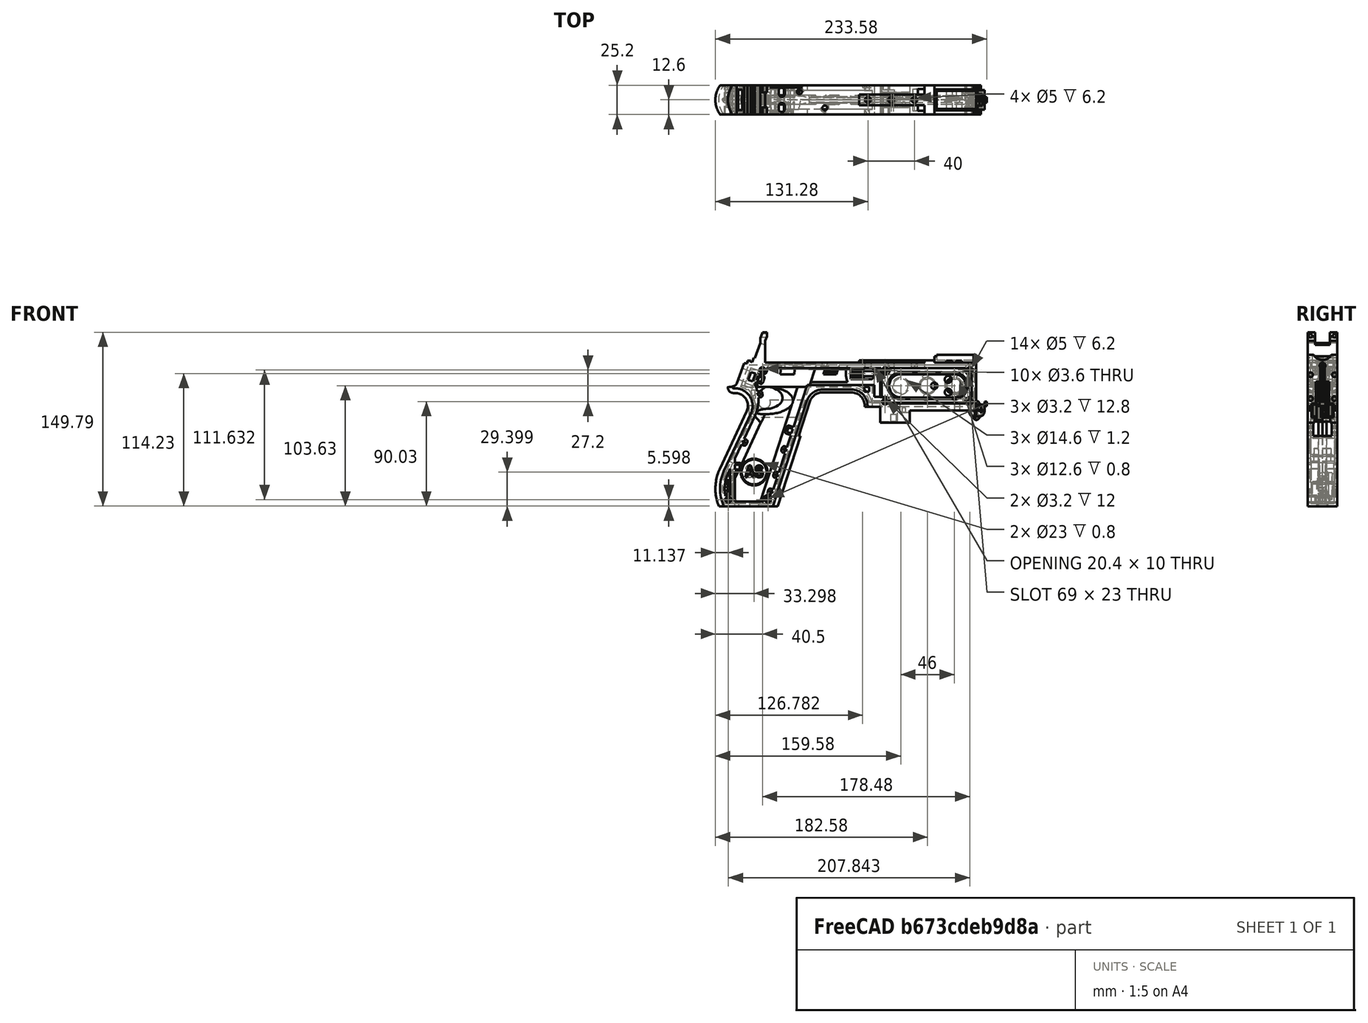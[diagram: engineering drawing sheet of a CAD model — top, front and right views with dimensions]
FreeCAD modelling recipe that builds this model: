
FCSTD DOCUMENT  (FreeCAD 1.0R39319 (Git))
Label: PICON-OF_ver_56
License: All rights reserved
LicenseURL: https://en.wikipedia.org/wiki/All_rights_reserved
objects: Sketcher::SketchObject×124, Part::Extrusion×63, Part::Cut×48, PartDesign::Pad×29, PartDesign::Pocket×21, PartDesign::Chamfer×15, PartDesign::Body×10, PartDesign::Fillet×6, Part::MultiFuse×5, Part::Part2DObjectPython×4, PartDesign::SubtractivePipe×4, PartDesign::SubtractiveLoft×4, PartDesign::Plane×3, PartDesign::SubShapeBinder×2, Part::Sweep×1, PartDesign::ShapeBinder×1, Mesh::Feature×1, PartDesign::Point×1, PartDesign::Groove×1
note: 626 computed .brp shape members not serialized (recipe doc carries the construction recipe); baked Part::Feature solids carry a one-line shape summary decoded from their .brp

FEATURE [Sketcher::SketchObject] Sketch  label="corpo principale"
  ArcFitTolerance = 1e-06
  AttacherType = Attacher::AttachEngine3D
  AttachmentSupport = -> [XZ_Plane]
  FullyConstrained = true
  MakeInternals = false
  MapMode = 5
  Placement = pos=(0,0,0) rot=(1,0,0;1.5708rad)
  sketch-geometry (65):
    g0: LineSegment StartX=0 StartY=0 StartZ=0 EndX=-57.2 EndY=0 EndZ=0
    g1: LineSegment StartX=-57.2 StartY=0 StartZ=0 EndX=-57.2 EndY=-10.4 EndZ=0
    g2: LineSegment StartX=-57.2 StartY=-10.4 StartZ=0 EndX=-82.8 EndY=-10.4 EndZ=0
    g3: LineSegment StartX=-82.8 StartY=-10.4 StartZ=0 EndX=-82.8 EndY=3.2 EndZ=0
    g4: LineSegment StartX=-82.8 StartY=3.2 StartZ=0 EndX=-93.6 EndY=3.2 EndZ=0
    g5: LineSegment StartX=-93.6 StartY=3.2 StartZ=0 EndX=-93.6 EndY=4 EndZ=0
    g6: LineSegment StartX=-107.6 StartY=18 StartZ=0 EndX=-132.428 EndY=18 EndZ=0
    g7: LineSegment StartX=-145.743 StartY=8.32624 StartZ=0 EndX=-175.232 EndY=-82.4316 EndZ=0
    g8: LineSegment StartX=-175.232 StartY=-82.4316 StartZ=0 EndX=-217.232 EndY=-82.4316 EndZ=0
    g9: LineSegment StartX=-217.232 StartY=-52.1862 StartZ=0 EndX=-193.988 EndY=-2.33927 EndZ=0
    g10: LineSegment StartX=-206.196 StartY=23.0857 StartZ=0 EndX=-199.861 EndY=40.4914 EndZ=0
    g11: LineSegment StartX=-199.861 StartY=40.4914 StartZ=0 EndX=-197.061 EndY=40.4914 EndZ=0
    g12: LineSegment StartX=-197.061 StartY=40.4914 StartZ=0 EndX=-197.061 EndY=42.8914 EndZ=0
    g13: LineSegment StartX=-197.061 StartY=42.8914 StartZ=0 EndX=-194.261 EndY=42.8914 EndZ=0
    g14: LineSegment StartX=-194.261 StartY=42.8914 StartZ=0 EndX=-194.535 EndY=42.1397 EndZ=0
    g15: LineSegment StartX=-194.535 StartY=42.1397 StartZ=0 EndX=-193.031 EndY=41.5924 EndZ=0
    g16: LineSegment StartX=-193.031 StartY=41.5924 StartZ=0 EndX=-191.663 EndY=45.3512 EndZ=0
    g17: LineSegment StartX=-191.663 StartY=45.3512 StartZ=0 EndX=-190.536 EndY=44.9408 EndZ=0
    g18: LineSegment StartX=-190.536 StartY=44.9408 StartZ=0 EndX=-185.747 EndY=58.0965 EndZ=0
    g19: LineSegment StartX=-185.747 StartY=58.0965 StartZ=0 EndX=-185.747 EndY=62.0965 EndZ=0
    g20: LineSegment StartX=-185.747 StartY=62.0965 StartZ=0 EndX=-183.832 EndY=67.3588 EndZ=0
    g21: LineSegment StartX=-183.832 StartY=67.3588 StartZ=0 EndX=-180.232 EndY=67.3588 EndZ=0
    g22: LineSegment StartX=-180.232 StartY=67.3588 StartZ=0 EndX=-180.232 EndY=63.7588 EndZ=0
    g23: LineSegment StartX=-180.232 StartY=63.7588 StartZ=0 EndX=-181.6 EndY=60 EndZ=0
    g24: LineSegment StartX=-181.6 StartY=60 StartZ=0 EndX=-181.6 EndY=41.2 EndZ=0
    g25: LineSegment StartX=-181.6 StartY=41.2 StartZ=0 EndX=-100.8 EndY=41.2 EndZ=0
    g26: LineSegment StartX=-36 StartY=43.2 StartZ=0 EndX=-36 EndY=41.2 EndZ=0
    g27: LineSegment StartX=0 StartY=48 StartZ=0 EndX=0 EndY=0 EndZ=0
    g28: LineSegment StartX=-209.901 StartY=19.85 StartZ=0 EndX=-209.901 EndY=20.1 EndZ=0
    g29: LineSegment StartX=-208.001 StartY=22 StartZ=0 EndX=-207.747 EndY=22 EndZ=0
    g30: LineSegment StartX=-207.583 StartY=19 StartZ=0 EndX=-209.051 EndY=19 EndZ=0
    g31: ArcOfCircle CenterX=-208.001 CenterY=20.1 CenterZ=0 NormalX=0 NormalY=0 NormalZ=1 AngleXU=0 Radius=1.9 StartAngle=1.5708 EndAngle=3.14159
    g32: GeomPoint [constr] X=-209.901 Y=22 Z=0
    g33: ArcOfCircle CenterX=-209.051 CenterY=19.85 CenterZ=0 NormalX=0 NormalY=0 NormalZ=1 AngleXU=0 Radius=0.85 StartAngle=3.14159 EndAngle=4.71239
    g34: GeomPoint [constr] X=-209.901 Y=19 Z=0
    g35: ArcOfCircle CenterX=-207.747 CenterY=23.65 CenterZ=0 NormalX=0 NormalY=0 NormalZ=1 AngleXU=0 Radius=1.65 StartAngle=4.71239 EndAngle=5.93412
    g36: GeomPoint [constr] X=-206.591 Y=22 Z=0
    g37: LineSegment StartX=-4 StartY=6 StartZ=0 EndX=-4 EndY=36.4 EndZ=0
    g38: LineSegment StartX=-4 StartY=36.4 StartZ=0 EndX=-185.2 EndY=36.4 EndZ=0
    g39: LineSegment StartX=-185.2 StartY=36.4 StartZ=0 EndX=-190.441 EndY=22 EndZ=0
    g40: LineSegment StartX=-214.575 StartY=-78.4316 StartZ=0 EndX=-178.142 EndY=-78.4316 EndZ=0
    g41: LineSegment StartX=-178.142 StartY=-78.4316 StartZ=0 EndX=-145.51 EndY=22 EndZ=0
    g42: LineSegment StartX=-145.51 StartY=22 StartZ=0 EndX=-87.91 EndY=22 EndZ=0
    g43: LineSegment StartX=-87.91 StartY=22 StartZ=0 EndX=-87.91 EndY=11.6 EndZ=0
    g44: LineSegment StartX=-87.91 StartY=11.6 StartZ=0 EndX=-80.11 EndY=11.6 EndZ=0
    g45: LineSegment StartX=-80.11 StartY=11.6 StartZ=0 EndX=-80.11 EndY=6 EndZ=0
    g46: LineSegment StartX=-80.11 StartY=6 StartZ=0 EndX=-4 EndY=6 EndZ=0
    g47: LineSegment StartX=-190.363 StartY=-4.02975 StartZ=0 EndX=-213.607 EndY=-53.8767 EndZ=0
    g48: ArcOfCircle CenterX=-132.428 CenterY=4 CenterZ=0 NormalX=0 NormalY=0 NormalZ=1 AngleXU=0 Radius=14 StartAngle=1.5708 EndAngle=2.82743
    g49: GeomPoint [constr] X=-142.6 Y=18 Z=0
    g50: ArcOfCircle CenterX=-107.6 CenterY=4 CenterZ=0 NormalX=0 NormalY=0 NormalZ=1 AngleXU=0 Radius=14 StartAngle=0 EndAngle=1.5708
    g51: GeomPoint [constr] X=-93.6 Y=18 Z=0
    g52: ArcOfCircle CenterX=-184.801 CenterY=-67.3089 CenterZ=0 NormalX=0 NormalY=0 NormalZ=1 AngleXU=0 Radius=35.7833 StartAngle=2.70526 EndAngle=3.57792
    g53: ArcOfCircle CenterX=-207.583 CenterY=4 CenterZ=0 NormalX=0 NormalY=0 NormalZ=1 AngleXU=0 Radius=15 StartAngle=5.84685 EndAngle=7.85398
    g54: LineSegment [constr] StartX=-213.607 StartY=-53.8767 StartZ=0 EndX=-217.232 EndY=-52.1862 EndZ=0
    g55: ArcOfCircle CenterX=-184.801 CenterY=-67.3089 CenterZ=0 NormalX=0 NormalY=0 NormalZ=1 AngleXU=0 Radius=31.7833 StartAngle=2.70526 EndAngle=3.49911
    g56: ArcOfCircle CenterX=-218.095 CenterY=8.90192 CenterZ=0 NormalX=0 NormalY=0 NormalZ=1 AngleXU=0 Radius=30.5989 StartAngle=5.84685 EndAngle=6.72553
    g57: LineSegment StartX=-44.6 StartY=43.2 StartZ=0 EndX=-36 EndY=43.2 EndZ=0
    g58: LineSegment StartX=-100.8 StartY=41.2 StartZ=0 EndX=-44.6 EndY=41.2 EndZ=0
    g59: LineSegment StartX=-44.6 StartY=41.2 StartZ=0 EndX=-44.6 EndY=43.2 EndZ=0
    g60: LineSegment StartX=-2.4 StartY=48 StartZ=0 EndX=0 EndY=48 EndZ=0
    g61: LineSegment StartX=-36 StartY=41.2 StartZ=0 EndX=-2.4 EndY=41.2 EndZ=0
    g62: LineSegment StartX=-2.4 StartY=41.2 StartZ=0 EndX=-2.4 EndY=48 EndZ=0
    g63: LineSegment [constr] StartX=-181.6 StartY=36.4 StartZ=0 EndX=-152.209 EndY=36.4 EndZ=0
    g64: LineSegment [constr] StartX=-181.6 StartY=36.4 StartZ=0 EndX=-130.41 EndY=36.4 EndZ=0
  constraints (183):
    c: Coincident(g-1,g0)
    c: PointOnObject(g0,g-1)
    c: Coincident(g0,g1)
    c: Vertical(g1)
    c: Coincident(g1,g2)
    c: Horizontal(g2)
    c: Coincident(g2,g3)
    c: Vertical(g3)
    c: Coincident(g3,g4)
    c: Coincident(g4,g5)
    c: Vertical(g5)
    c: Horizontal(g6)
    c: Coincident(g7,g8)
    c: Horizontal(g8)
    c: Coincident(g10,g11)
    c: Horizontal(g11)
    c: Coincident(g11,g12)
    c: Vertical(g12)
    c: Coincident(g12,g13)
    c: Horizontal(g13)
    c: Coincident(g13,g14)
    c: Coincident(g14,g15)
    c: Coincident(g15,g16)
    c: Coincident(g16,g17)
    c: Coincident(g17,g18)
    c: Coincident(g18,g19)
    c: Vertical(g19)
    c: Coincident(g19,g20)
    c: Coincident(g20,g21)
    c: Horizontal(g21)
    c: Coincident(g21,g22)
    c: Vertical(g22)
    c: Coincident(g22,g23)
    c: Coincident(g23,g24)
    c: Vertical(g24)
    c: Coincident(g24,g25)
    c: Horizontal(g25)
    c: Coincident(g57,g26)
    c: Vertical(g26)
    c: Coincident(g26,g61)
    c: PointOnObject(g60,g-2)
    c: Coincident(g60,g27)
    c: Coincident(g27,g0)
    c: DistanceY(g27,g27) = 48
    c: DistanceY(g1,g1) = 10.4
    c: DistanceX(g0,g0) = 57.2
    c: DistanceX(g2,g2) = 25.6
    c: Horizontal(g4)
    c: DistanceY(g3,g3) = 13.6
    c: DistanceX(g4,g4) = 10.8
    c: DistanceY(g5,g51) = 14.8
    c: DistanceX(g49,g51) = 49
    c: Distance(g7,g49) = 105.6
    c: DistanceX(g61,g60) = 36
    c: DistanceX(g25,g25) = 80.8
    c: DistanceY(g24,g24) = 18.8
    c: DistanceY(g22,g22) = 3.6
    c: Distance(g23) = 4
    c: Angle(g-1,g23) = 1.22173
    c: DistanceX(g21,g21) = 3.6
    c: Distance(g20) = 5.6
    c: Angle(g-1,g20) = 1.22173
    c: DistanceY(g19,g19) = 4
    c: Distance(g18) = 14
    c: Angle(g-1,g18) = 1.22173
    c: Distance(g17) = 1.2
    c: Distance(g16) = 4
    c: Angle(g16) = 1.22173
    c: Perpendicular(g18,g17)
    c: Distance(g15) = 1.6
    c: Perpendicular(g16,g15)
    c: Distance(g14) = 0.8
    c: DistanceX(g13,g13) = 2.8
    c: Perpendicular(g15,g14)
    c: DistanceY(g12,g12) = 2.4
    c: DistanceX(g11,g11) = 2.8
    c: Distance(g9) = 55
    c: Angle(g9,g-1) = 2.00713
    c: Horizontal(g29)
    c: Vertical(g28)
    c: Horizontal(g30)
    c: PointOnObject(g32,g29)
    c: PointOnObject(g32,g28)
    c: Tangent(g29,g31) = 1.5708
    c: Tangent(g28,g31) = 1.5708
    c: PointOnObject(g34,g28)
    c: PointOnObject(g34,g30)
    c: Tangent(g28,g33) = 1.5708
    c: Tangent(g30,g33) = 1.5708
    c: PointOnObject(g36,g29)
    c: PointOnObject(g36,g10)
    c: Tangent(g29,g35) = -1.5708
    c: Tangent(g10,g35) = -1.5708
    c: Angle(g-1,g10) = 1.22173
    c: Radius(g35) = 1.65
    c: Vertical(g37)
    c: Coincident(g37,g38)
    c: Horizontal(g38)
    c: Coincident(g38,g39)
    c: Horizontal(g40)
    c: Coincident(g40,g41)
    c: Coincident(g41,g42)
    c: Horizontal(g42)
    c: Coincident(g42,g43)
    c: Vertical(g43)
    c: Coincident(g43,g44)
    c: Horizontal(g44)
    c: Coincident(g44,g45)
    c: Vertical(g45)
    c: Coincident(g45,g46)
    c: Coincident(g46,g37)
    c: Horizontal(g46)
    c: DistanceY(g0,g37) = 6
    c: DistanceX(g37,g0) = 4
    c: DistanceY(g37,g25) = 4.8
    c: DistanceX(g38,g38) = 181.2
    c: DistanceX(g42,g42) = 57.6
    c: DistanceY(g49,g41) = 4
    c: DistanceX(g41,g49) = 2.91
    c: DistanceY(g43,g43) = 10.4
    c: DistanceX(g44,g44) = 7.8
    c: DistanceY(g7,g40) = 4
    c: Distance(g47) = 55
    c: Angle(g-1,g39) = 1.22173
    c: PointOnObject(g49,g7)
    c: PointOnObject(g49,g6)
    c: Tangent(g7,g48) = -1.5708
    c: Tangent(g6,g48) = -1.5708
    c: PointOnObject(g51,g5)
    c: PointOnObject(g51,g6)
    c: Tangent(g5,g50) = -1.5708
    c: Tangent(g6,g50) = -1.5708
    c: Radius(g50) = 14
    c: Radius(g48) = 14
    c: DistanceX(g8,g8) = 42
    c: Angle(g7,g-1) = 1.88496
    c: Parallel(g41,g7)
    c: Parallel(g47,g9)
    c: Coincident(g52,g8)
    c: Tangent(g52,g9) = 1.5708
    c: DistanceX(g9,g8) = 0
    c: Tangent(g53,g9) = -1.5708
    c: Tangent(g53,g30) = -1.5708
    c: Diameter(g53) = 30
    c: DistanceY(g53,g0) = -4
    c: Coincident(g54,g47)
    c: Distance(g54) = 4
    c: Coincident(g54,g9)
    c: Coincident(g55,g40)
    c: Tangent(g55,g47) = -1.5708
    c: Coincident(g52,g55)
    c: Coincident(g56,g39)
    c: Tangent(g56,g47) = 1.5708
    c: Horizontal(g57)
    c: DistanceX(g57,g57) = 8.6
    c: Coincident(g58,g25)
    c: Horizontal(g58)
    c: Coincident(g59,g58)
    c: Vertical(g59)
    c: DistanceY(g58,g57) = 2
    c: DistanceX(g58,g58) = 56.2
    c: Coincident(g59,g57)
    c: DistanceY(g41,g36) = 0
    c: DistanceY(g36,g39) = 0
    c: DistanceY(g28,g28) = 0.25
    c: DistanceX(g30,g36) = 2.46
    c: DistanceX(g28,g29) = 1.9
    c: Coincident(g62,g60)
    c: Horizontal(g60)
    c: DistanceX(g62,g27) = 2.4
    c: Coincident(g61,g62)
    c: DistanceY(g26,g26) = 2
    c: Vertical(g62)
    c: DistanceY(g61,g60) = 6.8
    c: Horizontal(g61)
    c: Distance(g63) = 29.391
    c: PointOnObject(g63,g38)
    c: PointOnObject(g63,g38)
    c: Distance(g64) = 51.19
    c: PointOnObject(g64,g38)
    c: PointOnObject(g64,g38)
    c: DistanceX(g24,g63) = 0
    c: DistanceX(g24,g64) = 0
FEATURE [Part::Extrusion] Extrude  label="Extrude corpo principale"
  Base = -> Sketch
  Dir = (0,-1,2e-16)
  DirMode = 2
  FaceMakerClass = Part::FaceMakerBullseye
  FaceMakerMode = 3
  LengthFwd = 25.2
  LengthRev = 12.6
  Solid = true
  Symmetric = true
FEATURE [Sketcher::SketchObject] Sketch002  label="scavo grilletto"
  ArcFitTolerance = 1e-06
  AttachmentSupport = -> [XZ_Plane]
  ExternalGeometry = -> [Sketch]
  FullyConstrained = true
  MakeInternals = false
  MapMode = 5
  Placement = pos=(0,0,0) rot=(1,0,0;1.5708rad)
  sketch-geometry (4):
    g0: LineSegment StartX=-89.51 StartY=22 StartZ=0 EndX=-152.71 EndY=22 EndZ=0
    g1: LineSegment StartX=-152.71 StartY=22 StartZ=0 EndX=-167.006 EndY=-22 EndZ=0
    g2: LineSegment StartX=-167.006 StartY=-22 StartZ=0 EndX=-89.51 EndY=-22 EndZ=0
    g3: LineSegment StartX=-89.51 StartY=-22 StartZ=0 EndX=-89.51 EndY=22 EndZ=0
  constraints (12):
    c: Horizontal(g0)
    c: Coincident(g0,g1)
    c: Coincident(g1,g2)
    c: Horizontal(g2)
    c: Coincident(g2,g3)
    c: Coincident(g3,g0)
    c: Vertical(g3)
    c: Angle(g1,g0) = 1.88496
    c: DistanceY(g3,g3) = 44
    c: DistanceX(g0,g0) = 63.2
    c: DistanceX(g0,g-3) = 1.6
    c: DistanceY(g-3,g0) = 0
FEATURE [Sketcher::SketchObject] Sketch004  label="traiettoria arrotondamento impugnatura anteriore"
  ArcFitTolerance = 1e-06
  AttachmentSupport = -> [XZ_Plane]
  ExternalGeometry = -> [Sketch]
  FullyConstrained = true
  MakeInternals = false
  MapMode = 5
  Placement = pos=(0,0,0) rot=(1,0,0;1.5708rad)
  sketch-geometry (13):
    g0: LineSegment StartX=-175.232 StartY=-82.4316 StartZ=0 EndX=-145.743 EndY=8.32624 EndZ=0
    g1: LineSegment StartX=-93.6 StartY=3.2 StartZ=0 EndX=-93.6 EndY=4 EndZ=0
    g2: LineSegment StartX=-132.428 StartY=18 StartZ=0 EndX=-107.6 EndY=18 EndZ=0
    g3: ArcOfCircle CenterX=-132.428 CenterY=4 CenterZ=0 NormalX=0 NormalY=0 NormalZ=1 AngleXU=0 Radius=14 StartAngle=1.5708 EndAngle=2.82743
    g4: ArcOfCircle CenterX=-107.6 CenterY=4 CenterZ=0 NormalX=0 NormalY=0 NormalZ=1 AngleXU=0 Radius=14 StartAngle=0 EndAngle=1.5708
    g5: LineSegment StartX=-175.232 StartY=-82.4316 StartZ=0 EndX=-217.232 EndY=-82.4316 EndZ=0
    g6: LineSegment StartX=-217.232 StartY=-52.1862 StartZ=0 EndX=-193.988 EndY=-2.33927 EndZ=0
    g7: LineSegment StartX=-209.051 StartY=19 StartZ=0 EndX=-207.583 EndY=19 EndZ=0
    g8: LineSegment StartX=-209.901 StartY=20.1 StartZ=0 EndX=-209.901 EndY=19.85 EndZ=0
    g9: ArcOfCircle CenterX=-184.801 CenterY=-67.3089 CenterZ=0 NormalX=0 NormalY=0 NormalZ=1 AngleXU=0 Radius=35.7833 StartAngle=2.70526 EndAngle=3.57792
    g10: ArcOfCircle CenterX=-207.583 CenterY=4 CenterZ=0 NormalX=0 NormalY=0 NormalZ=1 AngleXU=0 Radius=15 StartAngle=5.84685 EndAngle=7.85398
    g11: ArcOfCircle CenterX=-209.051 CenterY=19.85 CenterZ=0 NormalX=0 NormalY=0 NormalZ=1 AngleXU=0 Radius=0.85 StartAngle=3.14159 EndAngle=4.71239
    g12: ArcOfCircle CenterX=-208.001 CenterY=20.1 CenterZ=0 NormalX=0 NormalY=0 NormalZ=1 AngleXU=0 Radius=1.9 StartAngle=1.5708 EndAngle=3.14159
  constraints (26):
    c: Coincident(g0,g-3)
    c: Coincident(g0,g-6)
    c: Coincident(g1,g-8)
    c: Coincident(g1,g-7)
    c: Coincident(g2,g-5)
    c: Coincident(g2,g-4)
    c: Coincident(g3,g2)
    c: Tangent(g3,g0) = 1.5708
    c: Coincident(g4,g1)
    c: Tangent(g4,g2) = 1.5708
    c: Coincident(g5,g0)
    c: Coincident(g5,g-9)
    c: Coincident(g6,g-12)
    c: Coincident(g6,g-11)
    c: Coincident(g7,g-15)
    c: Coincident(g7,g-14)
    c: Coincident(g8,g-16)
    c: Coincident(g8,g-17)
    c: Tangent(g9,g6) = 1.5708
    c: Coincident(g9,g5)
    c: Coincident(g10,g7)
    c: Tangent(g10,g6) = -1.5708
    c: Tangent(g11,g7) = -1.5708
    c: Coincident(g11,g8)
    c: Tangent(g12,g8) = -1.5708
    c: Coincident(g12,g-17)
FEATURE [PartDesign::Plane] DatumPlane  label="Piano per disegno arrotondamento impugnatura"
  AttachmentSupport = -> [Sketch]
  Length = 73.6581
  MapMode = 7
  Placement = pos=(-145.743,1.8e-15,8.32624) rot=(0.154555,0.154555,0.97582;1.59527rad)
  ResizeMode = 0
  Width = 303.511
FEATURE [Sketcher::SketchObject] Sketch005  label="forma arrotondamento impugnatura anteriore"
  ArcFitTolerance = 1e-06
  AttachmentSupport = -> [DatumPlane]
  FullyConstrained = true
  MakeInternals = false
  MapMode = 5
  Placement = pos=(-145.743,1.8e-15,8.32624) rot=(0.154555,0.154555,0.97582;1.59527rad)
  sketch-geometry (5):
    g0: GeomPoint [constr] X=0 Y=-4 Z=0
    g1: GeomPoint [constr] X=-12.6 Y=7.1e-15 Z=0
    g2: GeomPoint [constr] X=12.6 Y=4.97e-14 Z=0
    g3: LineSegment StartX=-12.6 StartY=7.1e-15 StartZ=0 EndX=12.6 EndY=4.97e-14 EndZ=0
    g4: ArcOfCircle CenterX=-3.88e-14 CenterY=17.845 CenterZ=0 NormalX=0 NormalY=0 NormalZ=1 AngleXU=0 Radius=21.845 StartAngle=4.09759 EndAngle=5.32718
  constraints (11):
    c: DistanceY(g0,g-1) = 4
    c: DistanceX(g-1,g0) = 0
    c: DistanceX(g1,g-1) = 12.6
    c: DistanceX(g-1,g2) = 12.6
    c: DistanceY(g-1,g2) = 0
    c: DistanceY(g-1,g1) = 0
    c: Coincident(g3,g1)
    c: Coincident(g3,g2)
    c: Coincident(g4,g1)
    c: Coincident(g4,g2)
    c: PointOnObject(g0,g4)
FEATURE [Part::Sweep] Sweep  label="Sweep impugnatura"
  Frenet = true
  Sections = -> [Sketch005]
  Solid = true
  Spine = -> Sketch [Edge32,Edge33,Edge34,Edge35,Edge36,Edge37,Edge38,Edge39,Edge40,Edge41,Edge42,Edge43,Edge44]
  Transition = 1
FEATURE [Sketcher::SketchObject] Sketch008  label="buchi e pulizie varie"
  ArcFitTolerance = 1e-06
  AttachmentSupport = -> [XZ_Plane]
  ExternalGeometry = -> [Sketch]
  FullyConstrained = true
  MakeInternals = false
  MapMode = 5
  Placement = pos=(0,0,0) rot=(1,0,0;1.5708rad)
  sketch-geometry (26):
    g0: LineSegment StartX=-96.278 StartY=20.155 StartZ=0 EndX=-92.278 EndY=20.155 EndZ=0
    g1: LineSegment StartX=-92.278 StartY=20.155 StartZ=0 EndX=-92.278 EndY=16.155 EndZ=0
    g2: LineSegment StartX=-92.278 StartY=16.155 StartZ=0 EndX=-96.278 EndY=16.155 EndZ=0
    g3: LineSegment StartX=-96.278 StartY=16.155 StartZ=0 EndX=-96.278 EndY=20.155 EndZ=0
    g4: LineSegment StartX=-222.232 StartY=-82.4316 StartZ=0 EndX=-170.232 EndY=-82.4316 EndZ=0
    g5: LineSegment StartX=-170.232 StartY=-82.4316 StartZ=0 EndX=-170.232 EndY=-86.4316 EndZ=0
    g6: LineSegment StartX=-170.232 StartY=-86.4316 StartZ=0 EndX=-222.232 EndY=-86.4316 EndZ=0
    g7: LineSegment StartX=-222.232 StartY=-86.4316 StartZ=0 EndX=-222.232 EndY=-82.4316 EndZ=0
    g8: LineSegment StartX=-213.901 StartY=20.1 StartZ=0 EndX=-213.901 EndY=26 EndZ=0
    g9: LineSegment StartX=-213.901 StartY=26 StartZ=0 EndX=-206.196 EndY=26 EndZ=0
    g10: LineSegment StartX=-17.4 StartY=42.8 StartZ=0 EndX=-12.4 EndY=42.8 EndZ=0
    g11: LineSegment StartX=-12.4 StartY=42.8 StartZ=0 EndX=-12.4 EndY=41.2 EndZ=0
    g12: LineSegment StartX=-12.4 StartY=41.2 StartZ=0 EndX=-17.4 EndY=41.2 EndZ=0
    g13: LineSegment StartX=-17.4 StartY=41.2 StartZ=0 EndX=-17.4 EndY=42.8 EndZ=0
    g14: LineSegment StartX=-25.9 StartY=42.8 StartZ=0 EndX=-20.9 EndY=42.8 EndZ=0
    g15: LineSegment StartX=-20.9 StartY=42.8 StartZ=0 EndX=-20.9 EndY=41.2 EndZ=0
    g16: LineSegment StartX=-20.9 StartY=41.2 StartZ=0 EndX=-25.9 EndY=41.2 EndZ=0
    g17: LineSegment StartX=-25.9 StartY=41.2 StartZ=0 EndX=-25.9 EndY=42.8 EndZ=0
    g18: GeomPoint [constr] X=-206.196 Y=23.0857 Z=0
    g19: GeomPoint [constr] X=-213.901 Y=20.1 Z=0
    g20: BSplineCurve PolesCount=4 KnotsCount=2 Degree=3 IsPeriodic=0
    g21-g24: Circle [constr] x4 (B-spline internal-alignment scaffolding for g20; pole/knot coordinates omitted)
    g25: LineSegment StartX=-206.196 StartY=26 StartZ=0 EndX=-206.196 EndY=23.0857 EndZ=0
  constraints (73):
    c: Horizontal(g0)
    c: Coincident(g1,g0)
    c: Vertical(g1)
    c: Coincident(g2,g1)
    c: Horizontal(g2)
    c: Coincident(g3,g2)
    c: Coincident(g3,g0)
    c: Vertical(g3)
    c: DistanceX(g0,g-4) = 4.368
    c: DistanceY(g0,g-4) = 1.845
    c: DistanceY(g1,g1) = 4
    c: DistanceX(g2,g2) = 4
    c: Horizontal(g4)
    c: Coincident(g5,g4)
    c: Vertical(g5)
    c: Coincident(g6,g5)
    c: Horizontal(g6)
    c: Coincident(g7,g6)
    c: Coincident(g7,g4)
    c: Vertical(g7)
    c: DistanceY(g7,g7) = 4
    c: DistanceX(g4,g-5) = 5
    c: DistanceX(g-5,g4) = 5
    c: DistanceY(g4,g-5) = 0
    c: Coincident(g9,g8)
    c: Parallel(g9,g-6)
    c: DistanceX(g8,g-8) = 4
    c: Horizontal(g10)
    c: Coincident(g11,g10)
    c: Vertical(g11)
    c: Coincident(g12,g11)
    c: Horizontal(g12)
    c: Coincident(g13,g12)
    c: Coincident(g13,g10)
    c: Vertical(g13)
    c: Horizontal(g14)
    c: Coincident(g15,g14)
    c: Vertical(g15)
    c: Coincident(g16,g15)
    c: Horizontal(g16)
    c: Coincident(g17,g16)
    c: Coincident(g17,g14)
    c: Vertical(g17)
    c: DistanceY(g11,g10) = 1.6
    c: DistanceX(g10,g10) = 5
    c: DistanceY(g15,g14) = 1.6
    c: DistanceX(g14,g14) = 5
    c: DistanceX(g15,g12) = 3.5
    c: DistanceX(g11,g-9) = 10
    c: DistanceY(g-9,g11) = 0
    c: DistanceY(g-9,g15) = 0
    c: Perpendicular(g8,g9)
    c: DistanceY(g-7,g9) = 4
    c: DistanceY(g8,g-8) = 0
    c: InternalAlignment(g18,g20)
    c: InternalAlignment(g19,g20)
    c: InternalAlignment(g21,g20)
    c: Weight(g21) = 1
    c: InternalAlignment(g22,g20)
    c: Equal(g22,g21)
    c: InternalAlignment(g23,g20)
    c: Equal(g23,g21)
    c: InternalAlignment(g24,g20)
    c: Equal(g24,g21)
    c: Coincident(g18,g-12)
    c: Coincident(g19,g8)
    c: Coincident(g25,g9)
    c: Coincident(g25,g20)
    c: Vertical(g25)
    c: DistanceY(g20,g23) = 0
    c: DistanceY(g22,g18) = 2.26
    c: DistanceX(g22,g18) = 0.93
    c: DistanceX(g20,g23) = 2.9
FEATURE [Part::Extrusion] Extrude004  label="Extrude Buchi e pulizie varie"
  Base = -> Sketch008
  Dir = (0,-1,2e-16)
  DirMode = 2
  FaceMakerClass = Part::FaceMakerBullseye
  FaceMakerMode = 3
  LengthFwd = 25.2
  LengthRev = 0
  Solid = true
  Symmetric = true
FEATURE [Sketcher::SketchObject] Sketch009  label="rinforzi"
  ArcFitTolerance = 1e-06
  AttachmentSupport = -> [XZ_Plane]
  ExternalGeometry = -> [Sketch]
  FullyConstrained = true
  MakeInternals = false
  MapMode = 5
  Placement = pos=(0,0,0) rot=(1,0,0;1.5708rad)
  sketch-geometry (9):
    g0: LineSegment StartX=-87.91 StartY=22 StartZ=0 EndX=-87.91 EndY=36.4 EndZ=0
    g1: LineSegment StartX=-87.91 StartY=36.4 StartZ=0 EndX=-97.91 EndY=36.4 EndZ=0
    g2: LineSegment StartX=-97.91 StartY=36.4 StartZ=0 EndX=-97.91 EndY=22 EndZ=0
    g3: LineSegment StartX=-97.91 StartY=22 StartZ=0 EndX=-87.91 EndY=22 EndZ=0
    g4: LineSegment StartX=-149.713 StartY=9.06563 StartZ=0 EndX=-154.586 EndY=-5.93437 EndZ=0
    g5: LineSegment StartX=-154.586 StartY=-5.93437 StartZ=0 EndX=-191.863 EndY=-5.93437 EndZ=0
    g6: LineSegment StartX=-191.863 StartY=-5.93437 StartZ=0 EndX=-191.863 EndY=9.06563 EndZ=0
    g7: LineSegment StartX=-191.863 StartY=9.06563 StartZ=0 EndX=-149.713 EndY=9.06563 EndZ=0
    g8: LineSegment [constr] StartX=-145.51 StartY=22 StartZ=0 EndX=-149.713 EndY=9.06563 EndZ=0
  constraints (25):
    c: Vertical(g0)
    c: Coincident(g1,g0)
    c: Horizontal(g1)
    c: Coincident(g2,g1)
    c: Vertical(g2)
    c: Coincident(g3,g2)
    c: Coincident(g3,g0)
    c: Horizontal(g3)
    c: Coincident(g0,g-4)
    c: DistanceX(g3,g3) = 10
    c: DistanceY(g0,g-3) = 0
    c: Coincident(g5,g4)
    c: Horizontal(g5)
    c: Coincident(g6,g5)
    c: Vertical(g6)
    c: Coincident(g7,g6)
    c: Coincident(g7,g4)
    c: Horizontal(g7)
    c: Distance(g8) = 13.6
    c: Parallel(g-6,g8)
    c: Coincident(g-6,g8)
    c: Parallel(g4,g-6)
    c: DistanceY(g4,g4) = 15
    c: Coincident(g4,g8)
    c: DistanceX(g-5,g5) = -1.5
FEATURE [Part::Extrusion] Extrude001  label="Extrude scavo grilletto"
  Base = -> Sketch002
  Dir = (0,-1,2e-16)
  DirMode = 2
  FaceMakerClass = Part::FaceMakerBullseye
  FaceMakerMode = 3
  LengthFwd = 16
  LengthRev = 0
  Solid = true
  Symmetric = true
FEATURE [Part::Extrusion] Extrude005  label="Extrude Rinforzi"
  Base = -> Sketch009
  Dir = (0,-1,2e-16)
  DirMode = 2
  FaceMakerClass = Part::FaceMakerBullseye
  FaceMakerMode = 3
  LengthFwd = 2
  LengthRev = 0
  Placement = pos=(0,12.6,0) rot=(0,0,1;0rad)
  Solid = true
  Symmetric = false
FEATURE [PartDesign::ShapeBinder] CopyCut
  TraceSupport = false
FEATURE [PartDesign::Plane] DatumPlane001
  AttachmentSupport = -> [CopyCut]
  Length = 283.944
  MapMode = 5
  Placement = pos=(0,12.6,0) rot=(0,0.707107,0.707107;3.14159rad)
  ResizeMode = 0
  Width = 188.15
FEATURE [Sketcher::SketchObject] Sketch010  label="buco neopixel"
  ArcFitTolerance = 1e-06
  AttachmentSupport = -> [XZ_Plane]
  ExternalGeometry = -> [Sketch]
  FullyConstrained = true
  MakeInternals = false
  MapMode = 5
  Placement = pos=(0,0,0) rot=(1,0,0;1.5708rad)
  sketch-geometry (5):
    g0: LineSegment [constr] StartX=-199.861 StartY=40.4914 StartZ=0 EndX=-201.368 EndY=36.3521 EndZ=0
    g1: LineSegment StartX=-201.368 StartY=36.3521 StartZ=0 EndX=-204.932 EndY=26.5605 EndZ=0
    g2: LineSegment StartX=-201.368 StartY=36.3521 StartZ=0 EndX=-180.2 EndY=28.6477 EndZ=0
    g3: LineSegment StartX=-180.2 StartY=28.6477 StartZ=0 EndX=-183.764 EndY=18.8561 EndZ=0
    g4: LineSegment StartX=-183.764 StartY=18.8561 StartZ=0 EndX=-204.932 EndY=26.5605 EndZ=0
  constraints (14):
    c: Parallel(g0,g-3)
    c: Distance(g0) = 4.405
    c: Coincident(g0,g-3)
    c: Coincident(g2,g1)
    c: Coincident(g3,g2)
    c: Coincident(g4,g3)
    c: Coincident(g4,g1)
    c: Parallel(g1,g-3)
    c: Distance(g1) = 10.42
    c: Coincident(g1,g0)
    c: Parallel(g2,g4)
    c: Perpendicular(g1,g2)
    c: DistanceX(g-4,g2) = 5
    c: Parallel(g3,g1)
FEATURE [Part::Extrusion] Extrude006  label="Extrude buco neopixel"
  Base = -> Sketch010
  Dir = (0,-1,2e-16)
  DirMode = 2
  FaceMakerClass = Part::FaceMakerBullseye
  FaceMakerMode = 3
  LengthFwd = 17.2
  LengthRev = 0
  Solid = true
  Symmetric = true
FEATURE [Sketcher::SketchObject] Sketch011  label="fermo grilletto"
  ArcFitTolerance = 1e-06
  AttachmentSupport = -> [XZ_Plane]
  ExternalGeometry = -> [Sketch]
  FullyConstrained = true
  MakeInternals = false
  MapMode = 5
  Placement = pos=(0,0,0) rot=(1,0,0;1.5708rad)
  sketch-geometry (18):
    g0: LineSegment [constr] StartX=-145.51 StartY=22 StartZ=0 EndX=-157.347 EndY=-14.4293 EndZ=0
    g1: LineSegment [constr] StartX=-157.347 StartY=-14.4293 StartZ=0 EndX=-157.841 EndY=-15.951 EndZ=0
    g2: LineSegment StartX=-161.151 StartY=-13.1932 StartZ=0 EndX=-155.825 EndY=-14.9237 EndZ=0
    g3: LineSegment StartX=-163.167 StartY=-14.2205 StartZ=0 EndX=-164.403 EndY=-18.0247 EndZ=0
    g4: LineSegment StartX=-163.376 StartY=-20.0408 StartZ=0 EndX=-158.05 EndY=-21.7713 EndZ=0
    g5: LineSegment StartX=-158.05 StartY=-21.7713 StartZ=0 EndX=-155.825 EndY=-14.9237 EndZ=0
    g6: LineSegment StartX=-161.645 StartY=-14.7149 StartZ=0 EndX=-157.841 EndY=-15.951 EndZ=0
    g7: LineSegment StartX=-157.841 StartY=-15.951 StartZ=0 EndX=-159.077 EndY=-19.7552 EndZ=0
    g8: LineSegment StartX=-159.077 StartY=-19.7552 StartZ=0 EndX=-162.881 EndY=-18.5191 EndZ=0
    g9: LineSegment StartX=-162.881 StartY=-18.5191 StartZ=0 EndX=-161.645 EndY=-14.7149 EndZ=0
    g10: LineSegment [constr] StartX=-161.645 StartY=-14.7149 StartZ=0 EndX=-161.151 EndY=-13.1932 EndZ=0
    g11: LineSegment [constr] StartX=-159.077 StartY=-19.7552 StartZ=0 EndX=-157.555 EndY=-20.2496 EndZ=0
    g12: LineSegment [constr] StartX=-159.077 StartY=-19.7552 StartZ=0 EndX=-159.572 EndY=-21.2769 EndZ=0
    g13: LineSegment [constr] StartX=-161.645 StartY=-14.7149 StartZ=0 EndX=-163.167 EndY=-14.2205 EndZ=0
    g14: ArcOfCircle CenterX=-161.645 CenterY=-14.7149 CenterZ=0 NormalX=0 NormalY=0 NormalZ=1 AngleXU=0 Radius=1.6 StartAngle=1.25664 EndAngle=2.82743
    g15: GeomPoint [constr] X=-162.673 Y=-12.6988 Z=0
    g16: ArcOfCircle CenterX=-162.881 CenterY=-18.5191 CenterZ=0 NormalX=0 NormalY=0 NormalZ=1 AngleXU=0 Radius=1.6 StartAngle=2.82743 EndAngle=4.39823
    g17: GeomPoint [constr] X=-164.897 Y=-19.5464 Z=0
  constraints (48):
    c: Parallel(g0,g-3)
    c: Distance(g0) = 38.304
    c: Coincident(g0,g-3)
    c: Parallel(g1,g-3)
    c: Distance(g1) = 1.6
    c: Coincident(g1,g0)
    c: Coincident(g5,g4)
    c: Coincident(g5,g2)
    c: Coincident(g7,g6)
    c: Coincident(g8,g7)
    c: Coincident(g9,g8)
    c: Coincident(g9,g6)
    c: Parallel(g7,g-3)
    c: Parallel(g9,g7)
    c: Perpendicular(g6,g7)
    c: Parallel(g6,g8)
    c: Distance(g6) = 4
    c: Distance(g9) = 4
    c: Parallel(g5,g7)
    c: Parallel(g9,g3)
    c: Parallel(g2,g6)
    c: Parallel(g4,g8)
    c: Parallel(g13,g6)
    c: Parallel(g10,g9)
    c: Parallel(g11,g8)
    c: Parallel(g12,g7)
    c: Distance(g10) = 1.6
    c: Distance(g13) = 1.6
    c: Distance(g12) = 1.6
    c: Distance(g11) = 1.6
    c: Coincident(g10,g6)
    c: Coincident(g13,g6)
    c: Coincident(g12,g7)
    c: Coincident(g11,g7)
    c: Distance(g10,g15) = 1.6
    c: Distance(g15,g13) = 1.6
    c: Distance(g4,g12) = 1.6
    c: Distance(g4,g11) = 1.6
    c: PointOnObject(g15,g2)
    c: Tangent(g3,g14) = -1.5708
    c: Tangent(g2,g14) = 1.5708
    c: PointOnObject(g17,g4)
    c: PointOnObject(g17,g3)
    c: Tangent(g4,g16) = -1.5708
    c: Tangent(g3,g16) = -1.5708
    c: Equal(g16,g14)
    c: Coincident(g16,g8)
    c: Coincident(g6,g1)
FEATURE [Part::Extrusion] Extrude007  label="Extrude fermo grilletto"
  Base = -> Sketch011
  Dir = (0,-1,2e-16)
  DirMode = 2
  FaceMakerClass = Part::FaceMakerBullseye
  FaceMakerMode = 3
  LengthFwd = 25.2
  LengthRev = 0
  Solid = true
  Symmetric = true
FEATURE [Sketcher::SketchObject] Sketch012  label="buco oled"
  ArcFitTolerance = 1e-06
  AttachmentSupport = -> [XZ_Plane]
  ExternalGeometry = -> [Sketch]
  FullyConstrained = true
  MakeInternals = false
  MapMode = 5
  Placement = pos=(0,0,0) rot=(1,0,0;1.5708rad)
  sketch-geometry (4):
    g0: LineSegment StartX=-185.747 StartY=58.0965 StartZ=0 EndX=-180.232 EndY=56.0891 EndZ=0
    g1: LineSegment StartX=-185.747 StartY=58.0965 StartZ=0 EndX=-185.747 EndY=67.3588 EndZ=0
    g2: LineSegment StartX=-185.747 StartY=67.3588 StartZ=0 EndX=-180.232 EndY=67.3588 EndZ=0
    g3: LineSegment StartX=-180.232 StartY=67.3588 StartZ=0 EndX=-180.232 EndY=56.0891 EndZ=0
  constraints (10):
    c: Coincident(g1,g0)
    c: Coincident(g2,g1)
    c: Coincident(g3,g2)
    c: Coincident(g3,g0)
    c: Parallel(g1,g-5)
    c: Perpendicular(g-3,g0)
    c: Parallel(g2,g-6)
    c: Parallel(g3,g-4)
    c: Coincident(g0,g-5)
    c: Coincident(g2,g-6)
FEATURE [Part::Extrusion] Extrude008  label="Extrude buco oled"
  Base = -> Sketch012
  Dir = (0,-1,2e-16)
  DirMode = 2
  FaceMakerClass = Part::FaceMakerBullseye
  FaceMakerMode = 3
  LengthFwd = 12.8
  LengthRev = 0
  Solid = true
  Symmetric = true
FEATURE [Sketcher::SketchObject] Sketch013  label="buco pompa"
  ArcFitTolerance = 1e-06
  AttachmentSupport = -> [XZ_Plane]
  ExternalGeometry = -> [Sketch]
  FullyConstrained = true
  MakeInternals = false
  MapMode = 5
  Placement = pos=(0,0,0) rot=(1,0,0;1.5708rad)
  sketch-geometry (8):
    g0: LineSegment StartX=-82.8 StartY=-10.4 StartZ=0 EndX=-82.8 EndY=-9.6 EndZ=0
    g1: LineSegment StartX=-82.8 StartY=-9.6 StartZ=0 EndX=-67.9 EndY=-9.6 EndZ=0
    g2: LineSegment StartX=-67.9 StartY=-9.6 StartZ=0 EndX=-67.9 EndY=6 EndZ=0
    g3: LineSegment StartX=-67.9 StartY=6 StartZ=0 EndX=-65.9 EndY=6 EndZ=0
    g4: LineSegment StartX=-65.9 StartY=6 StartZ=0 EndX=-65.9 EndY=-1.7 EndZ=0
    g5: LineSegment StartX=-65.9 StartY=-1.7 StartZ=0 EndX=-57.2 EndY=-1.7 EndZ=0
    g6: LineSegment StartX=-57.2 StartY=-1.7 StartZ=0 EndX=-57.2 EndY=-10.4 EndZ=0
    g7: LineSegment StartX=-57.2 StartY=-10.4 StartZ=0 EndX=-82.8 EndY=-10.4 EndZ=0
  constraints (22):
    c: Vertical(g0)
    c: Coincident(g1,g0)
    c: Horizontal(g1)
    c: Coincident(g2,g1)
    c: Vertical(g2)
    c: Coincident(g3,g2)
    c: Horizontal(g3)
    c: Coincident(g4,g3)
    c: Vertical(g4)
    c: Coincident(g5,g4)
    c: Horizontal(g5)
    c: Coincident(g6,g5)
    c: Vertical(g6)
    c: Coincident(g7,g6)
    c: Coincident(g7,g0)
    c: DistanceY(g0,g0) = 0.8
    c: DistanceY(g6,g6) = 8.7
    c: DistanceX(g1,g1) = 14.9
    c: DistanceX(g3,g3) = 2
    c: Coincident(g0,g-4)
    c: DistanceY(g2,g-6) = 0
    c: Coincident(g6,g-5)
FEATURE [Part::Extrusion] Extrude009  label="Extrude buco pompa"
  Base = -> Sketch013
  Dir = (0,-1,2e-16)
  DirMode = 2
  FaceMakerClass = Part::FaceMakerBullseye
  FaceMakerMode = 3
  LengthFwd = 13.2
  LengthRev = 0
  Solid = true
  Symmetric = true
FEATURE [Sketcher::SketchObject] Sketch014  label="buco frontale"
  ArcFitTolerance = 1e-06
  AttachmentSupport = -> [XZ_Plane]
  ExternalGeometry = -> [Sketch]
  FullyConstrained = true
  MakeInternals = false
  MapMode = 5
  Placement = pos=(0,0,0) rot=(1,0,0;1.5708rad)
  sketch-geometry (10):
    g0: LineSegment StartX=0 StartY=0 StartZ=0 EndX=0 EndY=24.671 EndZ=0
    g1: LineSegment StartX=0 StartY=24.671 StartZ=0 EndX=-4 EndY=24.671 EndZ=0
    g2: LineSegment StartX=-4 StartY=24.671 StartZ=0 EndX=-4 EndY=16 EndZ=0
    g3: LineSegment StartX=-4 StartY=16 StartZ=0 EndX=-2.4 EndY=16 EndZ=0
    g4: LineSegment StartX=-2.4 StartY=16 StartZ=0 EndX=-2.4 EndY=10 EndZ=0
    g5: LineSegment StartX=-2.4 StartY=10 StartZ=0 EndX=-12 EndY=10 EndZ=0
    g6: LineSegment StartX=-12 StartY=10 StartZ=0 EndX=-12 EndY=6 EndZ=0
    g7: LineSegment StartX=-12 StartY=6 StartZ=0 EndX=-2.4 EndY=6 EndZ=0
    g8: LineSegment StartX=-2.4 StartY=6 StartZ=0 EndX=-2.4 EndY=0 EndZ=0
    g9: LineSegment StartX=-2.4 StartY=0 StartZ=0 EndX=0 EndY=0 EndZ=0
  constraints (29):
    c: Vertical(g0)
    c: Coincident(g1,g0)
    c: Horizontal(g1)
    c: Coincident(g2,g1)
    c: Vertical(g2)
    c: Coincident(g3,g2)
    c: Horizontal(g3)
    c: Coincident(g4,g3)
    c: Vertical(g4)
    c: Coincident(g5,g4)
    c: Horizontal(g5)
    c: Coincident(g6,g5)
    c: Vertical(g6)
    c: Coincident(g7,g6)
    c: Coincident(g8,g7)
    c: Vertical(g8)
    c: Coincident(g9,g8)
    c: Coincident(g9,g0)
    c: Horizontal(g9)
    c: DistanceY(g0,g0) = 24.671
    c: Horizontal(g7)
    c: DistanceY(g6,g6) = 4
    c: DistanceY(g4,g4) = 6
    c: DistanceX(g9,g9) = 2.4
    c: Coincident(g0,g-1)
    c: DistanceY(g-3,g7) = 0
    c: DistanceX(g8,g4) = 0
    c: DistanceX(g-3,g1) = 0
    c: DistanceX(g6,g-3) = 8
FEATURE [Part::Extrusion] Extrude010  label="Extrude buco frontale"
  Base = -> Sketch014
  Dir = (0,-1,2e-16)
  DirMode = 2
  FaceMakerClass = Part::FaceMakerBullseye
  FaceMakerMode = 3
  LengthFwd = 11.2
  LengthRev = 0
  Solid = true
  Symmetric = true
FEATURE [Sketcher::SketchObject] Sketch015  label="guida rail"
  ArcFitTolerance = 1e-06
  AttachmentSupport = -> [XZ_Plane]
  ExternalGeometry = -> [Sketch]
  FullyConstrained = true
  MakeInternals = false
  MapMode = 5
  Placement = pos=(0,0,0) rot=(1,0,0;1.5708rad)
  sketch-geometry (4):
    g0: LineSegment StartX=-100.8 StartY=43.2 StartZ=0 EndX=-44.6 EndY=43.2 EndZ=0
    g1: LineSegment StartX=-44.6 StartY=43.2 StartZ=0 EndX=-44.6 EndY=41.2 EndZ=0
    g2: LineSegment StartX=-44.6 StartY=41.2 StartZ=0 EndX=-100.8 EndY=41.2 EndZ=0
    g3: LineSegment StartX=-100.8 StartY=41.2 StartZ=0 EndX=-100.8 EndY=43.2 EndZ=0
  constraints (9):
    c: Horizontal(g0)
    c: Coincident(g1,g0)
    c: Coincident(g2,g1)
    c: Coincident(g3,g2)
    c: Coincident(g3,g0)
    c: Vertical(g3)
    c: Coincident(g2,g-3)
    c: Coincident(g1,g-3)
    c: Coincident(g0,g-4)
FEATURE [Part::Extrusion] Extrude011  label="Extrude guida rail"
  Base = -> Sketch015
  Dir = (0,-1,2e-16)
  DirMode = 2
  FaceMakerClass = Part::FaceMakerBullseye
  FaceMakerMode = 3
  LengthFwd = 9
  LengthRev = 0
  Solid = true
  Symmetric = true
FEATURE [Sketcher::SketchObject] Sketch016  label="guide per coperture laterali"
  ArcFitTolerance = 1e-06
  AttachmentSupport = -> [XZ_Plane]
  ExternalGeometry = -> [Sketch]
  FullyConstrained = true
  MakeInternals = false
  MapMode = 5
  Placement = pos=(0,0,0) rot=(1,0,0;1.5708rad)
  sketch-geometry (14):
    g0: Circle CenterX=-5.6 CenterY=7.6 CenterZ=0 NormalX=0 NormalY=0 NormalZ=1 AngleXU=0 Radius=1.6
    g1: Circle CenterX=-5.6 CenterY=7.6 CenterZ=0 NormalX=0 NormalY=0 NormalZ=1 AngleXU=0 Radius=4
    g2: Circle CenterX=-5.6 CenterY=34.8 CenterZ=0 NormalX=0 NormalY=0 NormalZ=1 AngleXU=0 Radius=1.6
    g3: Circle CenterX=-5.6 CenterY=34.8 CenterZ=0 NormalX=0 NormalY=0 NormalZ=1 AngleXU=0 Radius=4
    g4: Circle CenterX=-184.08 CenterY=34.8 CenterZ=0 NormalX=0 NormalY=0 NormalZ=1 AngleXU=0 Radius=1.6
    g5: Circle CenterX=-184.08 CenterY=34.8 CenterZ=0 NormalX=0 NormalY=0 NormalZ=1 AngleXU=0 Radius=4
    g6: Circle CenterX=-179.305 CenterY=-76.8316 CenterZ=0 NormalX=0 NormalY=0 NormalZ=1 AngleXU=0 Radius=1.6
    g7: Circle CenterX=-179.305 CenterY=-76.8316 CenterZ=0 NormalX=0 NormalY=0 NormalZ=1 AngleXU=0 Radius=4
    g8: Circle CenterX=-213.443 CenterY=-76.8316 CenterZ=0 NormalX=0 NormalY=0 NormalZ=1 AngleXU=0 Radius=1.6
    g9: Circle CenterX=-213.443 CenterY=-76.8316 CenterZ=0 NormalX=0 NormalY=0 NormalZ=1 AngleXU=0 Radius=4
    g10: Circle CenterX=-78.51 CenterY=7.6 CenterZ=0 NormalX=0 NormalY=0 NormalZ=1 AngleXU=0 Radius=1.6
    g11: Circle CenterX=-78.51 CenterY=7.6 CenterZ=0 NormalX=0 NormalY=0 NormalZ=1 AngleXU=0 Radius=4
    g12: Circle CenterX=-78.51 CenterY=34.8 CenterZ=0 NormalX=0 NormalY=0 NormalZ=1 AngleXU=0 Radius=1.6
    g13: Circle CenterX=-78.51 CenterY=34.8 CenterZ=0 NormalX=0 NormalY=0 NormalZ=1 AngleXU=0 Radius=4
  constraints (35):
    c: Diameter(g0) = 3.2
    c: Diameter(g1) = 8
    c: Coincident(g0,g1)
    c: Diameter(g2) = 3.2
    c: Diameter(g3) = 8
    c: Coincident(g3,g2)
    c: Tangent(g2,g-7)
    c: Diameter(g4) = 3.2
    c: Diameter(g5) = 8
    c: Coincident(g5,g4)
    c: Tangent(g4,g-7)
    c: Tangent(g4,g-8)
    c: Diameter(g6) = 3.2
    c: Diameter(g7) = 8
    c: Coincident(g7,g6)
    c: Tangent(g6,g-9)
    c: Tangent(g6,g-10)
    c: Diameter(g8) = 3.2
    c: Diameter(g9) = 8
    c: Coincident(g9,g8)
    c: Tangent(g8,g-10)
    c: Tangent(g8,g-11)
    c: Diameter(g10) = 3.2
    c: Diameter(g11) = 8
    c: Diameter(g12) = 3.2
    c: Diameter(g13) = 8
    c: Coincident(g12,g13)
    c: Coincident(g10,g11)
    c: Tangent(g12,g-7)
    c: DistanceX(g12,g10) = 0
    c: Tangent(g2,g-6)
    c: Tangent(g0,g-6)
    c: Tangent(g0,g-3)
    c: Tangent(g10,g-3)
    c: Tangent(g10,g-4)
FEATURE [Part::Extrusion] Extrude012  label="extrude guide per coperture laterali"
  Base = -> Sketch016
  Dir = (0,-1,2e-16)
  DirMode = 2
  FaceMakerClass = Part::FaceMakerBullseye
  FaceMakerMode = 3
  LengthFwd = 25.2
  LengthRev = 0
  Solid = true
  Symmetric = true
FEATURE [Sketcher::SketchObject] Sketch017  label="supporto CAM"
  ArcFitTolerance = 1e-06
  AttachmentSupport = -> [XZ_Plane]
  ExternalGeometry = -> [Sketch]
  FullyConstrained = true
  MakeInternals = false
  MapMode = 5
  Placement = pos=(0,0,0) rot=(1,0,0;1.5708rad)
  sketch-geometry (6):
    g0: LineSegment StartX=-2.4 StartY=48 StartZ=0 EndX=-2.4 EndY=41.2 EndZ=0
    g1: LineSegment StartX=-2.4 StartY=48 StartZ=0 EndX=-34 EndY=48 EndZ=0
    g2: LineSegment StartX=-34 StartY=48 StartZ=0 EndX=-34 EndY=46.72 EndZ=0
    g3: LineSegment StartX=-34 StartY=46.72 StartZ=0 EndX=-36 EndY=46.72 EndZ=0
    g4: LineSegment StartX=-36 StartY=46.72 StartZ=0 EndX=-36 EndY=41.2 EndZ=0
    g5: LineSegment StartX=-36 StartY=41.2 StartZ=0 EndX=-2.4 EndY=41.2 EndZ=0
  constraints (15):
    c: Coincident(g1,g0)
    c: Horizontal(g1)
    c: Coincident(g2,g1)
    c: Vertical(g2)
    c: Coincident(g3,g2)
    c: Horizontal(g3)
    c: Coincident(g4,g3)
    c: Coincident(g5,g4)
    c: DistanceX(g1,g0) = 31.6
    c: Coincident(g5,g0)
    c: Vertical(g4)
    c: DistanceY(g2,g1) = 1.28
    c: Coincident(g0,g-3)
    c: Coincident(g0,g-3)
    c: Coincident(g4,g-4)
FEATURE [Part::Extrusion] Extrude013  label="Extrude supporto CAM"
  Base = -> Sketch017
  Dir = (0,-1,2e-16)
  DirMode = 2
  FaceMakerClass = Part::FaceMakerBullseye
  FaceMakerMode = 3
  LengthFwd = 17.8
  LengthRev = 0
  Solid = true
  Symmetric = true
FEATURE [Sketcher::SketchObject] Sketch018  label="Scavo CAM"
  ArcFitTolerance = 1e-06
  AttachmentSupport = -> [YZ_Plane]
  ExternalGeometry = -> [Sketch]
  FullyConstrained = true
  MakeInternals = false
  MapMode = 5
  Placement = pos=(0,0,0) rot=(0.57735,0.57735,0.57735;2.0944rad)
  sketch-geometry (4):
    g0: LineSegment StartX=-7.73 StartY=48 StartZ=0 EndX=7.73 EndY=48 EndZ=0
    g1: LineSegment [constr] StartX=1.07e-14 StartY=48 StartZ=0 EndX=0 EndY=43.5155 EndZ=0
    g2: ArcOfCircle CenterX=9e-15 CenterY=52.42 CenterZ=0 NormalX=0 NormalY=0 NormalZ=1 AngleXU=0 Radius=8.90445 StartAngle=3.66102 EndAngle=5.76376
    g3: Circle [constr] CenterX=9e-15 CenterY=52.42 CenterZ=0 NormalX=0 NormalY=0 NormalZ=1 AngleXU=0 Radius=8.9
  constraints (13):
    c: Horizontal(g0)
    c: DistanceY(g-3,g0) = 0
    c: DistanceX(g0,g0) = 15.46
    c: DistanceX(g0,g-3) = 7.73
    c: DistanceX(g-3) = 0
    c: Coincident(g1,g-3)
    c: PointOnObject(g1,g-2)
    c: Coincident(g2,g0)
    c: Coincident(g2,g0)
    c: PointOnObject(g1,g2)
    c: Diameter(g3) = 17.8
    c: DistanceY(g1,g3) = 4.42
    c: Coincident(g2,g3)
FEATURE [Part::Extrusion] Extrude014  label="Extrude Scavo CAM"
  Base = -> Sketch018
  Dir = (1,0,0)
  DirMode = 2
  FaceMakerClass = Part::FaceMakerBullseye
  FaceMakerMode = 3
  LengthFwd = -34
  LengthRev = 0
  Solid = true
  Symmetric = false
FEATURE [Sketcher::SketchObject] Sketch019  label="scavo rumble"
  ArcFitTolerance = 1e-06
  AttachmentSupport = -> [XZ_Plane]
  ExternalGeometry = -> [Sketch]
  FullyConstrained = true
  MakeInternals = false
  MapMode = 5
  Placement = pos=(0,0,0) rot=(1,0,0;1.5708rad)
  sketch-geometry (6):
    g0: LineSegment StartX=-169.087 StartY=-38.264 StartZ=0 EndX=-163.951 EndY=-39.9327 EndZ=0
    g1: LineSegment StartX=-163.951 StartY=-39.9327 StartZ=0 EndX=-171.058 EndY=-61.807 EndZ=0
    g2: LineSegment StartX=-171.058 StartY=-61.807 StartZ=0 EndX=-176.194 EndY=-60.1383 EndZ=0
    g3: LineSegment StartX=-176.194 StartY=-60.1383 StartZ=0 EndX=-169.087 EndY=-38.264 EndZ=0
    g4: LineSegment [constr] StartX=-145.51 StartY=22 StartZ=0 EndX=-165.472 EndY=-39.4383 EndZ=0
    g5: LineSegment [constr] StartX=-163.951 StartY=-39.9327 StartZ=0 EndX=-165.472 EndY=-39.4383 EndZ=0
  constraints (17):
    c: Coincident(g1,g0)
    c: Coincident(g2,g1)
    c: Coincident(g3,g2)
    c: Coincident(g3,g0)
    c: Parallel(g3,g-3)
    c: Parallel(g3,g1)
    c: Perpendicular(g3,g0)
    c: Perpendicular(g2,g3)
    c: Distance(g2,g0) = 23
    c: Parallel(g4,g-3)
    c: Distance(g4) = 64.6
    c: Coincident(g4,g-3)
    c: Parallel(g5,g0)
    c: Coincident(g5,g0)
    c: Coincident(g5,g4)
    c: Distance(g4,g0) = 3.8
    c: Distance(g4,g0) = 1.6
FEATURE [Part::Extrusion] Extrude015  label="scavo rumble001"
  Base = -> Sketch019
  Dir = (0,-1,2e-16)
  DirMode = 2
  FaceMakerClass = Part::FaceMakerBullseye
  FaceMakerMode = 3
  LengthFwd = 21
  LengthRev = 0
  Solid = true
  Symmetric = true
FEATURE [Sketcher::SketchObject] Sketch020  label="fermo rumble"
  ArcFitTolerance = 1e-06
  AttachmentSupport = -> [XZ_Plane]
  ExternalGeometry = -> [Sketch019,Sketch]
  FullyConstrained = true
  MakeInternals = false
  MapMode = 5
  Placement = pos=(0,0,0) rot=(1,0,0;1.5708rad)
  sketch-geometry (16):
    g0: LineSegment [constr] StartX=-171.22 StartY=-57.1279 StartZ=0 EndX=-172.58 EndY=-61.3126 EndZ=0
    g1: LineSegment [constr] StartX=-172.58 StartY=-61.3126 StartZ=0 EndX=-171.058 EndY=-61.807 EndZ=0
    g2: LineSegment StartX=-172.633 StartY=-54.3557 StartZ=0 EndX=-170.54 EndY=-55.0356 EndZ=0
    g3: LineSegment StartX=-170.54 StartY=-55.0356 StartZ=0 EndX=-171.22 EndY=-57.1279 EndZ=0
    g4: LineSegment StartX=-171.22 StartY=-57.1279 StartZ=0 EndX=-173.313 EndY=-56.4481 EndZ=0
    g5: LineSegment StartX=-173.313 StartY=-56.4481 StartZ=0 EndX=-172.633 EndY=-54.3557 EndZ=0
    g6: LineSegment StartX=-172.138 StartY=-52.8341 StartZ=0 EndX=-168.714 EndY=-53.9465 EndZ=0
    g7: LineSegment StartX=-168.714 StartY=-53.9465 StartZ=0 EndX=-170.321 EndY=-58.892 EndZ=0
    g8: LineSegment StartX=-170.321 StartY=-58.892 StartZ=0 EndX=-173.745 EndY=-57.7795 EndZ=0
    g9: LineSegment StartX=-174.772 StartY=-55.7634 StartZ=0 EndX=-174.154 EndY=-53.8613 EndZ=0
    g10: LineSegment [constr] StartX=-174.154 StartY=-53.8613 StartZ=0 EndX=-173.66 EndY=-52.3396 EndZ=0
    g11: LineSegment [constr] StartX=-173.66 StartY=-52.3396 StartZ=0 EndX=-172.138 EndY=-52.8341 EndZ=0
    g12: ArcOfCircle CenterX=-173.251 CenterY=-56.2579 CenterZ=0 NormalX=0 NormalY=0 NormalZ=1 AngleXU=0 Radius=1.6 StartAngle=2.82743 EndAngle=4.39823
    g13: GeomPoint [constr] X=-175.267 Y=-57.2851 Z=0
    g14: ArcOfCircle CenterX=-172.633 CenterY=-54.3557 CenterZ=0 NormalX=0 NormalY=0 NormalZ=1 AngleXU=0 Radius=1.6 StartAngle=1.25664 EndAngle=2.82743
    g15: GeomPoint [constr] X=-173.66 Y=-52.3396 Z=0
  constraints (42):
    c: Parallel(g0,g-4)
    c: Distance(g0) = 4.4
    c: Coincident(g1,g0)
    c: Perpendicular(g0,g1)
    c: Distance(g1) = 1.6
    c: Coincident(g1,g-5)
    c: Coincident(g3,g2)
    c: Coincident(g4,g3)
    c: Coincident(g5,g4)
    c: Coincident(g5,g2)
    c: Parallel(g3,g-4)
    c: Parallel(g3,g5)
    c: Perpendicular(g2,g3)
    c: Parallel(g4,g2)
    c: Distance(g2) = 2.2
    c: Distance(g3) = 2.2
    c: Coincident(g7,g6)
    c: Coincident(g8,g7)
    c: Parallel(g7,g-4)
    c: Parallel(g7,g9)
    c: Perpendicular(g6,g7)
    c: Parallel(g6,g8)
    c: Distance(g6,g15) = 5.2
    c: Distance(g7) = 5.2
    c: Coincident(g11,g10)
    c: Parallel(g10,g9)
    c: Parallel(g11,g6)
    c: Distance(g10) = 1.6
    c: Distance(g11) = 1.6
    c: Coincident(g10,g15)
    c: Distance(g11,g2) = 1.6
    c: Distance(g2,g10) = 1.6
    c: PointOnObject(g13,g8)
    c: PointOnObject(g13,g9)
    c: Tangent(g8,g12) = 1.5708
    c: Tangent(g9,g12) = 1.5708
    c: PointOnObject(g15,g9)
    c: Tangent(g6,g14) = 1.5708
    c: Tangent(g9,g14) = 1.5708
    c: Equal(g12,g14)
    c: Coincident(g6,g11)
    c: Coincident(g3,g0)
FEATURE [Part::Extrusion] Extrude016  label="Extrude fermo rumble"
  Base = -> Sketch020
  Dir = (0,-1,2e-16)
  DirMode = 2
  FaceMakerClass = Part::FaceMakerBullseye
  FaceMakerMode = 3
  LengthFwd = 25.2
  LengthRev = 0
  Solid = true
  Symmetric = true
FEATURE [Sketcher::SketchObject] Sketch021  label="perno fermo rumble001"
  ArcFitTolerance = 1e-06
  AttachmentSupport = -> [XZ_Plane001]
  FullyConstrained = true
  MakeInternals = false
  MapMode = 5
  Placement = pos=(0,0,0) rot=(1,0,0;1.5708rad)
  sketch-geometry (16):
    g0: LineSegment StartX=0 StartY=0.45 StartZ=0 EndX=0 EndY=1.55 EndZ=0
    g1: LineSegment StartX=0.45 StartY=2 StartZ=0 EndX=1.55 EndY=2 EndZ=0
    g2: LineSegment StartX=2 StartY=1.55 StartZ=0 EndX=2 EndY=0.45 EndZ=0
    g3: LineSegment StartX=1.55 StartY=0 StartZ=0 EndX=0.45 EndY=0 EndZ=0
    g4: ArcOfCircle [constr] CenterX=0.45 CenterY=1.55 CenterZ=0 NormalX=0 NormalY=0 NormalZ=1 AngleXU=0 Radius=0.45 StartAngle=1.5708 EndAngle=3.14159
    g5: GeomPoint [constr] X=0 Y=2 Z=0
    g6: LineSegment StartX=0.45 StartY=2 StartZ=0 EndX=0 EndY=1.55 EndZ=0
    g7: ArcOfCircle [constr] CenterX=1.55 CenterY=1.55 CenterZ=0 NormalX=0 NormalY=0 NormalZ=1 AngleXU=0 Radius=0.45 StartAngle=0 EndAngle=1.5708
    g8: GeomPoint [constr] X=2 Y=2 Z=0
    g9: LineSegment StartX=2 StartY=1.55 StartZ=0 EndX=1.55 EndY=2 EndZ=0
    g10: ArcOfCircle [constr] CenterX=1.55 CenterY=0.45 CenterZ=0 NormalX=0 NormalY=0 NormalZ=1 AngleXU=0 Radius=0.45 StartAngle=4.71239 EndAngle=6.28319
    g11: GeomPoint [constr] X=2 Y=0 Z=0
    g12: LineSegment StartX=1.55 StartY=0 StartZ=0 EndX=2 EndY=0.45 EndZ=0
    g13: ArcOfCircle [constr] CenterX=0.45 CenterY=0.45 CenterZ=0 NormalX=0 NormalY=0 NormalZ=1 AngleXU=0 Radius=0.45 StartAngle=3.14159 EndAngle=4.71239
    g14: GeomPoint [constr] X=0 Y=0 Z=0
    g15: LineSegment StartX=0 StartY=0.45 StartZ=0 EndX=0.45 EndY=0 EndZ=0
  constraints (35):
    c: Coincident(g14,g-1)
    c: PointOnObject(g5,g-2)
    c: Horizontal(g1)
    c: Vertical(g2)
    c: Horizontal(g3)
    c: DistanceX(g5,g8) = 2
    c: DistanceY(g11,g8) = 2
    c: PointOnObject(g5,g0)
    c: PointOnObject(g5,g1)
    c: Tangent(g0,g4) = 1.5708
    c: Tangent(g1,g4) = 1.5708
    c: Coincident(g6,g0)
    c: Coincident(g6,g1)
    c: PointOnObject(g8,g2)
    c: PointOnObject(g8,g1)
    c: Tangent(g2,g7) = 1.5708
    c: Tangent(g1,g7) = 1.5708
    c: Coincident(g9,g2)
    c: Coincident(g9,g1)
    c: PointOnObject(g11,g2)
    c: PointOnObject(g11,g3)
    c: Tangent(g2,g10) = 1.5708
    c: Tangent(g3,g10) = 1.5708
    c: Coincident(g12,g2)
    c: Coincident(g12,g3)
    c: PointOnObject(g14,g0)
    c: PointOnObject(g14,g3)
    c: Tangent(g0,g13) = 1.5708
    c: Tangent(g3,g13) = 1.5708
    c: Coincident(g15,g0)
    c: Coincident(g15,g3)
    c: Equal(g6,g9)
    c: Equal(g9,g12)
    c: Equal(g12,g15)
    c: DistanceX(g14,g3) = 0.45
FEATURE [Sketcher::SketchObject] Sketch022  label="fori per M3x5(OD)x6(L)"
  ArcFitTolerance = 1e-06
  AttachmentSupport = -> [XZ_Plane]
  ExternalGeometry = -> [Sketch016]
  FullyConstrained = true
  MakeInternals = false
  MapMode = 5
  Placement = pos=(0,0,0) rot=(1,0,0;1.5708rad)
  sketch-geometry (7):
    g0: Circle CenterX=-5.6 CenterY=34.8 CenterZ=0 NormalX=0 NormalY=0 NormalZ=1 AngleXU=0 Radius=2.5
    g1: Circle CenterX=-5.6 CenterY=7.6 CenterZ=0 NormalX=0 NormalY=0 NormalZ=1 AngleXU=0 Radius=2.5
    g2: Circle CenterX=-78.51 CenterY=34.8 CenterZ=0 NormalX=0 NormalY=0 NormalZ=1 AngleXU=0 Radius=2.5
    g3: Circle CenterX=-78.51 CenterY=7.6 CenterZ=0 NormalX=0 NormalY=0 NormalZ=1 AngleXU=0 Radius=2.5
    g4: Circle CenterX=-184.08 CenterY=34.8 CenterZ=0 NormalX=0 NormalY=0 NormalZ=1 AngleXU=0 Radius=2.5
    g5: Circle CenterX=-179.305 CenterY=-76.8316 CenterZ=0 NormalX=0 NormalY=0 NormalZ=1 AngleXU=0 Radius=2.5
    g6: Circle CenterX=-213.443 CenterY=-76.8316 CenterZ=0 NormalX=0 NormalY=0 NormalZ=1 AngleXU=0 Radius=2.5
  constraints (14):
    c: Diameter(g0) = 5
    c: Diameter(g1) = 5
    c: Diameter(g2) = 5
    c: Diameter(g3) = 5
    c: Diameter(g4) = 5
    c: Diameter(g5) = 5
    c: Diameter(g6) = 5
    c: Coincident(g0,g-8)
    c: Coincident(g1,g-9)
    c: Coincident(g2,g-6)
    c: Coincident(g3,g-7)
    c: Coincident(g4,g-5)
    c: Coincident(g5,g-4)
    c: Coincident(g6,g-3)
FEATURE [Part::Extrusion] Extrude018  label="Extrude fori M3x5x6 - dx"
  Base = -> Sketch022
  Dir = (0,-1,2e-16)
  DirMode = 2
  FaceMakerClass = Part::FaceMakerBullseye
  FaceMakerMode = 3
  LengthFwd = 6.2
  LengthRev = 0
  Placement = pos=(0,-9.5,0) rot=(0,0,1;0rad)
  Solid = true
  Symmetric = true
FEATURE [Part::Extrusion] Extrude019  label="Extrude fori M3x5x6 - sx"
  Base = -> Sketch022
  Dir = (0,-1,2e-16)
  DirMode = 2
  FaceMakerClass = Part::FaceMakerBullseye
  FaceMakerMode = 3
  LengthFwd = 6.2
  LengthRev = 0
  Placement = pos=(0,9.5,0) rot=(0,0,1;0rad)
  Solid = true
  Symmetric = true
FEATURE [Sketcher::SketchObject] Sketch023  label="foro anteriore M3x5x6"
  ArcFitTolerance = 1e-06
  AttachmentSupport = -> [YZ_Plane]
  FullyConstrained = true
  MakeInternals = false
  MapMode = 5
  Placement = pos=(0,0,0) rot=(0.57735,0.57735,0.57735;2.0944rad)
  sketch-geometry (2):
    g0: LineSegment [constr] StartX=0 StartY=0 StartZ=0 EndX=0 EndY=38.6 EndZ=0
    g1: Circle CenterX=0 CenterY=38.6 CenterZ=0 NormalX=0 NormalY=0 NormalZ=1 AngleXU=0 Radius=2.5
  constraints (5):
    c: Coincident(g0,g-1)
    c: PointOnObject(g0,g-2)
    c: DistanceY(g0,g0) = 38.6
    c: Diameter(g1) = 5
    c: Coincident(g1,g0)
FEATURE [Part::Extrusion] Extrude020  label="Extrude foro anteriore M3x5x6"
  Base = -> Sketch023
  Dir = (1,0,0)
  DirMode = 2
  FaceMakerClass = Part::FaceMakerBullseye
  FaceMakerMode = 3
  LengthFwd = -6.2
  LengthRev = 0
  Solid = true
  Symmetric = false
FEATURE [Sketcher::SketchObject] Sketch024  label="fori per viti frontale"
  ArcFitTolerance = 1e-06
  AttachmentSupport = -> [YZ_Plane]
  FullyConstrained = true
  MakeInternals = false
  MapMode = 5
  Placement = pos=(0,0,0) rot=(0.57735,0.57735,0.57735;2.0944rad)
  sketch-geometry (9):
    g0: LineSegment [constr] StartX=-10.3 StartY=30.721 StartZ=0 EndX=10.3 EndY=30.721 EndZ=0
    g1: LineSegment [constr] StartX=10.3 StartY=30.721 StartZ=0 EndX=10.3 EndY=10.121 EndZ=0
    g2: LineSegment [constr] StartX=10.3 StartY=10.121 StartZ=0 EndX=-10.3 EndY=10.121 EndZ=0
    g3: LineSegment [constr] StartX=-10.3 StartY=10.121 StartZ=0 EndX=-10.3 EndY=30.721 EndZ=0
    g4: LineSegment [constr] StartX=0 StartY=0 StartZ=0 EndX=0 EndY=10.121 EndZ=0
    g5: Circle CenterX=-10.3 CenterY=30.721 CenterZ=0 NormalX=0 NormalY=0 NormalZ=1 AngleXU=0 Radius=2
    g6: Circle CenterX=10.3 CenterY=30.721 CenterZ=0 NormalX=0 NormalY=0 NormalZ=1 AngleXU=0 Radius=2
    g7: Circle CenterX=-10.3 CenterY=10.121 CenterZ=0 NormalX=0 NormalY=0 NormalZ=1 AngleXU=0 Radius=2
    g8: Circle CenterX=10.3 CenterY=10.121 CenterZ=0 NormalX=0 NormalY=0 NormalZ=1 AngleXU=0 Radius=2
  constraints (22):
    c: Horizontal(g0)
    c: Coincident(g1,g0)
    c: Vertical(g1)
    c: Coincident(g2,g1)
    c: Horizontal(g2)
    c: Coincident(g3,g2)
    c: Coincident(g3,g0)
    c: Vertical(g3)
    c: DistanceX(g0,g0) = 20.6
    c: DistanceY(g3,g3) = 20.6
    c: Coincident(g4,g-1)
    c: PointOnObject(g4,g-2)
    c: DistanceY(g4,g4) = 10.121
    c: Symmetric(g2,g2,g4)
    c: Diameter(g5) = 4
    c: Diameter(g6) = 4
    c: Diameter(g7) = 4
    c: Diameter(g8) = 4
    c: Coincident(g5,g0)
    c: Coincident(g6,g0)
    c: Coincident(g7,g2)
    c: Coincident(g8,g1)
FEATURE [Part::Extrusion] Extrude021  label="Extrude fori per viti frontale"
  Base = -> Sketch024
  Dir = (1,0,0)
  DirMode = 2
  FaceMakerClass = Part::FaceMakerBullseye
  FaceMakerMode = 3
  LengthFwd = -2.4
  LengthRev = 0
  Solid = true
  Symmetric = false
FEATURE [Sketcher::SketchObject] Sketch025  label="foro per filo CAM"
  ArcFitTolerance = 1e-06
  AttachmentSupport = -> [XZ_Plane]
  ExternalGeometry = -> [Sketch]
  FullyConstrained = true
  MakeInternals = false
  MapMode = 5
  Placement = pos=(0,0,0) rot=(1,0,0;1.5708rad)
  sketch-geometry (4):
    g0: LineSegment StartX=-44.6 StartY=41.2 StartZ=0 EndX=-44.6 EndY=36.4 EndZ=0
    g1: LineSegment StartX=-44.6 StartY=36.4 StartZ=0 EndX=-54.6 EndY=36.4 EndZ=0
    g2: LineSegment StartX=-54.6 StartY=36.4 StartZ=0 EndX=-50.4 EndY=41.2 EndZ=0
    g3: LineSegment StartX=-50.4 StartY=41.2 StartZ=0 EndX=-44.6 EndY=41.2 EndZ=0
  constraints (11):
    c: Vertical(g0)
    c: Coincident(g1,g0)
    c: Horizontal(g1)
    c: Coincident(g2,g1)
    c: Coincident(g3,g2)
    c: Coincident(g3,g0)
    c: Horizontal(g3)
    c: Coincident(g0,g-3)
    c: DistanceY(g0,g-4) = 0
    c: DistanceX(g3,g3) = 5.8
    c: DistanceX(g1,g1) = 10
FEATURE [Part::Extrusion] Extrude022  label="Extrude foro per filo CAM dx"
  Base = -> Sketch025
  Dir = (0,-1,2e-16)
  DirMode = 2
  FaceMakerClass = Part::FaceMakerBullseye
  FaceMakerMode = 3
  LengthFwd = 4.9
  LengthRev = 0
  Placement = pos=(0,6.95,0) rot=(0,0,1;0rad)
  Solid = true
  Symmetric = true
FEATURE [Part::Extrusion] Extrude023  label="Extrude foro per filo CAM sx"
  Base = -> Sketch025
  Dir = (0,-1,2e-16)
  DirMode = 2
  FaceMakerClass = Part::FaceMakerBullseye
  FaceMakerMode = 3
  LengthFwd = 4.9
  LengthRev = 0
  Placement = pos=(0,-6.95,0) rot=(0,0,1;0rad)
  Solid = true
  Symmetric = true
FEATURE [Sketcher::SketchObject] Sketch026  label="foro sotto anteriore M3x5x6"
  ArcFitTolerance = 1e-06
  AttachmentSupport = -> [XY_Plane]
  FullyConstrained = true
  MakeInternals = false
  MapMode = 5
  sketch-geometry (2):
    g0: LineSegment [constr] StartX=0 StartY=0 StartZ=0 EndX=-16.5 EndY=0 EndZ=0
    g1: Circle CenterX=-16.5 CenterY=0 CenterZ=0 NormalX=0 NormalY=0 NormalZ=1 AngleXU=0 Radius=2.5
  constraints (5):
    c: Distance(g0) = 16.5
    c: Coincident(g0,g-1)
    c: PointOnObject(g0,g-1)
    c: Diameter(g1) = 5
    c: Coincident(g0,g1)
FEATURE [Sketcher::SketchObject] Sketch027  label="foro sotto posteriore M3x5x6"
  ArcFitTolerance = 1e-06
  AttachmentSupport = -> [XY_Plane]
  ExternalGeometry = -> [Sketch]
  FullyConstrained = true
  MakeInternals = false
  MapMode = 5
  sketch-geometry (2):
    g0: LineSegment [constr] StartX=-82.8 StartY=2e-16 StartZ=0 EndX=-71.3 EndY=2e-16 EndZ=0
    g1: Circle CenterX=-71.3 CenterY=2e-16 CenterZ=0 NormalX=0 NormalY=0 NormalZ=1 AngleXU=0 Radius=2.5
  constraints (5):
    c: Distance(g0) = 11.5
    c: Coincident(g0,g-3)
    c: PointOnObject(g0,g-3)
    c: Diameter(g1) = 5
    c: Coincident(g1,g0)
FEATURE [Sketcher::SketchObject] Sketch029  label="fori sotto impugnatura"
  ArcFitTolerance = 1e-06
  AttachmentSupport = -> [XY_Plane]
  ExternalGeometry = -> [Sketch]
  FullyConstrained = true
  MakeInternals = false
  MapMode = 5
  sketch-geometry (15):
    g0: LineSegment [constr] StartX=-175.232 StartY=-1.83e-14 StartZ=0 EndX=-191.232 EndY=0 EndZ=0
    g1: Circle CenterX=-191.232 CenterY=0 CenterZ=0 NormalX=0 NormalY=0 NormalZ=1 AngleXU=0 Radius=3.95
    g2: LineSegment [constr] StartX=-175.232 StartY=-1.83e-14 StartZ=0 EndX=-204.275 EndY=0 EndZ=0
    g3: LineSegment StartX=-204.275 StartY=3.525 StartZ=0 EndX=-204.275 EndY=-3.525 EndZ=0
    g4: LineSegment StartX=-205.4 StartY=-4.65 StartZ=0 EndX=-206.65 EndY=-4.65 EndZ=0
    g5: LineSegment StartX=-207.775 StartY=-3.525 StartZ=0 EndX=-207.775 EndY=3.525 EndZ=0
    g6: LineSegment StartX=-206.65 StartY=4.65 StartZ=0 EndX=-205.4 EndY=4.65 EndZ=0
    g7: ArcOfCircle CenterX=-206.65 CenterY=3.525 CenterZ=0 NormalX=0 NormalY=0 NormalZ=1 AngleXU=0 Radius=1.125 StartAngle=1.5708 EndAngle=3.14159
    g8: GeomPoint [constr] X=-207.775 Y=4.65 Z=0
    g9: ArcOfCircle CenterX=-205.4 CenterY=3.525 CenterZ=0 NormalX=0 NormalY=0 NormalZ=1 AngleXU=0 Radius=1.125 StartAngle=0 EndAngle=1.5708
    g10: GeomPoint [constr] X=-204.275 Y=4.65 Z=0
    g11: ArcOfCircle CenterX=-205.4 CenterY=-3.525 CenterZ=0 NormalX=0 NormalY=0 NormalZ=1 AngleXU=0 Radius=1.125 StartAngle=4.71239 EndAngle=6.28319
    g12: GeomPoint [constr] X=-204.275 Y=-4.65 Z=0
    g13: ArcOfCircle CenterX=-206.65 CenterY=-3.525 CenterZ=0 NormalX=0 NormalY=0 NormalZ=1 AngleXU=0 Radius=1.125 StartAngle=3.14159 EndAngle=4.71239
    g14: GeomPoint [constr] X=-207.775 Y=-4.65 Z=0
  constraints (35):
    c: Distance(g0) = 16
    c: Coincident(g0,g-3)
    c: PointOnObject(g0,g-1)
    c: Diameter(g1) = 7.9
    c: Coincident(g1,g0)
    c: Coincident(g2,g0)
    c: PointOnObject(g2,g-1)
    c: Vertical(g3)
    c: Horizontal(g4)
    c: Vertical(g5)
    c: Horizontal(g6)
    c: DistanceY(g12,g10) = 9.3
    c: DistanceX(g8,g10) = 3.5
    c: Symmetric(g10,g12,g2)
    c: PointOnObject(g8,g5)
    c: PointOnObject(g8,g6)
    c: Tangent(g5,g7) = 1.5708
    c: Tangent(g6,g7) = 1.5708
    c: PointOnObject(g10,g3)
    c: PointOnObject(g10,g6)
    c: Tangent(g3,g9) = 1.5708
    c: Tangent(g6,g9) = 1.5708
    c: PointOnObject(g12,g3)
    c: PointOnObject(g12,g4)
    c: Tangent(g3,g11) = 1.5708
    c: Tangent(g4,g11) = 1.5708
    c: PointOnObject(g14,g4)
    c: PointOnObject(g14,g5)
    c: Tangent(g4,g13) = 1.5708
    c: Tangent(g5,g13) = 1.5708
    c: Equal(g7,g9)
    c: Equal(g9,g11)
    c: Equal(g11,g13)
    c: DistanceX(g6,g6) = 1.25
    c: DistanceX(g-5,g5) = 6.8
FEATURE [Sketcher::SketchObject] Sketch030  label="fori superiori per solenoide e oled"
  ArcFitTolerance = 1e-06
  AttachmentSupport = -> [XY_Plane]
  ExternalGeometry = -> [Sketch]
  FullyConstrained = true
  MakeInternals = false
  MapMode = 5
  sketch-geometry (33):
    g0: LineSegment [constr] StartX=-181.6 StartY=1.12e-14 StartZ=0 EndX=-169.91 EndY=0 EndZ=0
    g1: LineSegment [constr] StartX=-169.91 StartY=0 StartZ=0 EndX=-169.91 EndY=-2.6 EndZ=0
    g2: LineSegment [constr] StartX=-169.91 StartY=0 StartZ=0 EndX=-169.91 EndY=2.6 EndZ=0
    g3: LineSegment StartX=-169.91 StartY=4.975 StartZ=0 EndX=-169.91 EndY=8.225 EndZ=0
    g4: LineSegment StartX=-167.535 StartY=10.6 StartZ=0 EndX=-167.285 EndY=10.6 EndZ=0
    g5: LineSegment StartX=-164.91 StartY=8.225 StartZ=0 EndX=-164.91 EndY=4.975 EndZ=0
    g6: LineSegment StartX=-167.285 StartY=2.6 StartZ=0 EndX=-167.535 EndY=2.6 EndZ=0
    g7: LineSegment StartX=-169.91 StartY=-4.975 StartZ=0 EndX=-169.91 EndY=-8.225 EndZ=0
    g8: LineSegment StartX=-167.535 StartY=-10.6 StartZ=0 EndX=-167.285 EndY=-10.6 EndZ=0
    g9: LineSegment StartX=-164.91 StartY=-8.225 StartZ=0 EndX=-164.91 EndY=-4.975 EndZ=0
    g10: LineSegment StartX=-167.285 StartY=-2.6 StartZ=0 EndX=-167.535 EndY=-2.6 EndZ=0
    g11: ArcOfCircle CenterX=-167.535 CenterY=8.225 CenterZ=0 NormalX=0 NormalY=0 NormalZ=1 AngleXU=0 Radius=2.375 StartAngle=1.5708 EndAngle=3.14159
    g12: GeomPoint [constr] X=-169.91 Y=10.6 Z=0
    g13: ArcOfCircle CenterX=-167.285 CenterY=8.225 CenterZ=0 NormalX=0 NormalY=0 NormalZ=1 AngleXU=0 Radius=2.375 StartAngle=0 EndAngle=1.5708
    g14: GeomPoint [constr] X=-164.91 Y=10.6 Z=0
    g15: ArcOfCircle CenterX=-167.285 CenterY=4.975 CenterZ=0 NormalX=0 NormalY=0 NormalZ=1 AngleXU=0 Radius=2.375 StartAngle=4.71239 EndAngle=6.28319
    g16: GeomPoint [constr] X=-164.91 Y=2.6 Z=0
    g17: ArcOfCircle CenterX=-167.535 CenterY=4.975 CenterZ=0 NormalX=0 NormalY=0 NormalZ=1 AngleXU=0 Radius=2.375 StartAngle=3.14159 EndAngle=4.71239
    g18: GeomPoint [constr] X=-169.91 Y=2.6 Z=0
    g19: ArcOfCircle CenterX=-167.535 CenterY=-4.975 CenterZ=0 NormalX=0 NormalY=0 NormalZ=1 AngleXU=0 Radius=2.375 StartAngle=1.5708 EndAngle=3.14159
    g20: GeomPoint [constr] X=-169.91 Y=-2.6 Z=0
    g21: ArcOfCircle CenterX=-167.285 CenterY=-4.975 CenterZ=0 NormalX=0 NormalY=0 NormalZ=1 AngleXU=0 Radius=2.375 StartAngle=0 EndAngle=1.5708
    g22: GeomPoint [constr] X=-164.91 Y=-2.6 Z=0
    g23: ArcOfCircle CenterX=-167.285 CenterY=-8.225 CenterZ=0 NormalX=0 NormalY=0 NormalZ=1 AngleXU=0 Radius=2.375 StartAngle=4.71239 EndAngle=6.28319
    g24: GeomPoint [constr] X=-164.91 Y=-10.6 Z=0
    g25: ArcOfCircle CenterX=-167.535 CenterY=-8.225 CenterZ=0 NormalX=0 NormalY=0 NormalZ=1 AngleXU=0 Radius=2.375 StartAngle=3.14159 EndAngle=4.71239
    g26: GeomPoint [constr] X=-169.91 Y=-10.6 Z=0
    g27: LineSegment [constr] StartX=-181.6 StartY=1.12e-14 StartZ=0 EndX=-152.209 EndY=0 EndZ=0
    g28: LineSegment [constr] StartX=-181.6 StartY=1.12e-14 StartZ=0 EndX=-130.41 EndY=0 EndZ=0
    g29: LineSegment [constr] StartX=-152.209 StartY=0 StartZ=0 EndX=-152.209 EndY=6.95 EndZ=0
    g30: LineSegment [constr] StartX=-130.41 StartY=0 StartZ=0 EndX=-130.41 EndY=-6.95 EndZ=0
    g31: Circle CenterX=-152.209 CenterY=6.95 CenterZ=0 NormalX=0 NormalY=0 NormalZ=1 AngleXU=0 Radius=2.1
    g32: Circle CenterX=-130.41 CenterY=-6.95 CenterZ=0 NormalX=0 NormalY=0 NormalZ=1 AngleXU=0 Radius=2.1
  constraints (79):
    c: Distance(g0) = 11.69
    c: PointOnObject(g0,g-1)
    c: Coincident(g-4,g0)
    c: Distance(g1) = 2.6
    c: Coincident(g1,g0)
    c: Vertical(g1)
    c: Distance(g2) = 2.6
    c: Coincident(g2,g0)
    c: Vertical(g2)
    c: Distance(g18,g12) = 8
    c: Coincident(g18,g2)
    c: Vertical(g3)
    c: Distance(g14,g12) = 5
    c: Horizontal(g4)
    c: Distance(g16,g14) = 8
    c: Vertical(g5)
    c: Distance(g26,g20) = 8
    c: Coincident(g20,g1)
    c: Vertical(g7)
    c: Distance(g26,g24) = 5
    c: Horizontal(g8)
    c: Distance(g24,g22) = 8
    c: Vertical(g9)
    c: PointOnObject(g12,g3)
    c: PointOnObject(g12,g4)
    c: Tangent(g3,g11) = 1.5708
    c: Tangent(g4,g11) = 1.5708
    c: PointOnObject(g14,g5)
    c: PointOnObject(g14,g4)
    c: Tangent(g5,g13) = 1.5708
    c: Tangent(g4,g13) = 1.5708
    c: PointOnObject(g16,g5)
    c: PointOnObject(g16,g6)
    c: Tangent(g5,g15) = 1.5708
    c: Tangent(g6,g15) = 1.5708
    c: PointOnObject(g18,g3)
    c: PointOnObject(g18,g6)
    c: Tangent(g3,g17) = 1.5708
    c: Tangent(g6,g17) = 1.5708
    c: Equal(g11,g13)
    c: Equal(g13,g15)
    c: Equal(g15,g17)
    c: DistanceX(g4,g4) = 0.25
    c: PointOnObject(g20,g7)
    c: PointOnObject(g20,g10)
    c: Tangent(g7,g19) = -1.5708
    c: Tangent(g10,g19) = -1.5708
    c: PointOnObject(g22,g9)
    c: PointOnObject(g22,g10)
    c: Tangent(g9,g21) = -1.5708
    c: Tangent(g10,g21) = -1.5708
    c: PointOnObject(g24,g9)
    c: PointOnObject(g24,g8)
    c: Tangent(g9,g23) = -1.5708
    c: Tangent(g8,g23) = -1.5708
    c: PointOnObject(g26,g8)
    c: PointOnObject(g26,g7)
    c: Tangent(g8,g25) = -1.5708
    c: Tangent(g7,g25) = -1.5708
    c: Equal(g19,g21)
    c: Equal(g21,g23)
    c: Equal(g23,g25)
    c: DistanceX(g10,g10) = 0.25
    c: Distance(g27) = 29.391
    c: Coincident(g27,g0)
    c: PointOnObject(g27,g-1)
    c: Distance(g28) = 51.19
    c: Coincident(g28,g0)
    c: PointOnObject(g28,g-1)
    c: Distance(g29) = 6.95
    c: Coincident(g29,g27)
    c: Vertical(g29)
    c: Distance(g30) = 6.95
    c: Coincident(g30,g28)
    c: Vertical(g30)
    c: Diameter(g31) = 4.2
    c: Diameter(g32) = 4.2
    c: Coincident(g32,g30)
    c: Coincident(g31,g29)
FEATURE [Sketcher::SketchObject] Sketch031  label="fori inferiori switch pompa"
  ArcFitTolerance = 1e-06
  AttachmentSupport = -> [XY_Plane]
  ExternalGeometry = -> [Sketch]
  FullyConstrained = true
  MakeInternals = false
  MapMode = 5
  sketch-geometry (4):
    g0: LineSegment [constr] StartX=-57.2 StartY=1.9e-15 StartZ=0 EndX=-62.45 EndY=1.9e-15 EndZ=0
    g1: LineSegment [constr] StartX=-62.45 StartY=3.25 StartZ=0 EndX=-62.45 EndY=-3.25 EndZ=0
    g2: Circle CenterX=-62.45 CenterY=3.25 CenterZ=0 NormalX=0 NormalY=0 NormalZ=1 AngleXU=0 Radius=1.6
    g3: Circle CenterX=-62.45 CenterY=-3.25 CenterZ=0 NormalX=0 NormalY=0 NormalZ=1 AngleXU=0 Radius=1.6
  constraints (10):
    c: Distance(g0) = 5.25
    c: Coincident(g0,g-3)
    c: PointOnObject(g0,g-3)
    c: Vertical(g1)
    c: DistanceY(g1,g1) = 6.5
    c: Symmetric(g1,g1,g0)
    c: Diameter(g2) = 3.2
    c: Diameter(g3) = 3.2
    c: Coincident(g2,g1)
    c: Coincident(g3,g1)
FEATURE [Sketcher::SketchObject] Sketch032  label="spazio per PILA 18650"
  ArcFitTolerance = 1e-06
  AttachmentSupport = -> [XY_Plane]
  ExternalGeometry = -> [Sketch]
  FullyConstrained = true
  MakeInternals = false
  MapMode = 5
  sketch-geometry (2):
    g0: LineSegment [constr] StartX=-178.142 StartY=-1.74e-14 StartZ=0 EndX=-191.142 EndY=-1.83e-14 EndZ=0
    g1: Circle CenterX=-191.142 CenterY=-1.83e-14 CenterZ=0 NormalX=0 NormalY=0 NormalZ=1 AngleXU=0 Radius=10.5
  constraints (5):
    c: Distance(g0) = 13
    c: Coincident(g0,g-3)
    c: PointOnObject(g0,g-4)
    c: Diameter(g1) = 21
    c: Coincident(g1,g0)
FEATURE [Part::Extrusion] Extrude030  label="Extrude spazio per PILA 18650"
  Base = -> Sketch032
  Dir = (0,0,1)
  DirLink = -> Sketch [Edge45]
  DirMode = 2
  FaceMakerClass = Part::FaceMakerBullseye
  FaceMakerMode = 3
  LengthFwd = 76
  LengthRev = 0
  Placement = pos=(6,0,-72) rot=(0,0,1;0rad)
  Solid = true
  Symmetric = false
FEATURE [Sketcher::SketchObject] Sketch033  label="fermo per scheda micro"
  ArcFitTolerance = 1e-06
  AttachmentSupport = -> [XZ_Plane]
  ExternalGeometry = -> [Sketch]
  FullyConstrained = true
  MakeInternals = false
  MapMode = 5
  Placement = pos=(0,0,0) rot=(1,0,0;1.5708rad)
  sketch-geometry (12):
    g0: LineSegment StartX=-11.6 StartY=6 StartZ=0 EndX=-4 EndY=6 EndZ=0
    g1: LineSegment StartX=-4 StartY=6 StartZ=0 EndX=-4 EndY=36.4 EndZ=0
    g2: LineSegment StartX=-4 StartY=36.4 StartZ=0 EndX=-11.6 EndY=36.4 EndZ=0
    g3: LineSegment StartX=-11.6 StartY=36.4 StartZ=0 EndX=-11.6 EndY=6 EndZ=0
    g4: LineSegment StartX=-80.11 StartY=11.6 StartZ=0 EndX=-70.51 EndY=11.6 EndZ=0
    g5: LineSegment StartX=-70.51 StartY=11.6 StartZ=0 EndX=-70.51 EndY=6 EndZ=0
    g6: LineSegment StartX=-70.51 StartY=6 StartZ=0 EndX=-80.11 EndY=6 EndZ=0
    g7: LineSegment StartX=-80.11 StartY=6 StartZ=0 EndX=-80.11 EndY=11.6 EndZ=0
    g8: LineSegment StartX=-78.51 StartY=36.4 StartZ=0 EndX=-70.51 EndY=36.4 EndZ=0
    g9: LineSegment StartX=-70.51 StartY=36.4 StartZ=0 EndX=-70.51 EndY=30.8 EndZ=0
    g10: LineSegment StartX=-70.51 StartY=30.8 StartZ=0 EndX=-78.51 EndY=30.8 EndZ=0
    g11: LineSegment StartX=-78.51 StartY=30.8 StartZ=0 EndX=-78.51 EndY=36.4 EndZ=0
  constraints (33):
    c: Horizontal(g0)
    c: Coincident(g1,g0)
    c: Coincident(g2,g1)
    c: Horizontal(g2)
    c: Coincident(g3,g2)
    c: Coincident(g3,g0)
    c: Vertical(g3)
    c: DistanceX(g2,g2) = 7.6
    c: Coincident(g1,g-3)
    c: Coincident(g0,g-3)
    c: Horizontal(g4)
    c: Coincident(g5,g4)
    c: Vertical(g5)
    c: Coincident(g6,g5)
    c: Horizontal(g6)
    c: Coincident(g7,g6)
    c: Coincident(g7,g4)
    c: Vertical(g7)
    c: DistanceY(g5,g5) = 5.6
    c: DistanceX(g4,g4) = 9.6
    c: Coincident(g9,g8)
    c: Vertical(g9)
    c: Coincident(g10,g9)
    c: Horizontal(g10)
    c: Coincident(g11,g10)
    c: Coincident(g11,g8)
    c: Vertical(g11)
    c: DistanceY(g9,g9) = 5.6
    c: DistanceX(g10,g10) = 8
    c: Coincident(g4,g-4)
    c: DistanceX(g4,g10) = 1.6
    c: Horizontal(g8)
    c: DistanceY(g8,g1) = 0
FEATURE [Sketcher::SketchObject] Sketch034  label="buchi guida rail"
  ArcFitTolerance = 1e-06
  AttachmentSupport = -> [XY_Plane]
  ExternalGeometry = -> [Sketch]
  FullyConstrained = true
  MakeInternals = false
  MapMode = 5
  sketch-geometry (6):
    g0: LineSegment [constr] StartX=-100.8 StartY=9.1e-15 StartZ=0 EndX=-93.3 EndY=0 EndZ=0
    g1: LineSegment [constr] StartX=-93.3 StartY=0 StartZ=0 EndX=-73.3 EndY=0 EndZ=0
    g2: LineSegment [constr] StartX=-73.3 StartY=0 StartZ=0 EndX=-53.3 EndY=0 EndZ=0
    g3: Circle CenterX=-93.3 CenterY=0 CenterZ=0 NormalX=0 NormalY=0 NormalZ=1 AngleXU=0 Radius=2.5
    g4: Circle CenterX=-73.3 CenterY=0 CenterZ=0 NormalX=0 NormalY=0 NormalZ=1 AngleXU=0 Radius=2.5
    g5: Circle CenterX=-53.3 CenterY=0 CenterZ=0 NormalX=0 NormalY=0 NormalZ=1 AngleXU=0 Radius=2.5
  constraints (15):
    c: Distance(g0) = 7.5
    c: Coincident(g0,g-3)
    c: PointOnObject(g0,g-1)
    c: Distance(g1) = 20
    c: Coincident(g1,g0)
    c: PointOnObject(g1,g-1)
    c: Distance(g2) = 20
    c: Coincident(g2,g1)
    c: PointOnObject(g2,g-1)
    c: Diameter(g3) = 5
    c: Diameter(g4) = 5
    c: Diameter(g5) = 5
    c: Coincident(g3,g0)
    c: Coincident(g4,g1)
    c: Coincident(g5,g2)
FEATURE [Part::Extrusion] Extrude032  label="Extrude buchi guida rail"
  Base = -> Sketch034
  Dir = (0,0,1)
  DirMode = 2
  FaceMakerClass = Part::FaceMakerBullseye
  FaceMakerMode = 3
  LengthFwd = -6.2
  LengthRev = 0
  Placement = pos=(0,0,43.2) rot=(0,0,1;0rad)
  Solid = true
  Symmetric = false
FEATURE [Part::Extrusion] Extrude033  label="Extrude fori superiori per solenoide e oled001"
  Base = -> Sketch030
  Dir = (0,0,1)
  DirMode = 2
  FaceMakerClass = Part::FaceMakerBullseye
  FaceMakerMode = 3
  LengthFwd = -4.8
  LengthRev = 0
  Placement = pos=(0,0,41.2) rot=(0,0,1;0rad)
  Solid = true
  Symmetric = false
FEATURE [Part::Extrusion] Extrude034  label="Extrude fori sotto impugnatura001"
  Base = -> Sketch029
  Dir = (0,0,1)
  DirMode = 2
  FaceMakerClass = Part::FaceMakerBullseye
  FaceMakerMode = 3
  LengthFwd = 5
  LengthRev = 0
  Placement = pos=(0,0,-83) rot=(0,0,1;0rad)
  Solid = true
  Symmetric = false
FEATURE [Part::Extrusion] Extrude035  label="Extrude fori inferiori switch pompa001"
  Base = -> Sketch031
  Dir = (0,0,1)
  DirMode = 2
  FaceMakerClass = Part::FaceMakerBullseye
  FaceMakerMode = 3
  LengthFwd = 4
  LengthRev = 0
  Placement = pos=(0,0,-1.7) rot=(0,0,1;0rad)
  Solid = true
  Symmetric = false
FEATURE [Part::Extrusion] Extrude036  label="Extrude foro sotto posteriore M3x5x007"
  Base = -> Sketch027
  Dir = (0,0,1)
  DirMode = 2
  FaceMakerClass = Part::FaceMakerBullseye
  FaceMakerMode = 3
  LengthFwd = 6.2
  LengthRev = 0
  Placement = pos=(0,0,-9.6) rot=(0,0,1;0rad)
  Solid = true
  Symmetric = false
FEATURE [Part::Extrusion] Extrude037  label="Extrude foro sotto anteriore M3x5x007"
  Base = -> Sketch026
  Dir = (0,0,1)
  DirMode = 2
  FaceMakerClass = Part::FaceMakerBullseye
  FaceMakerMode = 3
  LengthFwd = 6.2
  LengthRev = 0
  Solid = true
  Symmetric = false
FEATURE [Sketcher::SketchObject] Sketch035  label="foro per fissaggio micro"
  ArcFitTolerance = 1e-06
  AttachmentSupport = -> [XZ_Plane]
  ExternalGeometry = -> [Sketch,Sketch033]
  FullyConstrained = true
  MakeInternals = false
  MapMode = 5
  Placement = pos=(0,0,0) rot=(1,0,0;1.5708rad)
  sketch-geometry (3):
    g0: Circle CenterX=-7.8 CenterY=21.2 CenterZ=0 NormalX=0 NormalY=0 NormalZ=1 AngleXU=0 Radius=1.6
    g1: GeomPoint [constr] X=-4 Y=21.2 Z=0
    g2: LineSegment [constr] StartX=-4 StartY=21.2 StartZ=0 EndX=-11.6 EndY=21.2 EndZ=0
  constraints (6):
    c: Diameter(g0) = 3.2
    c: Symmetric(g-3,g-3,g1)
    c: Coincident(g2,g1)
    c: Horizontal(g2)
    c: DistanceX(g-4,g2) = 0
    c: Symmetric(g2,g1,g0)
FEATURE [Part::Extrusion] Extrude038  label="Extrude foro per fissaggio micro"
  Base = -> Sketch035
  Dir = (0,-1,2e-16)
  DirMode = 2
  FaceMakerClass = Part::FaceMakerBullseye
  FaceMakerMode = 3
  LengthFwd = 3
  LengthRev = 0
  Placement = pos=(0,8.6,0) rot=(0,0,1;0rad)
  Solid = true
  Symmetric = false
FEATURE [Sketcher::SketchObject] Sketch036  label="supporto per alimentatore"
  ArcFitTolerance = 1e-06
  AttachmentSupport = -> [XZ_Plane]
  ExternalGeometry = -> [Sketch,Sketch016,Sketch022]
  FullyConstrained = true
  MakeInternals = false
  MapMode = 5
  Placement = pos=(0,0,0) rot=(1,0,0;1.5708rad)
  sketch-geometry (5):
    g0: LineSegment StartX=-211.843 StartY=-50.0944 StartZ=0 EndX=-211.843 EndY=-80.4316 EndZ=0
    g1: LineSegment StartX=-211.843 StartY=-50.0944 StartZ=0 EndX=-207.775 EndY=-41.3701 EndZ=0
    g2: LineSegment [constr] StartX=-209.443 StartY=-50.0944 StartZ=0 EndX=-209.443 EndY=-80.4316 EndZ=0
    g3: LineSegment StartX=-207.775 StartY=-41.3701 StartZ=0 EndX=-207.775 EndY=-80.4316 EndZ=0
    g4: LineSegment StartX=-211.843 StartY=-80.4316 StartZ=0 EndX=-207.775 EndY=-80.4316 EndZ=0
  constraints (15):
    c: Vertical(g0)
    c: Coincident(g1,g0)
    c: Vertical(g2)
    c: Tangent(g2,g-5)
    c: Coincident(g3,g1)
    c: Vertical(g3)
    c: DistanceY(g-3,g3) = -2
    c: Tangent(g1,g-8)
    c: DistanceY(g-3,g0) = -2
    c: Coincident(g4,g0)
    c: Coincident(g4,g3)
    c: Tangent(g0,g-6)
    c: DistanceY(g-3,g2) = -2
    c: DistanceY(g2,g0) = 0
    c: DistanceX(g-3,g3) = 6.8
FEATURE [Part::Extrusion] Extrude039  label="Extrude039 supporto alimentatore"
  Base = -> Sketch036
  Dir = (0,-1,2e-16)
  DirMode = 2
  FaceMakerClass = Part::FaceMakerBullseye
  FaceMakerMode = 3
  LengthFwd = 25.2
  LengthRev = 0
  Solid = true
  Symmetric = true
FEATURE [Sketcher::SketchObject] Sketch037  label="scavo per alimentatore"
  ArcFitTolerance = 1e-06
  AttachmentSupport = -> [XZ_Plane]
  ExternalGeometry = -> [Sketch036]
  FullyConstrained = true
  MakeInternals = false
  MapMode = 5
  Placement = pos=(0,0,0) rot=(1,0,0;1.5708rad)
  sketch-geometry (4):
    g0: LineSegment StartX=-209.575 StartY=-50.4316 StartZ=0 EndX=-209.575 EndY=-80.4316 EndZ=0
    g1: LineSegment StartX=-209.575 StartY=-50.4316 StartZ=0 EndX=-207.775 EndY=-50.4316 EndZ=0
    g2: LineSegment StartX=-207.775 StartY=-50.4316 StartZ=0 EndX=-207.775 EndY=-80.4316 EndZ=0
    g3: LineSegment StartX=-207.775 StartY=-80.4316 StartZ=0 EndX=-209.575 EndY=-80.4316 EndZ=0
  constraints (11):
    c: Vertical(g0)
    c: Coincident(g1,g0)
    c: Horizontal(g1)
    c: Coincident(g2,g1)
    c: Vertical(g2)
    c: Coincident(g3,g2)
    c: Coincident(g3,g0)
    c: Horizontal(g3)
    c: DistanceX(g1,g1) = 1.8
    c: Coincident(g2,g-3)
    c: DistanceY(g2,g2) = 30
FEATURE [Part::Extrusion] Extrude040  label="Extrude040 scavo alimentatore"
  Base = -> Sketch037
  Dir = (0,-1,2e-16)
  DirMode = 2
  FaceMakerClass = Part::FaceMakerBullseye
  FaceMakerMode = 3
  LengthFwd = 19.5
  LengthRev = 0
  Solid = true
  Symmetric = true
FEATURE [Part::Extrusion] Extrude031  label="Extrude fermo per scheda micro"
  Base = -> Sketch033
  Dir = (0,-1,2e-16)
  DirMode = 2
  FaceMakerClass = Part::FaceMakerBullseye
  FaceMakerMode = 3
  LengthFwd = 3
  LengthRev = 0
  Placement = pos=(0,8.6,0) rot=(0,0,1;0rad)
  Solid = true
  Symmetric = false
FEATURE [Sketcher::SketchObject] Sketch038  label="scavo driver solenoide"
  ArcFitTolerance = 1e-06
  AttachmentSupport = -> [XZ_Plane]
  ExternalGeometry = -> [Sketch,Sketch036]
  FullyConstrained = true
  MakeInternals = false
  MapMode = 5
  Placement = pos=(0,0,0) rot=(1,0,0;1.5708rad)
  sketch-geometry (7):
    g0: LineSegment StartX=-192.222 StartY=-8.0175 StartZ=0 EndX=-194.941 EndY=-6.74965 EndZ=0
    g1: LineSegment StartX=-194.941 StartY=-6.74965 StartZ=0 EndX=-212.269 EndY=-43.9083 EndZ=0
    g2: LineSegment StartX=-192.222 StartY=-8.0175 StartZ=0 EndX=-188.779 EndY=-9.62345 EndZ=0
    g3: LineSegment StartX=-188.779 StartY=-9.62345 StartZ=0 EndX=-205.357 EndY=-45.1761 EndZ=0
    g4: LineSegment StartX=-205.357 StartY=-45.1761 StartZ=0 EndX=-209.55 EndY=-45.1761 EndZ=0
    g5: LineSegment [constr] StartX=-212.269 StartY=-43.9083 StartZ=0 EndX=-209.55 EndY=-45.1761 EndZ=0
    g6: LineSegment StartX=-212.269 StartY=-43.9083 StartZ=0 EndX=-209.55 EndY=-45.1761 EndZ=0
  constraints (20):
    c: Coincident(g1,g0)
    c: Coincident(g3,g2)
    c: Coincident(g4,g3)
    c: Distance(g2) = 3.8
    c: Distance(g1) = 41
    c: Coincident(g5,g1)
    c: Distance(g5) = 3
    c: Perpendicular(g5,g-3)
    c: Parallel(g1,g-3)
    c: Perpendicular(g1,g0)
    c: Distance(g0) = 3
    c: Coincident(g6,g1)
    c: Parallel(g3,g-3)
    c: Perpendicular(g2,g3)
    c: Coincident(g2,g0)
    c: Perpendicular(g-4,g4)
    c: PointOnObject(g5,g-3)
    c: Distance(g-3,g5) = 9.6
    c: Coincident(g4,g5)
    c: Coincident(g6,g4)
FEATURE [Part::Extrusion] Extrude041  label="Extrude scavo driver solenoide"
  Base = -> Sketch038
  Dir = (0,-1,2e-16)
  DirMode = 2
  FaceMakerClass = Part::FaceMakerBullseye
  FaceMakerMode = 3
  LengthFwd = 20.6
  LengthRev = 0
  Solid = true
  Symmetric = true
FEATURE [Sketcher::SketchObject] Sketch039  label="scavo per cavo usb per micro"
  ArcFitTolerance = 1e-06
  AttachmentSupport = -> [XZ_Plane]
  ExternalGeometry = -> [Sketch,Sketch016]
  FullyConstrained = true
  MakeInternals = false
  MapMode = 5
  Placement = pos=(0,0,0) rot=(1,0,0;1.5708rad)
  sketch-geometry (4):
    g0: LineSegment StartX=-82.51 StartY=36.4 StartZ=0 EndX=-74.51 EndY=36.4 EndZ=0
    g1: LineSegment StartX=-74.51 StartY=36.4 StartZ=0 EndX=-74.51 EndY=30.8 EndZ=0
    g2: LineSegment StartX=-74.51 StartY=30.8 StartZ=0 EndX=-82.51 EndY=30.8 EndZ=0
    g3: LineSegment StartX=-82.51 StartY=30.8 StartZ=0 EndX=-82.51 EndY=36.4 EndZ=0
  constraints (11):
    c: Coincident(g1,g0)
    c: Vertical(g1)
    c: Coincident(g2,g1)
    c: Horizontal(g2)
    c: Coincident(g3,g2)
    c: Coincident(g3,g0)
    c: Vertical(g3)
    c: Tangent(g0,g-3)
    c: Tangent(g2,g-4)
    c: Tangent(g3,g-4)
    c: Tangent(g1,g-4)
FEATURE [Part::Extrusion] Extrude042  label="Extrude scavo per cavo usb per micro"
  Base = -> Sketch039
  Dir = (0,-1,2e-16)
  DirMode = 2
  FaceMakerClass = Part::FaceMakerBullseye
  FaceMakerMode = 3
  LengthFwd = 11.2
  LengthRev = 0
  Solid = true
  Symmetric = true
FEATURE [Sketcher::SketchObject] Sketch040  label="scavo saldature alimentatore connettore 5v"
  ArcFitTolerance = 1e-06
  AttachmentSupport = -> [XZ_Plane]
  ExternalGeometry = -> [Sketch037]
  FullyConstrained = true
  MakeInternals = false
  MapMode = 5
  Placement = pos=(0,0,0) rot=(1,0,0;1.5708rad)
  sketch-geometry (4):
    g0: LineSegment StartX=-211.175 StartY=-52.4316 StartZ=0 EndX=-211.175 EndY=-56.4316 EndZ=0
    g1: LineSegment StartX=-211.175 StartY=-52.4316 StartZ=0 EndX=-209.575 EndY=-52.4316 EndZ=0
    g2: LineSegment StartX=-209.575 StartY=-52.4316 StartZ=0 EndX=-209.575 EndY=-56.4316 EndZ=0
    g3: LineSegment StartX=-209.575 StartY=-56.4316 StartZ=0 EndX=-211.175 EndY=-56.4316 EndZ=0
  constraints (11):
    c: Vertical(g0)
    c: Coincident(g1,g0)
    c: Horizontal(g1)
    c: Coincident(g2,g1)
    c: Coincident(g3,g2)
    c: Coincident(g3,g0)
    c: Horizontal(g3)
    c: DistanceX(g1,g1) = 1.6
    c: DistanceY(g2,g2) = 4
    c: Tangent(g2,g-3)
    c: DistanceY(g1,g-3) = 2
FEATURE [Part::Extrusion] Extrude043  label="Extrude scavo saldature alimentatore connettore 5v"
  Base = -> Sketch040
  Dir = (0,-1,2e-16)
  DirMode = 2
  FaceMakerClass = Part::FaceMakerBullseye
  FaceMakerMode = 3
  LengthFwd = 8
  LengthRev = 0
  Solid = true
  Symmetric = true
FEATURE [Sketcher::SketchObject] Sketch041  label="scavo saldature alimentatore connettore 5v verticali"
  ArcFitTolerance = 1e-06
  AttachmentSupport = -> [XZ_Plane]
  ExternalGeometry = -> [Sketch037]
  FullyConstrained = true
  MakeInternals = false
  MapMode = 5
  Placement = pos=(0,0,0) rot=(1,0,0;1.5708rad)
  sketch-geometry (4):
    g0: LineSegment StartX=-211.175 StartY=-53.6316 StartZ=0 EndX=-209.575 EndY=-53.6316 EndZ=0
    g1: LineSegment StartX=-209.575 StartY=-53.6316 StartZ=0 EndX=-209.575 EndY=-76.6316 EndZ=0
    g2: LineSegment StartX=-209.575 StartY=-76.6316 StartZ=0 EndX=-211.175 EndY=-76.6316 EndZ=0
    g3: LineSegment StartX=-211.175 StartY=-76.6316 StartZ=0 EndX=-211.175 EndY=-53.6316 EndZ=0
  constraints (11):
    c: Horizontal(g0)
    c: Coincident(g1,g0)
    c: Coincident(g2,g1)
    c: Horizontal(g2)
    c: Coincident(g3,g2)
    c: Coincident(g3,g0)
    c: Vertical(g3)
    c: DistanceY(g3,g3) = 23
    c: DistanceX(g0,g0) = 1.6
    c: Tangent(g1,g-3)
    c: DistanceY(g0,g-3) = 3.2
FEATURE [Part::Extrusion] Extrude044  label="Extrude scavo saldature alimentatore connettore 5v verticali"
  Base = -> Sketch041
  Dir = (0,-1,2e-16)
  DirMode = 2
  FaceMakerClass = Part::FaceMakerBullseye
  FaceMakerMode = 3
  LengthFwd = 3.2
  LengthRev = 0
  Placement = pos=(0,8.3,0) rot=(0,0,1;0rad)
  Solid = true
  Symmetric = false
FEATURE [Sketcher::SketchObject] Sketch042  label="fermi per driver solenoide e alimentatore"
  ArcFitTolerance = 1e-06
  AttachmentSupport = -> [XZ_Plane]
  ExternalGeometry = -> [Sketch036,Sketch037,Sketch,Sketch038]
  FullyConstrained = true
  MakeInternals = false
  MapMode = 5
  Placement = pos=(0,0,0) rot=(1,0,0;1.5708rad)
  sketch-geometry (27):
    g0: LineSegment StartX=-200.506 StartY=-25.7811 StartZ=0 EndX=-201.436 EndY=-27.775 EndZ=0
    g1: LineSegment StartX=-201.436 StartY=-27.775 StartZ=0 EndX=-199.442 EndY=-28.7048 EndZ=0
    g2: LineSegment StartX=-199.442 StartY=-28.7048 StartZ=0 EndX=-198.512 EndY=-26.7109 EndZ=0
    g3: LineSegment StartX=-198.512 StartY=-26.7109 StartZ=0 EndX=-200.506 EndY=-25.7811 EndZ=0
    g4: LineSegment StartX=-201.28 StartY=-23.6549 StartZ=0 EndX=-203.562 EndY=-28.5489 EndZ=0
    g5: LineSegment StartX=-203.562 StartY=-28.5489 StartZ=0 EndX=-200.118 EndY=-30.1549 EndZ=0
    g6: LineSegment StartX=-197.992 StartY=-29.381 StartZ=0 EndX=-197.062 EndY=-27.3871 EndZ=0
    g7: LineSegment StartX=-197.836 StartY=-25.2608 StartZ=0 EndX=-201.28 EndY=-23.6549 EndZ=0
    g8: LineSegment [constr] StartX=-198.668 StartY=-30.8311 StartZ=0 EndX=-197.992 EndY=-29.381 EndZ=0
    g9: LineSegment [constr] StartX=-198.668 StartY=-30.8311 StartZ=0 EndX=-200.118 EndY=-30.1549 EndZ=0
    g10: ArcOfCircle CenterX=-198.512 CenterY=-26.7109 CenterZ=0 NormalX=0 NormalY=0 NormalZ=1 AngleXU=0 Radius=1.6 StartAngle=5.84685 EndAngle=7.41765
    g11: GeomPoint [constr] X=-196.386 Y=-25.937 Z=0
    g12: ArcOfCircle CenterX=-199.442 CenterY=-28.7048 CenterZ=0 NormalX=0 NormalY=0 NormalZ=1 AngleXU=0 Radius=1.6 StartAngle=4.27606 EndAngle=5.84685
    g13: GeomPoint [constr] X=-198.668 Y=-30.8311 Z=0
    g14: LineSegment StartX=-207.775 StartY=-46.8316 StartZ=0 EndX=-207.775 EndY=-50.8316 EndZ=0
    g15: LineSegment StartX=-207.775 StartY=-46.8316 StartZ=0 EndX=-203.775 EndY=-46.8316 EndZ=0
    g16: LineSegment StartX=-203.775 StartY=-46.8316 StartZ=0 EndX=-203.775 EndY=-50.8316 EndZ=0
    g17: LineSegment StartX=-207.775 StartY=-50.8316 StartZ=0 EndX=-203.775 EndY=-50.8316 EndZ=0
    g18: LineSegment StartX=-209.375 StartY=-52.4316 StartZ=0 EndX=-203.775 EndY=-52.4316 EndZ=0
    g19: LineSegment StartX=-202.175 StartY=-50.8316 StartZ=0 EndX=-202.175 EndY=-46.8316 EndZ=0
    g20: LineSegment StartX=-203.775 StartY=-45.2316 StartZ=0 EndX=-209.375 EndY=-45.2316 EndZ=0
    g21: LineSegment StartX=-209.375 StartY=-45.2316 StartZ=0 EndX=-209.375 EndY=-52.4316 EndZ=0
    g22: ArcOfCircle CenterX=-203.775 CenterY=-46.8316 CenterZ=0 NormalX=0 NormalY=0 NormalZ=1 AngleXU=0 Radius=1.6 StartAngle=1.8e-15 EndAngle=1.5708
    g23: GeomPoint [constr] X=-202.175 Y=-45.2316 Z=0
    g24: ArcOfCircle CenterX=-203.775 CenterY=-50.8316 CenterZ=0 NormalX=0 NormalY=0 NormalZ=1 AngleXU=0 Radius=1.6 StartAngle=4.71239 EndAngle=6.28319
    g25: GeomPoint [constr] X=-202.175 Y=-52.4316 Z=0
    g26: LineSegment [constr] StartX=-207.775 StartY=-50.4316 StartZ=0 EndX=-207.775 EndY=-50.8316 EndZ=0
  constraints (69):
    c: Coincident(g1,g0)
    c: Coincident(g2,g1)
    c: Coincident(g3,g2)
    c: Coincident(g3,g0)
    c: Parallel(g0,g2)
    c: Perpendicular(g3,g0)
    c: Perpendicular(g1,g0)
    c: Coincident(g5,g4)
    c: Coincident(g7,g4)
    c: Distance(g3) = 2.2
    c: Distance(g2) = 2.2
    c: Parallel(g6,g2)
    c: Parallel(g6,g4)
    c: Perpendicular(g5,g6)
    c: Perpendicular(g7,g6)
    c: Distance(g13,g11) = 5.4
    c: Distance(g5,g13) = 5.4
    c: Coincident(g9,g8)
    c: Distance(g8) = 1.6
    c: Distance(g9) = 1.6
    c: Perpendicular(g9,g8)
    c: Parallel(g8,g6)
    c: Coincident(g8,g13)
    c: Distance(g8,g1) = 1.6
    c: Distance(g9,g1) = 1.6
    c: Tangent(g0,g-5)
    c: Distance(g0,g-6) = 19.2
    c: PointOnObject(g11,g7)
    c: PointOnObject(g11,g6)
    c: Tangent(g7,g10) = -1.5708
    c: Tangent(g6,g10) = -1.5708
    c: PointOnObject(g13,g5)
    c: Tangent(g5,g12) = -1.5708
    c: Tangent(g6,g12) = -1.5708
    c: Equal(g10,g12)
    c: Coincident(g10,g2)
    c: Vertical(g14)
    c: Coincident(g15,g14)
    c: Horizontal(g15)
    c: Coincident(g16,g15)
    c: Vertical(g16)
    c: Coincident(g17,g14)
    c: Coincident(g17,g16)
    c: Horizontal(g17)
    c: Distance(g16) = 4
    c: Distance(g15) = 4
    c: Horizontal(g18)
    c: Vertical(g19)
    c: Horizontal(g20)
    c: Coincident(g21,g20)
    c: Coincident(g21,g18)
    c: Vertical(g21)
    c: Distance(g20,g23) = 7.2
    c: Distance(g25,g23) = 7.2
    c: DistanceY(g18,g14) = 1.6
    c: DistanceX(g18,g14) = 1.6
    c: PointOnObject(g23,g20)
    c: PointOnObject(g23,g19)
    c: Tangent(g20,g22) = -1.5708
    c: Tangent(g19,g22) = -1.5708
    c: PointOnObject(g25,g19)
    c: Tangent(g18,g24) = -1.5708
    c: Tangent(g19,g24) = -1.5708
    c: Equal(g22,g24)
    c: Coincident(g22,g15)
    c: Vertical(g26)
    c: Distance(g26) = 0.4
    c: Coincident(g26,g-4)
    c: Coincident(g14,g26)
FEATURE [Part::Extrusion] Extrude045  label="Extrude fermi per driver solenoide e alimentatore"
  Base = -> Sketch042
  Dir = (0,-1,2e-16)
  DirMode = 2
  FaceMakerClass = Part::FaceMakerBullseye
  FaceMakerMode = 3
  LengthFwd = 25.2
  LengthRev = 0
  Solid = true
  Symmetric = true
FEATURE [Sketcher::SketchObject] Sketch043  label="scavo pulizia fermo alimentatore"
  ArcFitTolerance = 1e-06
  AttachmentSupport = -> [XZ_Plane]
  ExternalGeometry = -> [Sketch042,Sketch036,Sketch037]
  FullyConstrained = true
  MakeInternals = false
  MapMode = 5
  Placement = pos=(0,0,0) rot=(1,0,0;1.5708rad)
  sketch-geometry (6):
    g0: LineSegment StartX=-209.375 StartY=-52.4316 StartZ=0 EndX=-209.375 EndY=-50.4316 EndZ=0
    g1: LineSegment StartX=-209.375 StartY=-50.4316 StartZ=0 EndX=-207.775 EndY=-50.4316 EndZ=0
    g2: LineSegment StartX=-207.775 StartY=-50.4316 StartZ=0 EndX=-207.775 EndY=-45.2316 EndZ=0
    g3: LineSegment StartX=-207.775 StartY=-45.2316 StartZ=0 EndX=-202.175 EndY=-45.2316 EndZ=0
    g4: LineSegment StartX=-202.175 StartY=-45.2316 StartZ=0 EndX=-202.175 EndY=-52.4316 EndZ=0
    g5: LineSegment StartX=-202.175 StartY=-52.4316 StartZ=0 EndX=-209.375 EndY=-52.4316 EndZ=0
  constraints (13):
    c: Vertical(g0)
    c: Coincident(g1,g0)
    c: Coincident(g2,g1)
    c: Coincident(g3,g2)
    c: Coincident(g4,g3)
    c: Coincident(g5,g4)
    c: Coincident(g5,g0)
    c: Horizontal(g5)
    c: Coincident(g0,g-6)
    c: Tangent(g1,g-8)
    c: Tangent(g2,g-4)
    c: Tangent(g3,g-7)
    c: Tangent(g4,g-3)
FEATURE [Part::Extrusion] Extrude046  label="Extrude scavo pulizia fermo alimentatore"
  Base = -> Sketch043
  Dir = (0,-1,2e-16)
  DirMode = 2
  FaceMakerClass = Part::FaceMakerBullseye
  FaceMakerMode = 3
  LengthFwd = 19.5
  LengthRev = 0
  Solid = true
  Symmetric = true
FEATURE [Sketcher::SketchObject] Sketch044  label="buchini per fissaggio oled"
  ArcFitTolerance = 1e-06
  AttachmentSupport = -> [YZ_Plane]
  ExternalGeometry = -> [Sketch]
  FullyConstrained = true
  MakeInternals = false
  MapMode = 5
  Placement = pos=(0,0,0) rot=(0.57735,0.57735,0.57735;2.0944rad)
  sketch-geometry (5):
    g0: LineSegment [constr] StartX=1.5e-14 StartY=67.3588 StartZ=0 EndX=0 EndY=64.3588 EndZ=0
    g1: LineSegment [constr] StartX=0 StartY=64.3588 StartZ=0 EndX=10.4 EndY=64.3588 EndZ=0
    g2: LineSegment [constr] StartX=0 StartY=64.3588 StartZ=0 EndX=-10.4 EndY=64.3588 EndZ=0
    g3: Circle CenterX=10.4 CenterY=64.3588 CenterZ=0 NormalX=0 NormalY=0 NormalZ=1 AngleXU=0 Radius=1.5
    g4: Circle CenterX=-10.4 CenterY=64.3588 CenterZ=0 NormalX=0 NormalY=0 NormalZ=1 AngleXU=0 Radius=1.5
  constraints (13):
    c: Distance(g0) = 3
    c: PointOnObject(g0,g-2)
    c: Coincident(g1,g0)
    c: Horizontal(g1)
    c: Coincident(g2,g0)
    c: Horizontal(g2)
    c: DistanceX(g1,g1) = 10.4
    c: Coincident(g3,g1)
    c: Diameter(g4) = 3
    c: Coincident(g4,g2)
    c: Coincident(g0,g-7)
    c: Equal(g1,g2)
    c: Equal(g4,g3)
FEATURE [Part::Extrusion] Extrude047  label="Extrude buchini per fissaggio oled"
  Base = -> Sketch044
  Dir = (1,0,0)
  DirMode = 2
  FaceMakerClass = Part::FaceMakerBullseye
  FaceMakerMode = 3
  LengthFwd = 10
  LengthRev = 0
  Placement = pos=(-186,0,0) rot=(0,0,1;0rad)
  Solid = true
  Symmetric = false
FEATURE [Sketcher::SketchObject] Sketch046  label="scavo 5x5 neopixel"
  ArcFitTolerance = 1e-06
  AttachmentSupport = -> [YZ_Plane002]
  FullyConstrained = true
  MakeInternals = false
  MapMode = 5
  Placement = pos=(0,0,0) rot=(0.57735,0.57735,0.57735;2.0944rad)
  sketch-geometry (4):
    g0: LineSegment StartX=-2.7 StartY=2.7 StartZ=0 EndX=2.7 EndY=2.7 EndZ=0
    g1: LineSegment StartX=2.7 StartY=2.7 StartZ=0 EndX=2.7 EndY=-2.7 EndZ=0
    g2: LineSegment StartX=2.7 StartY=-2.7 StartZ=0 EndX=-2.7 EndY=-2.7 EndZ=0
    g3: LineSegment StartX=-2.7 StartY=-2.7 StartZ=0 EndX=-2.7 EndY=2.7 EndZ=0
  constraints (11):
    c: Horizontal(g0)
    c: Coincident(g1,g0)
    c: Vertical(g1)
    c: Coincident(g2,g1)
    c: Horizontal(g2)
    c: Coincident(g3,g2)
    c: Coincident(g3,g0)
    c: Vertical(g3)
    c: DistanceX(g0,g0) = 5.4
    c: DistanceY(g1,g1) = 5.4
    c: Symmetric(g0,g1,g-1)
FEATURE [Sketcher::SketchObject] Sketch047  label="scavo 10x10 neopixel corpo"
  ArcFitTolerance = 1e-06
  AttachmentOffset = pos=(0,0,1) rot=(0,0,1;0rad)
  AttachmentSupport = -> [YZ_Plane002]
  FullyConstrained = true
  MakeInternals = false
  MapMode = 5
  Placement = pos=(1,0,0) rot=(0.57735,0.57735,0.57735;2.0944rad)
  sketch-geometry (4):
    g0: LineSegment StartX=-5 StartY=5.1 StartZ=0 EndX=5 EndY=5.1 EndZ=0
    g1: LineSegment StartX=5 StartY=5.1 StartZ=0 EndX=5 EndY=-5.1 EndZ=0
    g2: LineSegment StartX=5 StartY=-5.1 StartZ=0 EndX=-5 EndY=-5.1 EndZ=0
    g3: LineSegment StartX=-5 StartY=-5.1 StartZ=0 EndX=-5 EndY=5.1 EndZ=0
  constraints (11):
    c: Horizontal(g0)
    c: Coincident(g1,g0)
    c: Vertical(g1)
    c: Coincident(g2,g1)
    c: Horizontal(g2)
    c: Coincident(g3,g2)
    c: Coincident(g3,g0)
    c: Vertical(g3)
    c: DistanceX(g0,g0) = 10
    c: DistanceY(g1,g1) = 10.2
    c: Symmetric(g0,g2,g-1)
FEATURE [Sketcher::SketchObject] Sketch048  label="buco per perno blocco neopixel"
  ArcFitTolerance = 1e-06
  AttachmentSupport = -> [XZ_Plane002]
  FullyConstrained = true
  MakeInternals = false
  MapMode = 5
  Placement = pos=(0,0,0) rot=(1,0,0;1.5708rad)
  sketch-geometry (4):
    g0: LineSegment StartX=3 StartY=1.2 StartZ=0 EndX=3 EndY=-1.2 EndZ=0
    g1: LineSegment StartX=3 StartY=-1.2 StartZ=0 EndX=5.4 EndY=-1.2 EndZ=0
    g2: LineSegment StartX=5.4 StartY=-1.2 StartZ=0 EndX=5.4 EndY=1.2 EndZ=0
    g3: LineSegment StartX=5.4 StartY=1.2 StartZ=0 EndX=3 EndY=1.2 EndZ=0
  constraints (11):
    c: Coincident(g1,g0)
    c: Horizontal(g1)
    c: Coincident(g2,g1)
    c: Vertical(g2)
    c: Coincident(g3,g2)
    c: Coincident(g3,g0)
    c: Horizontal(g3)
    c: DistanceX(g1,g1) = 2.4
    c: DistanceY(g2,g2) = 2.4
    c: Symmetric(g0,g0,g-1)
    c: DistanceX(g-1,g0) = 3
FEATURE [Sketcher::SketchObject] Sketch045  label="blocco principale per neopixel"
  ArcFitTolerance = 1e-06
  AttachmentSupport = -> [XZ_Plane002]
  ExternalGeometry = -> [Sketch048]
  FullyConstrained = true
  MakeInternals = false
  MapMode = 5
  Placement = pos=(0,0,0) rot=(1,0,0;1.5708rad)
  sketch-geometry (6):
    g0: LineSegment StartX=0 StartY=5.1 StartZ=0 EndX=0 EndY=-5.1 EndZ=0
    g1: LineSegment StartX=0 StartY=-5.1 StartZ=0 EndX=3 EndY=-5.1 EndZ=0
    g2: LineSegment StartX=7 StartY=-1.1 StartZ=0 EndX=7 EndY=5.1 EndZ=0
    g3: LineSegment StartX=7 StartY=5.1 StartZ=0 EndX=0 EndY=5.1 EndZ=0
    g4: ArcOfCircle CenterX=3 CenterY=-1.1 CenterZ=0 NormalX=0 NormalY=0 NormalZ=1 AngleXU=0 Radius=4 StartAngle=4.71239 EndAngle=6.28319
    g5: GeomPoint [constr] X=7 Y=-5.1 Z=0
  constraints (15):
    c: Vertical(g0)
    c: Coincident(g1,g0)
    c: Horizontal(g1)
    c: Vertical(g2)
    c: Coincident(g3,g2)
    c: Coincident(g3,g0)
    c: Horizontal(g3)
    c: DistanceY(g0,g0) = 10.2
    c: Symmetric(g0,g0,g-1)
    c: DistanceX(g3,g3) = 7
    c: PointOnObject(g5,g2)
    c: PointOnObject(g5,g1)
    c: Tangent(g2,g4) = -1.5708
    c: Tangent(g1,g4) = -1.5708
    c: DistanceX(g-3,g1) = 0
FEATURE [Sketcher::SketchObject] Sketch049  label="rinforzi esterni per corpo neopoixel"
  ArcFitTolerance = 1e-06
  AttachmentSupport = -> [XZ_Plane002]
  ExternalGeometry = -> [Sketch045]
  FullyConstrained = true
  MakeInternals = false
  MapMode = 5
  Placement = pos=(0,0,0) rot=(1,0,0;1.5708rad)
  sketch-geometry (8):
    g0: LineSegment StartX=1 StartY=-4.1 StartZ=0 EndX=2 EndY=-4.1 EndZ=0
    g1: LineSegment StartX=2 StartY=-4.1 StartZ=0 EndX=2 EndY=-5.1 EndZ=0
    g2: LineSegment StartX=2 StartY=-5.1 StartZ=0 EndX=1 EndY=-5.1 EndZ=0
    g3: LineSegment StartX=1 StartY=-5.1 StartZ=0 EndX=1 EndY=-4.1 EndZ=0
    g4: LineSegment StartX=1 StartY=5.1 StartZ=0 EndX=2 EndY=5.1 EndZ=0
    g5: LineSegment StartX=2 StartY=5.1 StartZ=0 EndX=2 EndY=4.1 EndZ=0
    g6: LineSegment StartX=2 StartY=4.1 StartZ=0 EndX=1 EndY=4.1 EndZ=0
    g7: LineSegment StartX=1 StartY=4.1 StartZ=0 EndX=1 EndY=5.1 EndZ=0
  constraints (24):
    c: Horizontal(g0)
    c: Coincident(g1,g0)
    c: Vertical(g1)
    c: Coincident(g2,g1)
    c: Horizontal(g2)
    c: Coincident(g3,g2)
    c: Coincident(g3,g0)
    c: Vertical(g3)
    c: Horizontal(g4)
    c: Coincident(g5,g4)
    c: Vertical(g5)
    c: Coincident(g6,g5)
    c: Horizontal(g6)
    c: Coincident(g7,g6)
    c: Coincident(g7,g4)
    c: Vertical(g7)
    c: DistanceX(g4,g4) = 1
    c: DistanceY(g5,g5) = 1
    c: DistanceX(g0,g0) = 1
    c: DistanceY(g1,g1) = 1
    c: DistanceX(g-3,g4) = 1
    c: DistanceY(g-3,g4) = 0
    c: DistanceX(g-4,g2) = 1
    c: DistanceY(g2,g-4) = 0
FEATURE [Sketcher::SketchObject] Sketch052  label="scavo saldature driver solenoide"
  ArcFitTolerance = 1e-06
  AttachmentSupport = -> [XZ_Plane]
  ExternalGeometry = -> [Sketch038]
  FullyConstrained = true
  MakeInternals = false
  MapMode = 5
  Placement = pos=(0,0,0) rot=(1,0,0;1.5708rad)
  sketch-geometry (4):
    g0: LineSegment StartX=-195.304 StartY=-6.5806 StartZ=0 EndX=-196.994 EndY=-10.2058 EndZ=0
    g1: LineSegment StartX=-196.994 StartY=-10.2058 StartZ=0 EndX=-196.632 EndY=-10.3749 EndZ=0
    g2: LineSegment StartX=-196.632 StartY=-10.3749 StartZ=0 EndX=-194.941 EndY=-6.74965 EndZ=0
    g3: LineSegment StartX=-194.941 StartY=-6.74965 StartZ=0 EndX=-195.304 EndY=-6.5806 EndZ=0
  constraints (11):
    c: Coincident(g1,g0)
    c: Coincident(g2,g1)
    c: Coincident(g3,g2)
    c: Coincident(g3,g0)
    c: Parallel(g2,g0)
    c: Perpendicular(g2,g3)
    c: Perpendicular(g1,g2,g1) = 1.5708
    c: Parallel(g2,g-3)
    c: Distance(g2) = 4
    c: Distance(g3) = 0.4
    c: Coincident(g2,g-3)
FEATURE [Part::Extrusion] Extrude055  label="Extrude scavo saldature driver solenoide"
  Base = -> Sketch052
  Dir = (0,-1,2e-16)
  DirMode = 2
  FaceMakerClass = Part::FaceMakerBullseye
  FaceMakerMode = 3
  LengthFwd = 6
  LengthRev = 0
  Solid = true
  Symmetric = true
FEATURE [Sketcher::SketchObject] Sketch053  label="scavo saldature rumble"
  ArcFitTolerance = 1e-06
  AttachmentSupport = -> [XZ_Plane]
  ExternalGeometry = -> [Sketch019]
  FullyConstrained = true
  MakeInternals = false
  MapMode = 5
  Placement = pos=(0,0,0) rot=(1,0,0;1.5708rad)
  sketch-geometry (4):
    g0: LineSegment StartX=-169.822 StartY=-58.0028 StartZ=0 EndX=-171.058 EndY=-61.807 EndZ=0
    g1: LineSegment StartX=-171.058 StartY=-61.807 StartZ=0 EndX=-169.917 EndY=-62.1778 EndZ=0
    g2: LineSegment StartX=-169.917 StartY=-62.1778 StartZ=0 EndX=-168.681 EndY=-58.3736 EndZ=0
    g3: LineSegment StartX=-168.681 StartY=-58.3736 StartZ=0 EndX=-169.822 EndY=-58.0028 EndZ=0
  constraints (11):
    c: Coincident(g1,g0)
    c: Coincident(g2,g1)
    c: Coincident(g3,g2)
    c: Coincident(g3,g0)
    c: Parallel(g0,g2)
    c: Perpendicular(g3,g0)
    c: Perpendicular(g1,g0)
    c: Parallel(g0,g-3)
    c: Distance(g0) = 4
    c: Coincident(g0,g-3)
    c: Distance(g1) = 1.2
FEATURE [Part::Extrusion] Extrude056  label="Extrude scavo saldature rumble"
  Base = -> Sketch053
  Dir = (0,-1,2e-16)
  DirMode = 2
  FaceMakerClass = Part::FaceMakerBullseye
  FaceMakerMode = 3
  LengthFwd = 8.4
  LengthRev = 0
  Solid = true
  Symmetric = true
FEATURE [Sketcher::SketchObject] Sketch054  label="scavo saldature alimentatore connettore USB"
  ArcFitTolerance = 1e-06
  AttachmentSupport = -> [XZ_Plane]
  ExternalGeometry = -> [Sketch037]
  FullyConstrained = true
  MakeInternals = false
  MapMode = 5
  Placement = pos=(0,0,0) rot=(1,0,0;1.5708rad)
  sketch-geometry (4):
    g0: LineSegment StartX=-209.575 StartY=-80.4316 StartZ=0 EndX=-210.375 EndY=-80.4316 EndZ=0
    g1: LineSegment StartX=-210.375 StartY=-80.4316 StartZ=0 EndX=-210.375 EndY=-72.4316 EndZ=0
    g2: LineSegment StartX=-210.375 StartY=-72.4316 StartZ=0 EndX=-209.575 EndY=-72.4316 EndZ=0
    g3: LineSegment StartX=-209.575 StartY=-72.4316 StartZ=0 EndX=-209.575 EndY=-80.4316 EndZ=0
  constraints (11):
    c: Horizontal(g0)
    c: Coincident(g1,g0)
    c: Vertical(g1)
    c: Coincident(g2,g1)
    c: Horizontal(g2)
    c: Coincident(g3,g2)
    c: Coincident(g3,g0)
    c: Vertical(g3)
    c: DistanceX(g0,g0) = 0.8
    c: DistanceY(g3,g3) = 8
    c: Coincident(g0,g-4)
FEATURE [Part::Extrusion] Extrude057  label="Extrude scavo saldature alimentatore connettore USB"
  Base = -> Sketch054
  Dir = (0,-1,2e-16)
  DirMode = 2
  FaceMakerClass = Part::FaceMakerBullseye
  FaceMakerMode = 3
  LengthFwd = 11
  LengthRev = 0
  Solid = true
  Symmetric = true
FEATURE [Sketcher::SketchObject] Sketch055  label="buco interno per micro switch"
  ArcFitTolerance = 1e-06
  AttachmentSupport = -> [XZ_Plane]
  ExternalGeometry = -> [Sketch]
  FullyConstrained = true
  MakeInternals = false
  MapMode = 5
  Placement = pos=(0,0,0) rot=(1,0,0;1.5708rad)
  sketch-geometry (11):
    g0: LineSegment [constr] StartX=-194.483 StartY=34.2854 StartZ=0 EndX=-196.022 EndY=30.0568 EndZ=0
    g1: LineSegment [constr] StartX=-196.022 StartY=30.0568 StartZ=0 EndX=-197.561 EndY=25.8282 EndZ=0
    g2: LineSegment [constr] StartX=-196.022 StartY=30.0568 StartZ=0 EndX=-194.143 EndY=29.3727 EndZ=0
    g3: LineSegment [constr] StartX=-196.022 StartY=30.0568 StartZ=0 EndX=-197.902 EndY=30.7408 EndZ=0
    g4: LineSegment StartX=-196.362 StartY=34.9694 StartZ=0 EndX=-192.604 EndY=33.6014 EndZ=0
    g5: LineSegment StartX=-199.441 StartY=26.5122 StartZ=0 EndX=-195.682 EndY=25.1441 EndZ=0
    g6: LineSegment StartX=-192.604 StartY=33.6014 StartZ=0 EndX=-195.682 EndY=25.1441 EndZ=0
    g7: LineSegment StartX=-196.362 StartY=34.9694 StartZ=0 EndX=-199.441 EndY=26.5122 EndZ=0
    g8: GeomPoint [constr] X=-187.821 Y=29.2 Z=0
    g9: LineSegment [constr] StartX=-188.505 StartY=27.3206 StartZ=0 EndX=-196.022 EndY=30.0568 EndZ=0
    g10: LineSegment [constr] StartX=-187.821 StartY=29.2 StartZ=0 EndX=-188.505 EndY=27.3206 EndZ=0
  constraints (27):
    c: Coincident(g2,g0)
    c: Parallel(g0,g-3)
    c: Tangent(g1,g0) = -1.5708
    c: Perpendicular(g0,g2)
    c: Tangent(g2,g3)
    c: Distance(g0,g1) = 9
    c: Equal(g0,g1)
    c: Distance(g3,g2) = 4
    c: Equal(g2,g3)
    c: Parallel(g3,g4)
    c: Symmetric(g4,g4,g0)
    c: Parallel(g6,g1)
    c: Parallel(g7,g1)
    c: Symmetric(g6,g6,g2)
    c: Symmetric(g5,g5,g1)
    c: Symmetric(g7,g7,g3)
    c: Coincident(g7,g4)
    c: Coincident(g6,g4)
    c: Coincident(g5,g6)
    c: Symmetric(g-3,g-3,g8)
    c: Perpendicular(g-3,g9)
    c: Distance(g9) = 8
    c: Coincident(g3,g9)
    c: Coincident(g10,g8)
    c: Parallel(g10,g-3)
    c: Distance(g10) = 2
    c: Coincident(g10,g9)
FEATURE [Sketcher::SketchObject] Sketch056  label="buco esterno per micro switch"
  ArcFitTolerance = 1e-06
  AttachmentSupport = -> [XZ_Plane]
  ExternalGeometry = -> [Sketch055]
  FullyConstrained = true
  MakeInternals = false
  MapMode = 5
  Placement = pos=(0,0,0) rot=(1,0,0;1.5708rad)
  sketch-geometry (17):
    g0: GeomPoint [constr] X=-194.143 Y=29.3727 Z=0
    g1: GeomPoint [constr] X=-194.483 Y=34.2854 Z=0
    g2: GeomPoint [constr] X=-197.902 Y=30.7408 Z=0
    g3: GeomPoint [constr] X=-197.561 Y=25.8282 Z=0
    g4: GeomPoint [constr] X=-196.022 Y=30.0568 Z=0
    g5: LineSegment [constr] StartX=-194.483 StartY=34.2854 StartZ=0 EndX=-196.022 EndY=30.0568 EndZ=0
    g6: LineSegment [constr] StartX=-196.022 StartY=30.0568 StartZ=0 EndX=-197.561 EndY=25.8282 EndZ=0
    g7: LineSegment [constr] StartX=-197.902 StartY=30.7408 StartZ=0 EndX=-196.022 EndY=30.0568 EndZ=0
    g8: LineSegment [constr] StartX=-196.022 StartY=30.0568 StartZ=0 EndX=-194.143 EndY=29.3727 EndZ=0
    g9: LineSegment [constr] StartX=-195.338 StartY=31.9362 StartZ=0 EndX=-196.022 EndY=30.0568 EndZ=0
    g10: LineSegment [constr] StartX=-196.022 StartY=30.0568 StartZ=0 EndX=-196.706 EndY=28.1774 EndZ=0
    g11: LineSegment [constr] StartX=-196.022 StartY=30.0568 StartZ=0 EndX=-196.821 EndY=30.3475 EndZ=0
    g12: LineSegment [constr] StartX=-196.022 StartY=30.0568 StartZ=0 EndX=-195.223 EndY=29.7661 EndZ=0
    g13: LineSegment StartX=-194.539 StartY=31.6454 StartZ=0 EndX=-195.907 EndY=27.8867 EndZ=0
    g14: LineSegment StartX=-196.137 StartY=32.2269 StartZ=0 EndX=-197.505 EndY=28.4681 EndZ=0
    g15: LineSegment StartX=-196.137 StartY=32.2269 StartZ=0 EndX=-194.539 EndY=31.6454 EndZ=0
    g16: LineSegment StartX=-197.505 StartY=28.4681 StartZ=0 EndX=-195.907 EndY=27.8867 EndZ=0
  constraints (34):
    c: Symmetric(g-5,g-5,g1)
    c: Symmetric(g-5,g-6,g0)
    c: Symmetric(g-6,g-6,g3)
    c: Symmetric(g-5,g-6,g2)
    c: Coincident(g5,g1)
    c: Coincident(g5,g4)
    c: Coincident(g6,g4)
    c: Coincident(g6,g3)
    c: Equal(g5,g6)
    c: Coincident(g7,g2)
    c: Coincident(g7,g4)
    c: Coincident(g8,g4)
    c: Coincident(g8,g0)
    c: Equal(g7,g8)
    c: Coincident(g11,g9)
    c: Coincident(g12,g9)
    c: Tangent(g10,g9) = -1.5708
    c: Perpendicular(g11,g9)
    c: Parallel(g9,g-4)
    c: Equal(g9,g10)
    c: Parallel(g12,g11)
    c: Equal(g11,g12)
    c: Distance(g11,g12) = 1.7
    c: Distance(g9,g10) = 4
    c: Symmetric(g13,g13,g12)
    c: Parallel(g13,g9)
    c: Symmetric(g14,g14,g11)
    c: Symmetric(g15,g15,g9)
    c: Parallel(g15,g11)
    c: Symmetric(g16,g16,g10)
    c: Coincident(g16,g14)
    c: Coincident(g15,g14)
    c: Coincident(g13,g15)
    c: Coincident(g9,g4)
FEATURE [Sketcher::SketchObject] Sketch057  label="buco interno per SWITCH"
  ArcFitTolerance = 1e-06
  AttachmentSupport = -> [XZ_Plane]
  ExternalGeometry = -> [Sketch]
  FullyConstrained = true
  MakeInternals = false
  MapMode = 5
  Placement = pos=(0,0,0) rot=(1,0,0;1.5708rad)
  sketch-geometry (10):
    g0: GeomPoint [constr] X=-187.821 Y=29.2 Z=0
    g1: LineSegment [constr] StartX=-188.505 StartY=27.3206 StartZ=0 EndX=-193.203 EndY=29.0307 EndZ=0
    g2: LineSegment [constr] StartX=-190.809 StartY=35.6086 StartZ=0 EndX=-195.597 EndY=22.4529 EndZ=0
    g3: GeomPoint [constr] X=-193.203 Y=29.0307 Z=0
    g4: LineSegment [constr] StartX=-196.492 StartY=30.2278 StartZ=0 EndX=-189.914 EndY=27.8336 EndZ=0
    g5: LineSegment StartX=-194.098 StartY=36.8056 StartZ=0 EndX=-187.52 EndY=34.4115 EndZ=0
    g6: LineSegment StartX=-194.098 StartY=36.8056 StartZ=0 EndX=-198.886 EndY=23.6499 EndZ=0
    g7: LineSegment StartX=-187.52 StartY=34.4115 StartZ=0 EndX=-192.308 EndY=21.2558 EndZ=0
    g8: LineSegment StartX=-198.886 StartY=23.6499 StartZ=0 EndX=-192.308 EndY=21.2558 EndZ=0
    g9: LineSegment [constr] StartX=-187.821 StartY=29.2 StartZ=0 EndX=-188.505 EndY=27.3206 EndZ=0
  constraints (23):
    c: Symmetric(g-3,g-3,g0)
    c: Perpendicular(g1,g-3)
    c: Parallel(g2,g-3)
    c: Symmetric(g2,g2,g3)
    c: Perpendicular(g2,g4)
    c: Symmetric(g4,g4,g3)
    c: Distance(g2) = 14
    c: Distance(g4) = 7
    c: Distance(g1) = 5
    c: Parallel(g5,g4)
    c: Parallel(g7,g2)
    c: Symmetric(g5,g5,g2)
    c: Symmetric(g6,g6,g4)
    c: Symmetric(g7,g7,g4)
    c: Symmetric(g8,g8,g2)
    c: Coincident(g6,g5)
    c: Coincident(g7,g5)
    c: Coincident(g8,g7)
    c: Coincident(g3,g1)
    c: Coincident(g9,g0)
    c: Parallel(g9,g-3)
    c: Distance(g9) = 2
    c: Coincident(g1,g9)
FEATURE [Sketcher::SketchObject] Sketch058  label="buco esterno per SWITCH"
  ArcFitTolerance = 1e-06
  AttachmentSupport = -> [XZ_Plane]
  ExternalGeometry = -> [Sketch057]
  FullyConstrained = true
  MakeInternals = false
  MapMode = 5
  Placement = pos=(0,0,0) rot=(1,0,0;1.5708rad)
  sketch-geometry (12):
    g0: GeomPoint [constr] X=-190.809 Y=35.6086 Z=0
    g1: GeomPoint [constr] X=-196.492 Y=30.2278 Z=0
    g2: GeomPoint [constr] X=-189.914 Y=27.8336 Z=0
    g3: GeomPoint [constr] X=-195.597 Y=22.4529 Z=0
    g4: GeomPoint [constr] X=-193.203 Y=29.0307 Z=0
    g5: LineSegment [constr] StartX=-192.006 StartY=32.3196 StartZ=0 EndX=-194.4 EndY=25.7418 EndZ=0
    g6: GeomPoint [constr] X=-193.203 Y=29.0307 Z=0
    g7: LineSegment [constr] StartX=-195.082 StartY=29.7148 StartZ=0 EndX=-191.324 EndY=28.3467 EndZ=0
    g8: LineSegment StartX=-193.885 StartY=33.0037 StartZ=0 EndX=-190.127 EndY=31.6356 EndZ=0
    g9: LineSegment StartX=-190.127 StartY=31.6356 StartZ=0 EndX=-192.521 EndY=25.0578 EndZ=0
    g10: LineSegment StartX=-196.28 StartY=26.4258 StartZ=0 EndX=-192.521 EndY=25.0578 EndZ=0
    g11: LineSegment StartX=-193.885 StartY=33.0037 StartZ=0 EndX=-196.28 EndY=26.4258 EndZ=0
  constraints (21):
    c: Symmetric(g-6,g-6,g3)
    c: Symmetric(g-4,g-6,g2)
    c: Symmetric(g-5,g-4,g0)
    c: Symmetric(g-5,g-6,g1)
    c: Symmetric(g1,g2,g4)
    c: Parallel(g5,g-4)
    c: Symmetric(g5,g5,g6)
    c: Perpendicular(g7,g5)
    c: Symmetric(g7,g7,g6)
    c: Distance(g5) = 7
    c: Distance(g7) = 4
    c: Parallel(g8,g7)
    c: Parallel(g11,g5)
    c: Symmetric(g8,g8,g5)
    c: Symmetric(g9,g9,g7)
    c: Symmetric(g10,g10,g5)
    c: Symmetric(g11,g11,g7)
    c: Coincident(g11,g8)
    c: Coincident(g9,g8)
    c: Coincident(g9,g10)
    c: Coincident(g6,g4)
FEATURE [Part::Extrusion] Extrude060  label="Extrude buco interno per SWITCH destro"
  Base = -> Sketch057
  Dir = (0,-1,2e-16)
  DirMode = 2
  FaceMakerClass = Part::FaceMakerBullseye
  FaceMakerMode = 3
  LengthFwd = 13.2
  LengthRev = 0
  Placement = pos=(0,2.6,0) rot=(0,0,1;0rad)
  Solid = true
  Symmetric = false
FEATURE [Part::Extrusion] Extrude061  label="Extrude buco esterno per SWITCH destro"
  Base = -> Sketch058
  Dir = (0,-1,2e-16)
  DirMode = 2
  FaceMakerClass = Part::FaceMakerBullseye
  FaceMakerMode = 3
  LengthFwd = 2
  LengthRev = 0
  Placement = pos=(0,-10.6,0) rot=(0,0,1;0rad)
  Solid = true
  Symmetric = false
FEATURE [Sketcher::SketchObject] Sketch059  label="buco per spazio introduzione SWITCH"
  ArcFitTolerance = 1e-06
  AttachmentSupport = -> [XZ_Plane]
  ExternalGeometry = -> [Sketch057,Sketch010]
  FullyConstrained = true
  MakeInternals = false
  MapMode = 5
  Placement = pos=(0,0,0) rot=(1,0,0;1.5708rad)
  sketch-geometry (8):
    g0: LineSegment [constr] StartX=-201.368 StartY=36.3521 StartZ=0 EndX=-195.094 EndY=34.0687 EndZ=0
    g1: LineSegment [constr] StartX=-194.098 StartY=36.8056 StartZ=0 EndX=-195.094 EndY=34.0687 EndZ=0
    g2: LineSegment StartX=-198.658 StartY=24.2771 StartZ=0 EndX=-199.654 EndY=21.5401 EndZ=0
    g3: LineSegment StartX=-199.654 StartY=21.5401 StartZ=0 EndX=-181.196 EndY=14.822 EndZ=0
    g4: LineSegment StartX=-181.196 StartY=14.822 StartZ=0 EndX=-180.2 EndY=17.559 EndZ=0
    g5: LineSegment StartX=-180.2 StartY=17.559 StartZ=0 EndX=-198.658 EndY=24.2771 EndZ=0
    g6: LineSegment [constr] StartX=-204.932 StartY=26.5605 StartZ=0 EndX=-198.658 EndY=24.2771 EndZ=0
    g7: LineSegment [constr] StartX=-198.658 StartY=24.2771 StartZ=0 EndX=-199.654 EndY=21.5401 EndZ=0
  constraints (20):
    c: Parallel(g1,g-3)
    c: Parallel(g0,g-4)
    c: Coincident(g0,g-4)
    c: Coincident(g1,g-3)
    c: Coincident(g0,g1)
    c: Coincident(g3,g2)
    c: Coincident(g4,g3)
    c: Coincident(g5,g4)
    c: Coincident(g5,g2)
    c: Parallel(g5,g-5)
    c: Parallel(g3,g-5)
    c: Parallel(g4,g-6)
    c: DistanceX(g-6,g4) = 0
    c: Coincident(g6,g-5)
    c: Equal(g6,g0)
    c: Coincident(g7,g6)
    c: Equal(g7,g1)
    c: Tangent(g7,g-3)
    c: Coincident(g2,g6)
    c: Coincident(g2,g7)
FEATURE [Part::Extrusion] Extrude062  label="Extrude buco per spazio introduzione SWITCH"
  Base = -> Sketch059
  Dir = (0,-1,2e-16)
  DirMode = 2
  FaceMakerClass = Part::FaceMakerBullseye
  FaceMakerMode = 3
  LengthFwd = 13.2
  LengthRev = 0
  Solid = true
  Symmetric = true
FEATURE [Part::Extrusion] Extrude063  label="Extrude buco interno per SWITCH sinistro"
  Base = -> Sketch057
  Dir = (0,-1,2e-16)
  DirMode = 2
  FaceMakerClass = Part::FaceMakerBullseye
  FaceMakerMode = 3
  LengthFwd = 13.2
  LengthRev = 0
  Placement = pos=(0,10.6,0) rot=(0,0,1;0rad)
  Solid = true
  Symmetric = false
FEATURE [Part::Extrusion] Extrude064  label="Extrude buco esterno per SWITCH sinistro"
  Base = -> Sketch058
  Dir = (0,-1,2e-16)
  DirMode = 2
  FaceMakerClass = Part::FaceMakerBullseye
  FaceMakerMode = 3
  LengthFwd = 2
  LengthRev = 0
  Placement = pos=(0,12.6,0) rot=(0,0,1;0rad)
  Solid = true
  Symmetric = false
FEATURE [Sketcher::SketchObject] Sketch061  label="struttura esterna blocco switch"
  ArcFitTolerance = 1e-06
  AttachmentSupport = -> [XZ_Plane003]
  FullyConstrained = true
  MakeInternals = false
  MapMode = 5
  Placement = pos=(0,0,0) rot=(1,0,0;1.5708rad)
  sketch-geometry (5):
    g0: LineSegment StartX=-1 StartY=-5.1 StartZ=0 EndX=1 EndY=-5.1 EndZ=0
    g1: LineSegment StartX=1 StartY=-5.1 StartZ=0 EndX=1 EndY=5.1 EndZ=0
    g2: LineSegment StartX=1 StartY=5.1 StartZ=0 EndX=-1 EndY=5.1 EndZ=0
    g3: LineSegment StartX=-1 StartY=5.1 StartZ=0 EndX=-1 EndY=-5.1 EndZ=0
    g4: GeomPoint [constr] X=0 Y=0 Z=0
  constraints (12):
    c: Coincident(g0,g1)
    c: Coincident(g1,g2)
    c: Coincident(g2,g3)
    c: Coincident(g3,g0)
    c: Horizontal(g0)
    c: Horizontal(g2)
    c: Vertical(g1)
    c: Vertical(g3)
    c: Symmetric(g2,g0,g4)
    c: Distance(g1,g3) = 2
    c: Distance(g0,g2) = 10.2
    c: Coincident(g4,g-1)
FEATURE [Sketcher::SketchObject] Sketch062  label="struttura interna blocco switch"
  ArcFitTolerance = 1e-06
  AttachmentSupport = -> [XZ_Plane003]
  ExternalGeometry = -> [Sketch061]
  FullyConstrained = true
  MakeInternals = false
  MapMode = 5
  Placement = pos=(0,0,0) rot=(1,0,0;1.5708rad)
  sketch-geometry (5):
    g0: LineSegment StartX=-1 StartY=3.1 StartZ=0 EndX=-1 EndY=-3.1 EndZ=0
    g1: LineSegment StartX=-1 StartY=-3.1 StartZ=0 EndX=1 EndY=-3.1 EndZ=0
    g2: LineSegment StartX=1 StartY=-3.1 StartZ=0 EndX=1 EndY=3.1 EndZ=0
    g3: LineSegment StartX=1 StartY=3.1 StartZ=0 EndX=-1 EndY=3.1 EndZ=0
    g4: GeomPoint [constr] X=0 Y=0 Z=0
  constraints (12):
    c: Coincident(g0,g1)
    c: Coincident(g1,g2)
    c: Coincident(g2,g3)
    c: Coincident(g3,g0)
    c: Vertical(g0)
    c: Vertical(g2)
    c: Horizontal(g1)
    c: Horizontal(g3)
    c: Symmetric(g2,g0,g4)
    c: Coincident(g4,g-1)
    c: Distance(g0) = 6.2
    c: Equal(g3,g-3)
FEATURE [Sketcher::SketchObject] Sketch063  label="blocchi tra switch"
  ArcFitTolerance = 1e-06
  AttachmentSupport = -> [XZ_Plane003]
  ExternalGeometry = -> [Sketch061,Sketch062]
  FullyConstrained = true
  MakeInternals = false
  MapMode = 5
  Placement = pos=(0,0,0) rot=(1,0,0;1.5708rad)
  sketch-geometry (8):
    g0: LineSegment StartX=-3 StartY=5.1 StartZ=0 EndX=-1 EndY=5.1 EndZ=0
    g1: LineSegment StartX=-1 StartY=5.1 StartZ=0 EndX=-1 EndY=3.1 EndZ=0
    g2: LineSegment StartX=-1 StartY=3.1 StartZ=0 EndX=-3 EndY=3.1 EndZ=0
    g3: LineSegment StartX=-3 StartY=3.1 StartZ=0 EndX=-3 EndY=5.1 EndZ=0
    g4: LineSegment StartX=-3 StartY=-3.1 StartZ=0 EndX=-1 EndY=-3.1 EndZ=0
    g5: LineSegment StartX=-1 StartY=-3.1 StartZ=0 EndX=-1 EndY=-5.1 EndZ=0
    g6: LineSegment StartX=-1 StartY=-5.1 StartZ=0 EndX=-3 EndY=-5.1 EndZ=0
    g7: LineSegment StartX=-3 StartY=-5.1 StartZ=0 EndX=-3 EndY=-3.1 EndZ=0
  constraints (20):
    c: Horizontal(g0)
    c: Coincident(g1,g0)
    c: Coincident(g2,g1)
    c: Horizontal(g2)
    c: Coincident(g3,g2)
    c: Coincident(g3,g0)
    c: Vertical(g3)
    c: Horizontal(g4)
    c: Coincident(g5,g4)
    c: Coincident(g6,g5)
    c: Horizontal(g6)
    c: Coincident(g7,g6)
    c: Coincident(g7,g4)
    c: Vertical(g7)
    c: Coincident(g0,g-4)
    c: Coincident(g1,g-5)
    c: Coincident(g4,g-6)
    c: Coincident(g5,g-7)
    c: Distance(g0) = 2
    c: Distance(g4) = 2
FEATURE [Sketcher::SketchObject] Sketch066  label="piano per rampino"
  ArcFitTolerance = 1e-06
  AttachmentSupport = -> [XZ_Plane002]
  ExternalGeometry = -> [Sketch045]
  FullyConstrained = true
  MakeInternals = false
  MapMode = 5
  Placement = pos=(0,0,0) rot=(1,0,0;1.5708rad)
  sketch-geometry (4):
    g0: LineSegment StartX=5.4 StartY=5.1 StartZ=0 EndX=5.4 EndY=3.9 EndZ=0
    g1: LineSegment StartX=5.4 StartY=3.9 StartZ=0 EndX=7 EndY=3.9 EndZ=0
    g2: LineSegment StartX=7 StartY=3.9 StartZ=0 EndX=7 EndY=5.1 EndZ=0
    g3: LineSegment StartX=7 StartY=5.1 StartZ=0 EndX=5.4 EndY=5.1 EndZ=0
  constraints (11):
    c: Coincident(g0,g1)
    c: Coincident(g1,g2)
    c: Coincident(g2,g3)
    c: Coincident(g3,g0)
    c: Vertical(g0)
    c: Vertical(g2)
    c: Horizontal(g1)
    c: Horizontal(g3)
    c: Distance(g0,g2) = 1.6
    c: Distance(g1,g3) = 1.2
    c: Coincident(g2,g-3)
FEATURE [Sketcher::SketchObject] Sketch064  label="rampini_per_serraggio_struttura"
  ArcFitTolerance = 1e-06
  AttachmentSupport = -> [XZ_Plane002]
  ExternalGeometry = -> [Sketch066,Sketch045]
  FullyConstrained = true
  MakeInternals = false
  MapMode = 5
  Placement = pos=(0,0,0) rot=(1,0,0;1.5708rad)
  sketch-geometry (7):
    g0: LineSegment StartX=7 StartY=5.1 StartZ=0 EndX=7 EndY=3.9 EndZ=0
    g1: LineSegment StartX=7 StartY=3.9 StartZ=0 EndX=9 EndY=3.9 EndZ=0
    g2: LineSegment StartX=7 StartY=5.1 StartZ=0 EndX=7 EndY=5.1 EndZ=0
    g3: LineSegment StartX=7 StartY=5.1 StartZ=0 EndX=7 EndY=7.5 EndZ=0
    g4: LineSegment StartX=9 StartY=5.1 StartZ=0 EndX=9 EndY=3.9 EndZ=0
    g5: LineSegment StartX=7 StartY=7.5 StartZ=0 EndX=9 EndY=7.5 EndZ=0
    g6: LineSegment StartX=9 StartY=7.5 StartZ=0 EndX=9 EndY=5.1 EndZ=0
  constraints (20):
    c: Vertical(g0)
    c: Coincident(g1,g0)
    c: Horizontal(g1)
    c: Coincident(g2,g0)
    c: Horizontal(g2)
    c: Coincident(g3,g2)
    c: Vertical(g3)
    c: Coincident(g5,g3)
    c: Coincident(g4,g6)
    c: Coincident(g4,g1)
    c: Vertical(g4)
    c: Coincident(g0,g-3)
    c: DistanceY(g-4,g3) = 2.4
    c: DistanceX(g1,g1) = 2
    c: DistanceY(g2,g6) = 0
    c: DistanceX(g2,g2) = 0
    c: DistanceY(g0,g0) = 1.2
    c: Coincident(g5,g6)
    c: Horizontal(g5)
    c: Vertical(g6)
FEATURE [Sketcher::SketchObject] Sketch067  label="perno per blocco switch"
  ArcFitTolerance = 1e-06
  AttachmentSupport = -> [XZ_Plane]
  ExternalGeometry = -> [Sketch,Sketch010]
  FullyConstrained = true
  MakeInternals = false
  MapMode = 5
  Placement = pos=(0,0,0) rot=(1,0,0;1.5708rad)
  sketch-geometry (14):
    g0: LineSegment StartX=-191.073 StartY=24.9429 StartZ=0 EndX=-185.81 EndY=23.0276 EndZ=0
    g1: LineSegment StartX=-183.76 StartY=23.9839 StartZ=0 EndX=-182.392 EndY=27.7427 EndZ=0
    g2: LineSegment StartX=-183.348 StartY=29.7934 StartZ=0 EndX=-188.61 EndY=31.7087 EndZ=0
    g3: LineSegment StartX=-188.61 StartY=31.7087 StartZ=0 EndX=-191.073 EndY=24.9429 EndZ=0
    g4: GeomPoint [constr] X=-186.459 Y=27.0946 Z=0
    g5: LineSegment StartX=-189.022 StartY=25.8992 StartZ=0 EndX=-185.263 EndY=24.5311 EndZ=0
    g6: LineSegment StartX=-185.263 StartY=24.5311 StartZ=0 EndX=-183.895 EndY=28.2899 EndZ=0
    g7: LineSegment StartX=-183.895 StartY=28.2899 StartZ=0 EndX=-187.654 EndY=29.658 EndZ=0
    g8: LineSegment StartX=-187.654 StartY=29.658 StartZ=0 EndX=-189.022 EndY=25.8992 EndZ=0
    g9: GeomPoint [constr] X=-186.459 Y=27.0946 Z=0
    g10: ArcOfCircle CenterX=-185.263 CenterY=24.5311 CenterZ=0 NormalX=0 NormalY=0 NormalZ=1 AngleXU=0 Radius=1.6 StartAngle=4.36332 EndAngle=5.93412
    g11: GeomPoint [constr] X=-184.307 Y=22.4804 Z=0
    g12: ArcOfCircle CenterX=-183.895 CenterY=28.2899 CenterZ=0 NormalX=0 NormalY=0 NormalZ=1 AngleXU=0 Radius=1.6 StartAngle=5.93412 EndAngle=7.50492
    g13: GeomPoint [constr] X=-181.844 Y=29.2462 Z=0
  constraints (30):
    c: Coincident(g2,g3)
    c: Coincident(g3,g0)
    c: Symmetric(g13,g0,g4)
    c: Distance(g11,g3) = 7.2
    c: Distance(g0,g2) = 7.2
    c: Parallel(g3,g1)
    c: Parallel(g2,g0)
    c: Perpendicular(g2,g3)
    c: Coincident(g5,g6)
    c: Coincident(g6,g7)
    c: Coincident(g7,g8)
    c: Coincident(g8,g5)
    c: Symmetric(g7,g5,g9)
    c: Distance(g6,g8) = 4
    c: Distance(g5,g7) = 4
    c: Coincident(g9,g4)
    c: Parallel(g8,g6)
    c: Parallel(g7,g5)
    c: Perpendicular(g7,g8)
    c: Tangent(g8,g-3)
    c: Tangent(g2,g-4)
    c: PointOnObject(g11,g1)
    c: PointOnObject(g11,g0)
    c: Tangent(g1,g10) = -1.5708
    c: Tangent(g0,g10) = -1.5708
    c: PointOnObject(g13,g1)
    c: Tangent(g1,g12) = -1.5708
    c: Tangent(g2,g12) = -1.5708
    c: Equal(g10,g12)
    c: Coincident(g10,g5)
FEATURE [Part::Extrusion] Extrude072  label="Extrude perno per blocco switch"
  Base = -> Sketch067
  Dir = (0,-1,2e-16)
  DirMode = 2
  FaceMakerClass = Part::FaceMakerBullseye
  FaceMakerMode = 3
  LengthFwd = 25.2
  LengthRev = 0
  Solid = true
  Symmetric = true
FEATURE [Part::MultiFuse] Fusion
  Refine = true
  Shapes = -> [Extrude,Sweep,Extrude007,Extrude011,Extrude005,Extrude012,Extrude013,Extrude016,Extrude031,Extrude039,Extrude045,Extrude072]
FEATURE [Part::Cut] Cut
  Base = -> Fusion
  Refine = true
  Tool = -> Extrude001
FEATURE [Part::Cut] Cut001
  Base = -> Cut
  Refine = true
  Tool = -> Extrude004
FEATURE [Part::Cut] Cut002
  Base = -> Cut001
  Refine = true
  Tool = -> Extrude006
FEATURE [Part::Cut] Cut003
  Base = -> Cut002
  Refine = true
  Tool = -> Extrude008
FEATURE [Part::Cut] Cut004
  Base = -> Cut003
  Refine = true
  Tool = -> Extrude009
FEATURE [Part::Cut] Cut005
  Base = -> Cut004
  Refine = true
  Tool = -> Extrude010
FEATURE [Part::Cut] Cut006
  Base = -> Cut005
  Refine = true
  Tool = -> Extrude014
FEATURE [Part::Cut] Cut007
  Base = -> Cut006
  Refine = true
  Tool = -> Extrude015
FEATURE [Part::Cut] Cut008
  Base = -> Cut007
  Refine = true
  Tool = -> Extrude018
FEATURE [Part::Cut] Cut009
  Base = -> Cut008
  Refine = true
  Tool = -> Extrude019
FEATURE [Part::Cut] Cut010
  Base = -> Cut009
  Refine = true
  Tool = -> Extrude020
FEATURE [Part::Cut] Cut011
  Base = -> Cut010
  Refine = true
  Tool = -> Extrude021
FEATURE [Part::Cut] Cut012
  Base = -> Cut011
  Refine = true
  Tool = -> Extrude022
FEATURE [Part::Cut] Cut013
  Base = -> Cut012
  Refine = true
  Tool = -> Extrude023
FEATURE [Part::Cut] Cut014
  Base = -> Cut013
  Refine = true
  Tool = -> Extrude032
FEATURE [Part::Cut] Cut015
  Base = -> Cut014
  Refine = true
  Tool = -> Extrude033
FEATURE [Part::Cut] Cut016
  Base = -> Cut015
  Refine = true
  Tool = -> Extrude034
FEATURE [Part::Cut] Cut017
  Base = -> Cut016
  Refine = true
  Tool = -> Extrude035
FEATURE [Part::Cut] Cut018
  Base = -> Cut017
  Refine = true
  Tool = -> Extrude036
FEATURE [Part::Cut] Cut019
  Base = -> Cut018
  Refine = true
  Tool = -> Extrude037
FEATURE [Part::Cut] Cut020
  Base = -> Cut019
  Refine = true
  Tool = -> Extrude030
FEATURE [Part::Cut] Cut022
  Base = -> Cut020
  Refine = true
  Tool = -> Extrude038
FEATURE [Part::Cut] Cut023
  Base = -> Cut022
  Refine = true
  Tool = -> Extrude041
FEATURE [Part::Cut] Cut024
  Base = -> Cut023
  Refine = true
  Tool = -> Extrude040
FEATURE [Part::Cut] Cut025
  Base = -> Cut024
  Refine = true
  Tool = -> Extrude042
FEATURE [Part::Cut] Cut026
  Base = -> Cut025
  Refine = true
  Tool = -> Extrude043
FEATURE [Part::Cut] Cut027
  Base = -> Cut026
  Refine = true
  Tool = -> Extrude044
FEATURE [Part::Cut] Cut028
  Base = -> Cut027
  Refine = true
  Tool = -> Extrude046
FEATURE [Part::Cut] Cut029
  Base = -> Cut028
  Refine = true
  Tool = -> Extrude047
FEATURE [Part::Cut] Cut033
  Base = -> Cut029
  Refine = true
  Tool = -> Extrude055
FEATURE [Part::Cut] Cut034
  Base = -> Cut033
  Refine = true
  Tool = -> Extrude056
FEATURE [Part::Cut] Cut035
  Base = -> Cut034
  Refine = true
  Tool = -> Extrude057
FEATURE [Part::Cut] Cut037
  Base = -> Cut035
  Refine = true
  Tool = -> Extrude060
FEATURE [Part::Cut] Cut038
  Base = -> Cut037
  Refine = true
  Tool = -> Extrude061
FEATURE [Part::Cut] Cut039
  Base = -> Cut038
  Refine = true
  Tool = -> Extrude063
FEATURE [Part::Cut] Cut040
  Base = -> Cut039
  Refine = true
  Tool = -> Extrude064
FEATURE [Part::Cut] Cut041
  Base = -> Cut040
  Refine = true
  Tool = -> Extrude062
FEATURE [Sketcher::SketchObject] Sketch068  label="base con smusso sopra neopixel"
  ArcFitTolerance = 1e-06
  AttachmentSupport = -> [YZ_Plane002]
  FullyConstrained = true
  MakeInternals = false
  MapMode = 5
  Placement = pos=(0,0,0) rot=(0.57735,0.57735,0.57735;2.0944rad)
  sketch-geometry (5):
    g0: LineSegment StartX=-9.5 StartY=-6.1 StartZ=0 EndX=9.5 EndY=-6.1 EndZ=0
    g1: LineSegment StartX=9.5 StartY=-6.1 StartZ=0 EndX=9.5 EndY=6.1 EndZ=0
    g2: LineSegment StartX=9.5 StartY=6.1 StartZ=0 EndX=-9.5 EndY=6.1 EndZ=0
    g3: LineSegment StartX=-9.5 StartY=6.1 StartZ=0 EndX=-9.5 EndY=-6.1 EndZ=0
    g4: GeomPoint [constr] X=0 Y=0 Z=0
  constraints (12):
    c: Coincident(g0,g1)
    c: Coincident(g1,g2)
    c: Coincident(g2,g3)
    c: Coincident(g3,g0)
    c: Horizontal(g0)
    c: Horizontal(g2)
    c: Vertical(g1)
    c: Vertical(g3)
    c: Symmetric(g2,g0,g4)
    c: Distance(g1,g3) = 19
    c: Distance(g0,g2) = 12.2
    c: Coincident(g4,g-1)
FEATURE [Sketcher::SketchObject] Sketch069  label="cilindro minore"
  ArcFitTolerance = 1e-06
  AttachmentSupport = -> [XZ_Plane004]
  FullyConstrained = true
  MakeInternals = false
  MapMode = 5
  Placement = pos=(0,0,0) rot=(1,0,0;1.5708rad)
  sketch-geometry (1):
    g0: Circle CenterX=0 CenterY=0 CenterZ=0 NormalX=0 NormalY=0 NormalZ=1 AngleXU=0 Radius=5.8
  constraints (2):
    c: Diameter(g0) = 11.6
    c: Coincident(g0,g-1)
FEATURE [Sketcher::SketchObject] Sketch070  label="cilindro maggiore"
  ArcFitTolerance = 1e-06
  AttachmentSupport = -> [XZ_Plane004]
  ExternalGeometry = -> [Sketch069]
  FullyConstrained = true
  MakeInternals = false
  MapMode = 5
  Placement = pos=(0,0,0) rot=(1,0,0;1.5708rad)
  sketch-geometry (1):
    g0: Circle CenterX=0 CenterY=0 CenterZ=0 NormalX=0 NormalY=0 NormalZ=1 AngleXU=0 Radius=6.5
  constraints (2):
    c: Coincident(g0,g-1)
    c: Diameter(g0) = 13
FEATURE [Sketcher::SketchObject] Sketch071  label="buco interno"
  ArcFitTolerance = 1e-06
  AttachmentSupport = -> [XZ_Plane004]
  ExternalGeometry = -> [Sketch069]
  FullyConstrained = true
  MakeInternals = false
  MapMode = 5
  Placement = pos=(0,0,0) rot=(1,0,0;1.5708rad)
  sketch-geometry (1):
    g0: Circle CenterX=0 CenterY=0 CenterZ=0 NormalX=0 NormalY=0 NormalZ=1 AngleXU=0 Radius=5
  constraints (2):
    c: Coincident(g0,g-1)
    c: Diameter(g0) = 10
FEATURE [PartDesign::Pad] Pad
  Direction = (0,-1,2e-16)
  Length = 1.2
  Length2 = 10
  Placement = pos=(0,0,0) rot=(1,0,0;1.5708rad)
  Profile = -> Sketch070
  ReferenceAxis = -> Sketch070 [N_Axis]
  Refine = true
  Suppressed = false
  Type = 0
FEATURE [PartDesign::Pad] Pad001
  BaseFeature = -> Pad
  Direction = (0,-1,2e-16)
  Length = 5.6
  Length2 = 10
  Placement = pos=(0,0,0) rot=(1,0,0;1.5708rad)
  Profile = -> Sketch069
  ReferenceAxis = -> Sketch069 [N_Axis]
  Refine = true
  Suppressed = false
  Type = 0
FEATURE [PartDesign::Pocket] Pocket
  BaseFeature = -> Pad001
  Direction = (0,1,-2e-16)
  Length = 7
  Length2 = 5
  Midplane = true
  Placement = pos=(0,0,0) rot=(1,0,0;1.5708rad)
  Profile = -> Sketch071
  ReferenceAxis = -> Sketch071 [N_Axis]
  Refine = true
  Suppressed = false
  Type = 0
FEATURE [PartDesign::Fillet] Fillet
  Base = -> Pocket [Face7]
  BaseFeature = -> Pocket
  Placement = pos=(0,0,0) rot=(1,0,0;1.5708rad)
  Radius = 1
  Refine = true
  SupportTransform = false
  Suppressed = false
  UseAllEdges = false
FEATURE [PartDesign::Body] Body004  label="pulsanti lato sinistro"
  AllowCompound = false
  Group = -> [Sketch069,Sketch070,Sketch071,Pad,Pad001,Pocket,Fillet]
  Origin = -> Origin004
  Tip = -> Fillet
FEATURE [Sketcher::SketchObject] Sketch072  label="buco per saldature e diodo driver solenoide"
  ArcFitTolerance = 1e-06
  AttachmentSupport = -> [XZ_Plane]
  ExternalGeometry = -> [Sketch038]
  FullyConstrained = true
  MakeInternals = false
  MapMode = 5
  Placement = pos=(0,0,0) rot=(1,0,0;1.5708rad)
  sketch-geometry (4):
    g0: LineSegment StartX=-212.269 StartY=-43.9083 StartZ=0 EndX=-207.197 EndY=-33.0326 EndZ=0
    g1: LineSegment StartX=-207.197 StartY=-33.0326 StartZ=0 EndX=-207.56 EndY=-32.8635 EndZ=0
    g2: LineSegment StartX=-207.56 StartY=-32.8635 StartZ=0 EndX=-212.631 EndY=-43.7392 EndZ=0
    g3: LineSegment StartX=-212.631 StartY=-43.7392 StartZ=0 EndX=-212.269 EndY=-43.9083 EndZ=0
  constraints (11):
    c: Coincident(g1,g0)
    c: Coincident(g2,g1)
    c: Coincident(g3,g2)
    c: Coincident(g3,g0)
    c: Parallel(g-3,g0)
    c: Parallel(g0,g2)
    c: Perpendicular(g0,g3)
    c: Perpendicular(g1,g0)
    c: Distance(g3) = 0.4
    c: Distance(g2) = 12
    c: Coincident(g0,g-3)
FEATURE [Part::Extrusion] Extrude074  label="Extrude buco per saldature e diodo driver solenoide"
  Base = -> Sketch072
  Dir = (0,-1,2e-16)
  DirMode = 2
  FaceMakerClass = Part::FaceMakerBullseye
  FaceMakerMode = 3
  LengthFwd = 14.6
  LengthRev = 0
  Solid = true
  Symmetric = true
FEATURE [Part::Cut] Cut042
  Base = -> Cut041
  Refine = true
  Tool = -> Extrude074
FEATURE [Sketcher::SketchObject] Sketch073  label="fori slargati blocco solenoide"
  ArcFitTolerance = 1e-06
  AttachmentSupport = -> [XY_Plane]
  ExternalGeometry = -> [Sketch030]
  FullyConstrained = true
  MakeInternals = false
  MapMode = 5
  sketch-geometry (2):
    g0: Circle CenterX=-152.209 CenterY=6.95 CenterZ=0 NormalX=0 NormalY=0 NormalZ=1 AngleXU=0 Radius=3.7
    g1: Circle CenterX=-130.41 CenterY=-6.95 CenterZ=0 NormalX=0 NormalY=0 NormalZ=1 AngleXU=0 Radius=3.7
  constraints (4):
    c: Diameter(g0) = 7.4
    c: Coincident(g0,g-3)
    c: Diameter(g1) = 7.4
    c: Coincident(g1,g-4)
FEATURE [Part::Extrusion] Extrude075  label="Extrude fori slargati blocco solenoide"
  Base = -> Sketch073
  Dir = (0,0,1)
  DirMode = 2
  FaceMakerClass = Part::FaceMakerBullseye
  FaceMakerMode = 3
  LengthFwd = 1.5
  LengthRev = 0
  Placement = pos=(0,0,36.4) rot=(0,0,1;0rad)
  Solid = true
  Symmetric = false
FEATURE [Part::Cut] Cut043
  Base = -> Cut042
  Refine = true
  Tool = -> Extrude075
FEATURE [Sketcher::SketchObject] Sketch074  label="lato sx pistola"
  ArcFitTolerance = 1e-06
  AttachmentSupport = -> [XZ_Plane]
  ExternalGeometry = -> [Sketch016,Sketch,Sketch058]
  FullyConstrained = true
  MakeInternals = false
  MapMode = 5
  Placement = pos=(0,0,0) rot=(1,0,0;1.5708rad)
  sketch-geometry (37):
    g0: LineSegment StartX=-82.8 StartY=3.2 StartZ=0 EndX=0 EndY=3.2 EndZ=0
    g1: LineSegment StartX=-82.8 StartY=3.2 StartZ=0 EndX=-82.8 EndY=6.2 EndZ=0
    g2: LineSegment [constr] StartX=-107.6 StartY=18 StartZ=0 EndX=-107.6 EndY=20 EndZ=0
    g3: LineSegment [constr] StartX=-132.428 StartY=18 StartZ=0 EndX=-132.428 EndY=20 EndZ=0
    g4: LineSegment StartX=-132.428 StartY=20 StartZ=0 EndX=-107.6 EndY=20 EndZ=0
    g5: ArcOfCircle CenterX=-107.6 CenterY=4 CenterZ=0 NormalX=0 NormalY=0 NormalZ=1 AngleXU=0 Radius=16 StartAngle=0.137937 EndAngle=1.5708
    g6: LineSegment StartX=-82.8 StartY=6.2 StartZ=0 EndX=-91.752 EndY=6.2 EndZ=0
    g7: LineSegment [constr] StartX=-145.743 StartY=8.32624 StartZ=0 EndX=-147.645 EndY=8.94427 EndZ=0
    g8: ArcOfCircle CenterX=-132.428 CenterY=4 CenterZ=0 NormalX=0 NormalY=0 NormalZ=1 AngleXU=0 Radius=16 StartAngle=1.5708 EndAngle=2.82743
    g9: LineSegment StartX=-215.932 StartY=-80.4316 StartZ=0 EndX=-176.685 EndY=-80.4316 EndZ=0
    g10: LineSegment StartX=-147.645 StartY=8.94427 StartZ=0 EndX=-176.685 EndY=-80.4316 EndZ=0
    g11: LineSegment [constr] StartX=-193.988 StartY=-2.33927 StartZ=0 EndX=-192.176 EndY=-3.18451 EndZ=0
    g12: LineSegment [constr] StartX=-217.232 StartY=-52.1862 StartZ=0 EndX=-215.42 EndY=-53.0314 EndZ=0
    g13: LineSegment StartX=-192.176 StartY=-3.18451 StartZ=0 EndX=-215.42 EndY=-53.0314 EndZ=0
    g14: ArcOfCircle CenterX=-184.801 CenterY=-67.3089 CenterZ=0 NormalX=0 NormalY=0 NormalZ=1 AngleXU=0 Radius=33.7833 StartAngle=2.70526 EndAngle=3.54053
    g15: ArcOfCircle CenterX=-207.583 CenterY=4 CenterZ=0 NormalX=0 NormalY=0 NormalZ=1 AngleXU=0 Radius=17 StartAngle=5.84685 EndAngle=7.56663
    g16: LineSegment StartX=-202.765 StartY=20.303 StartZ=0 EndX=-195.887 EndY=39.2 EndZ=0
    g17: LineSegment [constr] StartX=-193.885 StartY=33.0037 StartZ=0 EndX=-197.644 EndY=34.3718 EndZ=0
    g18: LineSegment StartX=-195.887 StartY=39.2 StartZ=0 EndX=0 EndY=39.2 EndZ=0
    g19: LineSegment StartX=0 StartY=3.2 StartZ=0 EndX=0 EndY=39.2 EndZ=0
    g20: LineSegment StartX=-189.939 StartY=31.5672 StartZ=0 EndX=-192.333 EndY=24.9893 EndZ=0
    g21: LineSegment StartX=-196.467 StartY=26.4942 StartZ=0 EndX=-194.073 EndY=33.0721 EndZ=0
    g22: Circle CenterX=-213.443 CenterY=-76.8316 CenterZ=0 NormalX=0 NormalY=0 NormalZ=1 AngleXU=0 Radius=1.8
    g23: Circle CenterX=-179.305 CenterY=-76.8316 CenterZ=0 NormalX=0 NormalY=0 NormalZ=1 AngleXU=0 Radius=1.8
    g24: Circle CenterX=-184.08 CenterY=34.8 CenterZ=0 NormalX=0 NormalY=0 NormalZ=1 AngleXU=0 Radius=1.8
    g25: Circle CenterX=-78.51 CenterY=34.8 CenterZ=0 NormalX=0 NormalY=0 NormalZ=1 AngleXU=0 Radius=1.8
    g26: Circle CenterX=-78.51 CenterY=7.6 CenterZ=0 NormalX=0 NormalY=0 NormalZ=1 AngleXU=0 Radius=1.8
    g27: Circle CenterX=-5.6 CenterY=34.8 CenterZ=0 NormalX=0 NormalY=0 NormalZ=1 AngleXU=0 Radius=1.8
    g28: Circle CenterX=-5.6 CenterY=7.6 CenterZ=0 NormalX=0 NormalY=0 NormalZ=1 AngleXU=0 Radius=1.8
    g29: LineSegment StartX=-190.127 StartY=31.6356 StartZ=0 EndX=-189.939 EndY=31.5672 EndZ=0
    g30: LineSegment StartX=-194.073 StartY=33.0721 StartZ=0 EndX=-193.885 EndY=33.0037 EndZ=0
    g31: LineSegment StartX=-193.885 StartY=33.0037 StartZ=0 EndX=-190.127 EndY=31.6356 EndZ=0
    g32: LineSegment StartX=-196.467 StartY=26.4942 StartZ=0 EndX=-192.333 EndY=24.9893 EndZ=0
    g33: Circle CenterX=-19 CenterY=21.2 CenterZ=0 NormalX=0 NormalY=0 NormalZ=1 AngleXU=0 Radius=6.3
    g34: Circle CenterX=-42 CenterY=21.2 CenterZ=0 NormalX=0 NormalY=0 NormalZ=1 AngleXU=0 Radius=6.3
    g35: Circle CenterX=-65 CenterY=21.2 CenterZ=0 NormalX=0 NormalY=0 NormalZ=1 AngleXU=0 Radius=6.3
    g36: LineSegment [constr] StartX=-4 StartY=21.2 StartZ=0 EndX=-65 EndY=21.2 EndZ=0
  constraints (96):
    c: Coincident(g0,g-41)
    c: Horizontal(g0)
    c: PointOnObject(g0,g-39)
    c: Coincident(g1,g0)
    c: Vertical(g1)
    c: DistanceY(g1,g1) = 3
    c: Coincident(g2,g-17)
    c: Vertical(g2)
    c: Coincident(g3,g-16)
    c: Vertical(g3)
    c: DistanceY(g2,g2) = 2
    c: DistanceY(g3,g3) = 2
    c: Coincident(g4,g3)
    c: Coincident(g4,g2)
    c: Coincident(g5,g-17)
    c: Coincident(g5,g2)
    c: Coincident(g6,g1)
    c: Horizontal(g6)
    c: Coincident(g6,g5)
    c: Coincident(g7,g-15)
    c: Coincident(g8,g7)
    c: Coincident(g8,g3)
    c: Coincident(g8,g-15)
    c: Horizontal(g9)
    c: DistanceY(g-13,g9) = 2
    c: Coincident(g10,g7)
    c: Parallel(g10,g-14)
    c: Coincident(g9,g10)
    c: Distance(g11) = 2
    c: Coincident(g11,g-11)
    c: Perpendicular(g-11,g11)
    c: Distance(g12) = 2
    c: Coincident(g12,g-12)
    c: Perpendicular(g-11,g12)
    c: Coincident(g13,g11)
    c: Coincident(g13,g12)
    c: Coincident(g14,g-32)
    c: Coincident(g14,g12)
    c: Coincident(g14,g9)
    c: Coincident(g15,g-10)
    c: Coincident(g15,g11)
    c: Parallel(g16,g-22)
    c: Distance(g17) = 4
    c: PointOnObject(g17,g16)
    c: Coincident(g15,g16)
    c: Horizontal(g18)
    c: Coincident(g18,g16)
    c: Coincident(g19,g0)
    c: PointOnObject(g19,g-39)
    c: DistanceY(g19,g-36) = 2
    c: Coincident(g18,g19)
    c: Diameter(g22) = 3.6
    c: Coincident(g22,g-9)
    c: Diameter(g23) = 3.6
    c: Coincident(g23,g-8)
    c: Diameter(g24) = 3.6
    c: Diameter(g25) = 3.6
    c: Diameter(g26) = 3.6
    c: Diameter(g27) = 3.6
    c: Diameter(g28) = 3.6
    c: Coincident(g27,g-4)
    c: Coincident(g28,g-3)
    c: Coincident(g25,g-6)
    c: Coincident(g26,g-5)
    c: Coincident(g24,g-7)
    c: Parallel(g20,g-21)
    c: Equal(g20,g-21)
    c: Parallel(g21,g-19)
    c: Equal(g21,g-19)
    c: Distance(g29) = 0.2
    c: Distance(g30) = 0.2
    c: Parallel(g29,g-20)
    c: Parallel(g31,g-20)
    c: Equal(g31,g-20)
    c: Coincident(g30,g31)
    c: Coincident(g31,g29)
    c: Coincident(g29,g-21)
    c: Parallel(g30,g31)
    c: Coincident(g17,g30)
    c: Coincident(g20,g29)
    c: Coincident(g21,g30)
    c: Perpendicular(g16,g17)
    c: Coincident(g32,g21)
    c: Coincident(g32,g20)
    c: Perpendicular(g10,g7)
    c: Diameter(g33) = 12.6
    c: Diameter(g34) = 12.6
    c: Diameter(g35) = 12.6
    c: Horizontal(g36)
    c: PointOnObject(g33,g36)
    c: PointOnObject(g34,g36)
    c: DistanceX(g34,g33) = 23
    c: DistanceX(g35,g34) = 23
    c: DistanceX(g33,g36) = 15
    c: Symmetric(g-24,g-24,g36)
    c: Coincident(g36,g35)
FEATURE [Sketcher::SketchObject] Sketch075  label="lato dx pistola"
  ArcFitTolerance = 1e-06
  AttachmentSupport = -> [XZ_Plane]
  ExternalGeometry = -> [Sketch016,Sketch,Sketch058,Sketch074]
  FullyConstrained = true
  MakeInternals = false
  MapMode = 5
  Placement = pos=(0,0,0) rot=(1,0,0;1.5708rad)
  sketch-geometry (61):
    g0: LineSegment StartX=-82.8 StartY=3.2 StartZ=0 EndX=0 EndY=3.2 EndZ=0
    g1: LineSegment StartX=-82.8 StartY=3.2 StartZ=0 EndX=-82.8 EndY=6.2 EndZ=0
    g2: LineSegment [constr] StartX=-107.6 StartY=18 StartZ=0 EndX=-107.6 EndY=20 EndZ=0
    g3: LineSegment [constr] StartX=-132.428 StartY=18 StartZ=0 EndX=-132.428 EndY=20 EndZ=0
    g4: LineSegment StartX=-132.428 StartY=20 StartZ=0 EndX=-107.6 EndY=20 EndZ=0
    g5: ArcOfCircle CenterX=-107.6 CenterY=4 CenterZ=0 NormalX=0 NormalY=0 NormalZ=1 AngleXU=0 Radius=16 StartAngle=0.137937 EndAngle=1.5708
    g6: LineSegment StartX=-82.8 StartY=6.2 StartZ=0 EndX=-91.752 EndY=6.2 EndZ=0
    g7: LineSegment [constr] StartX=-145.743 StartY=8.32624 StartZ=0 EndX=-147.645 EndY=8.94427 EndZ=0
    g8: ArcOfCircle CenterX=-132.428 CenterY=4 CenterZ=0 NormalX=0 NormalY=0 NormalZ=1 AngleXU=0 Radius=16 StartAngle=1.5708 EndAngle=2.82743
    g9: LineSegment StartX=-215.932 StartY=-80.4316 StartZ=0 EndX=-176.685 EndY=-80.4316 EndZ=0
    g10: LineSegment StartX=-147.645 StartY=8.94427 StartZ=0 EndX=-176.685 EndY=-80.4316 EndZ=0
    g11: LineSegment [constr] StartX=-193.988 StartY=-2.33927 StartZ=0 EndX=-192.176 EndY=-3.18451 EndZ=0
    g12: LineSegment [constr] StartX=-217.232 StartY=-52.1862 StartZ=0 EndX=-215.42 EndY=-53.0314 EndZ=0
    g13: LineSegment StartX=-192.176 StartY=-3.18451 StartZ=0 EndX=-215.42 EndY=-53.0314 EndZ=0
    g14: ArcOfCircle CenterX=-184.801 CenterY=-67.3089 CenterZ=0 NormalX=0 NormalY=0 NormalZ=1 AngleXU=0 Radius=33.7833 StartAngle=2.70526 EndAngle=3.54053
    g15: ArcOfCircle CenterX=-207.583 CenterY=4 CenterZ=0 NormalX=0 NormalY=0 NormalZ=1 AngleXU=0 Radius=17 StartAngle=5.84685 EndAngle=7.56663
    g16: LineSegment StartX=-202.765 StartY=20.303 StartZ=0 EndX=-195.887 EndY=39.2 EndZ=0
    g17: LineSegment [constr] StartX=-193.885 StartY=33.0037 StartZ=0 EndX=-197.644 EndY=34.3718 EndZ=0
    g18: LineSegment StartX=-195.887 StartY=39.2 StartZ=0 EndX=0 EndY=39.2 EndZ=0
    g19: LineSegment StartX=0 StartY=3.2 StartZ=0 EndX=0 EndY=39.2 EndZ=0
    g20: LineSegment StartX=-189.939 StartY=31.5672 StartZ=0 EndX=-192.333 EndY=24.9893 EndZ=0
    g21: LineSegment StartX=-196.467 StartY=26.4942 StartZ=0 EndX=-194.073 EndY=33.0721 EndZ=0
    g22: Circle CenterX=-213.443 CenterY=-76.8316 CenterZ=0 NormalX=0 NormalY=0 NormalZ=1 AngleXU=0 Radius=1.8
    g23: Circle CenterX=-179.305 CenterY=-76.8316 CenterZ=0 NormalX=0 NormalY=0 NormalZ=1 AngleXU=0 Radius=1.8
    g24: Circle CenterX=-184.08 CenterY=34.8 CenterZ=0 NormalX=0 NormalY=0 NormalZ=1 AngleXU=0 Radius=1.8
    g25: Circle CenterX=-78.51 CenterY=34.8 CenterZ=0 NormalX=0 NormalY=0 NormalZ=1 AngleXU=0 Radius=1.8
    g26: Circle CenterX=-78.51 CenterY=7.6 CenterZ=0 NormalX=0 NormalY=0 NormalZ=1 AngleXU=0 Radius=1.8
    g27: Circle CenterX=-5.6 CenterY=34.8 CenterZ=0 NormalX=0 NormalY=0 NormalZ=1 AngleXU=0 Radius=1.8
    g28: Circle CenterX=-5.6 CenterY=7.6 CenterZ=0 NormalX=0 NormalY=0 NormalZ=1 AngleXU=0 Radius=1.8
    g29: LineSegment StartX=-190.127 StartY=31.6356 StartZ=0 EndX=-189.939 EndY=31.5672 EndZ=0
    g30: LineSegment StartX=-194.073 StartY=33.0721 StartZ=0 EndX=-193.885 EndY=33.0037 EndZ=0
    g31: LineSegment StartX=-193.885 StartY=33.0037 StartZ=0 EndX=-190.127 EndY=31.6356 EndZ=0
    g32: LineSegment StartX=-196.467 StartY=26.4942 StartZ=0 EndX=-192.333 EndY=24.9893 EndZ=0
    g33: LineSegment [constr] StartX=-4 StartY=21.2 StartZ=0 EndX=-87.91 EndY=21.2 EndZ=0
    g34: GeomPoint [constr] X=-4 Y=21.2 Z=0
    g35: LineSegment [constr] StartX=-15.2 StartY=33.7 StartZ=0 EndX=-15.2 EndY=8.7 EndZ=0
    g36: LineSegment [constr] StartX=-15.2 StartY=33.7 StartZ=0 EndX=-56.2 EndY=33.7 EndZ=0
    g37: LineSegment [constr] StartX=-15.2 StartY=8.7 StartZ=0 EndX=-56.2 EndY=8.7 EndZ=0
    g38: LineSegment [constr] StartX=-56.2 StartY=33.7 StartZ=0 EndX=-56.2 EndY=8.7 EndZ=0
    g39: Circle CenterX=-18.6 CenterY=30.3 CenterZ=0 NormalX=0 NormalY=0 NormalZ=1 AngleXU=0 Radius=3.4
    g40: Circle CenterX=-18.6 CenterY=12.1 CenterZ=0 NormalX=0 NormalY=0 NormalZ=1 AngleXU=0 Radius=3.4
    g41: Circle CenterX=-43.2 CenterY=30.3 CenterZ=0 NormalX=0 NormalY=0 NormalZ=1 AngleXU=0 Radius=3.4
    g42: Circle CenterX=-43.2 CenterY=12.1 CenterZ=0 NormalX=0 NormalY=0 NormalZ=1 AngleXU=0 Radius=3.4
    g43: LineSegment [constr] StartX=-4 StartY=21.2 StartZ=0 EndX=-15.2 EndY=21.2 EndZ=0
    g44: LineSegment [constr] StartX=-15.2 StartY=21.2 StartZ=0 EndX=-36.2 EndY=21.2 EndZ=0
    g45: LineSegment [constr] StartX=-41.5 StartY=16.2 StartZ=0 EndX=-30.9 EndY=16.2 EndZ=0
    g46: LineSegment [constr] StartX=-30.9 StartY=16.2 StartZ=0 EndX=-30.9 EndY=26.2 EndZ=0
    g47: LineSegment [constr] StartX=-30.9 StartY=26.2 StartZ=0 EndX=-41.5 EndY=26.2 EndZ=0
    g48: LineSegment [constr] StartX=-41.5 StartY=26.2 StartZ=0 EndX=-41.5 EndY=16.2 EndZ=0
    g49: GeomPoint [constr] X=-36.2 Y=21.2 Z=0
    g50: Circle CenterX=-36.2 CenterY=21.2 CenterZ=0 NormalX=0 NormalY=0 NormalZ=1 AngleXU=0 Radius=2.8
    g51: LineSegment [constr] StartX=-24.2 StartY=26.7 StartZ=0 EndX=-24.2 EndY=15.7 EndZ=0
    g52: Circle CenterX=-24.2 CenterY=26.7 CenterZ=0 NormalX=0 NormalY=0 NormalZ=1 AngleXU=0 Radius=3
    g53: Circle CenterX=-24.2 CenterY=15.7 CenterZ=0 NormalX=0 NormalY=0 NormalZ=1 AngleXU=0 Radius=3
    g54: GeomPoint X=-18.6 Y=30.3 Z=0
    g55: GeomPoint X=-18.6 Y=12.1 Z=0
    g56: GeomPoint X=-43.2 Y=12.1 Z=0
    g57: GeomPoint X=-43.2 Y=30.3 Z=0
    g58: Circle CenterX=-65 CenterY=21.2 CenterZ=0 NormalX=0 NormalY=0 NormalZ=1 AngleXU=0 Radius=1.5
    g59: Circle CenterX=-42 CenterY=21.2 CenterZ=0 NormalX=0 NormalY=0 NormalZ=1 AngleXU=0 Radius=1.5
    g60: Circle CenterX=-19 CenterY=21.2 CenterZ=0 NormalX=0 NormalY=0 NormalZ=1 AngleXU=0 Radius=1.5
  constraints (149):
    c: Coincident(g0,g-41)
    c: Horizontal(g0)
    c: PointOnObject(g0,g-39)
    c: Coincident(g1,g0)
    c: Vertical(g1)
    c: DistanceY(g1,g1) = 3
    c: Coincident(g2,g-17)
    c: Vertical(g2)
    c: Coincident(g3,g-16)
    c: Vertical(g3)
    c: DistanceY(g2,g2) = 2
    c: DistanceY(g3,g3) = 2
    c: Coincident(g4,g3)
    c: Coincident(g4,g2)
    c: Coincident(g5,g-17)
    c: Coincident(g5,g2)
    c: Coincident(g6,g1)
    c: Horizontal(g6)
    c: Coincident(g6,g5)
    c: Coincident(g7,g-15)
    c: Coincident(g8,g7)
    c: Coincident(g8,g3)
    c: Coincident(g8,g-15)
    c: Horizontal(g9)
    c: DistanceY(g-13,g9) = 2
    c: Coincident(g10,g7)
    c: Parallel(g10,g-14)
    c: Coincident(g9,g10)
    c: Distance(g11) = 2
    c: Coincident(g11,g-11)
    c: Perpendicular(g-11,g11)
    c: Distance(g12) = 2
    c: Coincident(g12,g-12)
    c: Perpendicular(g-11,g12)
    c: Coincident(g13,g11)
    c: Coincident(g13,g12)
    c: Coincident(g14,g-32)
    c: Coincident(g14,g12)
    c: Coincident(g14,g9)
    c: Coincident(g15,g-10)
    c: Coincident(g15,g11)
    c: Parallel(g16,g-22)
    c: Distance(g17) = 4
    c: PointOnObject(g17,g16)
    c: Coincident(g15,g16)
    c: Horizontal(g18)
    c: Coincident(g18,g16)
    c: Coincident(g19,g0)
    c: PointOnObject(g19,g-39)
    c: DistanceY(g19,g-36) = 2
    c: Coincident(g18,g19)
    c: Diameter(g22) = 3.6
    c: Coincident(g22,g-9)
    c: Diameter(g23) = 3.6
    c: Coincident(g23,g-8)
    c: Diameter(g24) = 3.6
    c: Diameter(g25) = 3.6
    c: Diameter(g26) = 3.6
    c: Diameter(g27) = 3.6
    c: Diameter(g28) = 3.6
    c: Coincident(g27,g-4)
    c: Coincident(g28,g-3)
    c: Coincident(g25,g-6)
    c: Coincident(g26,g-5)
    c: Coincident(g24,g-7)
    c: Parallel(g20,g-21)
    c: Equal(g20,g-21)
    c: Parallel(g21,g-19)
    c: Equal(g21,g-19)
    c: Distance(g29) = 0.2
    c: Distance(g30) = 0.2
    c: Parallel(g29,g-20)
    c: Parallel(g31,g-20)
    c: Equal(g31,g-20)
    c: Coincident(g30,g31)
    c: Coincident(g31,g29)
    c: Coincident(g29,g-21)
    c: Parallel(g30,g31)
    c: Coincident(g17,g30)
    c: Coincident(g20,g29)
    c: Coincident(g21,g30)
    c: Perpendicular(g16,g17)
    c: Coincident(g32,g21)
    c: Coincident(g32,g20)
    c: Perpendicular(g10,g7)
    c: Horizontal(g33)
    c: Symmetric(g-24,g-24,g33)
    c: PointOnObject(g33,g-28)
    c: Symmetric(g-24,g-24,g34)
    c: DistanceY(g35,g35) = 25
    c: Symmetric(g35,g35,g33)
    c: Distance(g36) = 41
    c: Coincident(g36,g35)
    c: Horizontal(g36)
    c: Coincident(g37,g35)
    c: Horizontal(g37)
    c: Coincident(g38,g36)
    c: Vertical(g38)
    c: Coincident(g37,g38)
    c: Diameter(g39) = 6.8
    c: Diameter(g40) = 6.8
    c: Tangent(g39,g36)
    c: Tangent(g40,g37)
    c: Tangent(g39,g35)
    c: Tangent(g40,g35)
    c: Diameter(g41) = 6.8
    c: Diameter(g42) = 6.8
    c: Tangent(g41,g36)
    c: Tangent(g42,g37)
    c: DistanceX(g41,g39) = 24.6
    c: DistanceX(g42,g40) = 24.6
    c: Distance(g43) = 11.2
    c: Coincident(g43,g33)
    c: PointOnObject(g43,g33)
    c: PointOnObject(g43,g35)
    c: Distance(g44) = 21
    c: Coincident(g44,g43)
    c: PointOnObject(g44,g33)
    c: Coincident(g45,g46)
    c: Coincident(g46,g47)
    c: Coincident(g47,g48)
    c: Coincident(g48,g45)
    c: Horizontal(g45)
    c: Horizontal(g47)
    c: Vertical(g46)
    c: Vertical(g48)
    c: Symmetric(g47,g45,g49)
    c: Distance(g46,g48) = 10.6
    c: Distance(g45,g47) = 10
    c: Coincident(g49,g44)
    c: Diameter(g50) = 5.6
    c: Coincident(g50,g44)
    c: Distance(g51) = 11
    c: Symmetric(g51,g51,g33)
    c: DistanceX(g51,g43) = 9
    c: Diameter(g52) = 6
    c: Coincident(g52,g51)
    c: Diameter(g53) = 6
    c: Coincident(g53,g51)
    c: Coincident(g40,g55)
    c: Coincident(g39,g54)
    c: Coincident(g41,g57)
    c: Coincident(g42,g56)
    c: Diameter(g58) = 3
    c: Diameter(g59) = 3
    c: Diameter(g60) = 3
    c: Coincident(g58,g-44)
    c: Coincident(g59,g-46)
    c: Coincident(g60,g-45)
FEATURE [Sketcher::SketchObject] Sketch078
  ArcFitTolerance = 1e-06
  AttachmentSupport = -> [XZ_Plane005]
  FullyConstrained = true
  MakeInternals = false
  MapMode = 5
  Placement = pos=(0,0,0) rot=(1,0,0;1.5708rad)
  sketch-geometry (5):
    g0: LineSegment [constr] StartX=0 StartY=5.5 StartZ=0 EndX=0 EndY=-5.5 EndZ=0
    g1: ArcOfCircle CenterX=0 CenterY=5.5 CenterZ=0 NormalX=0 NormalY=0 NormalZ=1 AngleXU=0 Radius=2.7 StartAngle=0 EndAngle=3.14159
    g2: ArcOfCircle CenterX=0 CenterY=-5.5 CenterZ=0 NormalX=0 NormalY=0 NormalZ=1 AngleXU=0 Radius=2.7 StartAngle=3.1416 EndAngle=6.28318
    g3: LineSegment StartX=-2.7 StartY=5.5 StartZ=0 EndX=-2.7 EndY=-5.50001 EndZ=0
    g4: LineSegment StartX=2.7 StartY=5.5 StartZ=0 EndX=2.7 EndY=-5.50001 EndZ=0
  constraints (13):
    c: Distance(g0) = 11
    c: Vertical(g0)
    c: Symmetric(g0,g0,g-1)
    c: Radius(g1) = 2.7
    c: Coincident(g1,g0)
    c: Radius(g2) = 2.7
    c: Coincident(g2,g0)
    c: Vertical(g3)
    c: Vertical(g4)
    c: Coincident(g2,g4)
    c: Coincident(g2,g3)
    c: Tangent(g3,g1) = -1.5708
    c: Tangent(g4,g1) = 1.5708
FEATURE [PartDesign::Pad] Pad002
  Direction = (0,-1,2e-16)
  Length = 0.8
  Length2 = 10
  Placement = pos=(0,0,0) rot=(1,0,0;1.5708rad)
  Profile = -> Sketch078
  ReferenceAxis = -> Sketch078 [N_Axis]
  Refine = true
  Suppressed = false
  Type = 0
FEATURE [Sketcher::SketchObject] Sketch079
  ArcFitTolerance = 1e-06
  AttachmentSupport = -> [XZ_Plane005]
  ExternalGeometry = -> [Sketch078]
  FullyConstrained = true
  MakeInternals = false
  MapMode = 5
  Placement = pos=(0,0,0) rot=(1,0,0;1.5708rad)
  sketch-geometry (2):
    g0: Circle CenterX=-1e-16 CenterY=5.5 CenterZ=0 NormalX=0 NormalY=0 NormalZ=1 AngleXU=0 Radius=2.7
    g1: Circle CenterX=0 CenterY=-5.5 CenterZ=0 NormalX=0 NormalY=0 NormalZ=1 AngleXU=0 Radius=2.7
  constraints (4):
    c: Coincident(g0,g-3)
    c: PointOnObject(g-3,g0)
    c: Coincident(g1,g-4)
    c: Equal(g1,g-4)
FEATURE [PartDesign::Pad] Pad003
  BaseFeature = -> Pad002
  Direction = (0,-1,2e-16)
  Length = 5
  Length2 = 10
  Placement = pos=(0,0,0) rot=(1,0,0;1.5708rad)
  Profile = -> Sketch079
  ReferenceAxis = -> Sketch079 [N_Axis]
  Refine = true
  Suppressed = false
  Type = 0
FEATURE [PartDesign::Fillet] Fillet001
  Base = -> Pad003 [Edge16,Edge14]
  BaseFeature = -> Pad003
  Placement = pos=(0,0,0) rot=(1,0,0;1.5708rad)
  Radius = 0.4
  Refine = true
  SupportTransform = false
  Suppressed = false
  UseAllEdges = false
FEATURE [PartDesign::Body] Body005  label="pulsanti lato destro"
  AllowCompound = false
  Group = -> [Sketch078,Pad002,Sketch079,Pad003,Fillet001]
  Origin = -> Origin005
  Tip = -> Fillet001
FEATURE [PartDesign::SubShapeBinder] Binder
  BindCopyOnChange = 0
  BindMode = 0
  ClaimChildren = false
  Context = -> Body006 [Binder.]
  Fuse = false
  MakeFace = true
  OffsetFill = false
  OffsetIntersection = false
  OffsetJoinType = 0
  OffsetOpenResult = false
  PartialLoad = false
  Refine = true
  Relative = true
  Support = -> [Body[Sketch074.]]
  _Version = 2
FEATURE [PartDesign::SubShapeBinder] Binder001
  BindCopyOnChange = 0
  BindMode = 0
  ClaimChildren = false
  Context = -> Body007 [Binder001.]
  Fuse = false
  MakeFace = true
  OffsetFill = false
  OffsetIntersection = false
  OffsetJoinType = 0
  OffsetOpenResult = false
  PartialLoad = false
  Refine = true
  Relative = true
  Support = -> [Body[Sketch075.]]
  _Version = 2
FEATURE [Mesh::Feature] logo_per_PCB_definitivo_positivo
  Placement = pos=(-191,17,-66) rot=(0,1,1;0rad)
FEATURE [Sketcher::SketchObject] Sketch114  label="Sketch114 - base lato DX"
  ArcFitTolerance = 1e-06
  AttachmentSupport = -> [Binder001]
  ExternalGeometry = -> [Binder001]
  FullyConstrained = true
  MakeInternals = false
  MapMode = 5
  Placement = pos=(0,1e-15,0) rot=(0,0.707107,0.707107;3.14159rad)
  sketch-geometry (30):
    g0: Circle CenterX=5.6 CenterY=34.8 CenterZ=0 NormalX=0 NormalY=0 NormalZ=1 AngleXU=0 Radius=1.8
    g1: Circle CenterX=5.6 CenterY=7.6 CenterZ=0 NormalX=0 NormalY=0 NormalZ=1 AngleXU=0 Radius=1.8
    g2: Circle CenterX=24.2 CenterY=26.7 CenterZ=0 NormalX=0 NormalY=0 NormalZ=1 AngleXU=0 Radius=3
    g3: Circle CenterX=24.2 CenterY=15.7 CenterZ=0 NormalX=0 NormalY=0 NormalZ=1 AngleXU=0 Radius=3
    g4: Circle CenterX=36.2 CenterY=21.2 CenterZ=0 NormalX=0 NormalY=0 NormalZ=1 AngleXU=0 Radius=2.8
    g5: Circle CenterX=78.51 CenterY=34.8 CenterZ=0 NormalX=0 NormalY=0 NormalZ=1 AngleXU=0 Radius=1.8
    g6: Circle CenterX=78.51 CenterY=7.6 CenterZ=0 NormalX=0 NormalY=0 NormalZ=1 AngleXU=0 Radius=1.8
    g7: Circle CenterX=184.08 CenterY=34.8 CenterZ=0 NormalX=0 NormalY=0 NormalZ=1 AngleXU=0 Radius=1.8
    g8: Circle CenterX=213.443 CenterY=-76.8316 CenterZ=0 NormalX=0 NormalY=0 NormalZ=1 AngleXU=0 Radius=1.8
    g9: Circle CenterX=179.305 CenterY=-76.8316 CenterZ=0 NormalX=0 NormalY=0 NormalZ=1 AngleXU=0 Radius=1.8
    g10: ArcOfCircle [constr] CenterX=132.428 CenterY=4 CenterZ=0 NormalX=0 NormalY=0 NormalZ=1 AngleXU=0 Radius=16 StartAngle=0.314159 EndAngle=1.5708
    g11: ArcOfCircle CenterX=107.6 CenterY=4 CenterZ=0 NormalX=0 NormalY=0 NormalZ=1 AngleXU=0 Radius=16 StartAngle=1.5708 EndAngle=3.00366
    g12: ArcOfCircle CenterX=207.583 CenterY=4 CenterZ=0 NormalX=0 NormalY=0 NormalZ=1 AngleXU=0 Radius=17 StartAngle=1.85815 EndAngle=3.57792
    g13: ArcOfCircle CenterX=184.801 CenterY=-67.3089 CenterZ=0 NormalX=0 NormalY=0 NormalZ=1 AngleXU=0 Radius=33.7833 StartAngle=5.88425 EndAngle=6.71952
    g14: LineSegment StartX=0 StartY=39.2 StartZ=0 EndX=0 EndY=3.2 EndZ=0
    g15: LineSegment StartX=0 StartY=3.2 StartZ=0 EndX=82.8 EndY=3.2 EndZ=0
    g16: LineSegment StartX=82.8 StartY=3.2 StartZ=0 EndX=82.8 EndY=6.2 EndZ=0
    g17: LineSegment StartX=82.8 StartY=6.2 StartZ=0 EndX=91.752 EndY=6.2 EndZ=0
    g18: LineSegment StartX=107.6 StartY=20 StartZ=0 EndX=132.428 EndY=20 EndZ=0
    g19: LineSegment StartX=147.645 StartY=8.94427 StartZ=0 EndX=176.685 EndY=-80.4316 EndZ=0
    g20: LineSegment StartX=176.685 StartY=-80.4316 StartZ=0 EndX=215.932 EndY=-80.4316 EndZ=0
    g21: LineSegment StartX=215.42 StartY=-53.0314 StartZ=0 EndX=192.176 EndY=-3.18451 EndZ=0
    g22: LineSegment StartX=202.765 StartY=20.303 StartZ=0 EndX=195.887 EndY=39.2 EndZ=0
    g23: LineSegment StartX=195.887 StartY=39.2 StartZ=0 EndX=0 EndY=39.2 EndZ=0
    g24: LineSegment StartX=196.467 StartY=26.4942 StartZ=0 EndX=194.073 EndY=33.0721 EndZ=0
    g25: LineSegment StartX=194.073 StartY=33.0721 StartZ=0 EndX=189.939 EndY=31.5672 EndZ=0
    g26: LineSegment StartX=189.939 StartY=31.5672 StartZ=0 EndX=192.333 EndY=24.9893 EndZ=0
    g27: LineSegment StartX=192.333 StartY=24.9893 StartZ=0 EndX=196.467 EndY=26.4942 EndZ=0
    g28: LineSegment StartX=132.428 StartY=20 StartZ=0 EndX=144.053 EndY=20 EndZ=0
    g29: LineSegment StartX=144.053 StartY=20 StartZ=0 EndX=147.645 EndY=8.94427 EndZ=0
  constraints (65):
    c: Equal(g0,g-25)
    c: Equal(g2,g-29)
    c: Equal(g3,g-30)
    c: Equal(g4,g-28)
    c: Equal(g1,g-26)
    c: Coincident(g0,g-25)
    c: Coincident(g1,g-26)
    c: Coincident(g2,g-29)
    c: Coincident(g3,g-30)
    c: Coincident(g4,g-28)
    c: Equal(g5,g-23)
    c: Equal(g6,g-24)
    c: Coincident(g5,g-23)
    c: Coincident(g6,g-24)
    c: Equal(g7,g-20)
    c: Coincident(g7,g-20)
    c: Equal(g9,g-22)
    c: Coincident(g9,g-22)
    c: Equal(g8,g-21)
    c: Coincident(g8,g-21)
    c: Equal(g13,g-12)
    c: Equal(g12,g-14)
    c: Equal(g10,g-9)
    c: Equal(g11,g-7)
    c: Coincident(g14,g-27)
    c: Coincident(g14,g-27)
    c: Coincident(g15,g14)
    c: Coincident(g15,g-5)
    c: Coincident(g16,g15)
    c: Coincident(g16,g-6)
    c: Coincident(g17,g16)
    c: Coincident(g17,g-7)
    c: Coincident(g11,g17)
    c: Coincident(g11,g-8)
    c: Coincident(g18,g11)
    c: Coincident(g18,g-9)
    c: Coincident(g10,g18)
    c: Coincident(g10,g-10)
    c: Coincident(g19,g10)
    c: Coincident(g19,g-11)
    c: Coincident(g20,g19)
    c: Coincident(g20,g-12)
    c: Coincident(g13,g20)
    c: Coincident(g13,g-13)
    c: Coincident(g21,g13)
    c: Coincident(g21,g-14)
    c: Coincident(g12,g21)
    c: Coincident(g12,g-15)
    c: Coincident(g22,g12)
    c: Coincident(g22,g-15)
    c: Coincident(g23,g22)
    c: Coincident(g23,g14)
    c: Coincident(g24,g-18)
    c: Coincident(g24,g-16)
    c: Coincident(g25,g24)
    c: Coincident(g25,g-19)
    c: Coincident(g26,g25)
    c: Coincident(g26,g-19)
    c: Coincident(g27,g26)
    c: Coincident(g27,g24)
    c: Coincident(g29,g10)
    c: Coincident(g28,g10)
    c: Coincident(g29,g28)
    c: Parallel(g28,g18)
    c: Parallel(g29,g19)
FEATURE [PartDesign::Pad] Pad011
  Direction = (0,1,-2e-16)
  Length = 2
  Length2 = 10
  Profile = -> Sketch114
  ReferenceAxis = -> Sketch114 [N_Axis]
  Refine = true
  Reversed = true
  Suppressed = false
  Type = 0
FEATURE [Sketcher::SketchObject] Sketch115
  ArcFitTolerance = 1e-06
  AttachmentSupport = -> [Pad011]
  ExternalGeometry = -> [Binder001]
  FullyConstrained = true
  MakeInternals = false
  MapMode = 5
  Placement = pos=(0,1.7e-15,0) rot=(0,0.707107,0.707107;3.14159rad)
  sketch-geometry (4):
    g0: ArcOfCircle CenterX=24.2 CenterY=26.7 CenterZ=0 NormalX=0 NormalY=0 NormalZ=1 AngleXU=0 Radius=3 StartAngle=4.48384e-08 EndAngle=3.14159
    g1: ArcOfCircle CenterX=24.2 CenterY=15.7 CenterZ=0 NormalX=0 NormalY=0 NormalZ=1 AngleXU=0 Radius=3 StartAngle=3.14159 EndAngle=6.28318
    g2: LineSegment StartX=21.2 StartY=26.7 StartZ=0 EndX=21.2 EndY=15.7 EndZ=0
    g3: LineSegment StartX=27.2 StartY=26.7 StartZ=0 EndX=27.2 EndY=15.7 EndZ=0
  constraints (12):
    c: Equal(g1,g-4)
    c: Equal(g0,g-3)
    c: Coincident(g0,g-3)
    c: Coincident(g1,g-4)
    c: Vertical(g2)
    c: Vertical(g3)
    c: Tangent(g3,g-3)
    c: Tangent(g2,g-3)
    c: Coincident(g0,g2)
    c: Coincident(g0,g3)
    c: Coincident(g1,g2)
    c: Coincident(g3,g1)
FEATURE [Sketcher::SketchObject] Sketch117  label="Sketch117 - fori per inserto M3 x 3 x 4.5"
  ArcFitTolerance = 1e-06
  AttachmentSupport = -> [Pad011]
  ExternalGeometry = -> [Binder001]
  FullyConstrained = true
  MakeInternals = false
  MapMode = 5
  Placement = pos=(0,1.7e-15,0) rot=(0,0.707107,0.707107;3.14159rad)
  sketch-geometry (4):
    g0: Circle CenterX=43.2 CenterY=30.3 CenterZ=0 NormalX=0 NormalY=0 NormalZ=1 AngleXU=0 Radius=2.25
    g1: Circle CenterX=43.2 CenterY=12.1 CenterZ=0 NormalX=0 NormalY=0 NormalZ=1 AngleXU=0 Radius=2.25
    g2: Circle CenterX=18.6 CenterY=30.3 CenterZ=0 NormalX=0 NormalY=0 NormalZ=1 AngleXU=0 Radius=2.25
    g3: Circle CenterX=18.6 CenterY=12.1 CenterZ=0 NormalX=0 NormalY=0 NormalZ=1 AngleXU=0 Radius=2.25
  constraints (8):
    c: Diameter(g0) = 4.5
    c: Diameter(g1) = 4.5
    c: Diameter(g2) = 4.5
    c: Diameter(g3) = 4.5
    c: Coincident(g2,g-3)
    c: Coincident(g3,g-6)
    c: Coincident(g0,g-4)
    c: Coincident(g1,g-5)
FEATURE [Sketcher::SketchObject] Sketch118
  ArcFitTolerance = 1e-06
  AttachmentSupport = -> [Pad011]
  ExternalGeometry = -> [Binder001]
  FullyConstrained = true
  MakeInternals = false
  MapMode = 5
  Placement = pos=(0,-2,0) rot=(1,0,0;1.5708rad)
  sketch-geometry (12):
    g0: Circle CenterX=-78.51 CenterY=34.8 CenterZ=0 NormalX=0 NormalY=0 NormalZ=1 AngleXU=0 Radius=1.8
    g1: Circle CenterX=-78.51 CenterY=7.6 CenterZ=0 NormalX=0 NormalY=0 NormalZ=1 AngleXU=0 Radius=1.8
    g2: Circle CenterX=-5.6 CenterY=34.8 CenterZ=0 NormalX=0 NormalY=0 NormalZ=1 AngleXU=0 Radius=1.8
    g3: Circle CenterX=-5.6 CenterY=7.6 CenterZ=0 NormalX=0 NormalY=0 NormalZ=1 AngleXU=0 Radius=1.8
    g4: LineSegment StartX=0 StartY=39.2 StartZ=0 EndX=0 EndY=3.2 EndZ=0
    g5: LineSegment StartX=0 StartY=3.2 StartZ=0 EndX=-82.8 EndY=3.2 EndZ=0
    g6: LineSegment StartX=-82.8 StartY=3.2 StartZ=0 EndX=-82.8 EndY=39.2 EndZ=0
    g7: LineSegment StartX=-82.8 StartY=39.2 StartZ=0 EndX=0 EndY=39.2 EndZ=0
    g8: ArcOfCircle CenterX=-65 CenterY=21.2 CenterZ=0 NormalX=0 NormalY=0 NormalZ=1 AngleXU=0 Radius=10 StartAngle=1.5708 EndAngle=4.71239
    g9: ArcOfCircle CenterX=-19 CenterY=21.2 CenterZ=0 NormalX=0 NormalY=0 NormalZ=1 AngleXU=0 Radius=10 StartAngle=4.71239 EndAngle=7.85398
    g10: LineSegment StartX=-65 StartY=31.2 StartZ=0 EndX=-19 EndY=31.2 EndZ=0
    g11: LineSegment StartX=-65 StartY=11.2 StartZ=0 EndX=-19 EndY=11.2 EndZ=0
  constraints (25):
    c: Equal(g2,g-5)
    c: Equal(g3,g-7)
    c: Equal(g1,g-6)
    c: Equal(g0,g-4)
    c: Coincident(g0,g-4)
    c: Coincident(g1,g-6)
    c: Coincident(g3,g-7)
    c: Coincident(g2,g-5)
    c: Coincident(g4,g-8)
    c: Coincident(g4,g-9)
    c: Coincident(g5,g4)
    c: Coincident(g5,g-10)
    c: Coincident(g6,g5)
    c: PointOnObject(g6,g-3)
    c: Vertical(g6)
    c: Coincident(g7,g6)
    c: Coincident(g7,g4)
    c: Tangent(g8,g10) = 1.5708
    c: Tangent(g8,g11) = -1.5708
    c: Tangent(g9,g10) = 1.5708
    c: Tangent(g9,g11) = -1.5708
    c: Equal(g8,g9)
    c: Radius(g8) = 10
    c: Coincident(g8,g-11)
    c: Coincident(g9,g-12)
FEATURE [Sketcher::SketchObject] Sketch120
  ArcFitTolerance = 1e-06
  AttachmentSupport = -> [Pad011]
  ExternalGeometry = -> [Binder001]
  FullyConstrained = true
  MakeInternals = false
  MapMode = 5
  Placement = pos=(0,-2,0) rot=(1,0,0;1.5708rad)
  sketch-geometry (4):
    g0: LineSegment StartX=-137.815 StartY=39.2 StartZ=0 EndX=-142.655 EndY=24.303 EndZ=0
    g1: LineSegment StartX=-137.815 StartY=39.2 StartZ=0 EndX=-110.815 EndY=39.2 EndZ=0
    g2: LineSegment StartX=-142.655 StartY=24.303 StartZ=0 EndX=-110.815 EndY=24.303 EndZ=0
    g3: ArcOfCircle CenterX=-92.2534 CenterY=31.7515 CenterZ=0 NormalX=0 NormalY=0 NormalZ=1 AngleXU=0 Radius=20 StartAngle=2.75997 EndAngle=3.52321
  constraints (12):
    c: PointOnObject(g0,g-3)
    c: Coincident(g1,g0)
    c: PointOnObject(g1,g-3)
    c: Coincident(g2,g0)
    c: Horizontal(g2)
    c: Tangent(g0,g-4)
    c: Vertical(g2,g1)
    c: DistanceX(g1,g1) = 27
    c: DistanceY(g-6,g0) = 4
    c: Radius(g3) = 20
    c: Coincident(g3,g1)
    c: Coincident(g3,g2)
FEATURE [Sketcher::SketchObject] Sketch121
  ArcFitTolerance = 1e-06
  AttachmentSupport = -> [Pad011]
  ExternalGeometry = -> [Binder001]
  FullyConstrained = true
  MakeInternals = false
  MapMode = 5
  Placement = pos=(0,-2,0) rot=(1,0,0;1.5708rad)
  sketch-geometry (15):
    g0: LineSegment StartX=-137.815 StartY=39.2 StartZ=0 EndX=-143.955 EndY=20.303 EndZ=0
    g1: LineSegment StartX=-143.955 StartY=20.303 StartZ=0 EndX=-190.141 EndY=20.303 EndZ=0
    g2: LineSegment StartX=-190.141 StartY=20.303 StartZ=0 EndX=-186.139 EndY=31.3 EndZ=0
    g3: LineSegment StartX=-178.754 StartY=39.2 StartZ=0 EndX=-180.791 EndY=33.6029 EndZ=0
    g4: ArcOfCircle CenterX=-184.08 CenterY=34.8 CenterZ=0 NormalX=0 NormalY=0 NormalZ=1 AngleXU=0 Radius=3.5 StartAngle=4.71239 EndAngle=5.93412
    g5: LineSegment StartX=-184.08 StartY=31.3 StartZ=0 EndX=-186.139 EndY=31.3 EndZ=0
    g6: LineSegment StartX=-137.815 StartY=39.2 StartZ=0 EndX=-156.815 EndY=39.2 EndZ=0
    g7: LineSegment StartX=-168.815 StartY=39.2 StartZ=0 EndX=-178.754 EndY=39.2 EndZ=0
    g8: LineSegment StartX=-157.815 StartY=39.2 StartZ=0 EndX=-167.815 EndY=39.2 EndZ=0
    g9: LineSegment StartX=-168.815 StartY=31.2 StartZ=0 EndX=-156.815 EndY=31.2 EndZ=0
    g10: LineSegment StartX=-167.436 StartY=36.2 StartZ=0 EndX=-157.436 EndY=36.2 EndZ=0
    g11: ArcOfCircle CenterX=-176.411 CenterY=35.2 CenterZ=0 NormalX=0 NormalY=0 NormalZ=1 AngleXU=0 Radius=20 StartAngle=6.08183 EndAngle=6.48454
    g12: ArcOfCircle CenterX=-188.411 CenterY=35.2 CenterZ=0 NormalX=0 NormalY=0 NormalZ=1 AngleXU=0 Radius=20 StartAngle=6.08183 EndAngle=6.48454
    g13: ArcOfCircle CenterX=-177.411 CenterY=35.2 CenterZ=0 NormalX=0 NormalY=0 NormalZ=1 AngleXU=0 Radius=20 StartAngle=0.0500209 EndAngle=0.201358
    g14: ArcOfCircle CenterX=-187.411 CenterY=35.2 CenterZ=0 NormalX=0 NormalY=0 NormalZ=1 AngleXU=0 Radius=20 StartAngle=0.0500209 EndAngle=0.201358
  constraints (46):
    c: PointOnObject(g0,g-3)
    c: Tangent(g0,g-5)
    c: Coincident(g1,g0)
    c: Horizontal(g1)
    c: Coincident(g2,g1)
    c: PointOnObject(g3,g-3)
    c: Parallel(g3,g-6)
    c: Parallel(g2,g-6)
    c: Radius(g4) = 3.5
    c: Coincident(g4,g-7)
    c: Tangent(g3,g4) = 1.5708
    c: Horizontal(g5)
    c: Tangent(g5,g4) = 1.5708
    c: DistanceX(g-8,g5) = 3.8
    c: Coincident(g2,g5)
    c: Coincident(g6,g0)
    c: PointOnObject(g6,g-3)
    c: DistanceX(g6,g6) = 19
    c: PointOnObject(g7,g-3)
    c: DistanceX(g7,g6) = 12
    c: Coincident(g7,g3)
    c: PointOnObject(g8,g-3)
    c: PointOnObject(g8,g-3)
    c: DistanceX(g8,g8) = 10
    c: DistanceX(g8,g6) = 1
    c: Horizontal(g9)
    c: Vertical(g7,g9)
    c: Vertical(g6,g9)
    c: DistanceY(g9,g7) = 8
    c: Horizontal(g10)
    c: Equal(g8,g10)
    c: DistanceY(g10,g8) = 3
    c: Radius(g11) = 20
    c: Coincident(g11,g6)
    c: Coincident(g11,g9)
    c: Radius(g12) = 20
    c: Coincident(g12,g7)
    c: Coincident(g12,g9)
    c: Equal(g13,g11)
    c: Coincident(g13,g8)
    c: Coincident(g13,g10)
    c: Horizontal(g13,g11)
    c: Equal(g14,g12)
    c: Coincident(g14,g8)
    c: Coincident(g14,g10)
    c: Horizontal(g1,g-6)
FEATURE [Sketcher::SketchObject] Sketch122
  ArcFitTolerance = 1e-06
  AttachmentSupport = -> [Pad011]
  ExternalGeometry = -> [Binder001]
  FullyConstrained = true
  MakeInternals = false
  MapMode = 5
  Placement = pos=(0,-2,0) rot=(1,0,0;1.5708rad)
  sketch-geometry (8):
    g0: ArcOfCircle CenterX=-184.801 CenterY=-67.3089 CenterZ=0 NormalX=0 NormalY=0 NormalZ=1 AngleXU=0 Radius=33.7833 StartAngle=2.70526 EndAngle=3.54053
    g1: LineSegment StartX=-176.685 StartY=-80.4316 StartZ=0 EndX=-215.932 EndY=-80.4316 EndZ=0
    g2: LineSegment StartX=-215.42 StartY=-53.0314 StartZ=0 EndX=-192.176 EndY=-3.18454 EndZ=0
    g3: ArcOfCircle CenterX=-207.583 CenterY=4 CenterZ=0 NormalX=0 NormalY=0 NormalZ=1 AngleXU=0 Radius=17 StartAngle=5.84685 EndAngle=7.56663
    g4: Circle CenterX=-213.443 CenterY=-76.8316 CenterZ=0 NormalX=0 NormalY=0 NormalZ=1 AngleXU=0 Radius=3
    g5: Circle CenterX=-179.305 CenterY=-76.8316 CenterZ=0 NormalX=0 NormalY=0 NormalZ=1 AngleXU=0 Radius=3
    g6: LineSegment StartX=-143.955 StartY=20.303 StartZ=0 EndX=-176.685 EndY=-80.4316 EndZ=0
    g7: LineSegment StartX=-202.765 StartY=20.303 StartZ=0 EndX=-143.955 EndY=20.303 EndZ=0
  constraints (18):
    c: Coincident(g0,g-7)
    c: Coincident(g0,g-8)
    c: Coincident(g1,g0)
    c: Tangent(g2,g-5)
    c: Coincident(g3,g-6)
    c: Coincident(g2,g3)
    c: Coincident(g0,g2)
    c: Diameter(g4) = 6
    c: Diameter(g5) = 6
    c: Coincident(g4,g-9)
    c: Coincident(g5,g-10)
    c: Horizontal(g1)
    c: Coincident(g6,g1)
    c: Tangent(g6,g-4)
    c: Coincident(g3,g-6)
    c: Coincident(g7,g3)
    c: Horizontal(g7)
    c: Coincident(g7,g6)
FEATURE [Sketcher::SketchObject] Sketch123
  ArcFitTolerance = 1e-06
  AttachmentSupport = -> [Pad011]
  ExternalGeometry = -> [Binder001]
  FullyConstrained = true
  MakeInternals = false
  MapMode = 5
  Placement = pos=(0,-2,0) rot=(1,0,0;1.5708rad)
  sketch-geometry (4):
    g0: LineSegment StartX=-108 StartY=36.8 StartZ=0 EndX=-90 EndY=36.8 EndZ=0
    g1: LineSegment StartX=-108 StartY=36.8 StartZ=0 EndX=-108 EndY=26.8 EndZ=0
    g2: LineSegment StartX=-108 StartY=26.8 StartZ=0 EndX=-90 EndY=26.8 EndZ=0
    g3: ArcOfCircle CenterX=-94 CenterY=31.8 CenterZ=0 NormalX=0 NormalY=0 NormalZ=1 AngleXU=0 Radius=6.40312 StartAngle=5.38713 EndAngle=7.17924
  constraints (13):
    c: Horizontal(g0)
    c: Coincident(g1,g0)
    c: Vertical(g1)
    c: Coincident(g2,g1)
    c: Horizontal(g2)
    c: DistanceX(g0,g0) = 18
    c: DistanceY(g1,g1) = 10
    c: Equal(g0,g2)
    c: DistanceX(g0,g-3) = 90
    c: DistanceY(g0,g-3) = 2.4
    c: Coincident(g3,g0)
    c: Coincident(g3,g2)
    c: DistanceX(g3,g0) = 4
FEATURE [PartDesign::Chamfer] Chamfer014
  Angle = 45
  Base = -> Pad011 [Edge80,Edge4,Edge7]
  BaseFeature = -> Pad011
  ChamferType = 0
  FlipDirection = false
  Refine = true
  Size = 1.9
  Size2 = 1
  SupportTransform = false
  Suppressed = false
  UseAllEdges = false
FEATURE [PartDesign::Pocket] Pocket006
  BaseFeature = -> Chamfer014
  Direction = (0,-1,2e-16)
  Length = 1.2
  Length2 = 5
  Profile = -> Sketch115
  ReferenceAxis = -> Sketch115 [N_Axis]
  Refine = true
  Suppressed = false
  Type = 0
FEATURE [Sketcher::SketchObject] Sketch116  label="Sketch116 - pieno per inserto M3 x 3 x 4,5"
  ArcFitTolerance = 1e-06
  AttachmentSupport = -> [Pocket006]
  ExternalGeometry = -> [Binder001]
  FullyConstrained = true
  MakeInternals = false
  MapMode = 5
  Placement = pos=(0,1.7e-15,0) rot=(0,0.707107,0.707107;3.14159rad)
  sketch-geometry (4):
    g0: Circle CenterX=43.2 CenterY=30.3 CenterZ=0 NormalX=0 NormalY=0 NormalZ=1 AngleXU=0 Radius=3.4
    g1: Circle CenterX=43.2 CenterY=12.1 CenterZ=0 NormalX=0 NormalY=0 NormalZ=1 AngleXU=0 Radius=3.4
    g2: Circle CenterX=18.6 CenterY=30.3 CenterZ=0 NormalX=0 NormalY=0 NormalZ=1 AngleXU=0 Radius=3.4
    g3: Circle CenterX=18.6 CenterY=12.1 CenterZ=0 NormalX=0 NormalY=0 NormalZ=1 AngleXU=0 Radius=3.4
  constraints (8):
    c: Diameter(g0) = 6.8
    c: Diameter(g1) = 6.8
    c: Diameter(g2) = 6.8
    c: Diameter(g3) = 6.8
    c: Coincident(g2,g-3)
    c: Coincident(g0,g-4)
    c: Coincident(g3,g-6)
    c: Coincident(g1,g-5)
FEATURE [PartDesign::Pad] Pad012
  BaseFeature = -> Pocket006
  Direction = (0,1,-2e-16)
  Length = 2.4
  Length2 = 10
  Profile = -> Sketch116
  ReferenceAxis = -> Sketch116 [N_Axis]
  Refine = true
  Suppressed = false
  Type = 0
FEATURE [PartDesign::Pocket] Pocket007
  BaseFeature = -> Pad012
  Direction = (0,-1,2e-16)
  Length = 0.6
  Length2 = 2.4
  Profile = -> Sketch117
  ReferenceAxis = -> Sketch117 [N_Axis]
  Refine = true
  Suppressed = false
  Type = 4
FEATURE [PartDesign::Pad] Pad013
  BaseFeature = -> Pocket007
  Direction = (0,-1,2e-16)
  Length = 1.6
  Length2 = 10
  Profile = -> Sketch118
  ReferenceAxis = -> Sketch118 [N_Axis]
  Refine = true
  Suppressed = false
  Type = 0
FEATURE [Sketcher::SketchObject] Sketch119
  ArcFitTolerance = 1e-06
  AttachmentSupport = -> [Pad013]
  ExternalGeometry = -> [Binder001]
  FullyConstrained = true
  MakeInternals = false
  MapMode = 5
  Placement = pos=(0,-3.6,0) rot=(1,0,0;1.5708rad)
  sketch-geometry (21):
    g0: LineSegment [constr] StartX=-82.8 StartY=3.2 StartZ=0 EndX=-82.8 EndY=39.2 EndZ=0
    g1: ArcOfCircle CenterX=-78.51 CenterY=34.8 CenterZ=0 NormalX=0 NormalY=0 NormalZ=1 AngleXU=0 Radius=3.5 StartAngle=4.71239 EndAngle=6.28319
    g2: ArcOfCircle CenterX=-78.51 CenterY=7.6 CenterZ=0 NormalX=0 NormalY=0 NormalZ=1 AngleXU=0 Radius=3.5 StartAngle=0 EndAngle=1.5708
    g3: ArcOfCircle CenterX=-5.6 CenterY=34.8 CenterZ=0 NormalX=0 NormalY=0 NormalZ=1 AngleXU=0 Radius=3.5 StartAngle=3.14159 EndAngle=4.71239
    g4: ArcOfCircle CenterX=-5.6 CenterY=7.6 CenterZ=0 NormalX=0 NormalY=0 NormalZ=1 AngleXU=0 Radius=3.5 StartAngle=1.5708 EndAngle=3.14159
    g5: LineSegment StartX=0 StartY=39.2 StartZ=0 EndX=0 EndY=31.3 EndZ=0
    g6: LineSegment StartX=0 StartY=39.2 StartZ=0 EndX=-9.1 EndY=39.2 EndZ=0
    g7: LineSegment StartX=0 StartY=3.2 StartZ=0 EndX=0 EndY=11.1 EndZ=0
    g8: LineSegment StartX=0 StartY=3.2 StartZ=0 EndX=-9.1 EndY=3.2 EndZ=0
    g9: LineSegment StartX=-82.8 StartY=3.2 StartZ=0 EndX=-75.01 EndY=3.2 EndZ=0
    g10: LineSegment StartX=-82.8 StartY=3.2 StartZ=0 EndX=-82.8 EndY=11.1 EndZ=0
    g11: LineSegment StartX=-82.8 StartY=39.2 StartZ=0 EndX=-82.8 EndY=31.3 EndZ=0
    g12: LineSegment StartX=-82.8 StartY=39.2 StartZ=0 EndX=-75.01 EndY=39.2 EndZ=0
    g13: LineSegment StartX=-82.8 StartY=31.3 StartZ=0 EndX=-78.51 EndY=31.3 EndZ=0
    g14: LineSegment StartX=-75.01 StartY=39.2 StartZ=0 EndX=-75.01 EndY=34.8 EndZ=0
    g15: LineSegment StartX=-82.8 StartY=11.1 StartZ=0 EndX=-78.51 EndY=11.1 EndZ=0
    g16: LineSegment StartX=-75.01 StartY=3.2 StartZ=0 EndX=-75.01 EndY=7.6 EndZ=0
    g17: LineSegment StartX=-9.1 StartY=39.2 StartZ=0 EndX=-9.1 EndY=34.8 EndZ=0
    g18: LineSegment StartX=0 StartY=31.3 StartZ=0 EndX=-5.6 EndY=31.3 EndZ=0
    g19: LineSegment StartX=0 StartY=11.1 StartZ=0 EndX=-5.6 EndY=11.1 EndZ=0
    g20: LineSegment StartX=-9.1 StartY=3.2 StartZ=0 EndX=-9.1 EndY=7.6 EndZ=0
  constraints (51):
    c: Coincident(g0,g-10)
    c: PointOnObject(g0,g-8)
    c: Vertical(g0)
    c: Coincident(g1,g-3)
    c: Coincident(g2,g-4)
    c: Coincident(g3,g-5)
    c: Coincident(g4,g-6)
    c: Radius(g4) = 3.5
    c: Radius(g3) = 3.5
    c: Radius(g1) = 3.5
    c: Radius(g2) = 3.5
    c: Coincident(g5,g-9)
    c: PointOnObject(g5,g-9)
    c: Coincident(g6,g5)
    c: PointOnObject(g6,g-8)
    c: Coincident(g7,g-9)
    c: PointOnObject(g7,g-9)
    c: Coincident(g8,g7)
    c: PointOnObject(g8,g-7)
    c: Coincident(g9,g0)
    c: PointOnObject(g9,g-7)
    c: Coincident(g10,g0)
    c: PointOnObject(g10,g0)
    c: Coincident(g11,g0)
    c: PointOnObject(g11,g0)
    c: Coincident(g12,g0)
    c: PointOnObject(g12,g-8)
    c: Coincident(g13,g11)
    c: Horizontal(g13)
    c: Coincident(g14,g12)
    c: Vertical(g14)
    c: Coincident(g15,g10)
    c: Horizontal(g15)
    c: Coincident(g16,g9)
    c: Vertical(g16)
    c: Coincident(g17,g6)
    c: Vertical(g17)
    c: Coincident(g18,g5)
    c: Horizontal(g18)
    c: Coincident(g19,g7)
    c: Horizontal(g19)
    c: Coincident(g20,g8)
    c: Vertical(g20)
    c: Tangent(g20,g4) = 1.5708
    c: Tangent(g4,g19) = -1.5708
    c: Tangent(g18,g3) = 1.5708
    c: Tangent(g3,g17) = -1.5708
    c: Tangent(g13,g1) = -1.5708
    c: Tangent(g1,g14) = 1.5708
    c: Tangent(g16,g2) = -1.5708
    c: Tangent(g2,g15) = 1.5708
FEATURE [PartDesign::Pocket] Pocket008
  BaseFeature = -> Pad013
  Direction = (0,1,-2e-16)
  Length = 1.6
  Length2 = 5
  Profile = -> Sketch119
  ReferenceAxis = -> Sketch119 [N_Axis]
  Refine = true
  Suppressed = false
  Type = 0
FEATURE [PartDesign::Pad] Pad017
  BaseFeature = -> Pocket008
  Direction = (0,-1,2e-16)
  Length = 1.6
  Length2 = 10
  Profile = -> Sketch123
  ReferenceAxis = -> Sketch123 [N_Axis]
  Refine = true
  Suppressed = false
  Type = 0
FEATURE [Sketcher::SketchObject] Sketch125
  ArcFitTolerance = 1e-06
  AttachmentSupport = -> [Pad017]
  ExternalGeometry = -> [Pad017]
  FullyConstrained = true
  MakeInternals = false
  MapMode = 5
  Placement = pos=(0,-3.6,8e-16) rot=(1,0,0;1.5708rad)
  sketch-geometry (20):
    g0: LineSegment StartX=-108 StartY=35.8 StartZ=0 EndX=-108 EndY=35 EndZ=0
    g1: LineSegment StartX=-108 StartY=35 StartZ=0 EndX=-97 EndY=35 EndZ=0
    g2: LineSegment StartX=-97 StartY=35 StartZ=0 EndX=-97 EndY=35.8 EndZ=0
    g3: LineSegment StartX=-97 StartY=35.8 StartZ=0 EndX=-108 EndY=35.8 EndZ=0
    g4: LineSegment StartX=-108 StartY=28.6 StartZ=0 EndX=-108 EndY=27.8 EndZ=0
    g5: LineSegment StartX=-108 StartY=27.8 StartZ=0 EndX=-97 EndY=27.8 EndZ=0
    g6: LineSegment StartX=-97 StartY=27.8 StartZ=0 EndX=-97 EndY=28.6 EndZ=0
    g7: LineSegment StartX=-97 StartY=28.6 StartZ=0 EndX=-108 EndY=28.6 EndZ=0
    g8: LineSegment StartX=-108 StartY=30.4 StartZ=0 EndX=-108 EndY=29.6 EndZ=0
    g9: LineSegment StartX=-108 StartY=29.6 StartZ=0 EndX=-97 EndY=29.6 EndZ=0
    g10: LineSegment StartX=-97 StartY=29.6 StartZ=0 EndX=-97 EndY=30.4 EndZ=0
    g11: LineSegment StartX=-97 StartY=30.4 StartZ=0 EndX=-108 EndY=30.4 EndZ=0
    g12: LineSegment StartX=-108 StartY=32.2 StartZ=0 EndX=-108 EndY=31.4 EndZ=0
    g13: LineSegment StartX=-108 StartY=31.4 StartZ=0 EndX=-97 EndY=31.4 EndZ=0
    g14: LineSegment StartX=-97 StartY=31.4 StartZ=0 EndX=-97 EndY=32.2 EndZ=0
    g15: LineSegment StartX=-97 StartY=32.2 StartZ=0 EndX=-108 EndY=32.2 EndZ=0
    g16: LineSegment StartX=-108 StartY=34 StartZ=0 EndX=-108 EndY=33.2 EndZ=0
    g17: LineSegment StartX=-108 StartY=33.2 StartZ=0 EndX=-97 EndY=33.2 EndZ=0
    g18: LineSegment StartX=-97 StartY=33.2 StartZ=0 EndX=-97 EndY=34 EndZ=0
    g19: LineSegment StartX=-97 StartY=34 StartZ=0 EndX=-108 EndY=34 EndZ=0
  constraints (55):
    c: Coincident(g1,g0)
    c: Horizontal(g1)
    c: Coincident(g2,g1)
    c: Vertical(g2)
    c: Coincident(g3,g2)
    c: Horizontal(g3)
    c: Coincident(g3,g0)
    c: DistanceX(g1,g1) = 11
    c: DistanceY(g2,g2) = 0.8
    c: Coincident(g5,g4)
    c: Horizontal(g5)
    c: Coincident(g6,g5)
    c: Vertical(g6)
    c: Coincident(g7,g6)
    c: Horizontal(g7)
    c: Coincident(g7,g4)
    c: Coincident(g9,g8)
    c: Horizontal(g9)
    c: Coincident(g10,g9)
    c: Vertical(g10)
    c: Coincident(g11,g10)
    c: Horizontal(g11)
    c: Coincident(g11,g8)
    c: Coincident(g13,g12)
    c: Horizontal(g13)
    c: Coincident(g14,g13)
    c: Vertical(g14)
    c: Coincident(g15,g14)
    c: Horizontal(g15)
    c: Coincident(g15,g12)
    c: Coincident(g17,g16)
    c: Horizontal(g17)
    c: Coincident(g18,g17)
    c: Vertical(g18)
    c: Coincident(g19,g18)
    c: Horizontal(g19)
    c: Coincident(g19,g16)
    c: Equal(g3,g19)
    c: Equal(g3,g15)
    c: Equal(g3,g11)
    c: Equal(g3,g7)
    c: Equal(g2,g18)
    c: Equal(g2,g14)
    c: Equal(g2,g10)
    c: Equal(g2,g6)
    c: DistanceY(g-4,g4) = 1
    c: DistanceY(g4,g8) = 1
    c: DistanceY(g8,g12) = 1
    c: DistanceY(g12,g16) = 1
    c: DistanceY(g16,g0) = 1
    c: Tangent(g0,g-5)
    c: Tangent(g16,g-5)
    c: Tangent(g12,g-5)
    c: Tangent(g8,g-5)
    c: Tangent(g4,g-5)
FEATURE [PartDesign::Chamfer] Chamfer009
  Angle = 45
  Base = -> Pad017 [Edge151,Edge154]
  BaseFeature = -> Pad017
  ChamferType = 1
  FlipDirection = false
  Refine = true
  Size = 1.5
  Size2 = 2.8
  SupportTransform = false
  Suppressed = false
  UseAllEdges = false
FEATURE [PartDesign::Pocket] Pocket009
  BaseFeature = -> Chamfer009
  Direction = (0,1,-2e-16)
  Length = 1
  Length2 = 5
  Profile = -> Sketch125
  ReferenceAxis = -> Sketch125 [N_Axis]
  Refine = true
  Suppressed = false
  Type = 0
FEATURE [PartDesign::Pad] Pad014
  BaseFeature = -> Pocket009
  Direction = (0,-1,2e-16)
  Length = 0.8
  Length2 = 10
  Profile = -> Sketch120
  ReferenceAxis = -> Sketch120 [N_Axis]
  Refine = true
  Suppressed = false
  Type = 0
FEATURE [Sketcher::SketchObject] Sketch124
  ArcFitTolerance = 1e-06
  AttachmentSupport = -> [Pad014]
  ExternalGeometry = -> [Binder001]
  FullyConstrained = true
  MakeInternals = false
  MapMode = 5
  Placement = pos=(0,-2.8,6e-16) rot=(1,0,0;1.5708rad)
  sketch-geometry (4):
    g0: LineSegment StartX=-129 StartY=39.2 StartZ=0 EndX=-131.599 EndY=31.2 EndZ=0
    g1: LineSegment StartX=-118 StartY=39.2 StartZ=0 EndX=-120.599 EndY=31.2 EndZ=0
    g2: LineSegment StartX=-129 StartY=39.2 StartZ=0 EndX=-118 EndY=39.2 EndZ=0
    g3: LineSegment StartX=-120.599 StartY=31.2 StartZ=0 EndX=-131.599 EndY=31.2 EndZ=0
  constraints (12):
    c: PointOnObject(g0,g-3)
    c: PointOnObject(g1,g-3)
    c: Parallel(g-4,g0)
    c: Parallel(g-4,g1)
    c: Coincident(g2,g0)
    c: Coincident(g2,g1)
    c: DistanceX(g2,g2) = 11
    c: DistanceY(g1,g1) = 8
    c: Coincident(g3,g1)
    c: Horizontal(g3)
    c: Coincident(g3,g0)
    c: DistanceX(g1,g-3) = 118
FEATURE [PartDesign::Pad] Pad018
  BaseFeature = -> Pad014
  Direction = (0,-1,2e-16)
  Length = 1.2
  Length2 = 10
  Profile = -> Sketch124
  ReferenceAxis = -> Sketch124 [N_Axis]
  Refine = true
  Suppressed = false
  Type = 0
FEATURE [Sketcher::SketchObject] Sketch126
  ArcFitTolerance = 1e-06
  AttachmentSupport = -> [Pad018]
  ExternalGeometry = -> [Pad018]
  FullyConstrained = true
  MakeInternals = false
  MapMode = 5
  Placement = pos=(0,-4,0) rot=(1,0,0;1.5708rad)
  sketch-geometry (8):
    g0: LineSegment StartX=-129.877 StartY=36.5 StartZ=0 EndX=-130.137 EndY=35.7 EndZ=0
    g1: LineSegment StartX=-130.69 StartY=34 StartZ=0 EndX=-130.95 EndY=33.2 EndZ=0
    g2: LineSegment StartX=-129.877 StartY=36.5 StartZ=0 EndX=-118.877 EndY=36.5 EndZ=0
    g3: LineSegment StartX=-130.137 StartY=35.7 StartZ=0 EndX=-119.137 EndY=35.7 EndZ=0
    g4: LineSegment StartX=-130.69 StartY=34 StartZ=0 EndX=-119.69 EndY=34 EndZ=0
    g5: LineSegment StartX=-130.95 StartY=33.2 StartZ=0 EndX=-119.95 EndY=33.2 EndZ=0
    g6: LineSegment StartX=-118.877 StartY=36.5 StartZ=0 EndX=-119.137 EndY=35.7 EndZ=0
    g7: LineSegment StartX=-119.69 StartY=34 StartZ=0 EndX=-119.95 EndY=33.2 EndZ=0
  constraints (20):
    c: Coincident(g2,g0)
    c: Horizontal(g2)
    c: Coincident(g3,g0)
    c: Horizontal(g3)
    c: Coincident(g4,g1)
    c: Horizontal(g4)
    c: Coincident(g5,g1)
    c: Horizontal(g5)
    c: Coincident(g6,g2)
    c: Coincident(g6,g3)
    c: Coincident(g7,g4)
    c: Coincident(g7,g5)
    c: Tangent(g0,g-4)
    c: Tangent(g6,g-5)
    c: Tangent(g1,g-4)
    c: Tangent(g7,g-5)
    c: DistanceY(g3,g2) = 0.8
    c: DistanceY(g5,g4) = 0.8
    c: DistanceY(g-6,g1) = 2
    c: DistanceY(g-6,g0) = 4.5
FEATURE [PartDesign::Chamfer] Chamfer008
  Angle = 45
  Base = -> Pad018 [Edge257]
  BaseFeature = -> Pad018
  ChamferType = 1
  FlipDirection = false
  Refine = true
  Size = 1
  Size2 = 6
  SupportTransform = false
  Suppressed = false
  UseAllEdges = false
FEATURE [PartDesign::Pocket] Pocket010
  BaseFeature = -> Chamfer008
  Direction = (0,1,-2e-16)
  Length = 1
  Length2 = 5
  Profile = -> Sketch126
  ReferenceAxis = -> Sketch126 [N_Axis]
  Refine = true
  Suppressed = false
  Type = 0
FEATURE [PartDesign::Pad] Pad015
  BaseFeature = -> Pocket010
  Direction = (0,-1,2e-16)
  Length = 2
  Length2 = 10
  Profile = -> Sketch121
  ReferenceAxis = -> Sketch121 [N_Axis]
  Refine = true
  Suppressed = false
  Type = 0
FEATURE [PartDesign::Pad] Pad016
  BaseFeature = -> Pad015
  Direction = (0,-1,2e-16)
  Length = 1.6
  Length2 = 10
  Profile = -> Sketch122
  ReferenceAxis = -> Sketch122 [N_Axis]
  Refine = true
  Suppressed = false
  Type = 0
FEATURE [Sketcher::SketchObject] Sketch129
  ArcFitTolerance = 1e-06
  AttachmentSupport = -> [Pad016]
  ExternalGeometry = -> [Binder001]
  FullyConstrained = true
  MakeInternals = false
  MapMode = 5
  Placement = pos=(0,-3.6,0) rot=(1,0,0;1.5708rad)
  sketch-geometry (12):
    g0: LineSegment [constr] StartX=-192.176 StartY=-3.18451 StartZ=0 EndX=-181.223 EndY=20.303 EndZ=0
    g1: LineSegment [constr] StartX=-202.765 StartY=20.303 StartZ=0 EndX=-181.223 EndY=20.303 EndZ=0
    g2: LineSegment StartX=-202.765 StartY=20.303 StartZ=0 EndX=-181.223 EndY=20.303 EndZ=0
    g3: LineSegment StartX=-192.176 StartY=-3.18451 StartZ=0 EndX=-196.804 EndY=-13.1107 EndZ=0
    g4: ArcOfCircle CenterX=-207.583 CenterY=4 CenterZ=0 NormalX=0 NormalY=0 NormalZ=1 AngleXU=0 Radius=17 StartAngle=5.84685 EndAngle=7.56663
    g5: ArcOfEllipse CenterX=-181.223 CenterY=8.55923 CenterZ=0 NormalX=0 NormalY=0 NormalZ=1 MajorRadius=23.4779 MinorRadius=11.7437 AngleXU=2e-16 StartAngle=4.71239 EndAngle=7.85398
    g6: LineSegment [constr] StartX=-157.745 StartY=8.55923 StartZ=0 EndX=-204.701 EndY=8.55923 EndZ=0
    g7: LineSegment [constr] StartX=-181.223 StartY=20.303 StartZ=0 EndX=-181.223 EndY=-3.18451 EndZ=0
    g8: GeomPoint [constr] X=-160.894 Y=8.55923 Z=0
    g9: GeomPoint [constr] X=-201.553 Y=8.55923 Z=0
    g10: ArcOfCircle CenterX=-181.223 CenterY=-20.3763 CenterZ=0 NormalX=0 NormalY=0 NormalZ=1 AngleXU=0 Radius=17.1918 StartAngle=1.57079 EndAngle=2.70526
    g11: GeomPoint [constr] X=-181.223 Y=-3.18451 Z=0
  constraints (23):
    c: Coincident(g0,g-5)
    c: Coincident(g1,g-6)
    c: Horizontal(g1)
    c: Coincident(g1,g0)
    c: Parallel(g0,g-4)
    c: Coincident(g2,g1)
    c: Coincident(g2,g0)
    c: Coincident(g3,g0)
    c: Equal(g4,g-5)
    c: Coincident(g4,g1)
    c: Coincident(g4,g0)
    c: InternalAlignment(g6-g9 -> g5) x4
    c: Vertical(g5,g0)
    c: Horizontal(g6)
    c: Coincident(g5,g0)
    c: DistanceX(g6,g-3) = 10.1
    c: Tangent(g10,g3) = -1.5708
    c: PointOnObject(g11,g10)
    c: Tangent(g5,g10,g11) = 1.5708
    c: Coincident(g10,g5)
    c: Coincident(g11,g7)
    c: Parallel(g3,g-4)
    c: Horizontal(g5,g0)
FEATURE [Sketcher::SketchObject] Sketch130
  ArcFitTolerance = 1e-06
  AttachmentOffset = pos=(0,0,-1.6) rot=(0,0,1;0rad)
  AttachmentSupport = -> [Pad016]
  ExternalGeometry = -> [Binder001]
  FullyConstrained = true
  MakeInternals = false
  MapMode = 5
  Placement = pos=(0,-2,-4e-16) rot=(1,0,0;1.5708rad)
  sketch-geometry (12):
    g0: LineSegment [constr] StartX=-192.176 StartY=-3.18451 StartZ=0 EndX=-181.223 EndY=20.303 EndZ=0
    g1: LineSegment [constr] StartX=-202.765 StartY=20.303 StartZ=0 EndX=-181.223 EndY=20.303 EndZ=0
    g2: LineSegment StartX=-202.765 StartY=20.303 StartZ=0 EndX=-181.223 EndY=20.303 EndZ=0
    g3: LineSegment StartX=-192.176 StartY=-3.18451 StartZ=0 EndX=-193.827 EndY=-6.72678 EndZ=0
    g4: ArcOfCircle CenterX=-207.583 CenterY=4 CenterZ=0 NormalX=0 NormalY=0 NormalZ=1 AngleXU=0 Radius=17 StartAngle=5.84685 EndAngle=7.56663
    g5: ArcOfEllipse CenterX=-181.223 CenterY=10.803 CenterZ=0 NormalX=0 NormalY=0 NormalZ=1 MajorRadius=14.4779 MinorRadius=9.5 AngleXU=0 StartAngle=4.71239 EndAngle=7.85398
    g6: LineSegment [constr] StartX=-166.745 StartY=10.803 StartZ=0 EndX=-195.701 EndY=10.803 EndZ=0
    g7: LineSegment [constr] StartX=-181.223 StartY=20.303 StartZ=0 EndX=-181.223 EndY=1.30297 EndZ=0
    g8: GeomPoint [constr] X=-170.298 Y=10.803 Z=0
    g9: GeomPoint [constr] X=-192.148 Y=10.803 Z=0
    g10: ArcOfCircle CenterX=-181.223 CenterY=-12.6042 CenterZ=0 NormalX=0 NormalY=0 NormalZ=1 AngleXU=0 Radius=13.9072 StartAngle=1.5708 EndAngle=2.70526
    g11: GeomPoint [constr] X=-181.223 Y=1.30297 Z=0
  constraints (23):
    c: Coincident(g0,g-5)
    c: Coincident(g1,g-6)
    c: Horizontal(g1)
    c: Coincident(g1,g0)
    c: Parallel(g0,g-4)
    c: Coincident(g2,g1)
    c: Coincident(g2,g0)
    c: Coincident(g3,g0)
    c: Equal(g4,g-5)
    c: Coincident(g4,g1)
    c: Coincident(g4,g0)
    c: InternalAlignment(g6-g9 -> g5) x4
    c: Vertical(g5,g0)
    c: Horizontal(g6)
    c: Coincident(g5,g0)
    c: DistanceX(g6,g-3) = 19.1
    c: Tangent(g10,g3) = -1.5708
    c: PointOnObject(g11,g10)
    c: Tangent(g5,g10,g11) = 1.5708
    c: Coincident(g10,g5)
    c: Coincident(g11,g7)
    c: Parallel(g3,g-4)
    c: DistanceY(g5,g0) = 19
FEATURE [Part::Part2DObjectPython] Clone2D001  label="Sketch130 (2D)"  # Draft 2D object (typed FeaturePython)
  Fuse = false
  Objects = -> [Sketch130]
  Placement = pos=(0,-2,-4e-16) rot=(1,0,0;1.5708rad)
  Scale = (1,1,1)
FEATURE [Sketcher::SketchObject] Sketch131
  ArcFitTolerance = 1e-06
  AttachmentOffset = pos=(0,0,-3.5) rot=(0,0,1;0rad)
  AttachmentSupport = -> [Pad016]
  ExternalGeometry = -> [Binder001]
  FullyConstrained = true
  MakeInternals = false
  MapMode = 5
  Placement = pos=(0,-0.1,-8e-16) rot=(1,0,0;1.5708rad)
  sketch-geometry (1):
    g0: GeomPoint X=-197.47 Y=8.55923 Z=0
  constraints (1):
    c: Symmetric(g-6,g-4,g0)
FEATURE [Sketcher::SketchObject] Sketch132
  ArcFitTolerance = 1e-06
  AttachmentSupport = -> [Pad016]
  ExternalGeometry = -> [Binder001]
  FullyConstrained = true
  MakeInternals = false
  MapMode = 5
  Placement = pos=(0,-3.6,0) rot=(1,0,0;1.5708rad)
  sketch-geometry (3):
    g0: LineSegment [constr] StartX=-215.42 StartY=-53.0314 StartZ=0 EndX=-167.782 EndY=-53.0314 EndZ=0
    g1: Circle CenterX=-191.282 CenterY=-53.0314 CenterZ=0 NormalX=0 NormalY=0 NormalZ=1 AngleXU=0 Radius=11.5
    g2: Circle CenterX=-191.282 CenterY=-53.0314 CenterZ=0 NormalX=0 NormalY=0 NormalZ=1 AngleXU=0 Radius=10.7
  constraints (8):
    c: Coincident(g0,g-3)
    c: PointOnObject(g0,g-4)
    c: Horizontal(g0)
    c: Diameter(g1) = 23
    c: PointOnObject(g1,g0)
    c: DistanceX(g1,g0) = 23.5
    c: Diameter(g2) = 21.4
    c: Coincident(g2,g1)
FEATURE [Part::Part2DObjectPython] ShapeString  # Draft 2D object (typed FeaturePython)
  FontFile = <path>
  Fuse = false
  Justification = 6
  JustificationReference = 0
  KeepLeftMargin = false
  MakeFace = true
  ObliqueAngle = 0
  Placement = pos=(-199,-3.6,-57.5) rot=(1,0,0;1.5708rad)
  ScaleToSize = true
  Size = 10
  String = AS
  Tracking = 0
FEATURE [Sketcher::SketchObject] Sketch133
  ArcFitTolerance = 1e-06
  AttachmentSupport = -> [Binder]
  ExternalGeometry = -> [Binder]
  FullyConstrained = true
  MakeInternals = false
  MapMode = 5
  Placement = pos=(0,9e-16,0) rot=(0,0.707107,0.707107;3.14159rad)
  sketch-geometry (30):
    g0: LineSegment StartX=0 StartY=39.2 StartZ=0 EndX=0 EndY=3.2 EndZ=0
    g1: LineSegment StartX=0 StartY=3.2 StartZ=0 EndX=82.8 EndY=3.2 EndZ=0
    g2: LineSegment StartX=82.8 StartY=3.2 StartZ=0 EndX=82.8 EndY=6.2 EndZ=0
    g3: LineSegment StartX=82.8 StartY=6.2 StartZ=0 EndX=91.752 EndY=6.2 EndZ=0
    g4: LineSegment StartX=0 StartY=39.2 StartZ=0 EndX=195.887 EndY=39.2 EndZ=0
    g5: LineSegment StartX=195.887 StartY=39.2 StartZ=0 EndX=202.765 EndY=20.303 EndZ=0
    g6: LineSegment StartX=192.333 StartY=24.9893 StartZ=0 EndX=196.467 EndY=26.4942 EndZ=0
    g7: LineSegment StartX=196.467 StartY=26.4942 StartZ=0 EndX=194.073 EndY=33.0721 EndZ=0
    g8: LineSegment StartX=194.073 StartY=33.0721 StartZ=0 EndX=189.939 EndY=31.5672 EndZ=0
    g9: LineSegment StartX=189.939 StartY=31.5672 StartZ=0 EndX=192.333 EndY=24.9893 EndZ=0
    g10: ArcOfCircle CenterX=107.6 CenterY=4 CenterZ=0 NormalX=0 NormalY=0 NormalZ=1 AngleXU=0 Radius=16 StartAngle=1.5708 EndAngle=3.00366
    g11: LineSegment StartX=107.6 StartY=20 StartZ=0 EndX=132.428 EndY=20 EndZ=0
    g12: ArcOfCircle [constr] CenterX=132.428 CenterY=4 CenterZ=0 NormalX=0 NormalY=0 NormalZ=1 AngleXU=0 Radius=16 StartAngle=0.314159 EndAngle=1.5708
    g13: LineSegment StartX=147.645 StartY=8.94427 StartZ=0 EndX=176.685 EndY=-80.4316 EndZ=0
    g14: LineSegment StartX=176.685 StartY=-80.4316 StartZ=0 EndX=215.932 EndY=-80.4316 EndZ=0
    g15: ArcOfCircle CenterX=207.583 CenterY=4 CenterZ=0 NormalX=0 NormalY=0 NormalZ=1 AngleXU=0 Radius=17 StartAngle=1.85815 EndAngle=3.57792
    g16: ArcOfCircle CenterX=184.801 CenterY=-67.3089 CenterZ=0 NormalX=0 NormalY=0 NormalZ=1 AngleXU=0 Radius=33.7833 StartAngle=5.88425 EndAngle=6.71952
    g17: LineSegment StartX=192.176 StartY=-3.18451 StartZ=0 EndX=215.42 EndY=-53.0314 EndZ=0
    g18: Circle CenterX=5.6 CenterY=34.8 CenterZ=0 NormalX=0 NormalY=0 NormalZ=1 AngleXU=0 Radius=1.8
    g19: Circle CenterX=5.6 CenterY=7.6 CenterZ=0 NormalX=0 NormalY=0 NormalZ=1 AngleXU=0 Radius=1.8
    g20: Circle CenterX=78.51 CenterY=34.8 CenterZ=0 NormalX=0 NormalY=0 NormalZ=1 AngleXU=0 Radius=1.8
    g21: Circle CenterX=78.51 CenterY=7.6 CenterZ=0 NormalX=0 NormalY=0 NormalZ=1 AngleXU=0 Radius=1.8
    g22: Circle CenterX=184.08 CenterY=34.8 CenterZ=0 NormalX=0 NormalY=0 NormalZ=1 AngleXU=0 Radius=1.8
    g23: Circle CenterX=179.305 CenterY=-76.8316 CenterZ=0 NormalX=0 NormalY=0 NormalZ=1 AngleXU=0 Radius=1.8
    g24: Circle CenterX=213.443 CenterY=-76.8316 CenterZ=0 NormalX=0 NormalY=0 NormalZ=1 AngleXU=0 Radius=1.8
    g25: Circle CenterX=19 CenterY=21.2 CenterZ=0 NormalX=0 NormalY=0 NormalZ=1 AngleXU=0 Radius=6.3
    g26: Circle CenterX=42 CenterY=21.2 CenterZ=0 NormalX=0 NormalY=0 NormalZ=1 AngleXU=0 Radius=6.3
    g27: Circle CenterX=65 CenterY=21.2 CenterZ=0 NormalX=0 NormalY=0 NormalZ=1 AngleXU=0 Radius=6.3
    g28: LineSegment StartX=132.428 StartY=20 StartZ=0 EndX=144.053 EndY=20 EndZ=0
    g29: LineSegment StartX=147.645 StartY=8.94427 StartZ=0 EndX=144.053 EndY=20 EndZ=0
  constraints (65):
    c: Coincident(g0,g-4)
    c: Coincident(g0,g-5)
    c: Coincident(g1,g0)
    c: Coincident(g1,g-6)
    c: Coincident(g2,g1)
    c: Coincident(g2,g-7)
    c: Coincident(g3,g2)
    c: Coincident(g3,g-8)
    c: Coincident(g4,g0)
    c: Coincident(g4,g-16)
    c: Coincident(g5,g4)
    c: Coincident(g5,g-16)
    c: Coincident(g6,g-20)
    c: Coincident(g6,g-21)
    c: Coincident(g7,g6)
    c: Coincident(g7,g-23)
    c: Coincident(g8,g7)
    c: Coincident(g8,g-22)
    c: Coincident(g9,g8)
    c: Coincident(g9,g6)
    c: Equal(g10,g-8)
    c: Coincident(g10,g3)
    c: Coincident(g10,g-9)
    c: Coincident(g11,g10)
    c: Coincident(g11,g-10)
    c: Equal(g12,g-10)
    c: Coincident(g12,g11)
    c: Coincident(g12,g-11)
    c: Coincident(g13,g12)
    c: Coincident(g13,g-12)
    c: Coincident(g14,g13)
    c: Coincident(g14,g-13)
    c: Equal(g15,g-15)
    c: Coincident(g15,g5)
    c: Coincident(g15,g-15)
    c: Equal(g16,g-13)
    c: Coincident(g16,g14)
    c: Coincident(g16,g-14)
    c: Coincident(g17,g15)
    c: Coincident(g17,g16)
    c: Equal(g18,g-28)
    c: Equal(g19,g-29)
    c: Equal(g20,g-26)
    c: Equal(g21,g-27)
    c: Equal(g22,g-17)
    c: Equal(g24,g-25)
    c: Equal(g23,g-24)
    c: Coincident(g23,g-24)
    c: Coincident(g24,g-25)
    c: Coincident(g22,g-17)
    c: Coincident(g20,g-26)
    c: Coincident(g21,g-27)
    c: Coincident(g18,g-28)
    c: Coincident(g19,g-29)
    c: Equal(g25,g-30)
    c: Equal(g26,g-31)
    c: Equal(g27,g-32)
    c: Coincident(g25,g-30)
    c: Coincident(g26,g-31)
    c: Coincident(g27,g-32)
    c: Parallel(g28,g11)
    c: Parallel(g29,g13)
    c: Coincident(g28,g11)
    c: Coincident(g29,g12)
    c: Coincident(g29,g28)
FEATURE [PartDesign::Pad] Pad019
  Direction = (0,1,-2e-16)
  Length = 2
  Length2 = 10
  Profile = -> Sketch133
  ReferenceAxis = -> Sketch133 [N_Axis]
  Refine = true
  Suppressed = false
  Type = 0
FEATURE [Sketcher::SketchObject] Sketch091  label="Sketch091 - forma anteriore"
  ArcFitTolerance = 1e-06
  AttachmentSupport = -> [Pad019]
  ExternalGeometry = -> [Binder]
  FullyConstrained = true
  MakeInternals = false
  MapMode = 5
  Placement = pos=(0,2,0) rot=(0,0.707107,0.707107;3.14159rad)
  sketch-geometry (12):
    g0: Circle CenterX=5.6 CenterY=34.8 CenterZ=0 NormalX=0 NormalY=0 NormalZ=1 AngleXU=0 Radius=1.8
    g1: Circle CenterX=5.6 CenterY=7.6 CenterZ=0 NormalX=0 NormalY=0 NormalZ=1 AngleXU=0 Radius=1.8
    g2: Circle CenterX=78.51 CenterY=34.8 CenterZ=0 NormalX=0 NormalY=0 NormalZ=1 AngleXU=0 Radius=1.8
    g3: Circle CenterX=78.51 CenterY=7.6 CenterZ=0 NormalX=0 NormalY=0 NormalZ=1 AngleXU=0 Radius=1.8
    g4: LineSegment StartX=0 StartY=39.2 StartZ=0 EndX=0 EndY=3.2 EndZ=0
    g5: LineSegment StartX=0 StartY=3.2 StartZ=0 EndX=82.8 EndY=3.2 EndZ=0
    g6: LineSegment StartX=82.8 StartY=3.2 StartZ=0 EndX=82.8 EndY=39.2 EndZ=0
    g7: LineSegment StartX=82.8 StartY=39.2 StartZ=0 EndX=0 EndY=39.2 EndZ=0
    g8: ArcOfCircle CenterX=19 CenterY=21.2 CenterZ=0 NormalX=0 NormalY=0 NormalZ=1 AngleXU=0 Radius=10 StartAngle=1.5708 EndAngle=4.71239
    g9: ArcOfCircle CenterX=65 CenterY=21.2 CenterZ=0 NormalX=0 NormalY=0 NormalZ=1 AngleXU=0 Radius=10 StartAngle=4.71239 EndAngle=7.85398
    g10: LineSegment StartX=19 StartY=31.2 StartZ=0 EndX=65 EndY=31.2 EndZ=0
    g11: LineSegment StartX=19 StartY=11.2 StartZ=0 EndX=65 EndY=11.2 EndZ=0
  constraints (25):
    c: Equal(g2,g-7)
    c: Equal(g3,g-8)
    c: Equal(g1,g-13)
    c: Equal(g0,g-12)
    c: Coincident(g0,g-12)
    c: Coincident(g1,g-13)
    c: Coincident(g3,g-8)
    c: Coincident(g2,g-7)
    c: Coincident(g4,g-4)
    c: Coincident(g4,g-5)
    c: Coincident(g5,g4)
    c: Coincident(g5,g-6)
    c: Coincident(g6,g5)
    c: PointOnObject(g6,g-3)
    c: Vertical(g6)
    c: Coincident(g7,g6)
    c: Coincident(g7,g4)
    c: Tangent(g8,g10) = 1.5708
    c: Tangent(g8,g11) = -1.5708
    c: Tangent(g9,g10) = 1.5708
    c: Tangent(g9,g11) = -1.5708
    c: Equal(g8,g9)
    c: Radius(g8) = 10
    c: Coincident(g8,g-11)
    c: Coincident(g9,g-9)
FEATURE [Sketcher::SketchObject] Sketch093  label="Sketch093 - scavi interni pulsanti"
  ArcFitTolerance = 1e-06
  AttachmentSupport = -> [Pad019]
  ExternalGeometry = -> [Binder]
  FullyConstrained = true
  MakeInternals = false
  MapMode = 5
  Placement = pos=(0,1.8e-15,0) rot=(1,0,0;1.5708rad)
  sketch-geometry (3):
    g0: Circle CenterX=-65 CenterY=21.2 CenterZ=0 NormalX=0 NormalY=0 NormalZ=1 AngleXU=0 Radius=7.3
    g1: Circle CenterX=-42 CenterY=21.2 CenterZ=0 NormalX=0 NormalY=0 NormalZ=1 AngleXU=0 Radius=7.3
    g2: Circle CenterX=-19 CenterY=21.2 CenterZ=0 NormalX=0 NormalY=0 NormalZ=1 AngleXU=0 Radius=7.3
  constraints (6):
    c: Coincident(g0,g-3)
    c: Coincident(g1,g-4)
    c: Coincident(g2,g-5)
    c: Diameter(g0) = 14.6
    c: Diameter(g1) = 14.6
    c: Diameter(g2) = 14.6
FEATURE [Sketcher::SketchObject] Sketch094  label="Sketch094 - forma centrale"
  ArcFitTolerance = 1e-06
  AttachmentSupport = -> [Pad019]
  ExternalGeometry = -> [Binder]
  FullyConstrained = true
  MakeInternals = false
  MapMode = 5
  Placement = pos=(0,2,0) rot=(0,0.707107,0.707107;3.14159rad)
  sketch-geometry (4):
    g0: LineSegment StartX=137.815 StartY=39.2 StartZ=0 EndX=142.655 EndY=24.303 EndZ=0
    g1: LineSegment StartX=110.815 StartY=24.303 StartZ=0 EndX=142.655 EndY=24.303 EndZ=0
    g2: LineSegment StartX=137.815 StartY=39.2 StartZ=0 EndX=110.815 EndY=39.2 EndZ=0
    g3: ArcOfCircle CenterX=92.2534 CenterY=31.7515 CenterZ=0 NormalX=0 NormalY=0 NormalZ=1 AngleXU=0 Radius=20 StartAngle=5.90156 EndAngle=6.66481
  constraints (12):
    c: PointOnObject(g0,g-3)
    c: Tangent(g0,g-5)
    c: Horizontal(g1)
    c: Coincident(g1,g0)
    c: Coincident(g2,g0)
    c: PointOnObject(g2,g-3)
    c: DistanceX(g2,g2) = 27
    c: Vertical(g1,g2)
    c: Coincident(g3,g2)
    c: Radius(g3) = 20
    c: Coincident(g3,g1)
    c: DistanceY(g-6,g0) = 4
FEATURE [Sketcher::SketchObject] Sketch095  label="Sketch095 - forma posteriore"
  ArcFitTolerance = 1e-06
  AttachmentSupport = -> [Pad019]
  ExternalGeometry = -> [Binder]
  FullyConstrained = true
  MakeInternals = false
  MapMode = 5
  Placement = pos=(0,2,0) rot=(0,0.707107,0.707107;3.14159rad)
  sketch-geometry (15):
    g0: LineSegment StartX=137.815 StartY=39.2 StartZ=0 EndX=143.955 EndY=20.303 EndZ=0
    g1: LineSegment StartX=143.955 StartY=20.303 StartZ=0 EndX=190.141 EndY=20.303 EndZ=0
    g2: ArcOfCircle CenterX=184.08 CenterY=34.8 CenterZ=0 NormalX=0 NormalY=0 NormalZ=1 AngleXU=0 Radius=3.5 StartAngle=3.49066 EndAngle=4.71239
    g3: LineSegment StartX=180.791 StartY=33.6029 StartZ=0 EndX=178.754 EndY=39.2 EndZ=0
    g4: LineSegment StartX=184.08 StartY=31.3 StartZ=0 EndX=186.139 EndY=31.3 EndZ=0
    g5: LineSegment StartX=190.141 StartY=20.303 StartZ=0 EndX=186.139 EndY=31.3 EndZ=0
    g6: LineSegment StartX=137.815 StartY=39.2 StartZ=0 EndX=156.815 EndY=39.2 EndZ=0
    g7: LineSegment StartX=178.754 StartY=39.2 StartZ=0 EndX=168.815 EndY=39.2 EndZ=0
    g8: LineSegment StartX=156.815 StartY=31.2 StartZ=0 EndX=168.815 EndY=31.2 EndZ=0
    g9: ArcOfCircle CenterX=176.411 CenterY=35.2 CenterZ=0 NormalX=0 NormalY=0 NormalZ=1 AngleXU=0 Radius=20 StartAngle=2.94023 EndAngle=3.34295
    g10: ArcOfCircle CenterX=188.411 CenterY=35.2 CenterZ=0 NormalX=0 NormalY=0 NormalZ=1 AngleXU=0 Radius=20 StartAngle=2.94023 EndAngle=3.34295
    g11: LineSegment StartX=157.815 StartY=39.2 StartZ=0 EndX=167.815 EndY=39.2 EndZ=0
    g12: LineSegment StartX=157.436 StartY=36.2 StartZ=0 EndX=167.436 EndY=36.2 EndZ=0
    g13: ArcOfCircle CenterX=177.411 CenterY=35.2 CenterZ=0 NormalX=0 NormalY=0 NormalZ=1 AngleXU=0 Radius=20 StartAngle=2.94023 EndAngle=3.09157
    g14: ArcOfCircle CenterX=187.411 CenterY=35.2 CenterZ=0 NormalX=0 NormalY=0 NormalZ=1 AngleXU=0 Radius=20 StartAngle=2.94023 EndAngle=3.09157
  constraints (46):
    c: PointOnObject(g0,g-3)
    c: Tangent(g0,g-6)
    c: Coincident(g1,g0)
    c: Horizontal(g1)
    c: Radius(g2) = 3.5
    c: Coincident(g2,g-5)
    c: PointOnObject(g3,g-3)
    c: Parallel(g3,g-4)
    c: Tangent(g3,g2) = 1.5708
    c: Horizontal(g4)
    c: Tangent(g4,g2) = -1.5708
    c: Coincident(g5,g1)
    c: Parallel(g5,g-4)
    c: Coincident(g5,g4)
    c: DistanceX(g4,g-8) = 3.8
    c: Coincident(g6,g0)
    c: PointOnObject(g6,g-3)
    c: Coincident(g7,g3)
    c: PointOnObject(g7,g-3)
    c: Horizontal(g8)
    c: DistanceX(g6,g7) = 12
    c: Vertical(g8,g6)
    c: Vertical(g7,g8)
    c: DistanceY(g8,g6) = 8
    c: Coincident(g9,g8)
    c: Coincident(g9,g6)
    c: Coincident(g10,g7)
    c: Coincident(g10,g8)
    c: Radius(g9) = 20
    c: Radius(g10) = 20
    c: PointOnObject(g11,g-3)
    c: PointOnObject(g11,g-3)
    c: DistanceX(g11,g11) = 10
    c: DistanceX(g6,g11) = 1
    c: Horizontal(g12)
    c: Equal(g12,g11)
    c: DistanceY(g12,g11) = 3
    c: Coincident(g13,g11)
    c: Coincident(g13,g12)
    c: Radius(g13) = 20
    c: Coincident(g14,g11)
    c: Coincident(g14,g12)
    c: Radius(g14) = 20
    c: DistanceX(g0,g6) = 19
    c: Horizontal(g9,g13)
    c: Horizontal(g0,g-4)
FEATURE [Sketcher::SketchObject] Sketch096  label="Sketch096 - forma impugnatura"
  ArcFitTolerance = 1e-06
  AttachmentSupport = -> [Pad019]
  ExternalGeometry = -> [Binder]
  FullyConstrained = true
  MakeInternals = false
  MapMode = 5
  Placement = pos=(0,2,0) rot=(0,0.707107,0.707107;3.14159rad)
  sketch-geometry (8):
    g0: LineSegment StartX=176.685 StartY=-80.4316 StartZ=0 EndX=143.955 EndY=20.303 EndZ=0
    g1: LineSegment StartX=176.685 StartY=-80.4316 StartZ=0 EndX=215.932 EndY=-80.4316 EndZ=0
    g2: Circle CenterX=179.305 CenterY=-76.8316 CenterZ=0 NormalX=0 NormalY=0 NormalZ=1 AngleXU=0 Radius=3
    g3: Circle CenterX=213.443 CenterY=-76.8316 CenterZ=0 NormalX=0 NormalY=0 NormalZ=1 AngleXU=0 Radius=3
    g4: LineSegment StartX=143.955 StartY=20.303 StartZ=0 EndX=202.765 EndY=20.303 EndZ=0
    g5: LineSegment StartX=215.42 StartY=-53.0314 StartZ=0 EndX=192.176 EndY=-3.18451 EndZ=0
    g6: ArcOfCircle CenterX=184.801 CenterY=-67.3089 CenterZ=0 NormalX=0 NormalY=0 NormalZ=1 AngleXU=0 Radius=33.7833 StartAngle=5.88425 EndAngle=6.71952
    g7: ArcOfCircle CenterX=207.583 CenterY=4 CenterZ=0 NormalX=0 NormalY=0 NormalZ=1 AngleXU=0 Radius=17 StartAngle=1.85815 EndAngle=3.57792
  constraints (19):
    c: Coincident(g0,g-4)
    c: PointOnObject(g0,g-3)
    c: Horizontal(g0,g-7)
    c: Coincident(g1,g0)
    c: Coincident(g1,g-5)
    c: Diameter(g2) = 6
    c: Diameter(g3) = 6
    c: Coincident(g2,g-9)
    c: Coincident(g3,g-10)
    c: Coincident(g4,g0)
    c: Coincident(g5,g-6)
    c: Coincident(g6,g1)
    c: Coincident(g6,g5)
    c: Equal(g-5,g6)
    c: Coincident(g5,g-7)
    c: Coincident(g4,g-7)
    c: Tangent(g7,g-7)
    c: Coincident(g7,g4)
    c: Coincident(g7,g5)
FEATURE [Sketcher::SketchObject] Sketch097
  ArcFitTolerance = 1e-06
  AttachmentSupport = -> [Pad019]
  ExternalGeometry = -> [Binder]
  FullyConstrained = true
  MakeInternals = false
  MapMode = 5
  Placement = pos=(0,2,0) rot=(0,0.707107,0.707107;3.14159rad)
  sketch-geometry (4):
    g0: LineSegment StartX=90 StartY=36.8 StartZ=0 EndX=108 EndY=36.8 EndZ=0
    g1: LineSegment StartX=108 StartY=36.8 StartZ=0 EndX=108 EndY=26.8 EndZ=0
    g2: LineSegment StartX=108 StartY=26.8 StartZ=0 EndX=90 EndY=26.8 EndZ=0
    g3: ArcOfCircle CenterX=94 CenterY=31.8 CenterZ=0 NormalX=0 NormalY=0 NormalZ=1 AngleXU=0 Radius=6.40312 StartAngle=2.24554 EndAngle=4.03765
  constraints (13):
    c: Horizontal(g0)
    c: Coincident(g1,g0)
    c: Vertical(g1)
    c: DistanceX(g0,g0) = 18
    c: DistanceY(g1,g1) = 10
    c: Coincident(g2,g1)
    c: Horizontal(g2)
    c: Equal(g2,g0)
    c: DistanceY(g0,g-3) = 2.4
    c: Coincident(g3,g0)
    c: Coincident(g3,g2)
    c: DistanceX(g2,g3) = 4
    c: DistanceX(g-3,g0) = 90
FEATURE [PartDesign::Chamfer] Chamfer015
  Angle = 45
  Base = -> Pad019 [Edge19,Edge22,Edge79]
  BaseFeature = -> Pad019
  ChamferType = 0
  FlipDirection = false
  Refine = true
  Size = 1.9
  Size2 = 1
  SupportTransform = false
  Suppressed = false
  UseAllEdges = false
FEATURE [PartDesign::Pocket] Pocket002
  BaseFeature = -> Chamfer015
  Direction = (0,1,-2e-16)
  Length = 1.2
  Length2 = 5
  Profile = -> Sketch093
  ReferenceAxis = -> Sketch093 [N_Axis]
  Refine = true
  Suppressed = false
  Type = 0
FEATURE [PartDesign::Pad] Pad005
  BaseFeature = -> Pocket002
  Direction = (0,1,-2e-16)
  Length = 1.6
  Length2 = 10
  Profile = -> Sketch091
  ReferenceAxis = -> Sketch091 [N_Axis]
  Refine = true
  Suppressed = false
  Type = 0
FEATURE [Sketcher::SketchObject] Sketch092  label="Sketch092 - scavi per viti anteriori"
  ArcFitTolerance = 1e-06
  AttachmentSupport = -> [Pad005]
  ExternalGeometry = -> [Binder]
  FullyConstrained = true
  MakeInternals = false
  MapMode = 5
  Placement = pos=(0,3.6,0) rot=(0,0.707107,0.707107;3.14159rad)
  sketch-geometry (20):
    g0: ArcOfCircle CenterX=5.6 CenterY=7.6 CenterZ=0 NormalX=0 NormalY=0 NormalZ=1 AngleXU=0 Radius=3.5 StartAngle=0 EndAngle=1.5708
    g1: ArcOfCircle CenterX=5.6 CenterY=34.8 CenterZ=0 NormalX=0 NormalY=0 NormalZ=1 AngleXU=0 Radius=3.5 StartAngle=4.71239 EndAngle=6.28319
    g2: ArcOfCircle CenterX=78.51 CenterY=34.8 CenterZ=0 NormalX=0 NormalY=0 NormalZ=1 AngleXU=0 Radius=3.5 StartAngle=3.14159 EndAngle=4.71239
    g3: ArcOfCircle CenterX=78.51 CenterY=7.6 CenterZ=0 NormalX=0 NormalY=0 NormalZ=1 AngleXU=0 Radius=3.5 StartAngle=1.5708 EndAngle=3.14159
    g4: LineSegment StartX=0 StartY=3.2 StartZ=0 EndX=0 EndY=11.1 EndZ=0
    g5: LineSegment StartX=0 StartY=11.1 StartZ=0 EndX=5.6 EndY=11.1 EndZ=0
    g6: LineSegment StartX=0 StartY=3.2 StartZ=0 EndX=9.1 EndY=3.2 EndZ=0
    g7: LineSegment StartX=9.1 StartY=3.2 StartZ=0 EndX=9.1 EndY=7.6 EndZ=0
    g8: LineSegment StartX=0 StartY=39.2 StartZ=0 EndX=0 EndY=31.3 EndZ=0
    g9: LineSegment StartX=0 StartY=31.3 StartZ=0 EndX=5.6 EndY=31.3 EndZ=0
    g10: LineSegment StartX=0 StartY=39.2 StartZ=0 EndX=9.1 EndY=39.2 EndZ=0
    g11: LineSegment StartX=9.1 StartY=39.2 StartZ=0 EndX=9.1 EndY=34.8 EndZ=0
    g12: LineSegment StartX=82.8 StartY=39.2 StartZ=0 EndX=75.01 EndY=39.2 EndZ=0
    g13: LineSegment StartX=82.8 StartY=39.2 StartZ=0 EndX=82.8 EndY=31.3 EndZ=0
    g14: LineSegment StartX=82.8 StartY=31.3 StartZ=0 EndX=78.51 EndY=31.3 EndZ=0
    g15: LineSegment StartX=82.8 StartY=3.2 StartZ=0 EndX=75.01 EndY=3.2 EndZ=0
    g16: LineSegment StartX=75.01 StartY=3.2 StartZ=0 EndX=75.01 EndY=7.6 EndZ=0
    g17: LineSegment StartX=82.8 StartY=3.2 StartZ=0 EndX=82.8 EndY=11.1 EndZ=0
    g18: LineSegment StartX=82.8 StartY=11.1 StartZ=0 EndX=78.51 EndY=11.1 EndZ=0
    g19: LineSegment StartX=75.01 StartY=39.2 StartZ=0 EndX=75.01 EndY=34.8 EndZ=0
  constraints (48):
    c: Radius(g0) = 3.5
    c: Coincident(g0,g-10)
    c: Radius(g1) = 3.5
    c: Coincident(g1,g-9)
    c: Radius(g2) = 3.5
    c: Coincident(g2,g-8)
    c: Radius(g3) = 3.5
    c: Coincident(g3,g-7)
    c: Coincident(g4,g-5)
    c: PointOnObject(g4,g-4)
    c: Coincident(g5,g4)
    c: Horizontal(g5)
    c: Coincident(g6,g4)
    c: PointOnObject(g6,g-5)
    c: Coincident(g7,g6)
    c: Vertical(g7)
    c: Coincident(g8,g-4)
    c: PointOnObject(g8,g-4)
    c: Coincident(g9,g8)
    c: Horizontal(g9)
    c: Coincident(g10,g8)
    c: PointOnObject(g10,g-3)
    c: Coincident(g11,g10)
    c: Vertical(g11)
    c: PointOnObject(g12,g-3)
    c: PointOnObject(g12,g-3)
    c: Coincident(g13,g12)
    c: Vertical(g13)
    c: Coincident(g14,g13)
    c: Horizontal(g14)
    c: Coincident(g15,g-6)
    c: PointOnObject(g15,g-5)
    c: Coincident(g16,g15)
    c: Vertical(g16)
    c: Coincident(g17,g15)
    c: Coincident(g18,g17)
    c: Horizontal(g18)
    c: Tangent(g3,g18) = -1.5708
    c: Tangent(g16,g3) = 1.5708
    c: Coincident(g19,g12)
    c: Vertical(g19)
    c: Tangent(g2,g19) = -1.5708
    c: Tangent(g2,g14) = 1.5708
    c: Tangent(g0,g7) = -1.5708
    c: Tangent(g0,g5) = 1.5708
    c: Tangent(g9,g1) = -1.5708
    c: Tangent(g1,g11) = 1.5708
    c: Tangent(g17,g13)
FEATURE [PartDesign::Pocket] Pocket001
  BaseFeature = -> Pad005
  Direction = (0,-1,2e-16)
  Length = 1.6
  Length2 = 5
  Profile = -> Sketch092
  ReferenceAxis = -> Sketch092 [N_Axis]
  Refine = true
  Suppressed = false
  Type = 0
FEATURE [PartDesign::Pad] Pad006
  BaseFeature = -> Pocket001
  Direction = (0,1,-2e-16)
  Length = 0.8
  Length2 = 10
  Profile = -> Sketch094
  ReferenceAxis = -> Sketch094 [N_Axis]
  Refine = true
  Suppressed = false
  Type = 0
FEATURE [PartDesign::Pad] Pad007
  BaseFeature = -> Pad006
  Direction = (0,1,-2e-16)
  Length = 2
  Length2 = 10
  Profile = -> Sketch095
  ReferenceAxis = -> Sketch095 [N_Axis]
  Refine = true
  Suppressed = false
  Type = 0
FEATURE [PartDesign::Pad] Pad008  label="Pad008 - forma impugnatura"
  BaseFeature = -> Pad007
  Direction = (0,1,-2e-16)
  Length = 1.6
  Length2 = 10
  Profile = -> Sketch096
  ReferenceAxis = -> Sketch096 [N_Axis]
  Refine = true
  Suppressed = false
  Type = 0
FEATURE [PartDesign::Pad] Pad009
  BaseFeature = -> Pad008
  Direction = (0,1,-2e-16)
  Length = 1.6
  Length2 = 10
  Profile = -> Sketch097
  ReferenceAxis = -> Sketch097 [N_Axis]
  Refine = true
  Suppressed = false
  Type = 0
FEATURE [Sketcher::SketchObject] Sketch098
  ArcFitTolerance = 1e-06
  AttachmentSupport = -> [Pad006]
  ExternalGeometry = -> [Binder]
  FullyConstrained = true
  MakeInternals = false
  MapMode = 5
  Placement = pos=(0,2.8,-7e-16) rot=(0,0.707107,0.707107;3.14159rad)
  sketch-geometry (4):
    g0: LineSegment StartX=118 StartY=39.2 StartZ=0 EndX=129 EndY=39.2 EndZ=0
    g1: LineSegment StartX=120.599 StartY=31.2 StartZ=0 EndX=131.599 EndY=31.2 EndZ=0
    g2: LineSegment StartX=129 StartY=39.2 StartZ=0 EndX=131.599 EndY=31.2 EndZ=0
    g3: LineSegment StartX=118 StartY=39.2 StartZ=0 EndX=120.599 EndY=31.2 EndZ=0
  constraints (12):
    c: PointOnObject(g0,g-3)
    c: PointOnObject(g0,g-3)
    c: DistanceX(g0,g0) = 11
    c: Horizontal(g1)
    c: Equal(g1,g0)
    c: Coincident(g2,g0)
    c: Coincident(g3,g0)
    c: Parallel(g-4,g2)
    c: Coincident(g1,g2)
    c: Coincident(g1,g3)
    c: DistanceY(g1,g0) = 8
    c: DistanceX(g-3,g0) = 118
FEATURE [Sketcher::SketchObject] Sketch099
  ArcFitTolerance = 1e-06
  AttachmentSupport = -> [Pad008]
  ExternalGeometry = -> [Binder]
  FullyConstrained = true
  MakeInternals = false
  MapMode = 5
  Placement = pos=(0,3.6,0) rot=(0,0.707107,0.707107;3.14159rad)
  sketch-geometry (13):
    g0: LineSegment StartX=192.176 StartY=-3.18451 StartZ=0 EndX=196.804 EndY=-13.1108 EndZ=0
    g1: LineSegment [constr] StartX=202.765 StartY=20.303 StartZ=0 EndX=181.223 EndY=20.303 EndZ=0
    g2: LineSegment [constr] StartX=181.223 StartY=20.303 StartZ=0 EndX=181.223 EndY=-3.18451 EndZ=0
    g3: ArcOfCircle CenterX=181.223 CenterY=-20.3764 CenterZ=0 NormalX=0 NormalY=0 NormalZ=1 AngleXU=0 Radius=17.1918 StartAngle=0.436332 EndAngle=1.57079
    g4: ArcOfEllipse CenterX=181.223 CenterY=8.55923 CenterZ=0 NormalX=0 NormalY=0 NormalZ=1 MajorRadius=23.4779 MinorRadius=11.7437 AngleXU=0 StartAngle=1.5708 EndAngle=4.71239
    g5: LineSegment [constr] StartX=204.701 StartY=8.55923 StartZ=0 EndX=157.745 EndY=8.55923 EndZ=0
    g6: LineSegment [constr] StartX=181.223 StartY=20.303 StartZ=0 EndX=181.223 EndY=-3.18451 EndZ=0
    g7: GeomPoint [constr] X=201.553 Y=8.55923 Z=0
    g8: GeomPoint [constr] X=160.894 Y=8.55923 Z=0
    g9: GeomPoint [constr] X=181.223 Y=-3.18451 Z=0
    g10: LineSegment StartX=181.223 StartY=20.303 StartZ=0 EndX=202.765 EndY=20.303 EndZ=0
    g11: ArcOfCircle CenterX=207.583 CenterY=4 CenterZ=0 NormalX=0 NormalY=0 NormalZ=1 AngleXU=0 Radius=17 StartAngle=1.85815 EndAngle=3.57792
    g12: LineSegment [constr] StartX=172.411 StartY=39.2 StartZ=0 EndX=192.176 EndY=-3.18451 EndZ=0
  constraints (27):
    c: Coincident(g1,g-7)
    c: Horizontal(g1)
    c: Coincident(g2,g1)
    c: Vertical(g2)
    c: Horizontal(g2,g0)
    c: Coincident(g3,g0)
    c: Coincident(g3,g2)
    c: InternalAlignment(g5-g8 -> g4) x4
    c: Horizontal(g5)
    c: PointOnObject(g4,g2)
    c: Coincident(g4,g1)
    c: DistanceX(g-3,g5) = 10.1
    c: Coincident(g4,g2)
    c: Tangent(g3,g-5)
    c: PointOnObject(g9,g4)
    c: PointOnObject(g9,g3)
    c: Tangent(g4,g3,g9) = 1.5708
    c: Coincident(g10,g1)
    c: Coincident(g10,g1)
    c: Equal(g11,g-4)
    c: Coincident(g11,g1)
    c: Coincident(g11,g0)
    c: PointOnObject(g12,g-6)
    c: PointOnObject(g1,g12)
    c: Tangent(g12,g-5) = -1.5708
    c: Tangent(g0,g-5) = -1.5708
    c: Horizontal(g9,g12)
FEATURE [Sketcher::SketchObject] Sketch106  label="Sketch106 - smusso impuniatura interno"
  ArcFitTolerance = 1e-06
  AttachmentSupport = -> [Pad008]
  ExternalGeometry = -> [Pad008]
  FullyConstrained = true
  MakeInternals = false
  MapMode = 5
  Placement = pos=(0,-1.586e-13,-80.4316) rot=(1,0,0;3.14159rad)
  sketch-geometry (9):
    g0: LineSegment StartX=-176.685 StartY=-3.6 StartZ=0 EndX=-176.685 EndY=-1.421e-13 EndZ=0
    g1: LineSegment [constr] StartX=-176.685 StartY=-1.416e-13 StartZ=0 EndX=-176.685 EndY=-1.419e-13 EndZ=0
    g2: LineSegment [constr] StartX=-186.685 StartY=-3.6 StartZ=0 EndX=-186.685 EndY=-1.421e-13 EndZ=0
    g3: ArcOfEllipse CenterX=-186.685 CenterY=-1.419e-13 CenterZ=0 NormalX=0 NormalY=0 NormalZ=1 MajorRadius=10 MinorRadius=3.6 AngleXU=-3.14159 StartAngle=1.5708 EndAngle=3.14159
    g4: LineSegment [constr] StartX=-196.685 StartY=-1.416e-13 StartZ=0 EndX=-176.685 EndY=-1.416e-13 EndZ=0
    g5: LineSegment [constr] StartX=-186.685 StartY=-3.6 StartZ=0 EndX=-186.685 EndY=3.6 EndZ=0
    g6: GeomPoint [constr] X=-196.015 Y=-1.425e-13 Z=0
    g7: GeomPoint [constr] X=-177.356 Y=-1.415e-13 Z=0
    g8: LineSegment StartX=-176.685 StartY=-3.6 StartZ=0 EndX=-186.685 EndY=-3.6 EndZ=0
  constraints (15):
    c: PointOnObject(g2,g-3)
    c: Coincident(g1,g-5)
    c: DistanceY(g1,g1) = 0
    c: Coincident(g0,g1)
    c: DistanceX(g2,g-5) = 10
    c: Vertical(g2)
    c: Horizontal(g2,g0)
    c: InternalAlignment(g4-g7 -> g3) x4
    c: Coincident(g3,g2)
    c: Horizontal(g4)
    c: Coincident(g3,g0)
    c: Tangent(g0,g-5) = 1.5708
    c: Coincident(g3,g2)
    c: Coincident(g8,g0)
    c: Coincident(g8,g2)
FEATURE [Sketcher::SketchObject] Sketch107  label="Sketch107 - smusso impugnatura esterno"
  ArcFitTolerance = 1e-06
  AttachmentSupport = -> [Pad008]
  ExternalGeometry = -> [Pad008]
  FullyConstrained = true
  MakeInternals = false
  MapMode = 5
  Placement = pos=(0,-1.586e-13,-80.4316) rot=(1,0,0;3.14159rad)
  sketch-geometry (9):
    g0: LineSegment [constr] StartX=-215.932 StartY=-1.416e-13 StartZ=0 EndX=-215.932 EndY=-5.02e-14 EndZ=0
    g1: LineSegment StartX=-215.932 StartY=-3.6 StartZ=0 EndX=-215.932 EndY=-5.02e-14 EndZ=0
    g2: LineSegment StartX=-215.932 StartY=-3.6 StartZ=0 EndX=-205.932 EndY=-3.6 EndZ=0
    g3: LineSegment [constr] StartX=-205.932 StartY=-3.6 StartZ=0 EndX=-205.932 EndY=-5.02e-14 EndZ=0
    g4: ArcOfEllipse CenterX=-205.932 CenterY=-5.02e-14 CenterZ=0 NormalX=0 NormalY=0 NormalZ=1 MajorRadius=10 MinorRadius=3.6 AngleXU=-3.14159 StartAngle=-2.66e-14 EndAngle=1.5708
    g5: LineSegment [constr] StartX=-215.932 StartY=-1.416e-13 StartZ=0 EndX=-195.932 EndY=-1.416e-13 EndZ=0
    g6: LineSegment [constr] StartX=-205.932 StartY=-3.6 StartZ=0 EndX=-205.932 EndY=3.6 EndZ=0
    g7: GeomPoint [constr] X=-215.262 Y=-1.394e-13 Z=0
    g8: GeomPoint [constr] X=-196.602 Y=-1.551e-13 Z=0
  constraints (16):
    c: Coincident(g0,g-6)
    c: PointOnObject(g0,g-6)
    c: DistanceY(g0,g0) = 0
    c: Coincident(g1,g-6)
    c: Coincident(g1,g0)
    c: Tangent(g2,g-3)
    c: DistanceX(g2,g2) = 10
    c: Coincident(g3,g2)
    c: Vertical(g3)
    c: Horizontal(g3,g0)
    c: InternalAlignment(g5-g8 -> g4) x4
    c: Coincident(g4,g3)
    c: Horizontal(g5)
    c: Coincident(g4,g0)
    c: Coincident(g4,g2)
    c: PointOnObject(g2,g1)
FEATURE [Sketcher::SketchObject] Sketch108
  ArcFitTolerance = 1e-06
  AttachmentOffset = pos=(0,0,-1.6) rot=(0,0,1;0rad)
  AttachmentSupport = -> [Pad008]
  ExternalGeometry = -> [Binder]
  FullyConstrained = true
  MakeInternals = false
  MapMode = 5
  Placement = pos=(0,2,4e-16) rot=(0,0.707107,0.707107;3.14159rad)
  sketch-geometry (14):
    g0: LineSegment StartX=192.176 StartY=-3.18451 StartZ=0 EndX=193.827 EndY=-6.72678 EndZ=0
    g1: LineSegment [constr] StartX=202.765 StartY=20.303 StartZ=0 EndX=181.223 EndY=20.303 EndZ=0
    g2: LineSegment [constr] StartX=181.223 StartY=20.303 StartZ=0 EndX=181.223 EndY=1.30297 EndZ=0
    g3: ArcOfCircle CenterX=181.223 CenterY=-12.6042 CenterZ=0 NormalX=0 NormalY=0 NormalZ=1 AngleXU=0 Radius=13.9072 StartAngle=0.436332 EndAngle=1.5708
    g4: ArcOfEllipse CenterX=181.223 CenterY=10.803 CenterZ=0 NormalX=0 NormalY=0 NormalZ=1 MajorRadius=14.4779 MinorRadius=9.5 AngleXU=0 StartAngle=1.5708 EndAngle=4.71239
    g5: LineSegment [constr] StartX=195.701 StartY=10.803 StartZ=0 EndX=166.745 EndY=10.803 EndZ=0
    g6: LineSegment [constr] StartX=181.223 StartY=20.303 StartZ=0 EndX=181.223 EndY=1.30297 EndZ=0
    g7: GeomPoint [constr] X=192.148 Y=10.803 Z=0
    g8: GeomPoint [constr] X=170.298 Y=10.803 Z=0
    g9: LineSegment StartX=181.223 StartY=20.303 StartZ=0 EndX=202.765 EndY=20.303 EndZ=0
    g10: ArcOfCircle CenterX=207.583 CenterY=4 CenterZ=0 NormalX=0 NormalY=0 NormalZ=1 AngleXU=0 Radius=17 StartAngle=1.85815 EndAngle=3.57792
    g11: LineSegment [constr] StartX=172.411 StartY=39.2 StartZ=0 EndX=192.176 EndY=-3.18451 EndZ=0
    g12: GeomPoint [constr] X=181.223 Y=1.30297 Z=0
    g13: GeomPoint [constr] X=181.223 Y=1.30297 Z=0
  constraints (28):
    c: Coincident(g1,g-7)
    c: Horizontal(g1)
    c: Coincident(g2,g1)
    c: Vertical(g2)
    c: Coincident(g3,g2)
    c: InternalAlignment(g5-g8 -> g4) x4
    c: Horizontal(g5)
    c: PointOnObject(g4,g2)
    c: Coincident(g4,g1)
    c: DistanceX(g-3,g5) = 19.1
    c: Coincident(g4,g2)
    c: Coincident(g9,g1)
    c: Coincident(g9,g1)
    c: Coincident(g10,g1)
    c: Coincident(g10,g0)
    c: PointOnObject(g11,g-6)
    c: PointOnObject(g1,g11)
    c: DistanceY(g2,g1) = 19
    c: Coincident(g10,g-4)
    c: PointOnObject(g12,g4)
    c: PointOnObject(g12,g3)
    c: Tangent(g11,g-5) = -1.5708
    c: Tangent(g0,g-5) = -1.5708
    c: Tangent(g3,g0) = 1.5708
    c: PointOnObject(g13,g4)
    c: PointOnObject(g13,g3)
    c: Tangent(g4,g3,g13) = 1.5708
    c: Horizontal(g11,g0)
FEATURE [Part::Part2DObjectPython] Clone2D  label="Sketch108 (2D)"  # Draft 2D object (typed FeaturePython)
  Fuse = false
  Objects = -> [Sketch108]
  Placement = pos=(0,2,4e-16) rot=(0,0.707107,0.707107;3.14159rad)
  Scale = (1,1,1)
FEATURE [Sketcher::SketchObject] Sketch109
  ArcFitTolerance = 1e-06
  AttachmentOffset = pos=(0,0,-3.5) rot=(0,0,1;0rad)
  AttachmentSupport = -> [Pad008]
  ExternalGeometry = -> [Binder]
  FullyConstrained = true
  MakeInternals = false
  MapMode = 5
  Placement = pos=(0,0.1,8e-16) rot=(0,0.707107,0.707107;3.14159rad)
  sketch-geometry (1):
    g0: GeomPoint X=197.47 Y=8.55923 Z=0
  constraints (1):
    c: Symmetric(g-7,g-5,g0)
FEATURE [PartDesign::Chamfer] Chamfer005
  Angle = 45
  Base = -> Pad009 [Edge215,Edge212]
  BaseFeature = -> Pad009
  ChamferType = 1
  FlipDirection = false
  Refine = true
  Size = 1.5
  Size2 = 2.8
  SupportTransform = false
  Suppressed = false
  UseAllEdges = false
FEATURE [Sketcher::SketchObject] Sketch111
  ArcFitTolerance = 1e-06
  AttachmentSupport = -> [Pad009]
  ExternalGeometry = -> [Pad009]
  FullyConstrained = true
  MakeInternals = false
  MapMode = 5
  Placement = pos=(0,3.6,-8e-16) rot=(0,0.707107,0.707107;3.14159rad)
  sketch-geometry (21):
    g0: LineSegment [constr] StartX=97 StartY=36.8 StartZ=0 EndX=97 EndY=26.8 EndZ=0
    g1: LineSegment StartX=97 StartY=28.6 StartZ=0 EndX=97 EndY=27.8 EndZ=0
    g2: LineSegment StartX=97 StartY=27.8 StartZ=0 EndX=108 EndY=27.8 EndZ=0
    g3: LineSegment StartX=108 StartY=27.8 StartZ=0 EndX=108 EndY=28.6 EndZ=0
    g4: LineSegment StartX=108 StartY=28.6 StartZ=0 EndX=97 EndY=28.6 EndZ=0
    g5: LineSegment StartX=97 StartY=35.8 StartZ=0 EndX=97 EndY=35 EndZ=0
    g6: LineSegment StartX=97 StartY=35 StartZ=0 EndX=108 EndY=35 EndZ=0
    g7: LineSegment StartX=108 StartY=35 StartZ=0 EndX=108 EndY=35.8 EndZ=0
    g8: LineSegment StartX=108 StartY=35.8 StartZ=0 EndX=97 EndY=35.8 EndZ=0
    g9: LineSegment StartX=97 StartY=30.4 StartZ=0 EndX=97 EndY=29.6 EndZ=0
    g10: LineSegment StartX=97 StartY=29.6 StartZ=0 EndX=108 EndY=29.6 EndZ=0
    g11: LineSegment StartX=108 StartY=29.6 StartZ=0 EndX=108 EndY=30.4 EndZ=0
    g12: LineSegment StartX=108 StartY=30.4 StartZ=0 EndX=97 EndY=30.4 EndZ=0
    g13: LineSegment StartX=97 StartY=34 StartZ=0 EndX=97 EndY=33.2 EndZ=0
    g14: LineSegment StartX=97 StartY=33.2 StartZ=0 EndX=108 EndY=33.2 EndZ=0
    g15: LineSegment StartX=108 StartY=33.2 StartZ=0 EndX=108 EndY=34 EndZ=0
    g16: LineSegment StartX=108 StartY=34 StartZ=0 EndX=97 EndY=34 EndZ=0
    g17: LineSegment StartX=97 StartY=32.2 StartZ=0 EndX=97 EndY=31.4 EndZ=0
    g18: LineSegment StartX=97 StartY=31.4 StartZ=0 EndX=108 EndY=31.4 EndZ=0
    g19: LineSegment StartX=108 StartY=31.4 StartZ=0 EndX=108 EndY=32.2 EndZ=0
    g20: LineSegment StartX=108 StartY=32.2 StartZ=0 EndX=97 EndY=32.2 EndZ=0
  constraints (54):
    c: Vertical(g0)
    c: PointOnObject(g0,g-3)
    c: PointOnObject(g0,g-4)
    c: DistanceX(g0,g-5) = 11
    c: Coincident(g1,g2)
    c: Coincident(g2,g3)
    c: Coincident(g3,g4)
    c: Coincident(g4,g1)
    c: Horizontal(g2)
    c: Horizontal(g4)
    c: Tangent(g1,g0)
    c: Tangent(g3,g-5)
    c: DistanceY(g2,g3) = 0.8
    c: Coincident(g5,g6)
    c: Coincident(g6,g7)
    c: Coincident(g7,g8)
    c: Coincident(g8,g5)
    c: Horizontal(g6)
    c: Horizontal(g8)
    c: DistanceY(g6,g7) = 0.8
    c: Coincident(g9,g10)
    c: Coincident(g10,g11)
    c: Coincident(g11,g12)
    c: Coincident(g12,g9)
    c: Horizontal(g10)
    c: Horizontal(g12)
    c: DistanceY(g10,g11) = 0.8
    c: Tangent(g5,g0)
    c: Tangent(g7,g-5)
    c: Tangent(g9,g0)
    c: Tangent(g11,g-5)
    c: Coincident(g13,g14)
    c: Coincident(g14,g15)
    c: Coincident(g15,g16)
    c: Coincident(g16,g13)
    c: Horizontal(g14)
    c: Horizontal(g16)
    c: DistanceY(g14,g15) = 0.8
    c: Tangent(g13,g0)
    c: Tangent(g15,g-5)
    c: Coincident(g17,g18)
    c: Coincident(g18,g19)
    c: Coincident(g19,g20)
    c: Coincident(g20,g17)
    c: Horizontal(g18)
    c: Horizontal(g20)
    c: DistanceY(g18,g19) = 0.8
    c: Tangent(g17,g0)
    c: Tangent(g19,g-5)
    c: DistanceY(g1,g9) = 1
    c: DistanceY(g9,g17) = 1
    c: DistanceY(g17,g13) = 1
    c: DistanceY(g13,g5) = 1
    c: DistanceY(g0,g1) = 1
FEATURE [PartDesign::Pocket] Pocket004
  BaseFeature = -> Chamfer005
  Direction = (0,-1,2e-16)
  Length = 1
  Length2 = 5
  Profile = -> Sketch111
  ReferenceAxis = -> Sketch111 [N_Axis]
  Refine = true
  Suppressed = false
  Type = 0
FEATURE [PartDesign::Pad] Pad010
  BaseFeature = -> Pocket004
  Direction = (0,1,-2e-16)
  Length = 1.2
  Length2 = 10
  Profile = -> Sketch098
  ReferenceAxis = -> Sketch098 [N_Axis]
  Refine = true
  Suppressed = false
  Type = 0
FEATURE [PartDesign::Chamfer] Chamfer006
  Angle = 45
  Base = -> Pad010 [Edge291]
  BaseFeature = -> Pad010
  ChamferType = 1
  FlipDirection = false
  Refine = true
  Size = 1
  Size2 = 6
  SupportTransform = false
  Suppressed = false
  UseAllEdges = false
FEATURE [Sketcher::SketchObject] Sketch110
  ArcFitTolerance = 1e-06
  AttachmentSupport = -> [Pad010]
  ExternalGeometry = -> [Sketch098]
  FullyConstrained = true
  MakeInternals = false
  MapMode = 5
  Placement = pos=(0,4,-9e-16) rot=(0,0.707107,0.707107;3.14159rad)
  sketch-geometry (8):
    g0: LineSegment StartX=119.69 StartY=34 StartZ=0 EndX=130.69 EndY=34 EndZ=0
    g1: LineSegment StartX=119.95 StartY=33.2 StartZ=0 EndX=130.95 EndY=33.2 EndZ=0
    g2: LineSegment StartX=119.137 StartY=35.7 StartZ=0 EndX=130.137 EndY=35.7 EndZ=0
    g3: LineSegment StartX=118.877 StartY=36.5 StartZ=0 EndX=129.877 EndY=36.5 EndZ=0
    g4: LineSegment StartX=118.877 StartY=36.5 StartZ=0 EndX=119.137 EndY=35.7 EndZ=0
    g5: LineSegment StartX=129.877 StartY=36.5 StartZ=0 EndX=130.137 EndY=35.7 EndZ=0
    g6: LineSegment StartX=119.69 StartY=34 StartZ=0 EndX=119.95 EndY=33.2 EndZ=0
    g7: LineSegment StartX=130.69 StartY=34 StartZ=0 EndX=130.95 EndY=33.2 EndZ=0
  constraints (24):
    c: Horizontal(g0)
    c: Horizontal(g1)
    c: Horizontal(g2)
    c: Horizontal(g3)
    c: Equal(g1,g-5)
    c: Equal(g0,g-5)
    c: Equal(g2,g-5)
    c: Equal(g3,g-5)
    c: PointOnObject(g0,g-3)
    c: PointOnObject(g1,g-3)
    c: PointOnObject(g2,g-3)
    c: PointOnObject(g3,g-3)
    c: Coincident(g4,g3)
    c: Coincident(g4,g2)
    c: Coincident(g5,g3)
    c: Coincident(g5,g2)
    c: Coincident(g6,g0)
    c: Coincident(g6,g1)
    c: Coincident(g7,g0)
    c: Coincident(g7,g1)
    c: DistanceY(g1,g0) = 0.8
    c: DistanceY(g2,g3) = 0.8
    c: DistanceY(g-5,g1) = 2
    c: DistanceY(g-5,g2) = 4.5
FEATURE [PartDesign::Pocket] Pocket003
  BaseFeature = -> Chamfer006
  Direction = (0,-1,2e-16)
  Length = 1
  Length2 = 5
  Profile = -> Sketch110
  ReferenceAxis = -> Sketch110 [N_Axis]
  Refine = true
  Suppressed = false
  Type = 0
FEATURE [PartDesign::SubtractivePipe] SubtractivePipe
  AuxilleryCurvelinear = true
  AuxillerySpineTangent = false
  BaseFeature = -> Pocket003
  Binormal = (0,0,0)
  Mode = 0
  Profile = -> Sketch106
  Refine = true
  Spine = -> Pad008 [Edge215]
  SpineTangent = false
  Suppressed = false
  Transformation = 0
  Transition = 0
FEATURE [PartDesign::SubtractivePipe] SubtractivePipe001
  AuxilleryCurvelinear = true
  AuxillerySpineTangent = false
  BaseFeature = -> SubtractivePipe
  Binormal = (0,0,0)
  Mode = 0
  Profile = -> Sketch107
  Refine = true
  Spine = -> Pad008 [Edge213,Edge216,Edge210]
  SpineTangent = false
  Suppressed = false
  Transformation = 0
  Transition = 0
FEATURE [PartDesign::SubtractiveLoft] SubtractiveLoft
  BaseFeature = -> SubtractivePipe001
  Closed = false
  Profile = -> Sketch099
  Refine = true
  Ruled = false
  Sections = -> [Sketch108]
  Suppressed = false
FEATURE [PartDesign::SubtractiveLoft] SubtractiveLoft001
  BaseFeature = -> SubtractiveLoft
  Closed = false
  Profile = -> Clone2D
  Refine = true
  Ruled = false
  Sections = -> [Sketch109]
  Suppressed = false
FEATURE [Sketcher::SketchObject] Sketch112
  ArcFitTolerance = 1e-06
  AttachmentSupport = -> [Pad008]
  ExternalGeometry = -> [Binder]
  FullyConstrained = true
  MakeInternals = false
  MapMode = 5
  Placement = pos=(0,3.6,0) rot=(0,0.707107,0.707107;3.14159rad)
  sketch-geometry (4):
    g0: LineSegment [constr] StartX=167.782 StartY=-53.0314 StartZ=0 EndX=215.42 EndY=-53.0314 EndZ=0
    g1: GeomPoint [constr] X=191.282 Y=-53.0314 Z=0
    g2: Circle CenterX=191.282 CenterY=-53.0314 CenterZ=0 NormalX=0 NormalY=0 NormalZ=1 AngleXU=0 Radius=11.5
    g3: Circle CenterX=191.282 CenterY=-53.0314 CenterZ=0 NormalX=0 NormalY=0 NormalZ=1 AngleXU=0 Radius=10.7
  constraints (9):
    c: Horizontal(g0)
    c: PointOnObject(g0,g-3)
    c: Diameter(g2) = 23
    c: Coincident(g2,g1)
    c: Diameter(g3) = 21.4
    c: Coincident(g3,g1)
    c: DistanceX(g0,g1) = 23.5
    c: PointOnObject(g1,g0)
    c: Coincident(g0,g-4)
FEATURE [PartDesign::Chamfer] Chamfer016
  Angle = 45
  Base = -> SubtractiveLoft001 [Edge118,Edge117,Edge119,Edge120,Edge109]
  BaseFeature = -> SubtractiveLoft001
  ChamferType = 0
  FlipDirection = false
  Refine = true
  Size = 1.5
  Size2 = 1
  SupportTransform = false
  Suppressed = false
  UseAllEdges = false
FEATURE [PartDesign::Chamfer] Chamfer017
  Angle = 45
  Base = -> Chamfer016 [Edge15]
  BaseFeature = -> Chamfer016
  ChamferType = 0
  FlipDirection = false
  Refine = true
  Size = 1.6
  Size2 = 1
  SupportTransform = false
  Suppressed = false
  UseAllEdges = false
FEATURE [PartDesign::Chamfer] Chamfer018
  Angle = 45
  Base = -> Chamfer017 [Edge10]
  BaseFeature = -> Chamfer017
  ChamferType = 0
  FlipDirection = false
  Refine = true
  Size = 3.5
  Size2 = 1
  SupportTransform = false
  Suppressed = false
  UseAllEdges = false
FEATURE [PartDesign::Chamfer] Chamfer019
  Angle = 45
  Base = -> Chamfer018 [Edge94]
  BaseFeature = -> Chamfer018
  ChamferType = 0
  FlipDirection = false
  Refine = true
  Size = 1.9
  Size2 = 1
  SupportTransform = false
  Suppressed = false
  UseAllEdges = false
FEATURE [PartDesign::Fillet] Fillet009
  Base = -> Chamfer019 [Edge83]
  BaseFeature = -> Chamfer019
  Radius = 1.1
  Refine = true
  SupportTransform = false
  Suppressed = false
  UseAllEdges = false
FEATURE [PartDesign::Fillet] Fillet010
  Base = -> Fillet009 [Edge77]
  BaseFeature = -> Fillet009
  Radius = 1.9
  Refine = true
  SupportTransform = false
  Suppressed = false
  UseAllEdges = false
FEATURE [PartDesign::Pocket] Pocket005
  BaseFeature = -> Fillet010
  Direction = (0,-1,2e-16)
  Length = 0.8
  Length2 = 5
  Profile = -> Sketch112
  ReferenceAxis = -> Sketch112 [N_Axis]
  Refine = true
  Suppressed = false
  Type = 0
FEATURE [Part::Part2DObjectPython] ShapeString001  # Draft 2D object (typed FeaturePython)
  FontFile = <path>
  Fuse = false
  Justification = 6
  JustificationReference = 0
  KeepLeftMargin = false
  MakeFace = true
  ObliqueAngle = 0
  Placement = pos=(-183.5,3.6,-57.5) rot=(0,0.707107,0.707107;3.14159rad)
  ScaleToSize = true
  Size = 10
  String = AS
  Tracking = 0
FEATURE [PartDesign::Pocket] Pocket013
  BaseFeature = -> Pocket005
  Direction = (-1e-16,-1,2e-16)
  Length = 1
  Length2 = 5
  Profile = -> ShapeString001
  ReferenceAxis = -> ShapeString001 [N_Axis]
  Refine = true
  Suppressed = false
  Type = 0
FEATURE [PartDesign::Pad] Pad020
  Direction = (0,-1,2e-16)
  Length = 25.2
  Length2 = 10
  Midplane = true
  Placement = pos=(0,0,0) rot=(1,0,0;1.5708rad)
  Profile = -> Sketch021
  ReferenceAxis = -> Sketch021 [N_Axis]
  Refine = true
  Suppressed = false
  Type = 0
FEATURE [PartDesign::Body] Body001  label="perno fermo rumble e driver solenoide"
  AllowCompound = false
  Group = -> [Sketch021,Pad020]
  Origin = -> Origin001
  Tip = -> Pad020
FEATURE [PartDesign::Pad] Pad021
  Direction = (0,-1,2e-16)
  Length = 16.8
  Length2 = 10
  Midplane = true
  Placement = pos=(0,0,0) rot=(1,0,0;1.5708rad)
  Profile = -> Sketch061
  ReferenceAxis = -> Sketch061 [N_Axis]
  Refine = true
  Suppressed = false
  Type = 0
FEATURE [PartDesign::Pocket] Pocket014
  BaseFeature = -> Pad021
  Direction = (0,1,-2e-16)
  Length = 12.8
  Length2 = 5
  Midplane = true
  Placement = pos=(0,0,0) rot=(1,0,0;1.5708rad)
  Profile = -> Sketch062
  ReferenceAxis = -> Sketch062 [N_Axis]
  Refine = true
  Suppressed = false
  Type = 0
FEATURE [PartDesign::Pad] Pad022
  BaseFeature = -> Pocket014
  Direction = (0,-1,2e-16)
  Length = 7.6
  Length2 = 10
  Midplane = true
  Placement = pos=(0,0,0) rot=(1,0,0;1.5708rad)
  Profile = -> Sketch063
  ReferenceAxis = -> Sketch063 [N_Axis]
  Refine = true
  Suppressed = false
  Type = 0
FEATURE [PartDesign::Body] Body003  label="blocco switch"
  AllowCompound = false
  Group = -> [Sketch061,Sketch062,Sketch063,Pad021,Pocket014,Pad022]
  Origin = -> Origin003
  Tip = -> Pad022
FEATURE [PartDesign::Pad] Pad024
  Direction = (0,-1,2e-16)
  Length = 17
  Length2 = 10
  Midplane = true
  Placement = pos=(0,0,0) rot=(1,0,0;1.5708rad)
  Profile = -> Sketch045
  ReferenceAxis = -> Sketch045 [N_Axis]
  Refine = true
  Suppressed = false
  Type = 0
FEATURE [PartDesign::Pocket] Pocket015
  BaseFeature = -> Pad024
  Direction = (-1,0,0)
  Length = 8
  Length2 = 5
  Placement = pos=(0,0,0) rot=(1,0,0;1.5708rad)
  Profile = -> Sketch047
  ReferenceAxis = -> Sketch047 [N_Axis]
  Refine = true
  Reversed = true
  Suppressed = false
  Type = 0
FEATURE [PartDesign::Pocket] Pocket016
  BaseFeature = -> Pocket015
  Direction = (-1,0,0)
  Length = 1
  Length2 = 5
  Placement = pos=(0,0,0) rot=(1,0,0;1.5708rad)
  Profile = -> Sketch046
  ReferenceAxis = -> Sketch046 [N_Axis]
  Refine = true
  Reversed = true
  Suppressed = false
  Type = 0
FEATURE [PartDesign::Pocket] Pocket017
  BaseFeature = -> Pocket016
  Direction = (0,1,-2e-16)
  Length = 17
  Length2 = 5
  Midplane = true
  Placement = pos=(0,0,0) rot=(1,0,0;1.5708rad)
  Profile = -> Sketch048
  ReferenceAxis = -> Sketch048 [N_Axis]
  Refine = true
  Suppressed = false
  Type = 0
FEATURE [PartDesign::Pad] Pad025
  BaseFeature = -> Pocket017
  Direction = (0,-1,2e-16)
  Length = 17
  Length2 = 10
  Midplane = true
  Placement = pos=(0,0,0) rot=(1,0,0;1.5708rad)
  Profile = -> Sketch049
  ReferenceAxis = -> Sketch049 [N_Axis]
  Refine = true
  Suppressed = false
  Type = 0
FEATURE [PartDesign::Pad] Pad026
  BaseFeature = -> Pad025
  Direction = (0,-1,2e-16)
  Length = 17
  Length2 = 10
  Midplane = true
  Placement = pos=(0,0,0) rot=(1,0,0;1.5708rad)
  Profile = -> Sketch066
  ReferenceAxis = -> Sketch066 [N_Axis]
  Refine = true
  Suppressed = false
  Type = 0
FEATURE [PartDesign::Pad] Pad027
  BaseFeature = -> Pad026
  Direction = (0,-1,2e-16)
  Length = 5
  Length2 = 10
  Midplane = true
  Placement = pos=(0,0,0) rot=(1,0,0;1.5708rad)
  Profile = -> Sketch064
  ReferenceAxis = -> Sketch064 [N_Axis]
  Refine = true
  Suppressed = false
  Type = 0
FEATURE [PartDesign::Pad] Pad028
  BaseFeature = -> Pad027
  Direction = (1,0,0)
  Length = 1
  Length2 = 10
  Placement = pos=(0,0,0) rot=(1,0,0;1.5708rad)
  Profile = -> Sketch068
  ReferenceAxis = -> Sketch068 [N_Axis]
  Refine = true
  Reversed = true
  Suppressed = false
  Type = 0
FEATURE [PartDesign::Chamfer] Chamfer020
  Angle = 45
  Base = -> Pad028 [Edge73,Edge75,Edge78,Edge77]
  BaseFeature = -> Pad028
  ChamferType = 0
  FlipDirection = false
  Placement = pos=(0,0,0) rot=(1,0,0;1.5708rad)
  Refine = true
  Size = 0.5
  Size2 = 1
  SupportTransform = false
  Suppressed = false
  UseAllEdges = false
FEATURE [PartDesign::Body] Body002  label="supporto per neopixel"
  AllowCompound = false
  Group = -> [Sketch045,Sketch047,Sketch046,Sketch048,Sketch049,Sketch066,Sketch064,Sketch068,Pad024,Pocket015,Pocket016,Pocket017,Pad025,Pad026,Pad027,Pad028,Chamfer020]
  Origin = -> Origin002
  Tip = -> Chamfer020
FEATURE [Sketcher::SketchObject] Sketch134  label="perno fermo rumble002"
  ArcFitTolerance = 1e-06
  AttachmentSupport = -> [XZ_Plane008]
  FullyConstrained = true
  MakeInternals = false
  MapMode = 5
  Placement = pos=(0,0,0) rot=(1,0,0;1.5708rad)
  sketch-geometry (16):
    g0: LineSegment StartX=0 StartY=0.45 StartZ=0 EndX=0 EndY=1.55 EndZ=0
    g1: LineSegment StartX=0.45 StartY=2 StartZ=0 EndX=1.55 EndY=2 EndZ=0
    g2: LineSegment StartX=2 StartY=1.55 StartZ=0 EndX=2 EndY=0.45 EndZ=0
    g3: LineSegment StartX=1.55 StartY=0 StartZ=0 EndX=0.45 EndY=0 EndZ=0
    g4: ArcOfCircle [constr] CenterX=0.45 CenterY=1.55 CenterZ=0 NormalX=0 NormalY=0 NormalZ=1 AngleXU=0 Radius=0.45 StartAngle=1.5708 EndAngle=3.14159
    g5: GeomPoint [constr] X=0 Y=2 Z=0
    g6: LineSegment StartX=0.45 StartY=2 StartZ=0 EndX=0 EndY=1.55 EndZ=0
    g7: ArcOfCircle [constr] CenterX=1.55 CenterY=1.55 CenterZ=0 NormalX=0 NormalY=0 NormalZ=1 AngleXU=0 Radius=0.45 StartAngle=0 EndAngle=1.5708
    g8: GeomPoint [constr] X=2 Y=2 Z=0
    g9: LineSegment StartX=2 StartY=1.55 StartZ=0 EndX=1.55 EndY=2 EndZ=0
    g10: ArcOfCircle [constr] CenterX=1.55 CenterY=0.45 CenterZ=0 NormalX=0 NormalY=0 NormalZ=1 AngleXU=0 Radius=0.45 StartAngle=4.71239 EndAngle=6.28319
    g11: GeomPoint [constr] X=2 Y=0 Z=0
    g12: LineSegment StartX=1.55 StartY=0 StartZ=0 EndX=2 EndY=0.45 EndZ=0
    g13: ArcOfCircle [constr] CenterX=0.45 CenterY=0.45 CenterZ=0 NormalX=0 NormalY=0 NormalZ=1 AngleXU=0 Radius=0.45 StartAngle=3.14159 EndAngle=4.71239
    g14: GeomPoint [constr] X=0 Y=0 Z=0
    g15: LineSegment StartX=0 StartY=0.45 StartZ=0 EndX=0.45 EndY=0 EndZ=0
  constraints (35):
    c: Coincident(g14,g-1)
    c: PointOnObject(g5,g-2)
    c: Horizontal(g1)
    c: Vertical(g2)
    c: Horizontal(g3)
    c: DistanceX(g5,g8) = 2
    c: DistanceY(g11,g8) = 2
    c: PointOnObject(g5,g0)
    c: PointOnObject(g5,g1)
    c: Tangent(g0,g4) = 1.5708
    c: Tangent(g1,g4) = 1.5708
    c: Coincident(g6,g0)
    c: Coincident(g6,g1)
    c: PointOnObject(g8,g2)
    c: PointOnObject(g8,g1)
    c: Tangent(g2,g7) = 1.5708
    c: Tangent(g1,g7) = 1.5708
    c: Coincident(g9,g2)
    c: Coincident(g9,g1)
    c: PointOnObject(g11,g2)
    c: PointOnObject(g11,g3)
    c: Tangent(g2,g10) = 1.5708
    c: Tangent(g3,g10) = 1.5708
    c: Coincident(g12,g2)
    c: Coincident(g12,g3)
    c: PointOnObject(g14,g0)
    c: PointOnObject(g14,g3)
    c: Tangent(g0,g13) = 1.5708
    c: Tangent(g3,g13) = 1.5708
    c: Coincident(g15,g0)
    c: Coincident(g15,g3)
    c: Equal(g6,g9)
    c: Equal(g9,g12)
    c: Equal(g12,g15)
    c: DistanceX(g14,g3) = 0.45
FEATURE [PartDesign::Pad] Pad029
  Direction = (0,-1,2e-16)
  Length = 17
  Length2 = 10
  Midplane = true
  Placement = pos=(0,0,0) rot=(1,0,0;1.5708rad)
  Profile = -> Sketch134
  ReferenceAxis = -> Sketch134 [N_Axis]
  Refine = true
  Suppressed = false
  Type = 0
FEATURE [PartDesign::Body] Body008  label="perno fermo neopixel"
  AllowCompound = false
  Group = -> [Sketch134,Pad029]
  Origin = -> Origin008
  Tip = -> Pad029
FEATURE [Sketcher::SketchObject] Sketch135  label="perno fermo rumble003"
  ArcFitTolerance = 1e-06
  AttachmentSupport = -> [XZ_Plane009]
  FullyConstrained = true
  MakeInternals = false
  MapMode = 5
  Placement = pos=(0,0,0) rot=(1,0,0;1.5708rad)
  sketch-geometry (16):
    g0: LineSegment StartX=4.69e-14 StartY=0.8 StartZ=0 EndX=-3.04e-14 EndY=3.1 EndZ=0
    g1: LineSegment StartX=0.8 StartY=3.9 StartZ=0 EndX=3.1 EndY=3.9 EndZ=0
    g2: LineSegment StartX=3.9 StartY=3.1 StartZ=0 EndX=3.9 EndY=0.8 EndZ=0
    g3: LineSegment StartX=3.1 StartY=0 StartZ=0 EndX=0.8 EndY=0 EndZ=0
    g4: ArcOfCircle [constr] CenterX=0.8 CenterY=3.1 CenterZ=0 NormalX=0 NormalY=0 NormalZ=1 AngleXU=0 Radius=0.8 StartAngle=1.5708 EndAngle=3.14159
    g5: GeomPoint [constr] X=0 Y=3.9 Z=0
    g6: LineSegment StartX=0.8 StartY=3.9 StartZ=0 EndX=-3.04e-14 EndY=3.1 EndZ=0
    g7: ArcOfCircle [constr] CenterX=3.1 CenterY=3.1 CenterZ=0 NormalX=0 NormalY=0 NormalZ=1 AngleXU=0 Radius=0.8 StartAngle=-2.4e-14 EndAngle=1.5708
    g8: GeomPoint [constr] X=3.9 Y=3.9 Z=0
    g9: LineSegment StartX=3.9 StartY=3.1 StartZ=0 EndX=3.1 EndY=3.9 EndZ=0
    g10: ArcOfCircle [constr] CenterX=3.1 CenterY=0.8 CenterZ=0 NormalX=0 NormalY=0 NormalZ=1 AngleXU=0 Radius=0.8 StartAngle=4.71239 EndAngle=6.28319
    g11: GeomPoint [constr] X=3.9 Y=0 Z=0
    g12: LineSegment StartX=3.1 StartY=0 StartZ=0 EndX=3.9 EndY=0.8 EndZ=0
    g13: ArcOfCircle [constr] CenterX=0.8 CenterY=0.8 CenterZ=0 NormalX=0 NormalY=0 NormalZ=1 AngleXU=0 Radius=0.8 StartAngle=3.14159 EndAngle=4.71239
    g14: GeomPoint [constr] X=0 Y=0 Z=0
    g15: LineSegment StartX=4.69e-14 StartY=0.8 StartZ=0 EndX=0.8 EndY=0 EndZ=0
  constraints (35):
    c: Coincident(g14,g-1)
    c: PointOnObject(g5,g-2)
    c: Horizontal(g1)
    c: Vertical(g2)
    c: Horizontal(g3)
    c: DistanceX(g5,g8) = 3.9
    c: DistanceY(g11,g8) = 3.9
    c: PointOnObject(g5,g0)
    c: PointOnObject(g5,g1)
    c: Tangent(g0,g4) = 1.5708
    c: Tangent(g1,g4) = 1.5708
    c: Coincident(g6,g0)
    c: Coincident(g6,g1)
    c: PointOnObject(g8,g2)
    c: PointOnObject(g8,g1)
    c: Tangent(g2,g7) = 1.5708
    c: Tangent(g1,g7) = 1.5708
    c: Coincident(g9,g2)
    c: Coincident(g9,g1)
    c: PointOnObject(g11,g2)
    c: PointOnObject(g11,g3)
    c: Tangent(g2,g10) = 1.5708
    c: Tangent(g3,g10) = 1.5708
    c: Coincident(g12,g2)
    c: Coincident(g12,g3)
    c: PointOnObject(g14,g0)
    c: PointOnObject(g14,g3)
    c: Tangent(g0,g13) = 1.5708
    c: Tangent(g3,g13) = 1.5708
    c: Coincident(g15,g0)
    c: Coincident(g15,g3)
    c: Equal(g6,g9)
    c: Equal(g9,g12)
    c: Equal(g12,g15)
    c: DistanceX(g14,g3) = 0.8
FEATURE [PartDesign::Pad] Pad030
  Direction = (0,-1,2e-16)
  Length = 25.2
  Length2 = 10
  Midplane = true
  Placement = pos=(0,0,0) rot=(1,0,0;1.5708rad)
  Profile = -> Sketch135
  ReferenceAxis = -> Sketch135 [N_Axis]
  Refine = true
  Suppressed = false
  Type = 0
FEATURE [PartDesign::Body] Body009  label="perno fermo switch - caricabatterie - grilletto"
  AllowCompound = false
  Group = -> [Sketch135,Pad030]
  Origin = -> Origin009
  Tip = -> Pad030
FEATURE [Sketcher::SketchObject] Sketch136  label="scavo_rele"
  ArcFitTolerance = 1e-06
  AttachmentSupport = -> [XZ_Plane]
  ExternalGeometry = -> [Sketch]
  FullyConstrained = true
  MakeInternals = false
  MapMode = 5
  Placement = pos=(0,0,0) rot=(1,0,0;1.5708rad)
  sketch-geometry (7):
    g0: LineSegment [constr] StartX=-173.013 StartY=-62.644 StartZ=0 EndX=-176.535 EndY=-73.4861 EndZ=0
    g1: LineSegment [constr] StartX=-173.013 StartY=-62.644 StartZ=0 EndX=-170.35 EndY=-63.5093 EndZ=0
    g2: LineSegment [constr] StartX=-173.013 StartY=-62.644 StartZ=0 EndX=-176.627 EndY=-61.4698 EndZ=0
    g3: LineSegment StartX=-176.627 StartY=-61.4698 StartZ=0 EndX=-170.35 EndY=-63.5093 EndZ=0
    g4: LineSegment StartX=-176.627 StartY=-61.4698 StartZ=0 EndX=-180.149 EndY=-72.3118 EndZ=0
    g5: LineSegment StartX=-170.35 StartY=-63.5093 StartZ=0 EndX=-173.872 EndY=-74.3513 EndZ=0
    g6: LineSegment StartX=-180.149 StartY=-72.3118 StartZ=0 EndX=-173.872 EndY=-74.3513 EndZ=0
  constraints (19):
    c: Tangent(g0,g-3)
    c: Distance(g0,g-3) = 89
    c: Distance(g0,g0) = 11.4
    c: Coincident(g1,g0)
    c: Coincident(g2,g0)
    c: Distance(g2) = 3.8
    c: Distance(g1) = 2.8
    c: Perpendicular(g0,g1)
    c: Perpendicular(g0,g2)
    c: Coincident(g3,g2)
    c: Coincident(g3,g1)
    c: Equal(g4,g0)
    c: Equal(g5,g0)
    c: Parallel(g4,g0)
    c: Parallel(g5,g0)
    c: Coincident(g4,g2)
    c: Coincident(g5,g1)
    c: Coincident(g6,g4)
    c: Coincident(g6,g5)
FEATURE [Part::Extrusion] Extrude076  label="Extrude076 - scavo_rele"
  Base = -> Sketch136
  Dir = (0,-1,2e-16)
  DirMode = 2
  FaceMakerClass = Part::FaceMakerBullseye
  FaceMakerMode = 3
  LengthFwd = 17.8
  LengthRev = 0
  Solid = true
  Symmetric = true
FEATURE [Sketcher::SketchObject] Sketch137  label="scavo_nuovo_driver"
  ArcFitTolerance = 1e-06
  AttachmentSupport = -> [XZ_Plane]
  ExternalGeometry = -> [Sketch]
  FullyConstrained = true
  MakeInternals = false
  MapMode = 5
  Placement = pos=(0,0,0) rot=(1,0,0;1.5708rad)
  sketch-geometry (7):
    g0: LineSegment [constr] StartX=-160.157 StartY=-23.0801 StartZ=0 EndX=-164.978 EndY=-37.9166 EndZ=0
    g1: LineSegment [constr] StartX=-160.157 StartY=-23.0801 StartZ=0 EndX=-157.114 EndY=-24.0689 EndZ=0
    g2: LineSegment [constr] StartX=-160.157 StartY=-23.0801 StartZ=0 EndX=-163.771 EndY=-21.9058 EndZ=0
    g3: LineSegment StartX=-163.771 StartY=-21.9058 StartZ=0 EndX=-157.114 EndY=-24.0689 EndZ=0
    g4: LineSegment StartX=-163.771 StartY=-21.9058 StartZ=0 EndX=-168.592 EndY=-36.7423 EndZ=0
    g5: LineSegment StartX=-157.114 StartY=-24.0689 StartZ=0 EndX=-161.935 EndY=-38.9054 EndZ=0
    g6: LineSegment StartX=-168.592 StartY=-36.7423 StartZ=0 EndX=-161.935 EndY=-38.9054 EndZ=0
  constraints (19):
    c: Distance(g0,g-3) = 47.4
    c: Distance(g0) = 15.6
    c: Tangent(g0,g-3)
    c: Coincident(g1,g0)
    c: Coincident(g2,g0)
    c: Distance(g1) = 3.2
    c: Distance(g2) = 3.8
    c: Perpendicular(g0,g1)
    c: Perpendicular(g0,g2)
    c: Coincident(g3,g2)
    c: Coincident(g3,g1)
    c: Equal(g4,g0)
    c: Equal(g5,g0)
    c: Parallel(g4,g0)
    c: Parallel(g5,g0)
    c: Coincident(g4,g2)
    c: Coincident(g5,g1)
    c: Coincident(g6,g4)
    c: Coincident(g6,g5)
FEATURE [Part::Extrusion] Extrude077  label="Extrude077 - scavo_nuovo_driver"
  Base = -> Sketch137
  Dir = (0,-1,2e-16)
  DirMode = 2
  FaceMakerClass = Part::FaceMakerBullseye
  FaceMakerMode = 3
  LengthFwd = 20.8
  LengthRev = 0
  Solid = true
  Symmetric = true
FEATURE [Sketcher::SketchObject] Sketch138  label="scavo_nuovo_driver_alto"
  ArcFitTolerance = 1e-06
  AttachmentSupport = -> [XZ_Plane]
  ExternalGeometry = -> [Sketch]
  FullyConstrained = true
  MakeInternals = false
  MapMode = 5
  Placement = pos=(0,0,0) rot=(1,0,0;1.5708rad)
  sketch-geometry (7):
    g0: LineSegment [constr] StartX=-188.796 StartY=17.7274 StartZ=0 EndX=-187.75 EndY=4.97025 EndZ=0
    g1: LineSegment StartX=-187.75 StartY=4.97025 StartZ=0 EndX=-189.743 EndY=4.8067 EndZ=0
    g2: LineSegment StartX=-187.75 StartY=4.97025 StartZ=0 EndX=-182.766 EndY=5.37913 EndZ=0
    g3: LineSegment StartX=-190.79 StartY=17.5638 StartZ=0 EndX=-189.743 EndY=4.8067 EndZ=0
    g4: LineSegment StartX=-183.813 StartY=18.1363 StartZ=0 EndX=-182.766 EndY=5.37913 EndZ=0
    g5: LineSegment StartX=-190.79 StartY=17.5638 StartZ=0 EndX=-188.796 EndY=17.7274 EndZ=0
    g6: LineSegment StartX=-188.796 StartY=17.7274 StartZ=0 EndX=-183.813 EndY=18.1363 EndZ=0
  constraints (20):
    c: Distance(g0) = 12.8
    c: DistanceY(g-3,g0) = 9
    c: PointOnObject(g0,g-4)
    c: PointOnObject(g0,g-4)
    c: Coincident(g1,g0)
    c: Coincident(g2,g0)
    c: Distance(g1) = 2
    c: Distance(g2) = 5
    c: Perpendicular(g0,g1)
    c: Perpendicular(g0,g2)
    c: Equal(g3,g0)
    c: Parallel(g3,g0)
    c: Coincident(g3,g1)
    c: Equal(g4,g0)
    c: Parallel(g4,g0)
    c: Coincident(g4,g2)
    c: Coincident(g5,g3)
    c: Coincident(g5,g0)
    c: Coincident(g6,g0)
    c: Coincident(g6,g4)
FEATURE [Part::Extrusion] Extrude078  label="Extrude078 - scavo_nuovo_driver_alto"
  Base = -> Sketch138
  Dir = (0,-1,2e-16)
  DirMode = 2
  FaceMakerClass = Part::FaceMakerBullseye
  FaceMakerMode = 3
  LengthFwd = 16.6
  LengthRev = 0
  Solid = true
  Symmetric = true
FEATURE [Sketcher::SketchObject] Sketch139  label="fermi_nuovo_driver_alto"
  ArcFitTolerance = 1e-06
  AttachmentSupport = -> [XZ_Plane]
  ExternalGeometry = -> [Sketch138,Sketch]
  FullyConstrained = true
  MakeInternals = false
  MapMode = 5
  Placement = pos=(0,0,0) rot=(1,0,0;1.5708rad)
  sketch-geometry (17):
    g0: LineSegment [constr] StartX=-188.314 StartY=16.4295 StartZ=0 EndX=-187.885 EndY=13.7638 EndZ=0
    g1: LineSegment [constr] StartX=-187.885 StartY=13.7638 StartZ=0 EndX=-187.456 EndY=11.0981 EndZ=0
    g2: LineSegment StartX=-187.885 StartY=13.7638 StartZ=0 EndX=-187.71 EndY=12.6778 EndZ=0
    g3: LineSegment StartX=-187.885 StartY=13.7638 StartZ=0 EndX=-188.06 EndY=14.8499 EndZ=0
    g4: LineSegment StartX=-187.71 StartY=12.6778 StartZ=0 EndX=-185.538 EndY=13.0274 EndZ=0
    g5: LineSegment StartX=-188.06 StartY=14.8499 StartZ=0 EndX=-185.888 EndY=15.1994 EndZ=0
    g6: LineSegment StartX=-185.888 StartY=15.1994 StartZ=0 EndX=-185.538 EndY=13.0274 EndZ=0
    g7: LineSegment StartX=-187.456 StartY=11.0981 StartZ=0 EndX=-189.035 EndY=10.8439 EndZ=0
    g8: LineSegment StartX=-188.314 StartY=16.4295 StartZ=0 EndX=-189.893 EndY=16.1753 EndZ=0
    g9: LineSegment StartX=-189.893 StartY=16.1753 StartZ=0 EndX=-189.035 EndY=10.8439 EndZ=0
    g10: LineSegment StartX=-187.456 StartY=11.0981 StartZ=0 EndX=-185.284 EndY=11.4477 EndZ=0
    g11: LineSegment StartX=-188.314 StartY=16.4295 StartZ=0 EndX=-186.142 EndY=16.7791 EndZ=0
    g12: LineSegment StartX=-184.308 StartY=15.4537 StartZ=0 EndX=-183.958 EndY=13.2816 EndZ=0
    g13: ArcOfCircle CenterX=-185.888 CenterY=15.1994 CenterZ=0 NormalX=0 NormalY=0 NormalZ=1 AngleXU=0 Radius=1.6 StartAngle=0.15957 EndAngle=1.73037
    g14: GeomPoint [constr] X=-184.562 Y=17.0333 Z=0
    g15: ArcOfCircle CenterX=-185.538 CenterY=13.0274 CenterZ=0 NormalX=0 NormalY=0 NormalZ=1 AngleXU=0 Radius=1.6 StartAngle=4.87196 EndAngle=6.44276
    g16: GeomPoint [constr] X=-183.704 Y=11.7019 Z=0
  constraints (43):
    c: Tangent(g1,g0) = -1.5708
    c: Distance(g0) = 2.7
    c: Equal(g1,g0)
    c: Tangent(g1,g-5)
    c: Coincident(g2,g0)
    c: Coincident(g3,g0)
    c: Distance(g2) = 1.1
    c: Equal(g3,g2)
    c: PointOnObject(g3,g2)
    c: Coincident(g4,g2)
    c: Coincident(g5,g3)
    c: Distance(g4) = 2.2
    c: Equal(g4,g5)
    c: Perpendicular(g1,g4)
    c: Perpendicular(g0,g5)
    c: Coincident(g6,g5)
    c: Coincident(g6,g4)
    c: Coincident(g7,g1)
    c: Coincident(g8,g0)
    c: Distance(g7) = 1.6
    c: Equal(g7,g8)
    c: Perpendicular(g1,g7)
    c: Perpendicular(g8,g0)
    c: Coincident(g9,g8)
    c: Coincident(g9,g7)
    c: Coincident(g10,g1)
    c: Coincident(g11,g0)
    c: Distance(g10,g16) = 3.8
    c: Perpendicular(g1,g10)
    c: Perpendicular(g1,g11)
    c: DistanceY(g0,g-4) = 3.8
    c: PointOnObject(g14,g12)
    c: PointOnObject(g14,g11)
    c: Tangent(g12,g13) = 1.5708
    c: Tangent(g11,g13) = 1.5708
    c: PointOnObject(g16,g12)
    c: PointOnObject(g16,g10)
    c: Tangent(g12,g15) = 1.5708
    c: Tangent(g10,g15) = -1.5708
    c: Equal(g13,g15)
    c: Coincident(g13,g5)
    c: Parallel(g2,g0)
    c: PointOnObject(g0,g-5)
FEATURE [Part::Extrusion] Extrude079  label="Extrude079 - fermi_nuovo_driver_alto"
  Base = -> Sketch139
  Dir = (0,-1,2e-16)
  DirMode = 2
  FaceMakerClass = Part::FaceMakerBullseye
  FaceMakerMode = 3
  LengthFwd = 25.2
  LengthRev = 0
  Solid = true
  Symmetric = true
FEATURE [Sketcher::SketchObject] Sketch140  label="scavo_diodo_nuovo_driver_alto"
  ArcFitTolerance = 1e-06
  AttachmentSupport = -> [XZ_Plane]
  ExternalGeometry = -> [Sketch138]
  FullyConstrained = true
  MakeInternals = false
  MapMode = 5
  Placement = pos=(0,0,0) rot=(1,0,0;1.5708rad)
  sketch-geometry (4):
    g0: LineSegment StartX=-190.79 StartY=17.5638 StartZ=0 EndX=-189.743 EndY=4.8067 EndZ=0
    g1: LineSegment StartX=-193.78 StartY=17.3185 StartZ=0 EndX=-192.733 EndY=4.56137 EndZ=0
    g2: LineSegment StartX=-190.79 StartY=17.5638 StartZ=0 EndX=-193.78 EndY=17.3185 EndZ=0
    g3: LineSegment StartX=-192.733 StartY=4.56137 StartZ=0 EndX=-189.743 EndY=4.8067 EndZ=0
  constraints (11):
    c: Equal(g0,g-3)
    c: Parallel(g0,g-3)
    c: Equal(g1,g-3)
    c: Parallel(g1,g-3)
    c: Coincident(g2,g0)
    c: Distance(g2) = 3
    c: Perpendicular(g0,g2)
    c: Coincident(g1,g2)
    c: Coincident(g3,g1)
    c: Coincident(g3,g0)
    c: Coincident(g0,g-3)
FEATURE [Part::Extrusion] Extrude080  label="Extrude080 - scavo_diodo_nuovo_driver_alto"
  Base = -> Sketch140
  Dir = (0,-1,2e-16)
  DirMode = 2
  FaceMakerClass = Part::FaceMakerBullseye
  FaceMakerMode = 3
  LengthFwd = 4
  LengthRev = 0
  Placement = pos=(0,7.8,0) rot=(0,0,1;0rad)
  Solid = true
  Symmetric = false
FEATURE [Part::MultiFuse] Fusion001
  Refine = true
  Shapes = -> [Cut043,Extrude079]
FEATURE [Part::Cut] Cut044
  Base = -> Fusion001
  Refine = true
  Tool = -> Extrude078
FEATURE [Part::Cut] Cut045
  Base = -> Cut044
  Refine = true
  Tool = -> Extrude080
FEATURE [Sketcher::SketchObject] Sketch141  label="fermi_nuovo_driver"
  ArcFitTolerance = 1e-06
  AttachmentSupport = -> [XZ_Plane]
  ExternalGeometry = -> [Sketch,Sketch137]
  FullyConstrained = true
  MakeInternals = false
  MapMode = 5
  Placement = pos=(0,0,0) rot=(1,0,0;1.5708rad)
  sketch-geometry (17):
    g0: LineSegment [constr] StartX=-157.114 StartY=-24.0689 StartZ=0 EndX=-160.157 EndY=-23.0801 EndZ=0
    g1: LineSegment [constr] StartX=-160.157 StartY=-23.0801 StartZ=0 EndX=-162.939 EndY=-31.6396 EndZ=0
    g2: LineSegment [constr] StartX=-162.939 StartY=-31.6396 StartZ=0 EndX=-164.607 EndY=-36.7753 EndZ=0
    g3: LineSegment StartX=-164.607 StartY=-36.7753 StartZ=0 EndX=-166.7 EndY=-36.0955 EndZ=0
    g4: LineSegment StartX=-167.727 StartY=-34.0793 StartZ=0 EndX=-167.047 EndY=-31.987 EndZ=0
    g5: LineSegment StartX=-165.031 StartY=-30.9598 StartZ=0 EndX=-161.417 EndY=-32.134 EndZ=0
    g6: LineSegment StartX=-161.417 StartY=-32.134 StartZ=0 EndX=-163.086 EndY=-37.2697 EndZ=0
    g7: LineSegment StartX=-164.607 StartY=-36.7753 StartZ=0 EndX=-163.086 EndY=-37.2697 EndZ=0
    g8: LineSegment StartX=-165.525 StartY=-32.4814 StartZ=0 EndX=-166.205 EndY=-34.5738 EndZ=0
    g9: LineSegment StartX=-166.205 StartY=-34.5738 StartZ=0 EndX=-164.113 EndY=-35.2536 EndZ=0
    g10: LineSegment StartX=-164.113 StartY=-35.2536 StartZ=0 EndX=-163.433 EndY=-33.1613 EndZ=0
    g11: LineSegment StartX=-163.433 StartY=-33.1613 StartZ=0 EndX=-165.525 EndY=-32.4814 EndZ=0
    g12: ArcOfCircle CenterX=-165.525 CenterY=-32.4814 CenterZ=0 NormalX=0 NormalY=0 NormalZ=1 AngleXU=0 Radius=1.6 StartAngle=1.25664 EndAngle=2.82743
    g13: GeomPoint [constr] X=-166.553 Y=-30.4653 Z=0
    g14: ArcOfCircle CenterX=-166.205 CenterY=-34.5738 CenterZ=0 NormalX=0 NormalY=0 NormalZ=1 AngleXU=0 Radius=1.6 StartAngle=2.82743 EndAngle=4.39823
    g15: GeomPoint [constr] X=-168.221 Y=-35.601 Z=0
    g16: LineSegment [constr] StartX=-160.157 StartY=-23.0801 StartZ=0 EndX=-164.978 EndY=-37.9166 EndZ=0
  constraints (44):
    c: Coincident(g0,g-4)
    c: PointOnObject(g0,g-3)
    c: Parallel(g0,g-4)
    c: Coincident(g1,g0)
    c: Parallel(g1,g-3)
    c: Coincident(g2,g1)
    c: Distance(g2) = 5.4
    c: Coincident(g3,g2)
    c: Parallel(g2,g-3)
    c: Distance(g15,g13) = 5.4
    c: Perpendicular(g3,g2)
    c: Parallel(g4,g2)
    c: Distance(g5,g13) = 5.4
    c: Distance(g3,g15) = 3.8
    c: Perpendicular(g4,g5)
    c: Coincident(g6,g5)
    c: Distance(g6) = 5.4
    c: Parallel(g6,g4)
    c: Coincident(g7,g2)
    c: Coincident(g7,g6)
    c: Coincident(g8,g9)
    c: Coincident(g9,g10)
    c: Coincident(g10,g11)
    c: Coincident(g11,g8)
    c: Distance(g8,g10) = 2.2
    c: Distance(g9,g11) = 2.2
    c: Perpendicular(g11,g8)
    c: Equal(g8,g10)
    c: Equal(g11,g9)
    c: Tangent(g10,g2)
    c: Distance(g10,g1) = 1.6
    c: PointOnObject(g13,g4)
    c: PointOnObject(g13,g5)
    c: Tangent(g4,g12) = 1.5708
    c: Tangent(g5,g12) = 1.5708
    c: PointOnObject(g15,g4)
    c: Tangent(g4,g14) = 1.5708
    c: Tangent(g3,g14) = 1.5708
    c: Equal(g14,g12)
    c: Coincident(g12,g8)
    c: Coincident(g16,g0)
    c: PointOnObject(g16,g-5)
    c: Parallel(g16,g-3)
    c: Distance(g16,g2) = 1.2
FEATURE [Part::Extrusion] Extrude081  label="Extrude081 - fermi_nuovo_driver"
  Base = -> Sketch141
  Dir = (0,-1,2e-16)
  DirMode = 2
  FaceMakerClass = Part::FaceMakerBullseye
  FaceMakerMode = 3
  LengthFwd = 25.2
  LengthRev = 0
  Solid = true
  Symmetric = true
FEATURE [Part::MultiFuse] Fusion002
  Refine = true
  Shapes = -> [Cut045,Extrude081]
FEATURE [Part::Cut] Cut046
  Base = -> Fusion002
  Refine = true
  Tool = -> Extrude077
FEATURE [Sketcher::SketchObject] Sketch142  label="fermi_rele"
  ArcFitTolerance = 1e-06
  AttachmentSupport = -> [XZ_Plane]
  ExternalGeometry = -> [Sketch,Sketch136]
  FullyConstrained = true
  MakeInternals = false
  MapMode = 5
  Placement = pos=(0,0,0) rot=(1,0,0;1.5708rad)
  sketch-geometry (15):
    g0: LineSegment StartX=-178.851 StartY=-68.3174 StartZ=0 EndX=-179.531 EndY=-70.4097 EndZ=0
    g1: LineSegment StartX=-176.835 StartY=-67.2901 StartZ=0 EndX=-173.221 EndY=-68.4644 EndZ=0
    g2: LineSegment StartX=-173.221 StartY=-68.4644 StartZ=0 EndX=-174.89 EndY=-73.6001 EndZ=0
    g3: LineSegment StartX=-178.504 StartY=-72.4258 StartZ=0 EndX=-174.89 EndY=-73.6001 EndZ=0
    g4: LineSegment StartX=-177.33 StartY=-68.8118 StartZ=0 EndX=-175.237 EndY=-69.4916 EndZ=0
    g5: LineSegment StartX=-177.33 StartY=-68.8118 StartZ=0 EndX=-178.01 EndY=-70.9041 EndZ=0
    g6: LineSegment StartX=-175.237 StartY=-69.4916 StartZ=0 EndX=-175.917 EndY=-71.584 EndZ=0
    g7: LineSegment StartX=-178.01 StartY=-70.9041 StartZ=0 EndX=-175.917 EndY=-71.584 EndZ=0
    g8: LineSegment [constr] StartX=-175.237 StartY=-69.4916 StartZ=0 EndX=-174.743 EndY=-67.9699 EndZ=0
    g9: LineSegment [constr] StartX=-175.237 StartY=-69.4916 StartZ=0 EndX=-173.716 EndY=-69.9861 EndZ=0
    g10: LineSegment [constr] StartX=-170.35 StartY=-63.5093 StartZ=0 EndX=-173.013 EndY=-62.644 EndZ=0
    g11: ArcOfCircle CenterX=-177.33 CenterY=-68.8118 CenterZ=0 NormalX=0 NormalY=0 NormalZ=1 AngleXU=0 Radius=1.6 StartAngle=1.25664 EndAngle=2.82743
    g12: GeomPoint [constr] X=-178.357 Y=-66.7957 Z=0
    g13: ArcOfCircle CenterX=-178.01 CenterY=-70.9041 CenterZ=0 NormalX=0 NormalY=0 NormalZ=1 AngleXU=0 Radius=1.6 StartAngle=2.82743 EndAngle=4.39823
    g14: GeomPoint [constr] X=-180.026 Y=-71.9314 Z=0
  constraints (39):
    c: Distance(g14,g12) = 5.4
    c: Distance(g1,g12) = 5.4
    c: Perpendicular(g1,g0)
    c: Coincident(g2,g1)
    c: Parallel(g2,g0)
    c: Coincident(g3,g2)
    c: Parallel(g2,g-3)
    c: Coincident(g5,g4)
    c: Distance(g5) = 2.2
    c: Distance(g4) = 2.2
    c: Perpendicular(g4,g5)
    c: Coincident(g6,g4)
    c: Equal(g6,g5)
    c: Parallel(g6,g5)
    c: Coincident(g7,g5)
    c: Coincident(g7,g6)
    c: Coincident(g8,g4)
    c: Coincident(g9,g4)
    c: Distance(g8) = 1.6
    c: Distance(g9) = 1.6
    c: Parallel(g8,g6)
    c: Parallel(g9,g4)
    c: PointOnObject(g8,g1)
    c: PointOnObject(g9,g2)
    c: Coincident(g10,g-4)
    c: Parallel(g10,g-4)
    c: PointOnObject(g10,g-3)
    c: Tangent(g6,g-3) = 1.5708
    c: Distance(g4,g10) = 7.2
    c: PointOnObject(g12,g1)
    c: Tangent(g1,g11) = 1.5708
    c: Tangent(g0,g11) = -1.5708
    c: PointOnObject(g14,g3)
    c: PointOnObject(g14,g0)
    c: Tangent(g3,g13) = -1.5708
    c: Tangent(g0,g13) = -1.5708
    c: Equal(g11,g13)
    c: Coincident(g11,g4)
    c: Parallel(g3,g1)
FEATURE [Part::Extrusion] Extrude082  label="Extrude082 - fermi_rele"
  Base = -> Sketch142
  Dir = (0,-1,2e-16)
  DirMode = 2
  FaceMakerClass = Part::FaceMakerBullseye
  FaceMakerMode = 3
  LengthFwd = 25.2
  LengthRev = 0
  Solid = true
  Symmetric = true
FEATURE [Part::MultiFuse] Fusion003
  Refine = true
  Shapes = -> [Cut046,Extrude082]
FEATURE [Part::Cut] Cut047
  Base = -> Fusion003
  Refine = true
  Tool = -> Extrude076
FEATURE [Sketcher::SketchObject] Sketch143  label="foro_passaggio_cavi_led_batteria"
  ArcFitTolerance = 1e-06
  AttachmentSupport = -> [XZ_Plane]
  ExternalGeometry = -> [Sketch,Sketch042,Sketch036]
  FullyConstrained = true
  MakeInternals = false
  MapMode = 5
  Placement = pos=(0,0,0) rot=(1,0,0;1.5708rad)
  sketch-geometry (4):
    g0: LineSegment StartX=-207.775 StartY=-41.3701 StartZ=0 EndX=-213.607 EndY=-53.8767 EndZ=0
    g1: LineSegment StartX=-213.607 StartY=-53.8767 StartZ=0 EndX=-211.843 EndY=-59.5559 EndZ=0
    g2: LineSegment StartX=-207.775 StartY=-41.3701 StartZ=0 EndX=-207.775 EndY=-50.8316 EndZ=0
    g3: LineSegment StartX=-207.775 StartY=-50.8316 StartZ=0 EndX=-211.843 EndY=-59.5559 EndZ=0
  constraints (9):
    c: Coincident(g0,g-3)
    c: PointOnObject(g1,g-6)
    c: Coincident(g1,g0)
    c: Coincident(g2,g0)
    c: Coincident(g2,g-7)
    c: Coincident(g3,g2)
    c: Parallel(g3,g0)
    c: Coincident(g3,g1)
    c: Coincident(g0,g-5)
FEATURE [Part::Extrusion] Extrude083  label="Extrude083 - foro_passaggio_cavi_led_batteria"
  Base = -> Sketch143
  Dir = (0,-1,2e-16)
  DirMode = 2
  FaceMakerClass = Part::FaceMakerBullseye
  FaceMakerMode = 3
  LengthFwd = 6
  LengthRev = 0
  Solid = true
  Symmetric = true
FEATURE [Part::Cut] Cut048
  Base = -> Cut047
  Refine = true
  Tool = -> Extrude083
FEATURE [Sketcher::SketchObject] Sketch144  label="foro_areazione_alimentatore"
  ArcFitTolerance = 1e-06
  AttachmentSupport = -> [XZ_Plane]
  ExternalGeometry = -> [Sketch036]
  FullyConstrained = true
  MakeInternals = false
  MapMode = 5
  Placement = pos=(0,0,0) rot=(1,0,0;1.5708rad)
  sketch-geometry (4):
    g0: LineSegment StartX=-211.843 StartY=-60.3701 StartZ=0 EndX=-207.775 EndY=-60.3701 EndZ=0
    g1: LineSegment StartX=-207.775 StartY=-60.3701 StartZ=0 EndX=-207.775 EndY=-70.3701 EndZ=0
    g2: LineSegment StartX=-211.843 StartY=-60.3701 StartZ=0 EndX=-211.843 EndY=-70.3701 EndZ=0
    g3: LineSegment StartX=-207.775 StartY=-70.3701 StartZ=0 EndX=-211.843 EndY=-70.3701 EndZ=0
  constraints (11):
    c: Horizontal(g0)
    c: Distance(g1) = 10
    c: Coincident(g1,g0)
    c: Tangent(g1,g-3)
    c: PointOnObject(g0,g-4)
    c: Coincident(g2,g0)
    c: PointOnObject(g2,g-4)
    c: Coincident(g3,g1)
    c: Horizontal(g3)
    c: Coincident(g3,g2)
    c: DistanceY(g0,g-3) = 19
FEATURE [Part::Extrusion] Extrude084  label="Extrude084 - foro_areazione_alimentatore"
  Base = -> Sketch144
  Dir = (0,-1,2e-16)
  DirMode = 2
  FaceMakerClass = Part::FaceMakerBullseye
  FaceMakerMode = 3
  LengthFwd = 10
  LengthRev = 0
  Solid = true
  Symmetric = true
FEATURE [Part::Cut] Cut049
  Base = -> Cut048
  Refine = true
  Tool = -> Extrude084
FEATURE [Sketcher::SketchObject] Sketch145  label="foro_per_condesatore"
  ArcFitTolerance = 1e-06
  AttachmentSupport = -> [XZ_Plane]
  ExternalGeometry = -> [Sketch,Sketch139]
  FullyConstrained = true
  MakeInternals = false
  MapMode = 5
  Placement = pos=(0,0,0) rot=(1,0,0;1.5708rad)
  sketch-geometry (1):
    g0: Circle CenterX=-182.345 CenterY=7.02342 CenterZ=0 NormalX=0 NormalY=0 NormalZ=1 AngleXU=0 Radius=5.2
  constraints (3):
    c: Diameter(g0) = 10.4
    c: Tangent(g0,g-3)
    c: Tangent(g0,g-4)
FEATURE [Part::Extrusion] Extrude085  label="Extrude085 - foro_per_condesatore"
  Base = -> Sketch145
  Dir = (0,-1,2e-16)
  DirMode = 2
  FaceMakerClass = Part::FaceMakerBullseye
  FaceMakerMode = 3
  LengthFwd = 25.2
  LengthRev = 0
  Solid = true
  Symmetric = true
FEATURE [Part::Cut] Cut050
  Base = -> Cut049
  Refine = true
  Tool = -> Extrude085
FEATURE [Sketcher::SketchObject] Sketch146  label="scavo_pulsante_6x6_per_led_batteria"
  ArcFitTolerance = 1e-06
  AttachmentSupport = -> [XZ_Plane]
  ExternalGeometry = -> [Sketch016]
  FullyConstrained = true
  MakeInternals = false
  MapMode = 5
  Placement = pos=(0,0,0) rot=(1,0,0;1.5708rad)
  sketch-geometry (5):
    g0: LineSegment StartX=-216.643 StartY=-65.8316 StartZ=0 EndX=-216.643 EndY=-72.8316 EndZ=0
    g1: LineSegment StartX=-216.643 StartY=-72.8316 StartZ=0 EndX=-210.243 EndY=-72.8316 EndZ=0
    g2: LineSegment StartX=-210.243 StartY=-72.8316 StartZ=0 EndX=-210.243 EndY=-65.8316 EndZ=0
    g3: LineSegment StartX=-210.243 StartY=-65.8316 StartZ=0 EndX=-216.643 EndY=-65.8316 EndZ=0
    g4: GeomPoint [constr] X=-213.443 Y=-69.3316 Z=0
  constraints (13):
    c: Coincident(g0,g1)
    c: Coincident(g1,g2)
    c: Coincident(g2,g3)
    c: Coincident(g3,g0)
    c: Vertical(g0)
    c: Vertical(g2)
    c: Horizontal(g1)
    c: Horizontal(g3)
    c: Distance(g0,g2) = 6.4
    c: Distance(g1,g3) = 7
    c: Tangent(g1,g-3)
    c: Symmetric(g0,g2,g4)
    c: Vertical(g-3,g4)
FEATURE [Part::Extrusion] Extrude086  label="Extrude086 - scavo_pulsante_6x6_per_led_batteria"
  Base = -> Sketch146
  Dir = (0,-1,2e-16)
  DirMode = 2
  FaceMakerClass = Part::FaceMakerBullseye
  FaceMakerMode = 3
  LengthFwd = 4
  LengthRev = 0
  Placement = pos=(0,12.6,0) rot=(0,0,1;0rad)
  Solid = true
  Symmetric = false
FEATURE [Sketcher::SketchObject] Sketch147  label="scavo_led_stato_batteria"
  ArcFitTolerance = 1e-06
  AttachmentSupport = -> [XZ_Plane]
  ExternalGeometry = -> [Sketch016]
  FullyConstrained = true
  MakeInternals = false
  MapMode = 5
  Placement = pos=(0,0,0) rot=(1,0,0;1.5708rad)
  sketch-geometry (5):
    g0: LineSegment StartX=-215.843 StartY=-56.2316 StartZ=0 EndX=-215.843 EndY=-65.4316 EndZ=0
    g1: LineSegment StartX=-215.843 StartY=-65.4316 StartZ=0 EndX=-211.043 EndY=-65.4316 EndZ=0
    g2: LineSegment StartX=-211.043 StartY=-65.4316 StartZ=0 EndX=-211.043 EndY=-56.2316 EndZ=0
    g3: LineSegment StartX=-211.043 StartY=-56.2316 StartZ=0 EndX=-215.843 EndY=-56.2316 EndZ=0
    g4: GeomPoint [constr] X=-213.443 Y=-60.8316 Z=0
  constraints (13):
    c: Coincident(g0,g1)
    c: Coincident(g1,g2)
    c: Coincident(g2,g3)
    c: Coincident(g3,g0)
    c: Distance(g0,g2) = 4.8
    c: Distance(g1,g3) = 9.2
    c: Equal(g0,g2)
    c: Equal(g1,g3)
    c: Perpendicular(g3,g0)
    c: DistanceY(g-3,g0) = 11.4
    c: Vertical(g2)
    c: Symmetric(g0,g2,g4)
    c: Vertical(g4,g-3)
FEATURE [Part::Extrusion] Extrude087  label="Extrude087 - scavo_led_stato_batteria"
  Base = -> Sketch147
  Dir = (0,-1,2e-16)
  DirMode = 2
  FaceMakerClass = Part::FaceMakerBullseye
  FaceMakerMode = 3
  LengthFwd = 2.2
  LengthRev = 0
  Placement = pos=(0,12.6,0) rot=(0,0,1;0rad)
  Solid = true
  Symmetric = false
FEATURE [Sketcher::SketchObject] Sketch148
  ArcFitTolerance = 1e-06
  AttachmentSupport = -> [Pad016]
  ExternalGeometry = -> [Pad016]
  FullyConstrained = true
  MakeInternals = false
  MapMode = 5
  Placement = pos=(0,0,-80.4316) rot=(1,0,0;3.14159rad)
  sketch-geometry (8):
    g0: LineSegment StartX=-176.685 StartY=3.6 StartZ=0 EndX=-186.685 EndY=3.6 EndZ=0
    g1: LineSegment StartX=-176.685 StartY=3.6 StartZ=0 EndX=-176.685 EndY=-9e-16 EndZ=0
    g2: LineSegment [constr] StartX=-186.685 StartY=3.6 StartZ=0 EndX=-186.685 EndY=-9e-16 EndZ=0
    g3: ArcOfEllipse CenterX=-186.685 CenterY=-9e-16 CenterZ=0 NormalX=0 NormalY=0 NormalZ=1 MajorRadius=10 MinorRadius=3.6 AngleXU=0 StartAngle=0 EndAngle=1.5708
    g4: LineSegment [constr] StartX=-176.685 StartY=-1e-15 StartZ=0 EndX=-196.685 EndY=-1e-15 EndZ=0
    g5: LineSegment [constr] StartX=-186.685 StartY=3.6 StartZ=0 EndX=-186.685 EndY=-3.6 EndZ=0
    g6: GeomPoint [constr] X=-177.356 Y=-1e-15 Z=0
    g7: GeomPoint [constr] X=-196.015 Y=-1e-15 Z=0
  constraints (13):
    c: Distance(g0) = 10
    c: Coincident(g0,g-5)
    c: PointOnObject(g0,g-3)
    c: Coincident(g1,g0)
    c: Coincident(g1,g-5)
    c: Coincident(g2,g0)
    c: Vertical(g2)
    c: PointOnObject(g2,g-4)
    c: InternalAlignment(g4-g7 -> g3) x4
    c: Coincident(g3,g2)
    c: Coincident(g3,g0)
    c: Coincident(g3,g1)
    c: Horizontal(g4)
FEATURE [PartDesign::SubtractivePipe] SubtractivePipe004
  AuxilleryCurvelinear = true
  AuxillerySpineTangent = false
  BaseFeature = -> Pad016
  Binormal = (0,0,0)
  Mode = 0
  Profile = -> Sketch148
  Refine = true
  Spine = -> Pad016 [Edge253]
  SpineTangent = false
  Suppressed = false
  Transformation = 0
  Transition = 0
FEATURE [Sketcher::SketchObject] Sketch149
  ArcFitTolerance = 1e-06
  AttachmentSupport = -> [Pad016]
  ExternalGeometry = -> [Pad016]
  FullyConstrained = true
  MakeInternals = false
  MapMode = 5
  Placement = pos=(0,0,-80.4316) rot=(1,0,0;3.14159rad)
  sketch-geometry (8):
    g0: LineSegment StartX=-215.932 StartY=3.6 StartZ=0 EndX=-205.932 EndY=3.6 EndZ=0
    g1: LineSegment StartX=-215.932 StartY=3.6 StartZ=0 EndX=-215.932 EndY=-4e-16 EndZ=0
    g2: LineSegment [constr] StartX=-205.932 StartY=3.6 StartZ=0 EndX=-205.932 EndY=-9e-16 EndZ=0
    g3: ArcOfEllipse CenterX=-205.932 CenterY=-1e-15 CenterZ=0 NormalX=0 NormalY=0 NormalZ=1 MajorRadius=10 MinorRadius=3.6 AngleXU=-3.14159 StartAngle=4.71239 EndAngle=6.28319
    g4: LineSegment [constr] StartX=-215.932 StartY=-1e-15 StartZ=0 EndX=-195.932 EndY=-1e-15 EndZ=0
    g5: LineSegment [constr] StartX=-205.932 StartY=-3.6 StartZ=0 EndX=-205.932 EndY=3.6 EndZ=0
    g6: GeomPoint [constr] X=-215.262 Y=-2.1e-15 Z=0
    g7: GeomPoint [constr] X=-196.602 Y=-9e-16 Z=0
  constraints (13):
    c: Distance(g0) = 10
    c: Coincident(g0,g-5)
    c: PointOnObject(g0,g-5)
    c: Coincident(g1,g0)
    c: Coincident(g1,g-4)
    c: Coincident(g2,g0)
    c: Vertical(g2)
    c: PointOnObject(g2,g-3)
    c: InternalAlignment(g4-g7 -> g3) x4
    c: Coincident(g3,g2)
    c: Coincident(g3,g0)
    c: Coincident(g3,g1)
    c: Horizontal(g4)
FEATURE [PartDesign::SubtractivePipe] SubtractivePipe005
  AuxilleryCurvelinear = true
  AuxillerySpineTangent = false
  BaseFeature = -> SubtractivePipe004
  Binormal = (0,0,0)
  Mode = 0
  Profile = -> Sketch149
  Refine = true
  Spine = -> Pad016 [Edge251,Edge256,Edge255]
  SpineTangent = false
  Suppressed = false
  Transformation = 0
  Transition = 0
FEATURE [PartDesign::SubtractiveLoft] SubtractiveLoft002
  BaseFeature = -> SubtractivePipe005
  Closed = false
  Profile = -> Sketch129
  Refine = true
  Ruled = false
  Sections = -> [Sketch130]
  Suppressed = false
FEATURE [PartDesign::SubtractiveLoft] SubtractiveLoft003
  BaseFeature = -> SubtractiveLoft002
  Closed = false
  Profile = -> Clone2D001
  Refine = true
  Ruled = false
  Sections = -> [Sketch131]
  Suppressed = false
FEATURE [PartDesign::Chamfer] Chamfer010
  Angle = 45
  Base = -> SubtractiveLoft003 [Edge203,Edge204,Edge202,Edge201,Edge195]
  BaseFeature = -> SubtractiveLoft003
  ChamferType = 0
  FlipDirection = false
  Refine = true
  Size = 1.5
  Size2 = 1
  SupportTransform = false
  Suppressed = false
  UseAllEdges = false
FEATURE [PartDesign::Chamfer] Chamfer011
  Angle = 45
  Base = -> Chamfer010 [Edge15]
  BaseFeature = -> Chamfer010
  ChamferType = 0
  FlipDirection = false
  Refine = true
  Size = 1.6
  Size2 = 1
  SupportTransform = false
  Suppressed = false
  UseAllEdges = false
FEATURE [PartDesign::Chamfer] Chamfer012
  Angle = 45
  Base = -> Chamfer011 [Edge10]
  BaseFeature = -> Chamfer011
  ChamferType = 0
  FlipDirection = false
  Refine = true
  Size = 3.5
  Size2 = 1
  SupportTransform = false
  Suppressed = false
  UseAllEdges = false
FEATURE [PartDesign::Chamfer] Chamfer013
  Angle = 45
  Base = -> Chamfer012 [Edge94]
  BaseFeature = -> Chamfer012
  ChamferType = 0
  FlipDirection = false
  Refine = true
  Size = 1.9
  Size2 = 1
  SupportTransform = false
  Suppressed = false
  UseAllEdges = false
FEATURE [PartDesign::Fillet] Fillet007
  Base = -> Chamfer013 [Edge83]
  BaseFeature = -> Chamfer013
  Radius = 1.1
  Refine = true
  SupportTransform = false
  Suppressed = false
  UseAllEdges = false
FEATURE [PartDesign::Fillet] Fillet008
  Base = -> Fillet007 [Edge75]
  BaseFeature = -> Fillet007
  Radius = 1.9
  Refine = true
  SupportTransform = false
  Suppressed = false
  UseAllEdges = false
FEATURE [PartDesign::Pocket] Pocket011
  BaseFeature = -> Fillet008
  Direction = (0,1,-2e-16)
  Length = 0.8
  Length2 = 5
  Profile = -> Sketch132
  ReferenceAxis = -> Sketch132 [N_Axis]
  Refine = true
  Suppressed = false
  Type = 0
FEATURE [PartDesign::Pocket] Pocket012
  BaseFeature = -> Pocket011
  Direction = (0,1,0)
  Length = 1
  Length2 = 5
  Profile = -> ShapeString
  ReferenceAxis = -> ShapeString [N_Axis]
  Refine = true
  Suppressed = false
  Type = 0
FEATURE [Sketcher::SketchObject] Sketch150
  ArcFitTolerance = 1e-06
  AttachmentSupport = -> [Pad008]
  ExternalGeometry = -> [Pad008]
  FullyConstrained = true
  MakeInternals = false
  MapMode = 5
  Placement = pos=(0,3.6,0) rot=(0,0.707107,0.707107;3.14159rad)
  sketch-geometry (7):
    g0: LineSegment [constr] StartX=210.343 StartY=-66.0316 StartZ=0 EndX=210.343 EndY=-72.8316 EndZ=0
    g1: LineSegment [constr] StartX=210.343 StartY=-72.8316 StartZ=0 EndX=216.543 EndY=-72.8316 EndZ=0
    g2: LineSegment [constr] StartX=216.543 StartY=-72.8316 StartZ=0 EndX=216.543 EndY=-66.0316 EndZ=0
    g3: LineSegment [constr] StartX=216.543 StartY=-66.0316 StartZ=0 EndX=210.343 EndY=-66.0316 EndZ=0
    g4: LineSegment [constr] StartX=210.343 StartY=-72.8316 StartZ=0 EndX=216.543 EndY=-66.0316 EndZ=0
    g5: LineSegment [constr] StartX=210.343 StartY=-66.0316 StartZ=0 EndX=213.443 EndY=-69.4316 EndZ=0
    g6: Circle CenterX=213.443 CenterY=-69.4316 CenterZ=0 NormalX=0 NormalY=0 NormalZ=1 AngleXU=0 Radius=2
  constraints (18):
    c: Coincident(g0,g1)
    c: Coincident(g1,g2)
    c: Coincident(g2,g3)
    c: Coincident(g3,g0)
    c: Vertical(g0)
    c: Vertical(g2)
    c: Horizontal(g1)
    c: Horizontal(g3)
    c: Distance(g0,g2) = 6.2
    c: Distance(g1,g3) = 6.8
    c: DistanceY(g-3,g1) = 4
    c: Coincident(g4,g0)
    c: Coincident(g4,g2)
    c: Coincident(g5,g0)
    c: Symmetric(g0,g2,g5)
    c: Diameter(g6) = 4
    c: Coincident(g6,g5)
    c: Vertical(g5,g-3)
FEATURE [Sketcher::SketchObject] Sketch151
  ArcFitTolerance = 1e-06
  AttachmentSupport = -> [Pad008]
  ExternalGeometry = -> [Pad008]
  FullyConstrained = true
  MakeInternals = false
  MapMode = 5
  Placement = pos=(0,3.6,0) rot=(0,0.707107,0.707107;3.14159rad)
  sketch-geometry (10):
    g0: LineSegment [constr] StartX=211.143 StartY=-56.2316 StartZ=0 EndX=211.143 EndY=-65.4316 EndZ=0
    g1: LineSegment [constr] StartX=211.143 StartY=-65.4316 StartZ=0 EndX=215.743 EndY=-65.4316 EndZ=0
    g2: LineSegment [constr] StartX=215.743 StartY=-65.4316 StartZ=0 EndX=215.743 EndY=-56.2316 EndZ=0
    g3: LineSegment [constr] StartX=215.743 StartY=-56.2316 StartZ=0 EndX=211.143 EndY=-56.2316 EndZ=0
    g4: LineSegment StartX=212.243 StartY=-63.8316 StartZ=0 EndX=214.643 EndY=-63.8316 EndZ=0
    g5: LineSegment StartX=214.643 StartY=-63.8316 StartZ=0 EndX=214.643 EndY=-57.0316 EndZ=0
    g6: LineSegment StartX=214.643 StartY=-57.0316 StartZ=0 EndX=212.243 EndY=-57.0316 EndZ=0
    g7: LineSegment StartX=212.243 StartY=-57.0316 StartZ=0 EndX=212.243 EndY=-63.8316 EndZ=0
    g8: GeomPoint [constr] X=213.443 Y=-60.4316 Z=0
    g9: GeomPoint [constr] X=213.443 Y=-60.8316 Z=0
  constraints (26):
    c: Coincident(g0,g1)
    c: Coincident(g1,g2)
    c: Coincident(g2,g3)
    c: Coincident(g3,g0)
    c: Vertical(g0)
    c: Vertical(g2)
    c: Horizontal(g1)
    c: Horizontal(g3)
    c: Distance(g0,g2) = 4.6
    c: Distance(g1,g3) = 9.2
    c: DistanceY(g-3,g1) = 11.4
    c: Coincident(g4,g5)
    c: Coincident(g5,g6)
    c: Coincident(g6,g7)
    c: Coincident(g7,g4)
    c: Horizontal(g4)
    c: Horizontal(g6)
    c: Vertical(g5)
    c: Vertical(g7)
    c: Symmetric(g6,g4,g8)
    c: Distance(g5,g7) = 2.4
    c: Distance(g4,g6) = 6.8
    c: Symmetric(g2,g0,g9)
    c: Vertical(g8,g9)
    c: DistanceY(g1,g4) = 1.6
    c: Vertical(g9,g-3)
FEATURE [PartDesign::Pocket] Pocket019
  BaseFeature = -> Pocket013
  Direction = (0,-1,2e-16)
  Length = 3.6
  Length2 = 5
  Profile = -> Sketch151
  ReferenceAxis = -> Sketch151 [N_Axis]
  Refine = true
  Suppressed = false
  Type = 0
FEATURE [PartDesign::Pocket] Pocket018
  BaseFeature = -> Pocket019
  Direction = (0,-1,2e-16)
  Length = 3.6
  Length2 = 5
  Profile = -> Sketch150
  ReferenceAxis = -> Sketch150 [N_Axis]
  Refine = true
  Suppressed = false
  Type = 0
FEATURE [PartDesign::Point] DatumPoint
  AttacherType = Attacher::AttachEnginePoint
  AttachmentSupport = -> [Sketch150]
  MapMode = 36
  Placement = pos=(-213.443,3.6,-69.4316) rot=(0,1,0;3.14159rad)
FEATURE [PartDesign::Plane] DatumPlane002
  AttachmentSupport = -> [DatumPoint]
  Length = 260.281
  MapMode = 1
  Placement = pos=(-213.443,3.6,-69.4316) rot=(0,0,1;0rad)
  ResizeMode = 0
  Width = 71.8377
FEATURE [Sketcher::SketchObject] Sketch152
  ArcFitTolerance = 1e-06
  AttachmentSupport = -> [DatumPlane002]
  ExternalGeometry = -> [Sketch150]
  FullyConstrained = true
  MakeInternals = false
  MapMode = 5
  Placement = pos=(-213.443,3.6,-69.4316) rot=(0,0,1;0rad)
  sketch-geometry (7):
    g0: LineSegment StartX=0 StartY=0 StartZ=0 EndX=-4 EndY=5.1e-15 EndZ=0
    g1: ArcOfEllipse CenterX=0 CenterY=0 CenterZ=0 NormalX=0 NormalY=0 NormalZ=1 MajorRadius=4 MinorRadius=3.6 AngleXU=3.14159 StartAngle=2e-16 EndAngle=1.5708
    g2: LineSegment [constr] StartX=-4 StartY=9e-16 StartZ=0 EndX=4 EndY=-9e-16 EndZ=0
    g3: LineSegment [constr] StartX=0 StartY=-3.6 StartZ=0 EndX=0 EndY=3.6 EndZ=0
    g4: GeomPoint [constr] X=-1.74356 Y=2.5e-15 Z=0
    g5: GeomPoint [constr] X=1.74356 Y=-2e-15 Z=0
    g6: LineSegment StartX=0 StartY=0 StartZ=0 EndX=-5.5e-15 EndY=-3.6 EndZ=0
  constraints (11):
    c: PointOnObject(g1,g-2)
    c: Distance(g0) = 4
    c: PointOnObject(g0,g-1)
    c: InternalAlignment(g2-g5 -> g1) x4
    c: Coincident(g1,g0)
    c: Vertical(g3)
    c: Coincident(g1,g-1)
    c: Distance(g6) = 3.6
    c: Coincident(g6,g1)
    c: Coincident(g1,g6)
    c: Coincident(g0,g1)
FEATURE [PartDesign::Groove] Groove
  Angle = 360
  Angle2 = 60
  Axis = (0,1,0)
  Base = (-213.443,3.6,-69.4316)
  BaseFeature = -> Pocket018
  Profile = -> Sketch152
  ReferenceAxis = -> Sketch152 [V_Axis]
  Refine = true
  Reversed = true
  Suppressed = false
  Type = 0
FEATURE [PartDesign::Body] Body006  label="lato SX"
  AllowCompound = false
  Group = -> [Binder,Pad019,Chamfer015,Pocket002,Sketch133,Sketch091,Pad005,Sketch092,Pocket001,Sketch093,Sketch094,Pad006,Sketch095,Pad007,Sketch096,Pad008,Sketch097,Pad009,Chamfer005,Pocket004,Sketch098,Pad010,Chamfer006,Pocket003,SubtractivePipe,SubtractivePipe001,Sketch099,Sketch106,Sketch107,Sketch108,Clone2D,Sketch109,SubtractiveLoft,SubtractiveLoft001,Sketch110,Sketch111,Sketch112,Chamfer016,Chamfer017,+15 more]
  Origin = -> Origin006
  Tip = -> Groove
FEATURE [Sketcher::SketchObject] Sketch153  label="ripieno_per_sostegno_led_batteria"
  ArcFitTolerance = 1e-06
  AttachmentSupport = -> [XZ_Plane]
  ExternalGeometry = -> [Sketch036]
  FullyConstrained = true
  MakeInternals = false
  MapMode = 5
  Placement = pos=(0,0,0) rot=(1,0,0;1.5708rad)
  sketch-geometry (4):
    g0: LineSegment StartX=-217.343 StartY=-54.5944 StartZ=0 EndX=-217.343 EndY=-63.1944 EndZ=0
    g1: LineSegment StartX=-217.343 StartY=-63.1944 StartZ=0 EndX=-211.843 EndY=-63.1944 EndZ=0
    g2: LineSegment StartX=-211.843 StartY=-63.1944 StartZ=0 EndX=-211.843 EndY=-54.5944 EndZ=0
    g3: LineSegment StartX=-211.843 StartY=-54.5944 StartZ=0 EndX=-217.343 EndY=-54.5944 EndZ=0
  constraints (11):
    c: Coincident(g0,g1)
    c: Coincident(g1,g2)
    c: Coincident(g2,g3)
    c: Coincident(g3,g0)
    c: Vertical(g0)
    c: Horizontal(g1)
    c: Horizontal(g3)
    c: Tangent(g2,g-3)
    c: DistanceY(g2,g-3) = 4.5
    c: DistanceX(g3,g3) = 5.5
    c: DistanceY(g0,g0) = 8.6
FEATURE [PartDesign::Body] Body  label="Struttura pistola"
  AllowCompound = false
  Group = -> [Sketch,Sketch002,Sketch004,DatumPlane,Sketch005,DatumPlane001,CopyCut,Sketch008,Sketch009,Sketch010,Sketch011,Sketch012,Sketch013,Sketch014,Sketch015,Sketch016,Sketch017,Sketch018,Sketch019,Sketch020,Sketch022,Sketch023,Sketch024,Sketch025,Sketch026,Sketch027,Sketch029,Sketch030,Sketch031,Sketch032,Sketch033,Sketch034,Sketch035,Sketch036,Sketch037,Sketch038,Sketch039,Sketch040,Sketch041,Sketch042,+28 more]
  Origin = -> Origin
FEATURE [Part::Extrusion] Extrude088  label="Extrude088 - ripieno_per_sostegno_led_batteria"
  Base = -> Sketch153
  Dir = (0,-1,2e-16)
  DirMode = 2
  FaceMakerClass = Part::FaceMakerBullseye
  FaceMakerMode = 3
  LengthFwd = 4
  LengthRev = 0
  Placement = pos=(0,12.6,0) rot=(0,0,1;0rad)
  Solid = true
  Symmetric = false
FEATURE [Part::MultiFuse] Fusion004
  Refine = true
  Shapes = -> [Cut050,Extrude088]
FEATURE [Part::Cut] Cut051
  Base = -> Fusion004
  Refine = true
  Tool = -> Extrude087
FEATURE [Part::Cut] Cut052
  Base = -> Cut051
  Refine = true
  Tool = -> Extrude086
FEATURE [Sketcher::SketchObject] Sketch154
  ArcFitTolerance = 1e-06
  AttachmentSupport = -> [Pad016]
  ExternalGeometry = -> [Binder001]
  FullyConstrained = true
  MakeInternals = false
  MapMode = 5
  Placement = pos=(0,-3.6,0) rot=(1,0,0;1.5708rad)
  sketch-geometry (25):
    g0: LineSegment StartX=-214.643 StartY=-72.4316 StartZ=0 EndX=-212.243 EndY=-72.4316 EndZ=0
    g1: LineSegment StartX=-212.243 StartY=-72.4316 StartZ=0 EndX=-212.243 EndY=-71.2316 EndZ=0
    g2: LineSegment StartX=-212.243 StartY=-71.2316 StartZ=0 EndX=-214.643 EndY=-71.2316 EndZ=0
    g3: LineSegment StartX=-214.643 StartY=-71.2316 StartZ=0 EndX=-214.643 EndY=-72.4316 EndZ=0
    g4: GeomPoint [constr] X=-213.443 Y=-71.8316 Z=0
    g5: LineSegment StartX=-214.643 StartY=-69.6316 StartZ=0 EndX=-212.243 EndY=-69.6316 EndZ=0
    g6: LineSegment StartX=-212.243 StartY=-69.6316 StartZ=0 EndX=-212.243 EndY=-68.4316 EndZ=0
    g7: LineSegment StartX=-212.243 StartY=-68.4316 StartZ=0 EndX=-214.643 EndY=-68.4316 EndZ=0
    g8: LineSegment StartX=-214.643 StartY=-68.4316 StartZ=0 EndX=-214.643 EndY=-69.6316 EndZ=0
    g9: GeomPoint [constr] X=-213.443 Y=-69.0316 Z=0
    g10: LineSegment StartX=-214.643 StartY=-66.8316 StartZ=0 EndX=-212.243 EndY=-66.8316 EndZ=0
    g11: LineSegment StartX=-212.243 StartY=-66.8316 StartZ=0 EndX=-212.243 EndY=-65.6316 EndZ=0
    g12: LineSegment StartX=-212.243 StartY=-65.6316 StartZ=0 EndX=-214.643 EndY=-65.6316 EndZ=0
    g13: LineSegment StartX=-214.643 StartY=-65.6316 StartZ=0 EndX=-214.643 EndY=-66.8316 EndZ=0
    g14: GeomPoint [constr] X=-213.443 Y=-66.2316 Z=0
    g15: LineSegment StartX=-214.643 StartY=-64.0316 StartZ=0 EndX=-212.243 EndY=-64.0316 EndZ=0
    g16: LineSegment StartX=-212.243 StartY=-64.0316 StartZ=0 EndX=-212.243 EndY=-62.8316 EndZ=0
    g17: LineSegment StartX=-212.243 StartY=-62.8316 StartZ=0 EndX=-214.643 EndY=-62.8316 EndZ=0
    g18: LineSegment StartX=-214.643 StartY=-62.8316 StartZ=0 EndX=-214.643 EndY=-64.0316 EndZ=0
    g19: GeomPoint [constr] X=-213.443 Y=-63.4316 Z=0
    g20: LineSegment StartX=-214.643 StartY=-61.2316 StartZ=0 EndX=-212.243 EndY=-61.2316 EndZ=0
    g21: LineSegment StartX=-212.243 StartY=-61.2316 StartZ=0 EndX=-212.243 EndY=-60.0316 EndZ=0
    g22: LineSegment StartX=-212.243 StartY=-60.0316 StartZ=0 EndX=-214.643 EndY=-60.0316 EndZ=0
    g23: LineSegment StartX=-214.643 StartY=-60.0316 StartZ=0 EndX=-214.643 EndY=-61.2316 EndZ=0
    g24: GeomPoint [constr] X=-213.443 Y=-60.6316 Z=0
  constraints (65):
    c: Coincident(g0,g1)
    c: Coincident(g1,g2)
    c: Coincident(g2,g3)
    c: Coincident(g3,g0)
    c: Horizontal(g0)
    c: Horizontal(g2)
    c: Vertical(g1)
    c: Vertical(g3)
    c: Symmetric(g2,g0,g4)
    c: Distance(g1,g3) = 2.4
    c: Distance(g0,g2) = 1.2
    c: Coincident(g5,g6)
    c: Coincident(g6,g7)
    c: Coincident(g7,g8)
    c: Coincident(g8,g5)
    c: Horizontal(g5)
    c: Horizontal(g7)
    c: Vertical(g6)
    c: Vertical(g8)
    c: Symmetric(g7,g5,g9)
    c: Distance(g6,g8) = 2.4
    c: Distance(g5,g7) = 1.2
    c: Coincident(g10,g11)
    c: Coincident(g11,g12)
    c: Coincident(g12,g13)
    c: Coincident(g13,g10)
    c: Horizontal(g10)
    c: Horizontal(g12)
    c: Vertical(g11)
    c: Vertical(g13)
    c: Symmetric(g12,g10,g14)
    c: Distance(g11,g13) = 2.4
    c: Distance(g10,g12) = 1.2
    c: Coincident(g15,g16)
    c: Coincident(g16,g17)
    c: Coincident(g17,g18)
    c: Coincident(g18,g15)
    c: Horizontal(g15)
    c: Horizontal(g17)
    c: Vertical(g16)
    c: Vertical(g18)
    c: Symmetric(g17,g15,g19)
    c: Distance(g16,g18) = 2.4
    c: Distance(g15,g17) = 1.2
    c: Vertical(g4,g-3)
    c: Vertical(g9,g-3)
    c: Vertical(g14,g-3)
    c: Vertical(g19,g-3)
    c: DistanceY(g-3,g4) = 5
    c: DistanceY(g4,g9) = 2.8
    c: DistanceY(g9,g14) = 2.8
    c: DistanceY(g14,g19) = 2.8
    c: Coincident(g20,g21)
    c: Coincident(g21,g22)
    c: Coincident(g22,g23)
    c: Coincident(g23,g20)
    c: Horizontal(g20)
    c: Horizontal(g22)
    c: Vertical(g21)
    c: Vertical(g23)
    c: Symmetric(g22,g20,g24)
    c: Distance(g21,g23) = 2.4
    c: Distance(g20,g22) = 1.2
    c: DistanceY(g19,g24) = 2.8
    c: Vertical(g-3,g24)
FEATURE [PartDesign::Pocket] Pocket020
  BaseFeature = -> Pocket012
  Direction = (0,1,-2e-16)
  Length = 3.6
  Length2 = 5
  Profile = -> Sketch154
  ReferenceAxis = -> Sketch154 [N_Axis]
  Refine = true
  Suppressed = false
  Type = 0
FEATURE [PartDesign::Body] Body007  label="lato DX"
  AllowCompound = false
  Group = -> [Binder001,Sketch114,Pad011,Chamfer014,Sketch115,Pocket006,Sketch116,Pad012,Sketch117,Pocket007,Sketch118,Pad013,Sketch119,Pocket008,Pad017,Chamfer009,Pocket009,Sketch123,Sketch120,Pad014,Pad018,Chamfer008,Pocket010,Sketch121,Pad015,Sketch122,Pad016,SubtractivePipe004,SubtractivePipe005,Sketch149,Sketch148,Sketch124,Sketch125,Sketch126,Sketch129,Sketch130,Clone2D001,Sketch131,SubtractiveLoft002,+13 more]
  Origin = -> Origin007
  Tip = -> Pocket020
note: 2 file-system paths scrubbed to <path> (originals preserved in the JSON sidecar)
